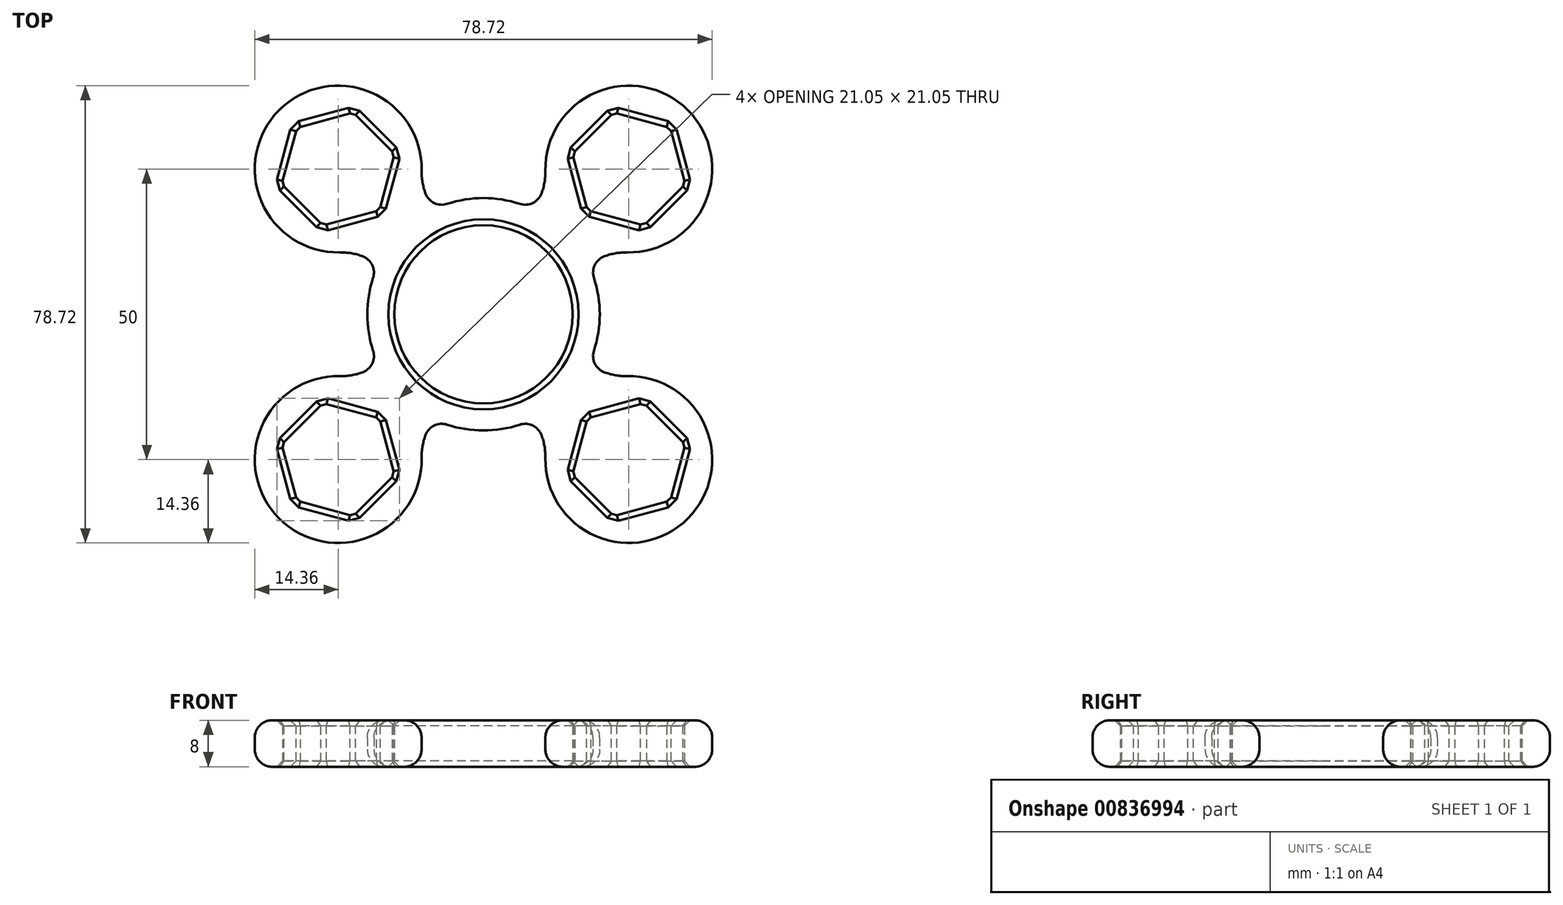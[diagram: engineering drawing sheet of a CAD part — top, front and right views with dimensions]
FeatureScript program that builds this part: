
annotation { "Feature Type Name" : "Feature", "Feature Type Description" : "" }
export const myFeature = defineFeature(function(context is Context, id is Id, definition is map)
    precondition{}
    {
        {
            var Q0;
            Q0=qCreatedBy(makeId("Top.planeOp"),FACE);
            var sketch = newSketch(context, id + "F0", { "sketchPlane" : qUnion([Q0])});
            skCircle(sketch, "E0", {"center": v(0, 0) * mm, "radius": 15.35 * mm});
            skLineSegment(sketch, "E1.1", {"start": v(35.15, -14.85) * mm, "end": v(14.85, -35.15) * mm, "construction": true});
            skLineSegment(sketch, "E1.2", {"start": v(-14.85, -35.15) * mm, "end": v(-35.15, -14.85) * mm, "construction": true});
            skLineSegment(sketch, "E1.3", {"start": v(-35.15, 14.85) * mm, "end": v(-17.9, 32.1) * mm, "construction": true});
            skArc(sketch, "E2", {"start": v(-18.1, 8.51) * mm, "mid": v(-20, 0) * mm, "end": v(-18.1, -8.51) * mm});
            skLineSegment(sketch, "E3", {"start": v(-25, 25) * mm, "end": v(-17.9, 17.9) * mm, "construction": true});
            skLineSegment(sketch, "E4", {"start": v(-25, -25) * mm, "end": v(-17.9, -17.9) * mm, "construction": true});
            skCircle(sketch, "E5.cCircle", {"center": v(-25, 25) * mm, "radius": 10.05 * mm, "construction": true});
            skLineSegment(sketch, "E5.0", {"start": v(-17.9, 17.9) * mm, "end": v(-27.6, 15.3) * mm});
            skLineSegment(sketch, "E5.1", {"start": v(-27.6, 15.3) * mm, "end": v(-34.7, 22.4) * mm});
            skLineSegment(sketch, "E5.2", {"start": v(-34.7, 22.4) * mm, "end": v(-32.1, 32.1) * mm});
            skLineSegment(sketch, "E5.3", {"start": v(-32.1, 32.1) * mm, "end": v(-22.4, 34.7) * mm});
            skLineSegment(sketch, "E5.4", {"start": v(-22.4, 34.7) * mm, "end": v(-15.3, 27.6) * mm});
            skLineSegment(sketch, "E5.5", {"start": v(-15.3, 27.6) * mm, "end": v(-17.9, 17.9) * mm});
            skCircle(sketch, "E6.cCircle", {"center": v(-25, -25) * mm, "radius": 10.05 * mm, "construction": true});
            skLineSegment(sketch, "E6.0", {"start": v(-17.9, -17.9) * mm, "end": v(-15.3, -27.6) * mm});
            skLineSegment(sketch, "E6.1", {"start": v(-15.3, -27.6) * mm, "end": v(-22.4, -34.7) * mm});
            skLineSegment(sketch, "E6.2", {"start": v(-22.4, -34.7) * mm, "end": v(-32.1, -32.1) * mm});
            skLineSegment(sketch, "E6.3", {"start": v(-32.1, -32.1) * mm, "end": v(-34.7, -22.4) * mm});
            skLineSegment(sketch, "E6.4", {"start": v(-34.7, -22.4) * mm, "end": v(-27.6, -15.3) * mm});
            skLineSegment(sketch, "E6.5", {"start": v(-27.6, -15.3) * mm, "end": v(-17.9, -17.9) * mm});
            skCircle(sketch, "E7.cCircle", {"center": v(25, -25) * mm, "radius": 10.05 * mm, "construction": true});
            skLineSegment(sketch, "E7.0", {"start": v(17.9, -17.9) * mm, "end": v(27.6, -15.3) * mm});
            skLineSegment(sketch, "E7.1", {"start": v(27.6, -15.3) * mm, "end": v(34.7, -22.4) * mm});
            skLineSegment(sketch, "E7.2", {"start": v(34.7, -22.4) * mm, "end": v(32.1, -32.1) * mm});
            skLineSegment(sketch, "E7.3", {"start": v(32.1, -32.1) * mm, "end": v(22.4, -34.7) * mm});
            skLineSegment(sketch, "E7.4", {"start": v(22.4, -34.7) * mm, "end": v(15.3, -27.6) * mm});
            skLineSegment(sketch, "E7.5", {"start": v(15.3, -27.6) * mm, "end": v(17.9, -17.9) * mm});
            skArc(sketch, "E8.cCircle", {"start": v(34.7, 22.4) * mm, "mid": v(17.9, 32.1) * mm, "end": v(27.6, 15.3) * mm, "construction": true});
            skLineSegment(sketch, "E8.0", {"start": v(17.9, 17.9) * mm, "end": v(15.3, 27.6) * mm});
            skLineSegment(sketch, "E8.1", {"start": v(15.3, 27.6) * mm, "end": v(22.4, 34.7) * mm});
            skLineSegment(sketch, "E8.2", {"start": v(22.4, 34.7) * mm, "end": v(32.1, 32.1) * mm});
            skLineSegment(sketch, "E8.3", {"start": v(32.1, 32.1) * mm, "end": v(34.7, 22.4) * mm});
            skLineSegment(sketch, "E8.4", {"start": v(34.7, 22.4) * mm, "end": v(27.6, 15.3) * mm});
            skLineSegment(sketch, "E8.5", {"start": v(27.6, 15.3) * mm, "end": v(17.9, 17.9) * mm});
            skArc(sketch, "E9", {"start": v(24.71, 10.65) * mm, "mid": v(35.15, 35.15) * mm, "end": v(10.65, 24.71) * mm});
            skArc(sketch, "E10", {"start": v(10.65, -24.71) * mm, "mid": v(35.15, -35.15) * mm, "end": v(24.71, -10.65) * mm});
            skArc(sketch, "E11", {"start": v(-24.71, -10.65) * mm, "mid": v(-35.15, -35.15) * mm, "end": v(-10.65, -24.71) * mm});
            skArc(sketch, "E12", {"start": v(-10.65, 24.71) * mm, "mid": v(-35.15, 35.15) * mm, "end": v(-24.71, 10.65) * mm});
            skArc(sketch, "E13", {"start": v(8.51, 18.1) * mm, "mid": v(10.13, 21.23) * mm, "end": v(10.65, 24.71) * mm});
            skArc(sketch, "E14", {"start": v(-24.71, -10.65) * mm, "mid": v(-21.23, -10.13) * mm, "end": v(-18.1, -8.51) * mm});
            skArc(sketch, "E15", {"start": v(-8.51, -18.1) * mm, "mid": v(-10.13, -21.23) * mm, "end": v(-10.65, -24.71) * mm});
            skArc(sketch, "E16", {"start": v(24.71, 10.65) * mm, "mid": v(21.23, 10.13) * mm, "end": v(18.1, 8.51) * mm});
            skPoint(sketch, "E17.center.orphan", {"position": v(-50, 0) * mm});
            skPoint(sketch, "E18.orphan", {"position": v(-29, 0) * mm});
            skArc(sketch, "E19.trimOffspring", {"start": v(-18.1, 8.51) * mm, "mid": v(-21.23, 10.13) * mm, "end": v(-24.71, 10.65) * mm});
            skArc(sketch, "E20.trimOffspring", {"start": v(-8.51, -18.1) * mm, "mid": v(0, -20) * mm, "end": v(8.51, -18.1) * mm});
            skPoint(sketch, "E21.start.orphan", {"position": v(0, -29) * mm});
            skPoint(sketch, "E22.center.orphan", {"position": v(0, -50) * mm});
            skArc(sketch, "E23.trimOffspring", {"start": v(10.65, -24.71) * mm, "mid": v(10.13, -21.23) * mm, "end": v(8.51, -18.1) * mm});
            skPoint(sketch, "E24.start.orphan", {"position": v(0, -20) * mm});
            skLineSegment(sketch, "E25.trimOffspring", {"start": v(17.9, -17.9) * mm, "end": v(25, -25) * mm, "construction": true});
            skArc(sketch, "E26.trimOffspring", {"start": v(18.1, -8.51) * mm, "mid": v(20, 0) * mm, "end": v(18.1, 8.51) * mm});
            skArc(sketch, "E27.trimOffspring", {"start": v(-10.65, 24.71) * mm, "mid": v(-10.13, 21.23) * mm, "end": v(-8.51, 18.1) * mm});
            skPoint(sketch, "E28.orphan", {"position": v(0, 29) * mm});
            skPoint(sketch, "E29.start.orphan", {"position": v(0, 20) * mm});
            skPoint(sketch, "E30.center.orphan", {"position": v(0, 50) * mm});
            skArc(sketch, "E31.trimOffspring", {"start": v(8.51, 18.1) * mm, "mid": v(0, 20) * mm, "end": v(-8.51, 18.1) * mm});
            skPoint(sketch, "E32.center.orphan", {"position": v(50, 0) * mm});
            skPoint(sketch, "E33.start.orphan", {"position": v(20, 0) * mm});
            skArc(sketch, "E34.trimOffspring", {"start": v(18.1, -8.51) * mm, "mid": v(21.23, -10.13) * mm, "end": v(24.71, -10.65) * mm});
            skPoint(sketch, "E35.start.orphan", {"position": v(29, 0) * mm});
            skPoint(sketch, "E36.start.orphan", {"position": v(-20, 0) * mm});
            skSolve(sketch);
        }
        {
            var Q0;
            Q0 = qSketchRegion(id + "F0", true);
            extrude(context, id + "F1", {"entities" : qUnion([Q0]), "depth" : 8 * mm, "offsetDistance" : 25 * mm});
        }
        {
            var Q0;
            Q0=makeQuery(id+"F1.opExtrude","CAP_EDGE",EDGE,{"disambiguationData":[OSD([sQuery(id+"F0.wireOp",EDGE,"E12")])],"isStart":false});
            var Q1;
            Q1=makeQuery(id+"F1.opExtrude","CAP_EDGE",EDGE,{"disambiguationData":[OSD([sQuery(id+"F0.wireOp",EDGE,"E11")])],"isStart":false});
            var Q2;
            Q2=makeQuery(id+"F1.opExtrude","CAP_EDGE",EDGE,{"disambiguationData":[OSD([sQuery(id+"F0.wireOp",EDGE,"E10")])],"isStart":false});
            var Q3;
            Q3=makeQuery(id+"F1.opExtrude","CAP_EDGE",EDGE,{"disambiguationData":[OSD([sQuery(id+"F0.wireOp",EDGE,"E9")])],"isStart":false});
            var Q4;
            Q4=makeQuery(id+"F1.opExtrude","CAP_EDGE",EDGE,{"disambiguationData":[OSD([sQuery(id+"F0.wireOp",EDGE,"E26.trimOffspring")])],"isStart":false});
            var Q5;
            Q5=makeQuery(id+"F1.opExtrude","CAP_EDGE",EDGE,{"disambiguationData":[OSD([sQuery(id+"F0.wireOp",EDGE,"E31.trimOffspring")])],"isStart":false});
            var Q6;
            Q6=makeQuery(id+"F1.opExtrude","CAP_EDGE",EDGE,{"disambiguationData":[OSD([sQuery(id+"F0.wireOp",EDGE,"E2")])],"isStart":false});
            var Q7;
            Q7=makeQuery(id+"F1.opExtrude","CAP_EDGE",EDGE,{"disambiguationData":[OSD([sQuery(id+"F0.wireOp",EDGE,"E20.trimOffspring")])],"isStart":true});
            var Q8;
            Q8=makeQuery(id+"F1.opExtrude","CAP_EDGE",EDGE,{"disambiguationData":[OSD([sQuery(id+"F0.wireOp",EDGE,"E20.trimOffspring")])],"isStart":false});
            var Q9;
            Q9=makeQuery(id+"F1.opExtrude","CAP_EDGE",EDGE,{"disambiguationData":[OSD([sQuery(id+"F0.wireOp",EDGE,"E11")])],"isStart":true});
            var Q10;
            Q10=makeQuery(id+"F1.opExtrude","CAP_EDGE",EDGE,{"disambiguationData":[OSD([sQuery(id+"F0.wireOp",EDGE,"E2")])],"isStart":true});
            var Q11;
            Q11=makeQuery(id+"F1.opExtrude","CAP_EDGE",EDGE,{"disambiguationData":[OSD([sQuery(id+"F0.wireOp",EDGE,"E12")])],"isStart":true});
            var Q12;
            Q12=makeQuery(id+"F1.opExtrude","SWEPT_EDGE",EDGE,{"disambiguationData":[OSD([sQuery(id+"F0.wireOp",EDGE,"E2"),sQuery(id+"F0.wireOp",EDGE,"E14")])]});
            var Q13;
            Q13=makeQuery(id+"F1.opExtrude","SWEPT_EDGE",EDGE,{"disambiguationData":[OSD([sQuery(id+"F0.wireOp",EDGE,"E2"),sQuery(id+"F0.wireOp",EDGE,"E19.trimOffspring")])]});
            var Q14;
            Q14=makeQuery(id+"F1.opExtrude","CAP_EDGE",EDGE,{"disambiguationData":[OSD([sQuery(id+"F0.wireOp",EDGE,"E9")])],"isStart":true});
            var Q15;
            Q15=makeQuery(id+"F1.opExtrude","CAP_EDGE",EDGE,{"disambiguationData":[OSD([sQuery(id+"F0.wireOp",EDGE,"E10")])],"isStart":true});
            var Q16;
            Q16=makeQuery(id+"F1.opExtrude","CAP_EDGE",EDGE,{"disambiguationData":[OSD([sQuery(id+"F0.wireOp",EDGE,"E26.trimOffspring")])],"isStart":true});
            var Q17;
            Q17=makeQuery(id+"F1.opExtrude","CAP_EDGE",EDGE,{"disambiguationData":[OSD([sQuery(id+"F0.wireOp",EDGE,"E31.trimOffspring")])],"isStart":true});
            var Q18;
            Q18=makeQuery(id+"F1.opExtrude","SWEPT_EDGE",EDGE,{"disambiguationData":[OSD([sQuery(id+"F0.wireOp",EDGE,"E13"),sQuery(id+"F0.wireOp",EDGE,"E31.trimOffspring")])]});
            var Q19;
            Q19=makeQuery(id+"F1.opExtrude","SWEPT_EDGE",EDGE,{"disambiguationData":[OSD([sQuery(id+"F0.wireOp",EDGE,"E16"),sQuery(id+"F0.wireOp",EDGE,"E26.trimOffspring")])]});
            var Q20;
            Q20=makeQuery(id+"F1.opExtrude","SWEPT_EDGE",EDGE,{"disambiguationData":[OSD([sQuery(id+"F0.wireOp",EDGE,"E26.trimOffspring"),sQuery(id+"F0.wireOp",EDGE,"E34.trimOffspring")])]});
            var Q21;
            Q21=makeQuery(id+"F1.opExtrude","SWEPT_EDGE",EDGE,{"disambiguationData":[OSD([sQuery(id+"F0.wireOp",EDGE,"E20.trimOffspring"),sQuery(id+"F0.wireOp",EDGE,"E23.trimOffspring")])]});
            var Q22;
            Q22=makeQuery(id+"F1.opExtrude","SWEPT_EDGE",EDGE,{"disambiguationData":[OSD([sQuery(id+"F0.wireOp",EDGE,"E15"),sQuery(id+"F0.wireOp",EDGE,"E20.trimOffspring")])]});
            var Q23;
            Q23=makeQuery(id+"F1.opExtrude","SWEPT_EDGE",EDGE,{"disambiguationData":[OSD([sQuery(id+"F0.wireOp",EDGE,"E27.trimOffspring"),sQuery(id+"F0.wireOp",EDGE,"E31.trimOffspring")])]});
            fillet(context, id + "F2", {"entities" : qUnion([Q0, Q1, Q2, Q3, Q4, Q5, Q6, Q7, Q8, Q9, Q10, Q11, Q12, Q13, Q14, Q15, Q16, Q17, Q18, Q19, Q20, Q21, Q22, Q23]), "radius" : 3 * mm, "tangentPropagation" : true, "allowEdgeOverflow" : false});
        }
        {
            var Q0;
            Q0=makeQuery(id+"F1.opExtrude","CAP_EDGE",EDGE,{"disambiguationData":[OSD([sQuery(id+"F0.wireOp",EDGE,"E5.2")])],"isStart":false});
            var Q1;
            Q1=makeQuery(id+"F1.opExtrude","CAP_EDGE",EDGE,{"disambiguationData":[OSD([sQuery(id+"F0.wireOp",EDGE,"E5.3")])],"isStart":false});
            var Q2;
            Q2=makeQuery(id+"F1.opExtrude","CAP_EDGE",EDGE,{"disambiguationData":[OSD([sQuery(id+"F0.wireOp",EDGE,"E5.4")])],"isStart":false});
            var Q3;
            Q3=makeQuery(id+"F1.opExtrude","CAP_EDGE",EDGE,{"disambiguationData":[OSD([sQuery(id+"F0.wireOp",EDGE,"E5.5")])],"isStart":false});
            var Q4;
            Q4=makeQuery(id+"F1.opExtrude","CAP_EDGE",EDGE,{"disambiguationData":[OSD([sQuery(id+"F0.wireOp",EDGE,"E5.0")])],"isStart":false});
            var Q5;
            Q5=makeQuery(id+"F1.opExtrude","CAP_EDGE",EDGE,{"disambiguationData":[OSD([sQuery(id+"F0.wireOp",EDGE,"E5.1")])],"isStart":false});
            var Q6;
            Q6=makeQuery(id+"F1.opExtrude","CAP_EDGE",EDGE,{"disambiguationData":[OSD([sQuery(id+"F0.wireOp",EDGE,"E8.0")])],"isStart":false});
            var Q7;
            Q7=makeQuery(id+"F1.opExtrude","CAP_EDGE",EDGE,{"disambiguationData":[OSD([sQuery(id+"F0.wireOp",EDGE,"E8.1")])],"isStart":false});
            var Q8;
            Q8=makeQuery(id+"F1.opExtrude","CAP_EDGE",EDGE,{"disambiguationData":[OSD([sQuery(id+"F0.wireOp",EDGE,"E8.2")])],"isStart":false});
            var Q9;
            Q9=makeQuery(id+"F1.opExtrude","CAP_EDGE",EDGE,{"disambiguationData":[OSD([sQuery(id+"F0.wireOp",EDGE,"E8.3")])],"isStart":false});
            var Q10;
            Q10=makeQuery(id+"F1.opExtrude","CAP_EDGE",EDGE,{"disambiguationData":[OSD([sQuery(id+"F0.wireOp",EDGE,"E8.4")])],"isStart":false});
            var Q11;
            Q11=makeQuery(id+"F1.opExtrude","CAP_EDGE",EDGE,{"disambiguationData":[OSD([sQuery(id+"F0.wireOp",EDGE,"E8.5")])],"isStart":false});
            var Q12;
            Q12=makeQuery(id+"F1.opExtrude","CAP_EDGE",EDGE,{"disambiguationData":[OSD([sQuery(id+"F0.wireOp",EDGE,"E0")])],"isStart":false});
            var Q13;
            Q13=makeQuery(id+"F1.opExtrude","CAP_EDGE",EDGE,{"disambiguationData":[OSD([sQuery(id+"F0.wireOp",EDGE,"E7.0")])],"isStart":false});
            var Q14;
            Q14=makeQuery(id+"F1.opExtrude","CAP_EDGE",EDGE,{"disambiguationData":[OSD([sQuery(id+"F0.wireOp",EDGE,"E7.5")])],"isStart":false});
            var Q15;
            Q15=makeQuery(id+"F1.opExtrude","CAP_EDGE",EDGE,{"disambiguationData":[OSD([sQuery(id+"F0.wireOp",EDGE,"E7.4")])],"isStart":false});
            var Q16;
            Q16=makeQuery(id+"F1.opExtrude","CAP_EDGE",EDGE,{"disambiguationData":[OSD([sQuery(id+"F0.wireOp",EDGE,"E7.3")])],"isStart":false});
            var Q17;
            Q17=makeQuery(id+"F1.opExtrude","CAP_EDGE",EDGE,{"disambiguationData":[OSD([sQuery(id+"F0.wireOp",EDGE,"E7.2")])],"isStart":false});
            var Q18;
            Q18=makeQuery(id+"F1.opExtrude","CAP_EDGE",EDGE,{"disambiguationData":[OSD([sQuery(id+"F0.wireOp",EDGE,"E7.1")])],"isStart":false});
            var Q19;
            Q19=makeQuery(id+"F1.opExtrude","CAP_EDGE",EDGE,{"disambiguationData":[OSD([sQuery(id+"F0.wireOp",EDGE,"E6.5")])],"isStart":false});
            var Q20;
            Q20=makeQuery(id+"F1.opExtrude","CAP_EDGE",EDGE,{"disambiguationData":[OSD([sQuery(id+"F0.wireOp",EDGE,"E6.0")])],"isStart":false});
            var Q21;
            Q21=makeQuery(id+"F1.opExtrude","CAP_EDGE",EDGE,{"disambiguationData":[OSD([sQuery(id+"F0.wireOp",EDGE,"E6.4")])],"isStart":false});
            var Q22;
            Q22=makeQuery(id+"F1.opExtrude","CAP_EDGE",EDGE,{"disambiguationData":[OSD([sQuery(id+"F0.wireOp",EDGE,"E6.3")])],"isStart":false});
            var Q23;
            Q23=makeQuery(id+"F1.opExtrude","CAP_EDGE",EDGE,{"disambiguationData":[OSD([sQuery(id+"F0.wireOp",EDGE,"E6.2")])],"isStart":false});
            var Q24;
            Q24=makeQuery(id+"F1.opExtrude","CAP_EDGE",EDGE,{"disambiguationData":[OSD([sQuery(id+"F0.wireOp",EDGE,"E6.1")])],"isStart":false});
            var Q25;
            Q25=makeQuery(id+"F1.opExtrude","CAP_EDGE",EDGE,{"disambiguationData":[OSD([sQuery(id+"F0.wireOp",EDGE,"E7.0")])],"isStart":true});
            var Q26;
            Q26=makeQuery(id+"F1.opExtrude","CAP_EDGE",EDGE,{"disambiguationData":[OSD([sQuery(id+"F0.wireOp",EDGE,"E7.5")])],"isStart":true});
            var Q27;
            Q27=makeQuery(id+"F1.opExtrude","CAP_EDGE",EDGE,{"disambiguationData":[OSD([sQuery(id+"F0.wireOp",EDGE,"E7.4")])],"isStart":true});
            var Q28;
            Q28=makeQuery(id+"F1.opExtrude","CAP_EDGE",EDGE,{"disambiguationData":[OSD([sQuery(id+"F0.wireOp",EDGE,"E7.3")])],"isStart":true});
            var Q29;
            Q29=makeQuery(id+"F1.opExtrude","CAP_EDGE",EDGE,{"disambiguationData":[OSD([sQuery(id+"F0.wireOp",EDGE,"E7.2")])],"isStart":true});
            var Q30;
            Q30=makeQuery(id+"F1.opExtrude","CAP_EDGE",EDGE,{"disambiguationData":[OSD([sQuery(id+"F0.wireOp",EDGE,"E7.1")])],"isStart":true});
            var Q31;
            Q31=makeQuery(id+"F1.opExtrude","CAP_EDGE",EDGE,{"disambiguationData":[OSD([sQuery(id+"F0.wireOp",EDGE,"E8.4")])],"isStart":true});
            var Q32;
            Q32=makeQuery(id+"F1.opExtrude","CAP_EDGE",EDGE,{"disambiguationData":[OSD([sQuery(id+"F0.wireOp",EDGE,"E8.5")])],"isStart":true});
            var Q33;
            Q33=makeQuery(id+"F1.opExtrude","CAP_EDGE",EDGE,{"disambiguationData":[OSD([sQuery(id+"F0.wireOp",EDGE,"E8.0")])],"isStart":true});
            var Q34;
            Q34=makeQuery(id+"F1.opExtrude","CAP_EDGE",EDGE,{"disambiguationData":[OSD([sQuery(id+"F0.wireOp",EDGE,"E8.1")])],"isStart":true});
            var Q35;
            Q35=makeQuery(id+"F1.opExtrude","CAP_EDGE",EDGE,{"disambiguationData":[OSD([sQuery(id+"F0.wireOp",EDGE,"E8.2")])],"isStart":true});
            var Q36;
            Q36=makeQuery(id+"F1.opExtrude","CAP_EDGE",EDGE,{"disambiguationData":[OSD([sQuery(id+"F0.wireOp",EDGE,"E8.3")])],"isStart":true});
            var Q37;
            Q37=makeQuery(id+"F1.opExtrude","CAP_EDGE",EDGE,{"disambiguationData":[OSD([sQuery(id+"F0.wireOp",EDGE,"E5.0")])],"isStart":true});
            var Q38;
            Q38=makeQuery(id+"F1.opExtrude","CAP_EDGE",EDGE,{"disambiguationData":[OSD([sQuery(id+"F0.wireOp",EDGE,"E5.5")])],"isStart":true});
            var Q39;
            Q39=makeQuery(id+"F1.opExtrude","CAP_EDGE",EDGE,{"disambiguationData":[OSD([sQuery(id+"F0.wireOp",EDGE,"E5.4")])],"isStart":true});
            var Q40;
            Q40=makeQuery(id+"F1.opExtrude","CAP_EDGE",EDGE,{"disambiguationData":[OSD([sQuery(id+"F0.wireOp",EDGE,"E5.3")])],"isStart":true});
            var Q41;
            Q41=makeQuery(id+"F1.opExtrude","CAP_EDGE",EDGE,{"disambiguationData":[OSD([sQuery(id+"F0.wireOp",EDGE,"E5.2")])],"isStart":true});
            var Q42;
            Q42=makeQuery(id+"F1.opExtrude","CAP_EDGE",EDGE,{"disambiguationData":[OSD([sQuery(id+"F0.wireOp",EDGE,"E5.1")])],"isStart":true});
            var Q43;
            Q43=makeQuery(id+"F1.opExtrude","CAP_EDGE",EDGE,{"disambiguationData":[OSD([sQuery(id+"F0.wireOp",EDGE,"E0")])],"isStart":true});
            var Q44;
            Q44=makeQuery(id+"F1.opExtrude","CAP_EDGE",EDGE,{"disambiguationData":[OSD([sQuery(id+"F0.wireOp",EDGE,"E6.5")])],"isStart":true});
            var Q45;
            Q45=makeQuery(id+"F1.opExtrude","CAP_EDGE",EDGE,{"disambiguationData":[OSD([sQuery(id+"F0.wireOp",EDGE,"E6.4")])],"isStart":true});
            var Q46;
            Q46=makeQuery(id+"F1.opExtrude","CAP_EDGE",EDGE,{"disambiguationData":[OSD([sQuery(id+"F0.wireOp",EDGE,"E6.3")])],"isStart":true});
            var Q47;
            Q47=makeQuery(id+"F1.opExtrude","CAP_EDGE",EDGE,{"disambiguationData":[OSD([sQuery(id+"F0.wireOp",EDGE,"E6.2")])],"isStart":true});
            var Q48;
            Q48=makeQuery(id+"F1.opExtrude","CAP_EDGE",EDGE,{"disambiguationData":[OSD([sQuery(id+"F0.wireOp",EDGE,"E6.1")])],"isStart":true});
            var Q49;
            Q49=makeQuery(id+"F1.opExtrude","CAP_EDGE",EDGE,{"disambiguationData":[OSD([sQuery(id+"F0.wireOp",EDGE,"E6.0")])],"isStart":true});
            var Q50;
            {var subQ0=sQuery(id+"F0.wireOp",EDGE,"E9");Q50=makeQuery(id+"F2.opFillet","BLEND_EDGE",EDGE,{"blendedFrom":[makeQuery(id+"F1.opExtrude","CAP_EDGE",EDGE,{"disambiguationData":[OSD([subQ0])],"isStart":true}),makeQuery(id+"F1.opExtrude","CAP_FACE",FACE,{"disambiguationData":[OSD([sQuery(id+"F0.wireOp",EDGE,"E0"),sQuery(id+"F0.wireOp",EDGE,"E2"),sQuery(id+"F0.wireOp",EDGE,"E5.0"),sQuery(id+"F0.wireOp",EDGE,"E5.1"),sQuery(id+"F0.wireOp",EDGE,"E5.2"),sQuery(id+"F0.wireOp",EDGE,"E5.3"),sQuery(id+"F0.wireOp",EDGE,"E5.4"),sQuery(id+"F0.wireOp",EDGE,"E5.5"),sQuery(id+"F0.wireOp",EDGE,"E6.0"),sQuery(id+"F0.wireOp",EDGE,"E6.1"),sQuery(id+"F0.wireOp",EDGE,"E6.2"),sQuery(id+"F0.wireOp",EDGE,"E6.3"),sQuery(id+"F0.wireOp",EDGE,"E6.4"),sQuery(id+"F0.wireOp",EDGE,"E6.5"),sQuery(id+"F0.wireOp",EDGE,"E7.0"),sQuery(id+"F0.wireOp",EDGE,"E7.1"),sQuery(id+"F0.wireOp",EDGE,"E7.2"),sQuery(id+"F0.wireOp",EDGE,"E7.3"),sQuery(id+"F0.wireOp",EDGE,"E7.4"),sQuery(id+"F0.wireOp",EDGE,"E7.5"),sQuery(id+"F0.wireOp",EDGE,"E8.0"),sQuery(id+"F0.wireOp",EDGE,"E8.1"),sQuery(id+"F0.wireOp",EDGE,"E8.2"),sQuery(id+"F0.wireOp",EDGE,"E8.3"),sQuery(id+"F0.wireOp",EDGE,"E8.4"),sQuery(id+"F0.wireOp",EDGE,"E8.5"),subQ0,sQuery(id+"F0.wireOp",EDGE,"E10"),sQuery(id+"F0.wireOp",EDGE,"E11"),sQuery(id+"F0.wireOp",EDGE,"E12"),sQuery(id+"F0.wireOp",EDGE,"E13"),sQuery(id+"F0.wireOp",EDGE,"E14"),sQuery(id+"F0.wireOp",EDGE,"E15"),sQuery(id+"F0.wireOp",EDGE,"E16"),sQuery(id+"F0.wireOp",EDGE,"E19.trimOffspring"),sQuery(id+"F0.wireOp",EDGE,"E20.trimOffspring"),sQuery(id+"F0.wireOp",EDGE,"E23.trimOffspring"),sQuery(id+"F0.wireOp",EDGE,"E26.trimOffspring"),sQuery(id+"F0.wireOp",EDGE,"E27.trimOffspring"),sQuery(id+"F0.wireOp",EDGE,"E31.trimOffspring"),sQuery(id+"F0.wireOp",EDGE,"E34.trimOffspring")])],"isStart":true})],"blendedInto":[makeQuery(id+"F1.opExtrude","CAP_FACE",FACE,{"disambiguationData":[OSD([sQuery(id+"F0.wireOp",EDGE,"E0"),sQuery(id+"F0.wireOp",EDGE,"E2"),sQuery(id+"F0.wireOp",EDGE,"E5.0"),sQuery(id+"F0.wireOp",EDGE,"E5.1"),sQuery(id+"F0.wireOp",EDGE,"E5.2"),sQuery(id+"F0.wireOp",EDGE,"E5.3"),sQuery(id+"F0.wireOp",EDGE,"E5.4"),sQuery(id+"F0.wireOp",EDGE,"E5.5"),sQuery(id+"F0.wireOp",EDGE,"E6.0"),sQuery(id+"F0.wireOp",EDGE,"E6.1"),sQuery(id+"F0.wireOp",EDGE,"E6.2"),sQuery(id+"F0.wireOp",EDGE,"E6.3"),sQuery(id+"F0.wireOp",EDGE,"E6.4"),sQuery(id+"F0.wireOp",EDGE,"E6.5"),sQuery(id+"F0.wireOp",EDGE,"E7.0"),sQuery(id+"F0.wireOp",EDGE,"E7.1"),sQuery(id+"F0.wireOp",EDGE,"E7.2"),sQuery(id+"F0.wireOp",EDGE,"E7.3"),sQuery(id+"F0.wireOp",EDGE,"E7.4"),sQuery(id+"F0.wireOp",EDGE,"E7.5"),sQuery(id+"F0.wireOp",EDGE,"E8.0"),sQuery(id+"F0.wireOp",EDGE,"E8.1"),sQuery(id+"F0.wireOp",EDGE,"E8.2"),sQuery(id+"F0.wireOp",EDGE,"E8.3"),sQuery(id+"F0.wireOp",EDGE,"E8.4"),sQuery(id+"F0.wireOp",EDGE,"E8.5"),subQ0,sQuery(id+"F0.wireOp",EDGE,"E10"),sQuery(id+"F0.wireOp",EDGE,"E11"),sQuery(id+"F0.wireOp",EDGE,"E12"),sQuery(id+"F0.wireOp",EDGE,"E13"),sQuery(id+"F0.wireOp",EDGE,"E14"),sQuery(id+"F0.wireOp",EDGE,"E15"),sQuery(id+"F0.wireOp",EDGE,"E16"),sQuery(id+"F0.wireOp",EDGE,"E19.trimOffspring"),sQuery(id+"F0.wireOp",EDGE,"E20.trimOffspring"),sQuery(id+"F0.wireOp",EDGE,"E23.trimOffspring"),sQuery(id+"F0.wireOp",EDGE,"E26.trimOffspring"),sQuery(id+"F0.wireOp",EDGE,"E27.trimOffspring"),sQuery(id+"F0.wireOp",EDGE,"E31.trimOffspring"),sQuery(id+"F0.wireOp",EDGE,"E34.trimOffspring")])],"isStart":true})]});}
            var Q51;
            {var subQ0=sQuery(id+"F0.wireOp",EDGE,"E9");Q51=makeQuery(id+"F2.opFillet","BLEND_EDGE",EDGE,{"blendedFrom":[makeQuery(id+"F1.opExtrude","CAP_EDGE",EDGE,{"disambiguationData":[OSD([subQ0])],"isStart":true}),makeQuery(id+"F1.opExtrude","SWEPT_FACE",FACE,{"disambiguationData":[OSD([subQ0])]})],"blendedInto":[makeQuery(id+"F1.opExtrude","SWEPT_FACE",FACE,{"disambiguationData":[OSD([subQ0])]})]});}
            var Q52;
            {var subQ0=sQuery(id+"F0.wireOp",EDGE,"E11");Q52=makeQuery(id+"F2.opFillet","BLEND_EDGE",EDGE,{"blendedFrom":[makeQuery(id+"F1.opExtrude","CAP_EDGE",EDGE,{"disambiguationData":[OSD([subQ0])],"isStart":true}),makeQuery(id+"F1.opExtrude","SWEPT_FACE",FACE,{"disambiguationData":[OSD([subQ0])]})],"blendedInto":[makeQuery(id+"F1.opExtrude","SWEPT_FACE",FACE,{"disambiguationData":[OSD([subQ0])]})]});}
            var Q53;
            {var subQ0=sQuery(id+"F0.wireOp",EDGE,"E11");Q53=makeQuery(id+"F2.opFillet","BLEND_EDGE",EDGE,{"blendedFrom":[makeQuery(id+"F1.opExtrude","CAP_EDGE",EDGE,{"disambiguationData":[OSD([subQ0])],"isStart":true}),makeQuery(id+"F1.opExtrude","CAP_FACE",FACE,{"disambiguationData":[OSD([sQuery(id+"F0.wireOp",EDGE,"E0"),sQuery(id+"F0.wireOp",EDGE,"E2"),sQuery(id+"F0.wireOp",EDGE,"E5.0"),sQuery(id+"F0.wireOp",EDGE,"E5.1"),sQuery(id+"F0.wireOp",EDGE,"E5.2"),sQuery(id+"F0.wireOp",EDGE,"E5.3"),sQuery(id+"F0.wireOp",EDGE,"E5.4"),sQuery(id+"F0.wireOp",EDGE,"E5.5"),sQuery(id+"F0.wireOp",EDGE,"E6.0"),sQuery(id+"F0.wireOp",EDGE,"E6.1"),sQuery(id+"F0.wireOp",EDGE,"E6.2"),sQuery(id+"F0.wireOp",EDGE,"E6.3"),sQuery(id+"F0.wireOp",EDGE,"E6.4"),sQuery(id+"F0.wireOp",EDGE,"E6.5"),sQuery(id+"F0.wireOp",EDGE,"E7.0"),sQuery(id+"F0.wireOp",EDGE,"E7.1"),sQuery(id+"F0.wireOp",EDGE,"E7.2"),sQuery(id+"F0.wireOp",EDGE,"E7.3"),sQuery(id+"F0.wireOp",EDGE,"E7.4"),sQuery(id+"F0.wireOp",EDGE,"E7.5"),sQuery(id+"F0.wireOp",EDGE,"E8.0"),sQuery(id+"F0.wireOp",EDGE,"E8.1"),sQuery(id+"F0.wireOp",EDGE,"E8.2"),sQuery(id+"F0.wireOp",EDGE,"E8.3"),sQuery(id+"F0.wireOp",EDGE,"E8.4"),sQuery(id+"F0.wireOp",EDGE,"E8.5"),sQuery(id+"F0.wireOp",EDGE,"E9"),sQuery(id+"F0.wireOp",EDGE,"E10"),subQ0,sQuery(id+"F0.wireOp",EDGE,"E12"),sQuery(id+"F0.wireOp",EDGE,"E13"),sQuery(id+"F0.wireOp",EDGE,"E14"),sQuery(id+"F0.wireOp",EDGE,"E15"),sQuery(id+"F0.wireOp",EDGE,"E16"),sQuery(id+"F0.wireOp",EDGE,"E19.trimOffspring"),sQuery(id+"F0.wireOp",EDGE,"E20.trimOffspring"),sQuery(id+"F0.wireOp",EDGE,"E23.trimOffspring"),sQuery(id+"F0.wireOp",EDGE,"E26.trimOffspring"),sQuery(id+"F0.wireOp",EDGE,"E27.trimOffspring"),sQuery(id+"F0.wireOp",EDGE,"E31.trimOffspring"),sQuery(id+"F0.wireOp",EDGE,"E34.trimOffspring")])],"isStart":true})],"blendedInto":[makeQuery(id+"F1.opExtrude","CAP_FACE",FACE,{"disambiguationData":[OSD([sQuery(id+"F0.wireOp",EDGE,"E0"),sQuery(id+"F0.wireOp",EDGE,"E2"),sQuery(id+"F0.wireOp",EDGE,"E5.0"),sQuery(id+"F0.wireOp",EDGE,"E5.1"),sQuery(id+"F0.wireOp",EDGE,"E5.2"),sQuery(id+"F0.wireOp",EDGE,"E5.3"),sQuery(id+"F0.wireOp",EDGE,"E5.4"),sQuery(id+"F0.wireOp",EDGE,"E5.5"),sQuery(id+"F0.wireOp",EDGE,"E6.0"),sQuery(id+"F0.wireOp",EDGE,"E6.1"),sQuery(id+"F0.wireOp",EDGE,"E6.2"),sQuery(id+"F0.wireOp",EDGE,"E6.3"),sQuery(id+"F0.wireOp",EDGE,"E6.4"),sQuery(id+"F0.wireOp",EDGE,"E6.5"),sQuery(id+"F0.wireOp",EDGE,"E7.0"),sQuery(id+"F0.wireOp",EDGE,"E7.1"),sQuery(id+"F0.wireOp",EDGE,"E7.2"),sQuery(id+"F0.wireOp",EDGE,"E7.3"),sQuery(id+"F0.wireOp",EDGE,"E7.4"),sQuery(id+"F0.wireOp",EDGE,"E7.5"),sQuery(id+"F0.wireOp",EDGE,"E8.0"),sQuery(id+"F0.wireOp",EDGE,"E8.1"),sQuery(id+"F0.wireOp",EDGE,"E8.2"),sQuery(id+"F0.wireOp",EDGE,"E8.3"),sQuery(id+"F0.wireOp",EDGE,"E8.4"),sQuery(id+"F0.wireOp",EDGE,"E8.5"),sQuery(id+"F0.wireOp",EDGE,"E9"),sQuery(id+"F0.wireOp",EDGE,"E10"),subQ0,sQuery(id+"F0.wireOp",EDGE,"E12"),sQuery(id+"F0.wireOp",EDGE,"E13"),sQuery(id+"F0.wireOp",EDGE,"E14"),sQuery(id+"F0.wireOp",EDGE,"E15"),sQuery(id+"F0.wireOp",EDGE,"E16"),sQuery(id+"F0.wireOp",EDGE,"E19.trimOffspring"),sQuery(id+"F0.wireOp",EDGE,"E20.trimOffspring"),sQuery(id+"F0.wireOp",EDGE,"E23.trimOffspring"),sQuery(id+"F0.wireOp",EDGE,"E26.trimOffspring"),sQuery(id+"F0.wireOp",EDGE,"E27.trimOffspring"),sQuery(id+"F0.wireOp",EDGE,"E31.trimOffspring"),sQuery(id+"F0.wireOp",EDGE,"E34.trimOffspring")])],"isStart":true})]});}
            var Q54;
            {var subQ0=sQuery(id+"F0.wireOp",EDGE,"E11");Q54=makeQuery(id+"F2.opFillet","BLEND_EDGE",EDGE,{"blendedFrom":[makeQuery(id+"F1.opExtrude","CAP_EDGE",EDGE,{"disambiguationData":[OSD([subQ0])],"isStart":false}),makeQuery(id+"F1.opExtrude","CAP_FACE",FACE,{"disambiguationData":[OSD([sQuery(id+"F0.wireOp",EDGE,"E0"),sQuery(id+"F0.wireOp",EDGE,"E2"),sQuery(id+"F0.wireOp",EDGE,"E5.0"),sQuery(id+"F0.wireOp",EDGE,"E5.1"),sQuery(id+"F0.wireOp",EDGE,"E5.2"),sQuery(id+"F0.wireOp",EDGE,"E5.3"),sQuery(id+"F0.wireOp",EDGE,"E5.4"),sQuery(id+"F0.wireOp",EDGE,"E5.5"),sQuery(id+"F0.wireOp",EDGE,"E6.0"),sQuery(id+"F0.wireOp",EDGE,"E6.1"),sQuery(id+"F0.wireOp",EDGE,"E6.2"),sQuery(id+"F0.wireOp",EDGE,"E6.3"),sQuery(id+"F0.wireOp",EDGE,"E6.4"),sQuery(id+"F0.wireOp",EDGE,"E6.5"),sQuery(id+"F0.wireOp",EDGE,"E7.0"),sQuery(id+"F0.wireOp",EDGE,"E7.1"),sQuery(id+"F0.wireOp",EDGE,"E7.2"),sQuery(id+"F0.wireOp",EDGE,"E7.3"),sQuery(id+"F0.wireOp",EDGE,"E7.4"),sQuery(id+"F0.wireOp",EDGE,"E7.5"),sQuery(id+"F0.wireOp",EDGE,"E8.0"),sQuery(id+"F0.wireOp",EDGE,"E8.1"),sQuery(id+"F0.wireOp",EDGE,"E8.2"),sQuery(id+"F0.wireOp",EDGE,"E8.3"),sQuery(id+"F0.wireOp",EDGE,"E8.4"),sQuery(id+"F0.wireOp",EDGE,"E8.5"),sQuery(id+"F0.wireOp",EDGE,"E9"),sQuery(id+"F0.wireOp",EDGE,"E10"),subQ0,sQuery(id+"F0.wireOp",EDGE,"E12"),sQuery(id+"F0.wireOp",EDGE,"E13"),sQuery(id+"F0.wireOp",EDGE,"E14"),sQuery(id+"F0.wireOp",EDGE,"E15"),sQuery(id+"F0.wireOp",EDGE,"E16"),sQuery(id+"F0.wireOp",EDGE,"E19.trimOffspring"),sQuery(id+"F0.wireOp",EDGE,"E20.trimOffspring"),sQuery(id+"F0.wireOp",EDGE,"E23.trimOffspring"),sQuery(id+"F0.wireOp",EDGE,"E26.trimOffspring"),sQuery(id+"F0.wireOp",EDGE,"E27.trimOffspring"),sQuery(id+"F0.wireOp",EDGE,"E31.trimOffspring"),sQuery(id+"F0.wireOp",EDGE,"E34.trimOffspring")])],"isStart":false})],"blendedInto":[makeQuery(id+"F1.opExtrude","CAP_FACE",FACE,{"disambiguationData":[OSD([sQuery(id+"F0.wireOp",EDGE,"E0"),sQuery(id+"F0.wireOp",EDGE,"E2"),sQuery(id+"F0.wireOp",EDGE,"E5.0"),sQuery(id+"F0.wireOp",EDGE,"E5.1"),sQuery(id+"F0.wireOp",EDGE,"E5.2"),sQuery(id+"F0.wireOp",EDGE,"E5.3"),sQuery(id+"F0.wireOp",EDGE,"E5.4"),sQuery(id+"F0.wireOp",EDGE,"E5.5"),sQuery(id+"F0.wireOp",EDGE,"E6.0"),sQuery(id+"F0.wireOp",EDGE,"E6.1"),sQuery(id+"F0.wireOp",EDGE,"E6.2"),sQuery(id+"F0.wireOp",EDGE,"E6.3"),sQuery(id+"F0.wireOp",EDGE,"E6.4"),sQuery(id+"F0.wireOp",EDGE,"E6.5"),sQuery(id+"F0.wireOp",EDGE,"E7.0"),sQuery(id+"F0.wireOp",EDGE,"E7.1"),sQuery(id+"F0.wireOp",EDGE,"E7.2"),sQuery(id+"F0.wireOp",EDGE,"E7.3"),sQuery(id+"F0.wireOp",EDGE,"E7.4"),sQuery(id+"F0.wireOp",EDGE,"E7.5"),sQuery(id+"F0.wireOp",EDGE,"E8.0"),sQuery(id+"F0.wireOp",EDGE,"E8.1"),sQuery(id+"F0.wireOp",EDGE,"E8.2"),sQuery(id+"F0.wireOp",EDGE,"E8.3"),sQuery(id+"F0.wireOp",EDGE,"E8.4"),sQuery(id+"F0.wireOp",EDGE,"E8.5"),sQuery(id+"F0.wireOp",EDGE,"E9"),sQuery(id+"F0.wireOp",EDGE,"E10"),subQ0,sQuery(id+"F0.wireOp",EDGE,"E12"),sQuery(id+"F0.wireOp",EDGE,"E13"),sQuery(id+"F0.wireOp",EDGE,"E14"),sQuery(id+"F0.wireOp",EDGE,"E15"),sQuery(id+"F0.wireOp",EDGE,"E16"),sQuery(id+"F0.wireOp",EDGE,"E19.trimOffspring"),sQuery(id+"F0.wireOp",EDGE,"E20.trimOffspring"),sQuery(id+"F0.wireOp",EDGE,"E23.trimOffspring"),sQuery(id+"F0.wireOp",EDGE,"E26.trimOffspring"),sQuery(id+"F0.wireOp",EDGE,"E27.trimOffspring"),sQuery(id+"F0.wireOp",EDGE,"E31.trimOffspring"),sQuery(id+"F0.wireOp",EDGE,"E34.trimOffspring")])],"isStart":false})]});}
            var Q55;
            {var subQ0=sQuery(id+"F0.wireOp",EDGE,"E9");Q55=makeQuery(id+"F2.opFillet","BLEND_EDGE",EDGE,{"blendedFrom":[makeQuery(id+"F1.opExtrude","CAP_EDGE",EDGE,{"disambiguationData":[OSD([subQ0])],"isStart":false}),makeQuery(id+"F1.opExtrude","SWEPT_FACE",FACE,{"disambiguationData":[OSD([subQ0])]})],"blendedInto":[makeQuery(id+"F1.opExtrude","SWEPT_FACE",FACE,{"disambiguationData":[OSD([subQ0])]})]});}
            var Q56;
            {var subQ0=sQuery(id+"F0.wireOp",EDGE,"E11");Q56=makeQuery(id+"F2.opFillet","BLEND_EDGE",EDGE,{"blendedFrom":[makeQuery(id+"F1.opExtrude","CAP_EDGE",EDGE,{"disambiguationData":[OSD([subQ0])],"isStart":false}),makeQuery(id+"F1.opExtrude","SWEPT_FACE",FACE,{"disambiguationData":[OSD([subQ0])]})],"blendedInto":[makeQuery(id+"F1.opExtrude","SWEPT_FACE",FACE,{"disambiguationData":[OSD([subQ0])]})]});}
            var Q57;
            {var subQ0=sQuery(id+"F0.wireOp",EDGE,"E10");Q57=makeQuery(id+"F2.opFillet","BLEND_EDGE",EDGE,{"blendedFrom":[makeQuery(id+"F1.opExtrude","CAP_EDGE",EDGE,{"disambiguationData":[OSD([subQ0])],"isStart":true}),makeQuery(id+"F1.opExtrude","CAP_FACE",FACE,{"disambiguationData":[OSD([sQuery(id+"F0.wireOp",EDGE,"E0"),sQuery(id+"F0.wireOp",EDGE,"E2"),sQuery(id+"F0.wireOp",EDGE,"E5.0"),sQuery(id+"F0.wireOp",EDGE,"E5.1"),sQuery(id+"F0.wireOp",EDGE,"E5.2"),sQuery(id+"F0.wireOp",EDGE,"E5.3"),sQuery(id+"F0.wireOp",EDGE,"E5.4"),sQuery(id+"F0.wireOp",EDGE,"E5.5"),sQuery(id+"F0.wireOp",EDGE,"E6.0"),sQuery(id+"F0.wireOp",EDGE,"E6.1"),sQuery(id+"F0.wireOp",EDGE,"E6.2"),sQuery(id+"F0.wireOp",EDGE,"E6.3"),sQuery(id+"F0.wireOp",EDGE,"E6.4"),sQuery(id+"F0.wireOp",EDGE,"E6.5"),sQuery(id+"F0.wireOp",EDGE,"E7.0"),sQuery(id+"F0.wireOp",EDGE,"E7.1"),sQuery(id+"F0.wireOp",EDGE,"E7.2"),sQuery(id+"F0.wireOp",EDGE,"E7.3"),sQuery(id+"F0.wireOp",EDGE,"E7.4"),sQuery(id+"F0.wireOp",EDGE,"E7.5"),sQuery(id+"F0.wireOp",EDGE,"E8.0"),sQuery(id+"F0.wireOp",EDGE,"E8.1"),sQuery(id+"F0.wireOp",EDGE,"E8.2"),sQuery(id+"F0.wireOp",EDGE,"E8.3"),sQuery(id+"F0.wireOp",EDGE,"E8.4"),sQuery(id+"F0.wireOp",EDGE,"E8.5"),sQuery(id+"F0.wireOp",EDGE,"E9"),subQ0,sQuery(id+"F0.wireOp",EDGE,"E11"),sQuery(id+"F0.wireOp",EDGE,"E12"),sQuery(id+"F0.wireOp",EDGE,"E13"),sQuery(id+"F0.wireOp",EDGE,"E14"),sQuery(id+"F0.wireOp",EDGE,"E15"),sQuery(id+"F0.wireOp",EDGE,"E16"),sQuery(id+"F0.wireOp",EDGE,"E19.trimOffspring"),sQuery(id+"F0.wireOp",EDGE,"E20.trimOffspring"),sQuery(id+"F0.wireOp",EDGE,"E23.trimOffspring"),sQuery(id+"F0.wireOp",EDGE,"E26.trimOffspring"),sQuery(id+"F0.wireOp",EDGE,"E27.trimOffspring"),sQuery(id+"F0.wireOp",EDGE,"E31.trimOffspring"),sQuery(id+"F0.wireOp",EDGE,"E34.trimOffspring")])],"isStart":true})],"blendedInto":[makeQuery(id+"F1.opExtrude","CAP_FACE",FACE,{"disambiguationData":[OSD([sQuery(id+"F0.wireOp",EDGE,"E0"),sQuery(id+"F0.wireOp",EDGE,"E2"),sQuery(id+"F0.wireOp",EDGE,"E5.0"),sQuery(id+"F0.wireOp",EDGE,"E5.1"),sQuery(id+"F0.wireOp",EDGE,"E5.2"),sQuery(id+"F0.wireOp",EDGE,"E5.3"),sQuery(id+"F0.wireOp",EDGE,"E5.4"),sQuery(id+"F0.wireOp",EDGE,"E5.5"),sQuery(id+"F0.wireOp",EDGE,"E6.0"),sQuery(id+"F0.wireOp",EDGE,"E6.1"),sQuery(id+"F0.wireOp",EDGE,"E6.2"),sQuery(id+"F0.wireOp",EDGE,"E6.3"),sQuery(id+"F0.wireOp",EDGE,"E6.4"),sQuery(id+"F0.wireOp",EDGE,"E6.5"),sQuery(id+"F0.wireOp",EDGE,"E7.0"),sQuery(id+"F0.wireOp",EDGE,"E7.1"),sQuery(id+"F0.wireOp",EDGE,"E7.2"),sQuery(id+"F0.wireOp",EDGE,"E7.3"),sQuery(id+"F0.wireOp",EDGE,"E7.4"),sQuery(id+"F0.wireOp",EDGE,"E7.5"),sQuery(id+"F0.wireOp",EDGE,"E8.0"),sQuery(id+"F0.wireOp",EDGE,"E8.1"),sQuery(id+"F0.wireOp",EDGE,"E8.2"),sQuery(id+"F0.wireOp",EDGE,"E8.3"),sQuery(id+"F0.wireOp",EDGE,"E8.4"),sQuery(id+"F0.wireOp",EDGE,"E8.5"),sQuery(id+"F0.wireOp",EDGE,"E9"),subQ0,sQuery(id+"F0.wireOp",EDGE,"E11"),sQuery(id+"F0.wireOp",EDGE,"E12"),sQuery(id+"F0.wireOp",EDGE,"E13"),sQuery(id+"F0.wireOp",EDGE,"E14"),sQuery(id+"F0.wireOp",EDGE,"E15"),sQuery(id+"F0.wireOp",EDGE,"E16"),sQuery(id+"F0.wireOp",EDGE,"E19.trimOffspring"),sQuery(id+"F0.wireOp",EDGE,"E20.trimOffspring"),sQuery(id+"F0.wireOp",EDGE,"E23.trimOffspring"),sQuery(id+"F0.wireOp",EDGE,"E26.trimOffspring"),sQuery(id+"F0.wireOp",EDGE,"E27.trimOffspring"),sQuery(id+"F0.wireOp",EDGE,"E31.trimOffspring"),sQuery(id+"F0.wireOp",EDGE,"E34.trimOffspring")])],"isStart":true})]});}
            var Q58;
            {var subQ0=sQuery(id+"F0.wireOp",EDGE,"E10");Q58=makeQuery(id+"F2.opFillet","BLEND_EDGE",EDGE,{"blendedFrom":[makeQuery(id+"F1.opExtrude","CAP_EDGE",EDGE,{"disambiguationData":[OSD([subQ0])],"isStart":true}),makeQuery(id+"F1.opExtrude","SWEPT_FACE",FACE,{"disambiguationData":[OSD([subQ0])]})],"blendedInto":[makeQuery(id+"F1.opExtrude","SWEPT_FACE",FACE,{"disambiguationData":[OSD([subQ0])]})]});}
            var Q59;
            {var subQ0=sQuery(id+"F0.wireOp",EDGE,"E10");Q59=makeQuery(id+"F2.opFillet","BLEND_EDGE",EDGE,{"blendedFrom":[makeQuery(id+"F1.opExtrude","CAP_EDGE",EDGE,{"disambiguationData":[OSD([subQ0])],"isStart":false}),makeQuery(id+"F1.opExtrude","CAP_FACE",FACE,{"disambiguationData":[OSD([sQuery(id+"F0.wireOp",EDGE,"E0"),sQuery(id+"F0.wireOp",EDGE,"E2"),sQuery(id+"F0.wireOp",EDGE,"E5.0"),sQuery(id+"F0.wireOp",EDGE,"E5.1"),sQuery(id+"F0.wireOp",EDGE,"E5.2"),sQuery(id+"F0.wireOp",EDGE,"E5.3"),sQuery(id+"F0.wireOp",EDGE,"E5.4"),sQuery(id+"F0.wireOp",EDGE,"E5.5"),sQuery(id+"F0.wireOp",EDGE,"E6.0"),sQuery(id+"F0.wireOp",EDGE,"E6.1"),sQuery(id+"F0.wireOp",EDGE,"E6.2"),sQuery(id+"F0.wireOp",EDGE,"E6.3"),sQuery(id+"F0.wireOp",EDGE,"E6.4"),sQuery(id+"F0.wireOp",EDGE,"E6.5"),sQuery(id+"F0.wireOp",EDGE,"E7.0"),sQuery(id+"F0.wireOp",EDGE,"E7.1"),sQuery(id+"F0.wireOp",EDGE,"E7.2"),sQuery(id+"F0.wireOp",EDGE,"E7.3"),sQuery(id+"F0.wireOp",EDGE,"E7.4"),sQuery(id+"F0.wireOp",EDGE,"E7.5"),sQuery(id+"F0.wireOp",EDGE,"E8.0"),sQuery(id+"F0.wireOp",EDGE,"E8.1"),sQuery(id+"F0.wireOp",EDGE,"E8.2"),sQuery(id+"F0.wireOp",EDGE,"E8.3"),sQuery(id+"F0.wireOp",EDGE,"E8.4"),sQuery(id+"F0.wireOp",EDGE,"E8.5"),sQuery(id+"F0.wireOp",EDGE,"E9"),subQ0,sQuery(id+"F0.wireOp",EDGE,"E11"),sQuery(id+"F0.wireOp",EDGE,"E12"),sQuery(id+"F0.wireOp",EDGE,"E13"),sQuery(id+"F0.wireOp",EDGE,"E14"),sQuery(id+"F0.wireOp",EDGE,"E15"),sQuery(id+"F0.wireOp",EDGE,"E16"),sQuery(id+"F0.wireOp",EDGE,"E19.trimOffspring"),sQuery(id+"F0.wireOp",EDGE,"E20.trimOffspring"),sQuery(id+"F0.wireOp",EDGE,"E23.trimOffspring"),sQuery(id+"F0.wireOp",EDGE,"E26.trimOffspring"),sQuery(id+"F0.wireOp",EDGE,"E27.trimOffspring"),sQuery(id+"F0.wireOp",EDGE,"E31.trimOffspring"),sQuery(id+"F0.wireOp",EDGE,"E34.trimOffspring")])],"isStart":false})],"blendedInto":[makeQuery(id+"F1.opExtrude","CAP_FACE",FACE,{"disambiguationData":[OSD([sQuery(id+"F0.wireOp",EDGE,"E0"),sQuery(id+"F0.wireOp",EDGE,"E2"),sQuery(id+"F0.wireOp",EDGE,"E5.0"),sQuery(id+"F0.wireOp",EDGE,"E5.1"),sQuery(id+"F0.wireOp",EDGE,"E5.2"),sQuery(id+"F0.wireOp",EDGE,"E5.3"),sQuery(id+"F0.wireOp",EDGE,"E5.4"),sQuery(id+"F0.wireOp",EDGE,"E5.5"),sQuery(id+"F0.wireOp",EDGE,"E6.0"),sQuery(id+"F0.wireOp",EDGE,"E6.1"),sQuery(id+"F0.wireOp",EDGE,"E6.2"),sQuery(id+"F0.wireOp",EDGE,"E6.3"),sQuery(id+"F0.wireOp",EDGE,"E6.4"),sQuery(id+"F0.wireOp",EDGE,"E6.5"),sQuery(id+"F0.wireOp",EDGE,"E7.0"),sQuery(id+"F0.wireOp",EDGE,"E7.1"),sQuery(id+"F0.wireOp",EDGE,"E7.2"),sQuery(id+"F0.wireOp",EDGE,"E7.3"),sQuery(id+"F0.wireOp",EDGE,"E7.4"),sQuery(id+"F0.wireOp",EDGE,"E7.5"),sQuery(id+"F0.wireOp",EDGE,"E8.0"),sQuery(id+"F0.wireOp",EDGE,"E8.1"),sQuery(id+"F0.wireOp",EDGE,"E8.2"),sQuery(id+"F0.wireOp",EDGE,"E8.3"),sQuery(id+"F0.wireOp",EDGE,"E8.4"),sQuery(id+"F0.wireOp",EDGE,"E8.5"),sQuery(id+"F0.wireOp",EDGE,"E9"),subQ0,sQuery(id+"F0.wireOp",EDGE,"E11"),sQuery(id+"F0.wireOp",EDGE,"E12"),sQuery(id+"F0.wireOp",EDGE,"E13"),sQuery(id+"F0.wireOp",EDGE,"E14"),sQuery(id+"F0.wireOp",EDGE,"E15"),sQuery(id+"F0.wireOp",EDGE,"E16"),sQuery(id+"F0.wireOp",EDGE,"E19.trimOffspring"),sQuery(id+"F0.wireOp",EDGE,"E20.trimOffspring"),sQuery(id+"F0.wireOp",EDGE,"E23.trimOffspring"),sQuery(id+"F0.wireOp",EDGE,"E26.trimOffspring"),sQuery(id+"F0.wireOp",EDGE,"E27.trimOffspring"),sQuery(id+"F0.wireOp",EDGE,"E31.trimOffspring"),sQuery(id+"F0.wireOp",EDGE,"E34.trimOffspring")])],"isStart":false})]});}
            var Q60;
            {var subQ0=sQuery(id+"F0.wireOp",EDGE,"E23.trimOffspring");var subQ1=sQuery(id+"F0.wireOp",EDGE,"E20.trimOffspring");Q60=makeQuery(id+"F2.opFillet","BLEND_EDGE",EDGE,{"blendedFrom":[makeQuery(id+"F1.opExtrude","CAP_VERTEX",VERTEX,{"disambiguationData":[OSD([subQ1,subQ0])],"isStart":true}),makeQuery(id+"F1.opExtrude","CAP_FACE",FACE,{"disambiguationData":[OSD([sQuery(id+"F0.wireOp",EDGE,"E0"),sQuery(id+"F0.wireOp",EDGE,"E2"),sQuery(id+"F0.wireOp",EDGE,"E5.0"),sQuery(id+"F0.wireOp",EDGE,"E5.1"),sQuery(id+"F0.wireOp",EDGE,"E5.2"),sQuery(id+"F0.wireOp",EDGE,"E5.3"),sQuery(id+"F0.wireOp",EDGE,"E5.4"),sQuery(id+"F0.wireOp",EDGE,"E5.5"),sQuery(id+"F0.wireOp",EDGE,"E6.0"),sQuery(id+"F0.wireOp",EDGE,"E6.1"),sQuery(id+"F0.wireOp",EDGE,"E6.2"),sQuery(id+"F0.wireOp",EDGE,"E6.3"),sQuery(id+"F0.wireOp",EDGE,"E6.4"),sQuery(id+"F0.wireOp",EDGE,"E6.5"),sQuery(id+"F0.wireOp",EDGE,"E7.0"),sQuery(id+"F0.wireOp",EDGE,"E7.1"),sQuery(id+"F0.wireOp",EDGE,"E7.2"),sQuery(id+"F0.wireOp",EDGE,"E7.3"),sQuery(id+"F0.wireOp",EDGE,"E7.4"),sQuery(id+"F0.wireOp",EDGE,"E7.5"),sQuery(id+"F0.wireOp",EDGE,"E8.0"),sQuery(id+"F0.wireOp",EDGE,"E8.1"),sQuery(id+"F0.wireOp",EDGE,"E8.2"),sQuery(id+"F0.wireOp",EDGE,"E8.3"),sQuery(id+"F0.wireOp",EDGE,"E8.4"),sQuery(id+"F0.wireOp",EDGE,"E8.5"),sQuery(id+"F0.wireOp",EDGE,"E9"),sQuery(id+"F0.wireOp",EDGE,"E10"),sQuery(id+"F0.wireOp",EDGE,"E11"),sQuery(id+"F0.wireOp",EDGE,"E12"),sQuery(id+"F0.wireOp",EDGE,"E13"),sQuery(id+"F0.wireOp",EDGE,"E14"),sQuery(id+"F0.wireOp",EDGE,"E15"),sQuery(id+"F0.wireOp",EDGE,"E16"),sQuery(id+"F0.wireOp",EDGE,"E19.trimOffspring"),subQ1,subQ0,sQuery(id+"F0.wireOp",EDGE,"E26.trimOffspring"),sQuery(id+"F0.wireOp",EDGE,"E27.trimOffspring"),sQuery(id+"F0.wireOp",EDGE,"E31.trimOffspring"),sQuery(id+"F0.wireOp",EDGE,"E34.trimOffspring")])],"isStart":true})],"blendedInto":[makeQuery(id+"F1.opExtrude","CAP_FACE",FACE,{"disambiguationData":[OSD([sQuery(id+"F0.wireOp",EDGE,"E0"),sQuery(id+"F0.wireOp",EDGE,"E2"),sQuery(id+"F0.wireOp",EDGE,"E5.0"),sQuery(id+"F0.wireOp",EDGE,"E5.1"),sQuery(id+"F0.wireOp",EDGE,"E5.2"),sQuery(id+"F0.wireOp",EDGE,"E5.3"),sQuery(id+"F0.wireOp",EDGE,"E5.4"),sQuery(id+"F0.wireOp",EDGE,"E5.5"),sQuery(id+"F0.wireOp",EDGE,"E6.0"),sQuery(id+"F0.wireOp",EDGE,"E6.1"),sQuery(id+"F0.wireOp",EDGE,"E6.2"),sQuery(id+"F0.wireOp",EDGE,"E6.3"),sQuery(id+"F0.wireOp",EDGE,"E6.4"),sQuery(id+"F0.wireOp",EDGE,"E6.5"),sQuery(id+"F0.wireOp",EDGE,"E7.0"),sQuery(id+"F0.wireOp",EDGE,"E7.1"),sQuery(id+"F0.wireOp",EDGE,"E7.2"),sQuery(id+"F0.wireOp",EDGE,"E7.3"),sQuery(id+"F0.wireOp",EDGE,"E7.4"),sQuery(id+"F0.wireOp",EDGE,"E7.5"),sQuery(id+"F0.wireOp",EDGE,"E8.0"),sQuery(id+"F0.wireOp",EDGE,"E8.1"),sQuery(id+"F0.wireOp",EDGE,"E8.2"),sQuery(id+"F0.wireOp",EDGE,"E8.3"),sQuery(id+"F0.wireOp",EDGE,"E8.4"),sQuery(id+"F0.wireOp",EDGE,"E8.5"),sQuery(id+"F0.wireOp",EDGE,"E9"),sQuery(id+"F0.wireOp",EDGE,"E10"),sQuery(id+"F0.wireOp",EDGE,"E11"),sQuery(id+"F0.wireOp",EDGE,"E12"),sQuery(id+"F0.wireOp",EDGE,"E13"),sQuery(id+"F0.wireOp",EDGE,"E14"),sQuery(id+"F0.wireOp",EDGE,"E15"),sQuery(id+"F0.wireOp",EDGE,"E16"),sQuery(id+"F0.wireOp",EDGE,"E19.trimOffspring"),subQ1,subQ0,sQuery(id+"F0.wireOp",EDGE,"E26.trimOffspring"),sQuery(id+"F0.wireOp",EDGE,"E27.trimOffspring"),sQuery(id+"F0.wireOp",EDGE,"E31.trimOffspring"),sQuery(id+"F0.wireOp",EDGE,"E34.trimOffspring")])],"isStart":true})]});}
            var Q61;
            {var subQ0=sQuery(id+"F0.wireOp",EDGE,"E10");Q61=makeQuery(id+"F2.opFillet","BLEND_EDGE",EDGE,{"blendedFrom":[makeQuery(id+"F1.opExtrude","CAP_EDGE",EDGE,{"disambiguationData":[OSD([subQ0])],"isStart":false}),makeQuery(id+"F1.opExtrude","SWEPT_FACE",FACE,{"disambiguationData":[OSD([subQ0])]})],"blendedInto":[makeQuery(id+"F1.opExtrude","SWEPT_FACE",FACE,{"disambiguationData":[OSD([subQ0])]})]});}
            var Q62;
            Q62=makeQuery(id+"F1.opExtrude","SWEPT_EDGE",EDGE,{"disambiguationData":[OSD([sQuery(id+"F0.wireOp",EDGE,"E5.4"),sQuery(id+"F0.wireOp",EDGE,"E5.5")])]});
            var Q63;
            Q63=makeQuery(id+"F1.opExtrude","SWEPT_EDGE",EDGE,{"disambiguationData":[OSD([sQuery(id+"F0.wireOp",EDGE,"E6.4"),sQuery(id+"F0.wireOp",EDGE,"E6.5")])]});
            var Q64;
            Q64=makeQuery(id+"F1.opExtrude","SWEPT_EDGE",EDGE,{"disambiguationData":[OSD([sQuery(id+"F0.wireOp",EDGE,"E7.0"),sQuery(id+"F0.wireOp",EDGE,"E7.1")])]});
            var Q65;
            Q65=makeQuery(id+"F1.opExtrude","SWEPT_EDGE",EDGE,{"disambiguationData":[OSD([sQuery(id+"F0.wireOp",EDGE,"E7.0"),sQuery(id+"F0.wireOp",EDGE,"E7.5")])]});
            var Q66;
            Q66=makeQuery(id+"F1.opExtrude","SWEPT_EDGE",EDGE,{"disambiguationData":[OSD([sQuery(id+"F0.wireOp",EDGE,"E5.2"),sQuery(id+"F0.wireOp",EDGE,"E5.3")])]});
            var Q67;
            Q67=makeQuery(id+"F1.opExtrude","SWEPT_EDGE",EDGE,{"disambiguationData":[OSD([sQuery(id+"F0.wireOp",EDGE,"E5.0"),sQuery(id+"F0.wireOp",EDGE,"E5.1")])]});
            var Q68;
            {var subQ0=sQuery(id+"F0.wireOp",EDGE,"E2");Q68=makeQuery(id+"F2.opFillet","BLEND_EDGE",EDGE,{"blendedFrom":[makeQuery(id+"F1.opExtrude","CAP_VERTEX",VERTEX,{"disambiguationData":[OSD([subQ0,sQuery(id+"F0.wireOp",EDGE,"E14")])],"isStart":true}),makeQuery(id+"F1.opExtrude","CAP_EDGE",EDGE,{"disambiguationData":[OSD([subQ0])],"isStart":true})],"blendedInto":[]});}
            var Q69;
            {var subQ0=sQuery(id+"F0.wireOp",EDGE,"E14");var subQ1=sQuery(id+"F0.wireOp",EDGE,"E2");Q69=makeQuery(id+"F2.opFillet","BLEND_EDGE",EDGE,{"blendedFrom":[makeQuery(id+"F1.opExtrude","CAP_VERTEX",VERTEX,{"disambiguationData":[OSD([subQ1,subQ0])],"isStart":true}),makeQuery(id+"F1.opExtrude","SWEPT_EDGE",EDGE,{"disambiguationData":[OSD([subQ1,subQ0])]})],"blendedInto":[]});}
            var Q70;
            {var subQ0=sQuery(id+"F0.wireOp",EDGE,"E19.trimOffspring");var subQ1=sQuery(id+"F0.wireOp",EDGE,"E2");Q70=makeQuery(id+"F2.opFillet","BLEND_EDGE",EDGE,{"blendedFrom":[makeQuery(id+"F1.opExtrude","CAP_VERTEX",VERTEX,{"disambiguationData":[OSD([subQ1,subQ0])],"isStart":false}),makeQuery(id+"F1.opExtrude","CAP_FACE",FACE,{"disambiguationData":[OSD([sQuery(id+"F0.wireOp",EDGE,"E0"),subQ1,sQuery(id+"F0.wireOp",EDGE,"E5.0"),sQuery(id+"F0.wireOp",EDGE,"E5.1"),sQuery(id+"F0.wireOp",EDGE,"E5.2"),sQuery(id+"F0.wireOp",EDGE,"E5.3"),sQuery(id+"F0.wireOp",EDGE,"E5.4"),sQuery(id+"F0.wireOp",EDGE,"E5.5"),sQuery(id+"F0.wireOp",EDGE,"E6.0"),sQuery(id+"F0.wireOp",EDGE,"E6.1"),sQuery(id+"F0.wireOp",EDGE,"E6.2"),sQuery(id+"F0.wireOp",EDGE,"E6.3"),sQuery(id+"F0.wireOp",EDGE,"E6.4"),sQuery(id+"F0.wireOp",EDGE,"E6.5"),sQuery(id+"F0.wireOp",EDGE,"E7.0"),sQuery(id+"F0.wireOp",EDGE,"E7.1"),sQuery(id+"F0.wireOp",EDGE,"E7.2"),sQuery(id+"F0.wireOp",EDGE,"E7.3"),sQuery(id+"F0.wireOp",EDGE,"E7.4"),sQuery(id+"F0.wireOp",EDGE,"E7.5"),sQuery(id+"F0.wireOp",EDGE,"E8.0"),sQuery(id+"F0.wireOp",EDGE,"E8.1"),sQuery(id+"F0.wireOp",EDGE,"E8.2"),sQuery(id+"F0.wireOp",EDGE,"E8.3"),sQuery(id+"F0.wireOp",EDGE,"E8.4"),sQuery(id+"F0.wireOp",EDGE,"E8.5"),sQuery(id+"F0.wireOp",EDGE,"E9"),sQuery(id+"F0.wireOp",EDGE,"E10"),sQuery(id+"F0.wireOp",EDGE,"E11"),sQuery(id+"F0.wireOp",EDGE,"E12"),sQuery(id+"F0.wireOp",EDGE,"E13"),sQuery(id+"F0.wireOp",EDGE,"E14"),sQuery(id+"F0.wireOp",EDGE,"E15"),sQuery(id+"F0.wireOp",EDGE,"E16"),subQ0,sQuery(id+"F0.wireOp",EDGE,"E20.trimOffspring"),sQuery(id+"F0.wireOp",EDGE,"E23.trimOffspring"),sQuery(id+"F0.wireOp",EDGE,"E26.trimOffspring"),sQuery(id+"F0.wireOp",EDGE,"E27.trimOffspring"),sQuery(id+"F0.wireOp",EDGE,"E31.trimOffspring"),sQuery(id+"F0.wireOp",EDGE,"E34.trimOffspring")])],"isStart":false})],"blendedInto":[makeQuery(id+"F1.opExtrude","CAP_FACE",FACE,{"disambiguationData":[OSD([sQuery(id+"F0.wireOp",EDGE,"E0"),subQ1,sQuery(id+"F0.wireOp",EDGE,"E5.0"),sQuery(id+"F0.wireOp",EDGE,"E5.1"),sQuery(id+"F0.wireOp",EDGE,"E5.2"),sQuery(id+"F0.wireOp",EDGE,"E5.3"),sQuery(id+"F0.wireOp",EDGE,"E5.4"),sQuery(id+"F0.wireOp",EDGE,"E5.5"),sQuery(id+"F0.wireOp",EDGE,"E6.0"),sQuery(id+"F0.wireOp",EDGE,"E6.1"),sQuery(id+"F0.wireOp",EDGE,"E6.2"),sQuery(id+"F0.wireOp",EDGE,"E6.3"),sQuery(id+"F0.wireOp",EDGE,"E6.4"),sQuery(id+"F0.wireOp",EDGE,"E6.5"),sQuery(id+"F0.wireOp",EDGE,"E7.0"),sQuery(id+"F0.wireOp",EDGE,"E7.1"),sQuery(id+"F0.wireOp",EDGE,"E7.2"),sQuery(id+"F0.wireOp",EDGE,"E7.3"),sQuery(id+"F0.wireOp",EDGE,"E7.4"),sQuery(id+"F0.wireOp",EDGE,"E7.5"),sQuery(id+"F0.wireOp",EDGE,"E8.0"),sQuery(id+"F0.wireOp",EDGE,"E8.1"),sQuery(id+"F0.wireOp",EDGE,"E8.2"),sQuery(id+"F0.wireOp",EDGE,"E8.3"),sQuery(id+"F0.wireOp",EDGE,"E8.4"),sQuery(id+"F0.wireOp",EDGE,"E8.5"),sQuery(id+"F0.wireOp",EDGE,"E9"),sQuery(id+"F0.wireOp",EDGE,"E10"),sQuery(id+"F0.wireOp",EDGE,"E11"),sQuery(id+"F0.wireOp",EDGE,"E12"),sQuery(id+"F0.wireOp",EDGE,"E13"),sQuery(id+"F0.wireOp",EDGE,"E14"),sQuery(id+"F0.wireOp",EDGE,"E15"),sQuery(id+"F0.wireOp",EDGE,"E16"),subQ0,sQuery(id+"F0.wireOp",EDGE,"E20.trimOffspring"),sQuery(id+"F0.wireOp",EDGE,"E23.trimOffspring"),sQuery(id+"F0.wireOp",EDGE,"E26.trimOffspring"),sQuery(id+"F0.wireOp",EDGE,"E27.trimOffspring"),sQuery(id+"F0.wireOp",EDGE,"E31.trimOffspring"),sQuery(id+"F0.wireOp",EDGE,"E34.trimOffspring")])],"isStart":false})]});}
            var Q71;
            Q71=makeQuery(id+"F1.opExtrude","SWEPT_EDGE",EDGE,{"disambiguationData":[OSD([sQuery(id+"F0.wireOp",EDGE,"E6.0"),sQuery(id+"F0.wireOp",EDGE,"E6.1")])]});
            var Q72;
            Q72=makeQuery(id+"F1.opExtrude","SWEPT_EDGE",EDGE,{"disambiguationData":[OSD([sQuery(id+"F0.wireOp",EDGE,"E6.3"),sQuery(id+"F0.wireOp",EDGE,"E6.4")])]});
            var Q73;
            Q73=makeQuery(id+"F1.opExtrude","SWEPT_EDGE",EDGE,{"disambiguationData":[OSD([sQuery(id+"F0.wireOp",EDGE,"E6.2"),sQuery(id+"F0.wireOp",EDGE,"E6.3")])]});
            var Q74;
            Q74=makeQuery(id+"F1.opExtrude","SWEPT_EDGE",EDGE,{"disambiguationData":[OSD([sQuery(id+"F0.wireOp",EDGE,"E5.3"),sQuery(id+"F0.wireOp",EDGE,"E5.4")])]});
            var Q75;
            Q75=makeQuery(id+"F1.opExtrude","SWEPT_EDGE",EDGE,{"disambiguationData":[OSD([sQuery(id+"F0.wireOp",EDGE,"E6.0"),sQuery(id+"F0.wireOp",EDGE,"E6.5")])]});
            var Q76;
            Q76=makeQuery(id+"F1.opExtrude","SWEPT_EDGE",EDGE,{"disambiguationData":[OSD([sQuery(id+"F0.wireOp",EDGE,"E6.1"),sQuery(id+"F0.wireOp",EDGE,"E6.2")])]});
            var Q77;
            {var subQ0=sQuery(id+"F0.wireOp",EDGE,"E20.trimOffspring");var subQ1=sQuery(id+"F0.wireOp",EDGE,"E15");Q77=makeQuery(id+"F2.opFillet","BLEND_EDGE",EDGE,{"blendedFrom":[makeQuery(id+"F1.opExtrude","CAP_VERTEX",VERTEX,{"disambiguationData":[OSD([subQ1,subQ0])],"isStart":false}),makeQuery(id+"F1.opExtrude","CAP_FACE",FACE,{"disambiguationData":[OSD([sQuery(id+"F0.wireOp",EDGE,"E0"),sQuery(id+"F0.wireOp",EDGE,"E2"),sQuery(id+"F0.wireOp",EDGE,"E5.0"),sQuery(id+"F0.wireOp",EDGE,"E5.1"),sQuery(id+"F0.wireOp",EDGE,"E5.2"),sQuery(id+"F0.wireOp",EDGE,"E5.3"),sQuery(id+"F0.wireOp",EDGE,"E5.4"),sQuery(id+"F0.wireOp",EDGE,"E5.5"),sQuery(id+"F0.wireOp",EDGE,"E6.0"),sQuery(id+"F0.wireOp",EDGE,"E6.1"),sQuery(id+"F0.wireOp",EDGE,"E6.2"),sQuery(id+"F0.wireOp",EDGE,"E6.3"),sQuery(id+"F0.wireOp",EDGE,"E6.4"),sQuery(id+"F0.wireOp",EDGE,"E6.5"),sQuery(id+"F0.wireOp",EDGE,"E7.0"),sQuery(id+"F0.wireOp",EDGE,"E7.1"),sQuery(id+"F0.wireOp",EDGE,"E7.2"),sQuery(id+"F0.wireOp",EDGE,"E7.3"),sQuery(id+"F0.wireOp",EDGE,"E7.4"),sQuery(id+"F0.wireOp",EDGE,"E7.5"),sQuery(id+"F0.wireOp",EDGE,"E8.0"),sQuery(id+"F0.wireOp",EDGE,"E8.1"),sQuery(id+"F0.wireOp",EDGE,"E8.2"),sQuery(id+"F0.wireOp",EDGE,"E8.3"),sQuery(id+"F0.wireOp",EDGE,"E8.4"),sQuery(id+"F0.wireOp",EDGE,"E8.5"),sQuery(id+"F0.wireOp",EDGE,"E9"),sQuery(id+"F0.wireOp",EDGE,"E10"),sQuery(id+"F0.wireOp",EDGE,"E11"),sQuery(id+"F0.wireOp",EDGE,"E12"),sQuery(id+"F0.wireOp",EDGE,"E13"),sQuery(id+"F0.wireOp",EDGE,"E14"),subQ1,sQuery(id+"F0.wireOp",EDGE,"E16"),sQuery(id+"F0.wireOp",EDGE,"E19.trimOffspring"),subQ0,sQuery(id+"F0.wireOp",EDGE,"E23.trimOffspring"),sQuery(id+"F0.wireOp",EDGE,"E26.trimOffspring"),sQuery(id+"F0.wireOp",EDGE,"E27.trimOffspring"),sQuery(id+"F0.wireOp",EDGE,"E31.trimOffspring"),sQuery(id+"F0.wireOp",EDGE,"E34.trimOffspring")])],"isStart":false})],"blendedInto":[makeQuery(id+"F1.opExtrude","CAP_FACE",FACE,{"disambiguationData":[OSD([sQuery(id+"F0.wireOp",EDGE,"E0"),sQuery(id+"F0.wireOp",EDGE,"E2"),sQuery(id+"F0.wireOp",EDGE,"E5.0"),sQuery(id+"F0.wireOp",EDGE,"E5.1"),sQuery(id+"F0.wireOp",EDGE,"E5.2"),sQuery(id+"F0.wireOp",EDGE,"E5.3"),sQuery(id+"F0.wireOp",EDGE,"E5.4"),sQuery(id+"F0.wireOp",EDGE,"E5.5"),sQuery(id+"F0.wireOp",EDGE,"E6.0"),sQuery(id+"F0.wireOp",EDGE,"E6.1"),sQuery(id+"F0.wireOp",EDGE,"E6.2"),sQuery(id+"F0.wireOp",EDGE,"E6.3"),sQuery(id+"F0.wireOp",EDGE,"E6.4"),sQuery(id+"F0.wireOp",EDGE,"E6.5"),sQuery(id+"F0.wireOp",EDGE,"E7.0"),sQuery(id+"F0.wireOp",EDGE,"E7.1"),sQuery(id+"F0.wireOp",EDGE,"E7.2"),sQuery(id+"F0.wireOp",EDGE,"E7.3"),sQuery(id+"F0.wireOp",EDGE,"E7.4"),sQuery(id+"F0.wireOp",EDGE,"E7.5"),sQuery(id+"F0.wireOp",EDGE,"E8.0"),sQuery(id+"F0.wireOp",EDGE,"E8.1"),sQuery(id+"F0.wireOp",EDGE,"E8.2"),sQuery(id+"F0.wireOp",EDGE,"E8.3"),sQuery(id+"F0.wireOp",EDGE,"E8.4"),sQuery(id+"F0.wireOp",EDGE,"E8.5"),sQuery(id+"F0.wireOp",EDGE,"E9"),sQuery(id+"F0.wireOp",EDGE,"E10"),sQuery(id+"F0.wireOp",EDGE,"E11"),sQuery(id+"F0.wireOp",EDGE,"E12"),sQuery(id+"F0.wireOp",EDGE,"E13"),sQuery(id+"F0.wireOp",EDGE,"E14"),subQ1,sQuery(id+"F0.wireOp",EDGE,"E16"),sQuery(id+"F0.wireOp",EDGE,"E19.trimOffspring"),subQ0,sQuery(id+"F0.wireOp",EDGE,"E23.trimOffspring"),sQuery(id+"F0.wireOp",EDGE,"E26.trimOffspring"),sQuery(id+"F0.wireOp",EDGE,"E27.trimOffspring"),sQuery(id+"F0.wireOp",EDGE,"E31.trimOffspring"),sQuery(id+"F0.wireOp",EDGE,"E34.trimOffspring")])],"isStart":false})]});}
            var Q78;
            Q78=makeQuery(id+"F2.opFillet","BLEND_EDGE",EDGE,{"blendedFrom":[makeQuery(id+"F1.opExtrude","CAP_EDGE",EDGE,{"disambiguationData":[OSD([sQuery(id+"F0.wireOp",EDGE,"E11")])],"isStart":true}),makeQuery(id+"F1.opExtrude","CAP_EDGE",EDGE,{"disambiguationData":[OSD([sQuery(id+"F0.wireOp",EDGE,"E15")])],"isStart":true})],"blendedInto":[]});
            var Q79;
            Q79=makeQuery(id+"F1.opExtrude","SWEPT_EDGE",EDGE,{"disambiguationData":[OSD([sQuery(id+"F0.wireOp",EDGE,"E7.1"),sQuery(id+"F0.wireOp",EDGE,"E7.2")])]});
            var Q80;
            {var subQ0=sQuery(id+"F0.wireOp",EDGE,"E14");var subQ1=sQuery(id+"F0.wireOp",EDGE,"E2");Q80=makeQuery(id+"F2.opFillet","BLEND_EDGE",EDGE,{"blendedFrom":[makeQuery(id+"F1.opExtrude","CAP_VERTEX",VERTEX,{"disambiguationData":[OSD([subQ1,subQ0])],"isStart":true}),makeQuery(id+"F1.opExtrude","CAP_FACE",FACE,{"disambiguationData":[OSD([sQuery(id+"F0.wireOp",EDGE,"E0"),subQ1,sQuery(id+"F0.wireOp",EDGE,"E5.0"),sQuery(id+"F0.wireOp",EDGE,"E5.1"),sQuery(id+"F0.wireOp",EDGE,"E5.2"),sQuery(id+"F0.wireOp",EDGE,"E5.3"),sQuery(id+"F0.wireOp",EDGE,"E5.4"),sQuery(id+"F0.wireOp",EDGE,"E5.5"),sQuery(id+"F0.wireOp",EDGE,"E6.0"),sQuery(id+"F0.wireOp",EDGE,"E6.1"),sQuery(id+"F0.wireOp",EDGE,"E6.2"),sQuery(id+"F0.wireOp",EDGE,"E6.3"),sQuery(id+"F0.wireOp",EDGE,"E6.4"),sQuery(id+"F0.wireOp",EDGE,"E6.5"),sQuery(id+"F0.wireOp",EDGE,"E7.0"),sQuery(id+"F0.wireOp",EDGE,"E7.1"),sQuery(id+"F0.wireOp",EDGE,"E7.2"),sQuery(id+"F0.wireOp",EDGE,"E7.3"),sQuery(id+"F0.wireOp",EDGE,"E7.4"),sQuery(id+"F0.wireOp",EDGE,"E7.5"),sQuery(id+"F0.wireOp",EDGE,"E8.0"),sQuery(id+"F0.wireOp",EDGE,"E8.1"),sQuery(id+"F0.wireOp",EDGE,"E8.2"),sQuery(id+"F0.wireOp",EDGE,"E8.3"),sQuery(id+"F0.wireOp",EDGE,"E8.4"),sQuery(id+"F0.wireOp",EDGE,"E8.5"),sQuery(id+"F0.wireOp",EDGE,"E9"),sQuery(id+"F0.wireOp",EDGE,"E10"),sQuery(id+"F0.wireOp",EDGE,"E11"),sQuery(id+"F0.wireOp",EDGE,"E12"),sQuery(id+"F0.wireOp",EDGE,"E13"),subQ0,sQuery(id+"F0.wireOp",EDGE,"E15"),sQuery(id+"F0.wireOp",EDGE,"E16"),sQuery(id+"F0.wireOp",EDGE,"E19.trimOffspring"),sQuery(id+"F0.wireOp",EDGE,"E20.trimOffspring"),sQuery(id+"F0.wireOp",EDGE,"E23.trimOffspring"),sQuery(id+"F0.wireOp",EDGE,"E26.trimOffspring"),sQuery(id+"F0.wireOp",EDGE,"E27.trimOffspring"),sQuery(id+"F0.wireOp",EDGE,"E31.trimOffspring"),sQuery(id+"F0.wireOp",EDGE,"E34.trimOffspring")])],"isStart":true})],"blendedInto":[makeQuery(id+"F1.opExtrude","CAP_FACE",FACE,{"disambiguationData":[OSD([sQuery(id+"F0.wireOp",EDGE,"E0"),subQ1,sQuery(id+"F0.wireOp",EDGE,"E5.0"),sQuery(id+"F0.wireOp",EDGE,"E5.1"),sQuery(id+"F0.wireOp",EDGE,"E5.2"),sQuery(id+"F0.wireOp",EDGE,"E5.3"),sQuery(id+"F0.wireOp",EDGE,"E5.4"),sQuery(id+"F0.wireOp",EDGE,"E5.5"),sQuery(id+"F0.wireOp",EDGE,"E6.0"),sQuery(id+"F0.wireOp",EDGE,"E6.1"),sQuery(id+"F0.wireOp",EDGE,"E6.2"),sQuery(id+"F0.wireOp",EDGE,"E6.3"),sQuery(id+"F0.wireOp",EDGE,"E6.4"),sQuery(id+"F0.wireOp",EDGE,"E6.5"),sQuery(id+"F0.wireOp",EDGE,"E7.0"),sQuery(id+"F0.wireOp",EDGE,"E7.1"),sQuery(id+"F0.wireOp",EDGE,"E7.2"),sQuery(id+"F0.wireOp",EDGE,"E7.3"),sQuery(id+"F0.wireOp",EDGE,"E7.4"),sQuery(id+"F0.wireOp",EDGE,"E7.5"),sQuery(id+"F0.wireOp",EDGE,"E8.0"),sQuery(id+"F0.wireOp",EDGE,"E8.1"),sQuery(id+"F0.wireOp",EDGE,"E8.2"),sQuery(id+"F0.wireOp",EDGE,"E8.3"),sQuery(id+"F0.wireOp",EDGE,"E8.4"),sQuery(id+"F0.wireOp",EDGE,"E8.5"),sQuery(id+"F0.wireOp",EDGE,"E9"),sQuery(id+"F0.wireOp",EDGE,"E10"),sQuery(id+"F0.wireOp",EDGE,"E11"),sQuery(id+"F0.wireOp",EDGE,"E12"),sQuery(id+"F0.wireOp",EDGE,"E13"),subQ0,sQuery(id+"F0.wireOp",EDGE,"E15"),sQuery(id+"F0.wireOp",EDGE,"E16"),sQuery(id+"F0.wireOp",EDGE,"E19.trimOffspring"),sQuery(id+"F0.wireOp",EDGE,"E20.trimOffspring"),sQuery(id+"F0.wireOp",EDGE,"E23.trimOffspring"),sQuery(id+"F0.wireOp",EDGE,"E26.trimOffspring"),sQuery(id+"F0.wireOp",EDGE,"E27.trimOffspring"),sQuery(id+"F0.wireOp",EDGE,"E31.trimOffspring"),sQuery(id+"F0.wireOp",EDGE,"E34.trimOffspring")])],"isStart":true})]});}
            var Q81;
            Q81=makeQuery(id+"F1.opExtrude","SWEPT_EDGE",EDGE,{"disambiguationData":[OSD([sQuery(id+"F0.wireOp",EDGE,"E7.2"),sQuery(id+"F0.wireOp",EDGE,"E7.3")])]});
            var Q82;
            {var subQ0=sQuery(id+"F0.wireOp",EDGE,"E2");Q82=makeQuery(id+"F2.opFillet","BLEND_EDGE",EDGE,{"blendedFrom":[makeQuery(id+"F1.opExtrude","CAP_VERTEX",VERTEX,{"disambiguationData":[OSD([subQ0,sQuery(id+"F0.wireOp",EDGE,"E19.trimOffspring")])],"isStart":false}),makeQuery(id+"F1.opExtrude","CAP_EDGE",EDGE,{"disambiguationData":[OSD([subQ0])],"isStart":false})],"blendedInto":[]});}
            var Q83;
            Q83=makeQuery(id+"F1.opExtrude","SWEPT_EDGE",EDGE,{"disambiguationData":[OSD([sQuery(id+"F0.wireOp",EDGE,"E7.3"),sQuery(id+"F0.wireOp",EDGE,"E7.4")])]});
            var Q84;
            {var subQ0=sQuery(id+"F0.wireOp",EDGE,"E2");Q84=makeQuery(id+"F2.opFillet","BLEND_EDGE",EDGE,{"blendedFrom":[makeQuery(id+"F1.opExtrude","CAP_VERTEX",VERTEX,{"disambiguationData":[OSD([subQ0,sQuery(id+"F0.wireOp",EDGE,"E19.trimOffspring")])],"isStart":true}),makeQuery(id+"F1.opExtrude","CAP_EDGE",EDGE,{"disambiguationData":[OSD([subQ0])],"isStart":true})],"blendedInto":[]});}
            var Q85;
            {var subQ0=sQuery(id+"F0.wireOp",EDGE,"E19.trimOffspring");var subQ1=sQuery(id+"F0.wireOp",EDGE,"E2");Q85=makeQuery(id+"F2.opFillet","BLEND_EDGE",EDGE,{"blendedFrom":[makeQuery(id+"F1.opExtrude","CAP_VERTEX",VERTEX,{"disambiguationData":[OSD([subQ1,subQ0])],"isStart":true}),makeQuery(id+"F1.opExtrude","CAP_FACE",FACE,{"disambiguationData":[OSD([sQuery(id+"F0.wireOp",EDGE,"E0"),subQ1,sQuery(id+"F0.wireOp",EDGE,"E5.0"),sQuery(id+"F0.wireOp",EDGE,"E5.1"),sQuery(id+"F0.wireOp",EDGE,"E5.2"),sQuery(id+"F0.wireOp",EDGE,"E5.3"),sQuery(id+"F0.wireOp",EDGE,"E5.4"),sQuery(id+"F0.wireOp",EDGE,"E5.5"),sQuery(id+"F0.wireOp",EDGE,"E6.0"),sQuery(id+"F0.wireOp",EDGE,"E6.1"),sQuery(id+"F0.wireOp",EDGE,"E6.2"),sQuery(id+"F0.wireOp",EDGE,"E6.3"),sQuery(id+"F0.wireOp",EDGE,"E6.4"),sQuery(id+"F0.wireOp",EDGE,"E6.5"),sQuery(id+"F0.wireOp",EDGE,"E7.0"),sQuery(id+"F0.wireOp",EDGE,"E7.1"),sQuery(id+"F0.wireOp",EDGE,"E7.2"),sQuery(id+"F0.wireOp",EDGE,"E7.3"),sQuery(id+"F0.wireOp",EDGE,"E7.4"),sQuery(id+"F0.wireOp",EDGE,"E7.5"),sQuery(id+"F0.wireOp",EDGE,"E8.0"),sQuery(id+"F0.wireOp",EDGE,"E8.1"),sQuery(id+"F0.wireOp",EDGE,"E8.2"),sQuery(id+"F0.wireOp",EDGE,"E8.3"),sQuery(id+"F0.wireOp",EDGE,"E8.4"),sQuery(id+"F0.wireOp",EDGE,"E8.5"),sQuery(id+"F0.wireOp",EDGE,"E9"),sQuery(id+"F0.wireOp",EDGE,"E10"),sQuery(id+"F0.wireOp",EDGE,"E11"),sQuery(id+"F0.wireOp",EDGE,"E12"),sQuery(id+"F0.wireOp",EDGE,"E13"),sQuery(id+"F0.wireOp",EDGE,"E14"),sQuery(id+"F0.wireOp",EDGE,"E15"),sQuery(id+"F0.wireOp",EDGE,"E16"),subQ0,sQuery(id+"F0.wireOp",EDGE,"E20.trimOffspring"),sQuery(id+"F0.wireOp",EDGE,"E23.trimOffspring"),sQuery(id+"F0.wireOp",EDGE,"E26.trimOffspring"),sQuery(id+"F0.wireOp",EDGE,"E27.trimOffspring"),sQuery(id+"F0.wireOp",EDGE,"E31.trimOffspring"),sQuery(id+"F0.wireOp",EDGE,"E34.trimOffspring")])],"isStart":true})],"blendedInto":[makeQuery(id+"F1.opExtrude","CAP_FACE",FACE,{"disambiguationData":[OSD([sQuery(id+"F0.wireOp",EDGE,"E0"),subQ1,sQuery(id+"F0.wireOp",EDGE,"E5.0"),sQuery(id+"F0.wireOp",EDGE,"E5.1"),sQuery(id+"F0.wireOp",EDGE,"E5.2"),sQuery(id+"F0.wireOp",EDGE,"E5.3"),sQuery(id+"F0.wireOp",EDGE,"E5.4"),sQuery(id+"F0.wireOp",EDGE,"E5.5"),sQuery(id+"F0.wireOp",EDGE,"E6.0"),sQuery(id+"F0.wireOp",EDGE,"E6.1"),sQuery(id+"F0.wireOp",EDGE,"E6.2"),sQuery(id+"F0.wireOp",EDGE,"E6.3"),sQuery(id+"F0.wireOp",EDGE,"E6.4"),sQuery(id+"F0.wireOp",EDGE,"E6.5"),sQuery(id+"F0.wireOp",EDGE,"E7.0"),sQuery(id+"F0.wireOp",EDGE,"E7.1"),sQuery(id+"F0.wireOp",EDGE,"E7.2"),sQuery(id+"F0.wireOp",EDGE,"E7.3"),sQuery(id+"F0.wireOp",EDGE,"E7.4"),sQuery(id+"F0.wireOp",EDGE,"E7.5"),sQuery(id+"F0.wireOp",EDGE,"E8.0"),sQuery(id+"F0.wireOp",EDGE,"E8.1"),sQuery(id+"F0.wireOp",EDGE,"E8.2"),sQuery(id+"F0.wireOp",EDGE,"E8.3"),sQuery(id+"F0.wireOp",EDGE,"E8.4"),sQuery(id+"F0.wireOp",EDGE,"E8.5"),sQuery(id+"F0.wireOp",EDGE,"E9"),sQuery(id+"F0.wireOp",EDGE,"E10"),sQuery(id+"F0.wireOp",EDGE,"E11"),sQuery(id+"F0.wireOp",EDGE,"E12"),sQuery(id+"F0.wireOp",EDGE,"E13"),sQuery(id+"F0.wireOp",EDGE,"E14"),sQuery(id+"F0.wireOp",EDGE,"E15"),sQuery(id+"F0.wireOp",EDGE,"E16"),subQ0,sQuery(id+"F0.wireOp",EDGE,"E20.trimOffspring"),sQuery(id+"F0.wireOp",EDGE,"E23.trimOffspring"),sQuery(id+"F0.wireOp",EDGE,"E26.trimOffspring"),sQuery(id+"F0.wireOp",EDGE,"E27.trimOffspring"),sQuery(id+"F0.wireOp",EDGE,"E31.trimOffspring"),sQuery(id+"F0.wireOp",EDGE,"E34.trimOffspring")])],"isStart":true})]});}
            var Q86;
            {var subQ0=sQuery(id+"F0.wireOp",EDGE,"E19.trimOffspring");Q86=makeQuery(id+"F2.opFillet","BLEND_EDGE",EDGE,{"blendedFrom":[makeQuery(id+"F1.opExtrude","CAP_EDGE",EDGE,{"disambiguationData":[OSD([subQ0])],"isStart":false}),makeQuery(id+"F1.opExtrude","CAP_FACE",FACE,{"disambiguationData":[OSD([sQuery(id+"F0.wireOp",EDGE,"E0"),sQuery(id+"F0.wireOp",EDGE,"E2"),sQuery(id+"F0.wireOp",EDGE,"E5.0"),sQuery(id+"F0.wireOp",EDGE,"E5.1"),sQuery(id+"F0.wireOp",EDGE,"E5.2"),sQuery(id+"F0.wireOp",EDGE,"E5.3"),sQuery(id+"F0.wireOp",EDGE,"E5.4"),sQuery(id+"F0.wireOp",EDGE,"E5.5"),sQuery(id+"F0.wireOp",EDGE,"E6.0"),sQuery(id+"F0.wireOp",EDGE,"E6.1"),sQuery(id+"F0.wireOp",EDGE,"E6.2"),sQuery(id+"F0.wireOp",EDGE,"E6.3"),sQuery(id+"F0.wireOp",EDGE,"E6.4"),sQuery(id+"F0.wireOp",EDGE,"E6.5"),sQuery(id+"F0.wireOp",EDGE,"E7.0"),sQuery(id+"F0.wireOp",EDGE,"E7.1"),sQuery(id+"F0.wireOp",EDGE,"E7.2"),sQuery(id+"F0.wireOp",EDGE,"E7.3"),sQuery(id+"F0.wireOp",EDGE,"E7.4"),sQuery(id+"F0.wireOp",EDGE,"E7.5"),sQuery(id+"F0.wireOp",EDGE,"E8.0"),sQuery(id+"F0.wireOp",EDGE,"E8.1"),sQuery(id+"F0.wireOp",EDGE,"E8.2"),sQuery(id+"F0.wireOp",EDGE,"E8.3"),sQuery(id+"F0.wireOp",EDGE,"E8.4"),sQuery(id+"F0.wireOp",EDGE,"E8.5"),sQuery(id+"F0.wireOp",EDGE,"E9"),sQuery(id+"F0.wireOp",EDGE,"E10"),sQuery(id+"F0.wireOp",EDGE,"E11"),sQuery(id+"F0.wireOp",EDGE,"E12"),sQuery(id+"F0.wireOp",EDGE,"E13"),sQuery(id+"F0.wireOp",EDGE,"E14"),sQuery(id+"F0.wireOp",EDGE,"E15"),sQuery(id+"F0.wireOp",EDGE,"E16"),subQ0,sQuery(id+"F0.wireOp",EDGE,"E20.trimOffspring"),sQuery(id+"F0.wireOp",EDGE,"E23.trimOffspring"),sQuery(id+"F0.wireOp",EDGE,"E26.trimOffspring"),sQuery(id+"F0.wireOp",EDGE,"E27.trimOffspring"),sQuery(id+"F0.wireOp",EDGE,"E31.trimOffspring"),sQuery(id+"F0.wireOp",EDGE,"E34.trimOffspring")])],"isStart":false})],"blendedInto":[makeQuery(id+"F1.opExtrude","CAP_FACE",FACE,{"disambiguationData":[OSD([sQuery(id+"F0.wireOp",EDGE,"E0"),sQuery(id+"F0.wireOp",EDGE,"E2"),sQuery(id+"F0.wireOp",EDGE,"E5.0"),sQuery(id+"F0.wireOp",EDGE,"E5.1"),sQuery(id+"F0.wireOp",EDGE,"E5.2"),sQuery(id+"F0.wireOp",EDGE,"E5.3"),sQuery(id+"F0.wireOp",EDGE,"E5.4"),sQuery(id+"F0.wireOp",EDGE,"E5.5"),sQuery(id+"F0.wireOp",EDGE,"E6.0"),sQuery(id+"F0.wireOp",EDGE,"E6.1"),sQuery(id+"F0.wireOp",EDGE,"E6.2"),sQuery(id+"F0.wireOp",EDGE,"E6.3"),sQuery(id+"F0.wireOp",EDGE,"E6.4"),sQuery(id+"F0.wireOp",EDGE,"E6.5"),sQuery(id+"F0.wireOp",EDGE,"E7.0"),sQuery(id+"F0.wireOp",EDGE,"E7.1"),sQuery(id+"F0.wireOp",EDGE,"E7.2"),sQuery(id+"F0.wireOp",EDGE,"E7.3"),sQuery(id+"F0.wireOp",EDGE,"E7.4"),sQuery(id+"F0.wireOp",EDGE,"E7.5"),sQuery(id+"F0.wireOp",EDGE,"E8.0"),sQuery(id+"F0.wireOp",EDGE,"E8.1"),sQuery(id+"F0.wireOp",EDGE,"E8.2"),sQuery(id+"F0.wireOp",EDGE,"E8.3"),sQuery(id+"F0.wireOp",EDGE,"E8.4"),sQuery(id+"F0.wireOp",EDGE,"E8.5"),sQuery(id+"F0.wireOp",EDGE,"E9"),sQuery(id+"F0.wireOp",EDGE,"E10"),sQuery(id+"F0.wireOp",EDGE,"E11"),sQuery(id+"F0.wireOp",EDGE,"E12"),sQuery(id+"F0.wireOp",EDGE,"E13"),sQuery(id+"F0.wireOp",EDGE,"E14"),sQuery(id+"F0.wireOp",EDGE,"E15"),sQuery(id+"F0.wireOp",EDGE,"E16"),subQ0,sQuery(id+"F0.wireOp",EDGE,"E20.trimOffspring"),sQuery(id+"F0.wireOp",EDGE,"E23.trimOffspring"),sQuery(id+"F0.wireOp",EDGE,"E26.trimOffspring"),sQuery(id+"F0.wireOp",EDGE,"E27.trimOffspring"),sQuery(id+"F0.wireOp",EDGE,"E31.trimOffspring"),sQuery(id+"F0.wireOp",EDGE,"E34.trimOffspring")])],"isStart":false})]});}
            var Q87;
            {var subQ0=sQuery(id+"F0.wireOp",EDGE,"E23.trimOffspring");var subQ1=sQuery(id+"F0.wireOp",EDGE,"E20.trimOffspring");Q87=makeQuery(id+"F2.opFillet","BLEND_EDGE",EDGE,{"blendedFrom":[makeQuery(id+"F1.opExtrude","CAP_VERTEX",VERTEX,{"disambiguationData":[OSD([subQ1,subQ0])],"isStart":false}),makeQuery(id+"F1.opExtrude","CAP_FACE",FACE,{"disambiguationData":[OSD([sQuery(id+"F0.wireOp",EDGE,"E0"),sQuery(id+"F0.wireOp",EDGE,"E2"),sQuery(id+"F0.wireOp",EDGE,"E5.0"),sQuery(id+"F0.wireOp",EDGE,"E5.1"),sQuery(id+"F0.wireOp",EDGE,"E5.2"),sQuery(id+"F0.wireOp",EDGE,"E5.3"),sQuery(id+"F0.wireOp",EDGE,"E5.4"),sQuery(id+"F0.wireOp",EDGE,"E5.5"),sQuery(id+"F0.wireOp",EDGE,"E6.0"),sQuery(id+"F0.wireOp",EDGE,"E6.1"),sQuery(id+"F0.wireOp",EDGE,"E6.2"),sQuery(id+"F0.wireOp",EDGE,"E6.3"),sQuery(id+"F0.wireOp",EDGE,"E6.4"),sQuery(id+"F0.wireOp",EDGE,"E6.5"),sQuery(id+"F0.wireOp",EDGE,"E7.0"),sQuery(id+"F0.wireOp",EDGE,"E7.1"),sQuery(id+"F0.wireOp",EDGE,"E7.2"),sQuery(id+"F0.wireOp",EDGE,"E7.3"),sQuery(id+"F0.wireOp",EDGE,"E7.4"),sQuery(id+"F0.wireOp",EDGE,"E7.5"),sQuery(id+"F0.wireOp",EDGE,"E8.0"),sQuery(id+"F0.wireOp",EDGE,"E8.1"),sQuery(id+"F0.wireOp",EDGE,"E8.2"),sQuery(id+"F0.wireOp",EDGE,"E8.3"),sQuery(id+"F0.wireOp",EDGE,"E8.4"),sQuery(id+"F0.wireOp",EDGE,"E8.5"),sQuery(id+"F0.wireOp",EDGE,"E9"),sQuery(id+"F0.wireOp",EDGE,"E10"),sQuery(id+"F0.wireOp",EDGE,"E11"),sQuery(id+"F0.wireOp",EDGE,"E12"),sQuery(id+"F0.wireOp",EDGE,"E13"),sQuery(id+"F0.wireOp",EDGE,"E14"),sQuery(id+"F0.wireOp",EDGE,"E15"),sQuery(id+"F0.wireOp",EDGE,"E16"),sQuery(id+"F0.wireOp",EDGE,"E19.trimOffspring"),subQ1,subQ0,sQuery(id+"F0.wireOp",EDGE,"E26.trimOffspring"),sQuery(id+"F0.wireOp",EDGE,"E27.trimOffspring"),sQuery(id+"F0.wireOp",EDGE,"E31.trimOffspring"),sQuery(id+"F0.wireOp",EDGE,"E34.trimOffspring")])],"isStart":false})],"blendedInto":[makeQuery(id+"F1.opExtrude","CAP_FACE",FACE,{"disambiguationData":[OSD([sQuery(id+"F0.wireOp",EDGE,"E0"),sQuery(id+"F0.wireOp",EDGE,"E2"),sQuery(id+"F0.wireOp",EDGE,"E5.0"),sQuery(id+"F0.wireOp",EDGE,"E5.1"),sQuery(id+"F0.wireOp",EDGE,"E5.2"),sQuery(id+"F0.wireOp",EDGE,"E5.3"),sQuery(id+"F0.wireOp",EDGE,"E5.4"),sQuery(id+"F0.wireOp",EDGE,"E5.5"),sQuery(id+"F0.wireOp",EDGE,"E6.0"),sQuery(id+"F0.wireOp",EDGE,"E6.1"),sQuery(id+"F0.wireOp",EDGE,"E6.2"),sQuery(id+"F0.wireOp",EDGE,"E6.3"),sQuery(id+"F0.wireOp",EDGE,"E6.4"),sQuery(id+"F0.wireOp",EDGE,"E6.5"),sQuery(id+"F0.wireOp",EDGE,"E7.0"),sQuery(id+"F0.wireOp",EDGE,"E7.1"),sQuery(id+"F0.wireOp",EDGE,"E7.2"),sQuery(id+"F0.wireOp",EDGE,"E7.3"),sQuery(id+"F0.wireOp",EDGE,"E7.4"),sQuery(id+"F0.wireOp",EDGE,"E7.5"),sQuery(id+"F0.wireOp",EDGE,"E8.0"),sQuery(id+"F0.wireOp",EDGE,"E8.1"),sQuery(id+"F0.wireOp",EDGE,"E8.2"),sQuery(id+"F0.wireOp",EDGE,"E8.3"),sQuery(id+"F0.wireOp",EDGE,"E8.4"),sQuery(id+"F0.wireOp",EDGE,"E8.5"),sQuery(id+"F0.wireOp",EDGE,"E9"),sQuery(id+"F0.wireOp",EDGE,"E10"),sQuery(id+"F0.wireOp",EDGE,"E11"),sQuery(id+"F0.wireOp",EDGE,"E12"),sQuery(id+"F0.wireOp",EDGE,"E13"),sQuery(id+"F0.wireOp",EDGE,"E14"),sQuery(id+"F0.wireOp",EDGE,"E15"),sQuery(id+"F0.wireOp",EDGE,"E16"),sQuery(id+"F0.wireOp",EDGE,"E19.trimOffspring"),subQ1,subQ0,sQuery(id+"F0.wireOp",EDGE,"E26.trimOffspring"),sQuery(id+"F0.wireOp",EDGE,"E27.trimOffspring"),sQuery(id+"F0.wireOp",EDGE,"E31.trimOffspring"),sQuery(id+"F0.wireOp",EDGE,"E34.trimOffspring")])],"isStart":false})]});}
            var Q88;
            Q88=makeQuery(id+"F2.opFillet","BLEND_EDGE",EDGE,{"blendedFrom":[makeQuery(id+"F1.opExtrude","CAP_EDGE",EDGE,{"disambiguationData":[OSD([sQuery(id+"F0.wireOp",EDGE,"E9")])],"isStart":true}),makeQuery(id+"F1.opExtrude","CAP_EDGE",EDGE,{"disambiguationData":[OSD([sQuery(id+"F0.wireOp",EDGE,"E16")])],"isStart":true})],"blendedInto":[]});
            var Q89;
            Q89=makeQuery(id+"F1.opExtrude","SWEPT_EDGE",EDGE,{"disambiguationData":[OSD([sQuery(id+"F0.wireOp",EDGE,"E8.1"),sQuery(id+"F0.wireOp",EDGE,"E8.2")])]});
            var Q90;
            {var subQ0=sQuery(id+"F0.wireOp",EDGE,"E14");Q90=makeQuery(id+"F2.opFillet","BLEND_EDGE",EDGE,{"blendedFrom":[makeQuery(id+"F1.opExtrude","CAP_VERTEX",VERTEX,{"disambiguationData":[OSD([sQuery(id+"F0.wireOp",EDGE,"E2"),subQ0])],"isStart":true}),makeQuery(id+"F1.opExtrude","CAP_EDGE",EDGE,{"disambiguationData":[OSD([subQ0])],"isStart":true})],"blendedInto":[]});}
            var Q91;
            Q91=makeQuery(id+"F1.opExtrude","SWEPT_EDGE",EDGE,{"disambiguationData":[OSD([sQuery(id+"F0.wireOp",EDGE,"E8.3"),sQuery(id+"F0.wireOp",EDGE,"E8.4")])]});
            var Q92;
            {var subQ0=sQuery(id+"F0.wireOp",EDGE,"E19.trimOffspring");Q92=makeQuery(id+"F2.opFillet","BLEND_EDGE",EDGE,{"blendedFrom":[makeQuery(id+"F1.opExtrude","CAP_VERTEX",VERTEX,{"disambiguationData":[OSD([sQuery(id+"F0.wireOp",EDGE,"E2"),subQ0])],"isStart":false}),makeQuery(id+"F1.opExtrude","CAP_EDGE",EDGE,{"disambiguationData":[OSD([subQ0])],"isStart":false})],"blendedInto":[]});}
            var Q93;
            {var subQ0=sQuery(id+"F0.wireOp",EDGE,"E19.trimOffspring");Q93=makeQuery(id+"F2.opFillet","BLEND_EDGE",EDGE,{"blendedFrom":[makeQuery(id+"F1.opExtrude","CAP_VERTEX",VERTEX,{"disambiguationData":[OSD([sQuery(id+"F0.wireOp",EDGE,"E2"),subQ0])],"isStart":true}),makeQuery(id+"F1.opExtrude","CAP_EDGE",EDGE,{"disambiguationData":[OSD([subQ0])],"isStart":true})],"blendedInto":[]});}
            var Q94;
            Q94=makeQuery(id+"F1.opExtrude","SWEPT_EDGE",EDGE,{"disambiguationData":[OSD([sQuery(id+"F0.wireOp",EDGE,"E8.4"),sQuery(id+"F0.wireOp",EDGE,"E8.5")])]});
            var Q95;
            {var subQ0=sQuery(id+"F0.wireOp",EDGE,"E23.trimOffspring");Q95=makeQuery(id+"F2.opFillet","BLEND_EDGE",EDGE,{"blendedFrom":[makeQuery(id+"F1.opExtrude","CAP_VERTEX",VERTEX,{"disambiguationData":[OSD([sQuery(id+"F0.wireOp",EDGE,"E20.trimOffspring"),subQ0])],"isStart":false}),makeQuery(id+"F1.opExtrude","CAP_EDGE",EDGE,{"disambiguationData":[OSD([subQ0])],"isStart":false})],"blendedInto":[]});}
            var Q96;
            {var subQ0=sQuery(id+"F0.wireOp",EDGE,"E20.trimOffspring");Q96=makeQuery(id+"F2.opFillet","BLEND_EDGE",EDGE,{"blendedFrom":[makeQuery(id+"F1.opExtrude","CAP_VERTEX",VERTEX,{"disambiguationData":[OSD([subQ0,sQuery(id+"F0.wireOp",EDGE,"E23.trimOffspring")])],"isStart":false}),makeQuery(id+"F1.opExtrude","CAP_EDGE",EDGE,{"disambiguationData":[OSD([subQ0])],"isStart":false})],"blendedInto":[]});}
            var Q97;
            {var subQ0=sQuery(id+"F0.wireOp",EDGE,"E31.trimOffspring");var subQ1=sQuery(id+"F0.wireOp",EDGE,"E13");Q97=makeQuery(id+"F2.opFillet","BLEND_EDGE",EDGE,{"blendedFrom":[makeQuery(id+"F1.opExtrude","CAP_VERTEX",VERTEX,{"disambiguationData":[OSD([subQ1,subQ0])],"isStart":true}),makeQuery(id+"F1.opExtrude","SWEPT_EDGE",EDGE,{"disambiguationData":[OSD([subQ1,subQ0])]})],"blendedInto":[]});}
            var Q98;
            {var subQ0=sQuery(id+"F0.wireOp",EDGE,"E14");Q98=makeQuery(id+"F2.opFillet","BLEND_EDGE",EDGE,{"blendedFrom":[makeQuery(id+"F1.opExtrude","CAP_EDGE",EDGE,{"disambiguationData":[OSD([subQ0])],"isStart":true}),makeQuery(id+"F1.opExtrude","CAP_FACE",FACE,{"disambiguationData":[OSD([sQuery(id+"F0.wireOp",EDGE,"E0"),sQuery(id+"F0.wireOp",EDGE,"E2"),sQuery(id+"F0.wireOp",EDGE,"E5.0"),sQuery(id+"F0.wireOp",EDGE,"E5.1"),sQuery(id+"F0.wireOp",EDGE,"E5.2"),sQuery(id+"F0.wireOp",EDGE,"E5.3"),sQuery(id+"F0.wireOp",EDGE,"E5.4"),sQuery(id+"F0.wireOp",EDGE,"E5.5"),sQuery(id+"F0.wireOp",EDGE,"E6.0"),sQuery(id+"F0.wireOp",EDGE,"E6.1"),sQuery(id+"F0.wireOp",EDGE,"E6.2"),sQuery(id+"F0.wireOp",EDGE,"E6.3"),sQuery(id+"F0.wireOp",EDGE,"E6.4"),sQuery(id+"F0.wireOp",EDGE,"E6.5"),sQuery(id+"F0.wireOp",EDGE,"E7.0"),sQuery(id+"F0.wireOp",EDGE,"E7.1"),sQuery(id+"F0.wireOp",EDGE,"E7.2"),sQuery(id+"F0.wireOp",EDGE,"E7.3"),sQuery(id+"F0.wireOp",EDGE,"E7.4"),sQuery(id+"F0.wireOp",EDGE,"E7.5"),sQuery(id+"F0.wireOp",EDGE,"E8.0"),sQuery(id+"F0.wireOp",EDGE,"E8.1"),sQuery(id+"F0.wireOp",EDGE,"E8.2"),sQuery(id+"F0.wireOp",EDGE,"E8.3"),sQuery(id+"F0.wireOp",EDGE,"E8.4"),sQuery(id+"F0.wireOp",EDGE,"E8.5"),sQuery(id+"F0.wireOp",EDGE,"E9"),sQuery(id+"F0.wireOp",EDGE,"E10"),sQuery(id+"F0.wireOp",EDGE,"E11"),sQuery(id+"F0.wireOp",EDGE,"E12"),sQuery(id+"F0.wireOp",EDGE,"E13"),subQ0,sQuery(id+"F0.wireOp",EDGE,"E15"),sQuery(id+"F0.wireOp",EDGE,"E16"),sQuery(id+"F0.wireOp",EDGE,"E19.trimOffspring"),sQuery(id+"F0.wireOp",EDGE,"E20.trimOffspring"),sQuery(id+"F0.wireOp",EDGE,"E23.trimOffspring"),sQuery(id+"F0.wireOp",EDGE,"E26.trimOffspring"),sQuery(id+"F0.wireOp",EDGE,"E27.trimOffspring"),sQuery(id+"F0.wireOp",EDGE,"E31.trimOffspring"),sQuery(id+"F0.wireOp",EDGE,"E34.trimOffspring")])],"isStart":true})],"blendedInto":[makeQuery(id+"F1.opExtrude","CAP_FACE",FACE,{"disambiguationData":[OSD([sQuery(id+"F0.wireOp",EDGE,"E0"),sQuery(id+"F0.wireOp",EDGE,"E2"),sQuery(id+"F0.wireOp",EDGE,"E5.0"),sQuery(id+"F0.wireOp",EDGE,"E5.1"),sQuery(id+"F0.wireOp",EDGE,"E5.2"),sQuery(id+"F0.wireOp",EDGE,"E5.3"),sQuery(id+"F0.wireOp",EDGE,"E5.4"),sQuery(id+"F0.wireOp",EDGE,"E5.5"),sQuery(id+"F0.wireOp",EDGE,"E6.0"),sQuery(id+"F0.wireOp",EDGE,"E6.1"),sQuery(id+"F0.wireOp",EDGE,"E6.2"),sQuery(id+"F0.wireOp",EDGE,"E6.3"),sQuery(id+"F0.wireOp",EDGE,"E6.4"),sQuery(id+"F0.wireOp",EDGE,"E6.5"),sQuery(id+"F0.wireOp",EDGE,"E7.0"),sQuery(id+"F0.wireOp",EDGE,"E7.1"),sQuery(id+"F0.wireOp",EDGE,"E7.2"),sQuery(id+"F0.wireOp",EDGE,"E7.3"),sQuery(id+"F0.wireOp",EDGE,"E7.4"),sQuery(id+"F0.wireOp",EDGE,"E7.5"),sQuery(id+"F0.wireOp",EDGE,"E8.0"),sQuery(id+"F0.wireOp",EDGE,"E8.1"),sQuery(id+"F0.wireOp",EDGE,"E8.2"),sQuery(id+"F0.wireOp",EDGE,"E8.3"),sQuery(id+"F0.wireOp",EDGE,"E8.4"),sQuery(id+"F0.wireOp",EDGE,"E8.5"),sQuery(id+"F0.wireOp",EDGE,"E9"),sQuery(id+"F0.wireOp",EDGE,"E10"),sQuery(id+"F0.wireOp",EDGE,"E11"),sQuery(id+"F0.wireOp",EDGE,"E12"),sQuery(id+"F0.wireOp",EDGE,"E13"),subQ0,sQuery(id+"F0.wireOp",EDGE,"E15"),sQuery(id+"F0.wireOp",EDGE,"E16"),sQuery(id+"F0.wireOp",EDGE,"E19.trimOffspring"),sQuery(id+"F0.wireOp",EDGE,"E20.trimOffspring"),sQuery(id+"F0.wireOp",EDGE,"E23.trimOffspring"),sQuery(id+"F0.wireOp",EDGE,"E26.trimOffspring"),sQuery(id+"F0.wireOp",EDGE,"E27.trimOffspring"),sQuery(id+"F0.wireOp",EDGE,"E31.trimOffspring"),sQuery(id+"F0.wireOp",EDGE,"E34.trimOffspring")])],"isStart":true})]});}
            var Q99;
            {var subQ0=sQuery(id+"F0.wireOp",EDGE,"E20.trimOffspring");Q99=makeQuery(id+"F2.opFillet","BLEND_EDGE",EDGE,{"blendedFrom":[makeQuery(id+"F1.opExtrude","CAP_EDGE",EDGE,{"disambiguationData":[OSD([subQ0])],"isStart":true}),makeQuery(id+"F1.opExtrude","CAP_FACE",FACE,{"disambiguationData":[OSD([sQuery(id+"F0.wireOp",EDGE,"E0"),sQuery(id+"F0.wireOp",EDGE,"E2"),sQuery(id+"F0.wireOp",EDGE,"E5.0"),sQuery(id+"F0.wireOp",EDGE,"E5.1"),sQuery(id+"F0.wireOp",EDGE,"E5.2"),sQuery(id+"F0.wireOp",EDGE,"E5.3"),sQuery(id+"F0.wireOp",EDGE,"E5.4"),sQuery(id+"F0.wireOp",EDGE,"E5.5"),sQuery(id+"F0.wireOp",EDGE,"E6.0"),sQuery(id+"F0.wireOp",EDGE,"E6.1"),sQuery(id+"F0.wireOp",EDGE,"E6.2"),sQuery(id+"F0.wireOp",EDGE,"E6.3"),sQuery(id+"F0.wireOp",EDGE,"E6.4"),sQuery(id+"F0.wireOp",EDGE,"E6.5"),sQuery(id+"F0.wireOp",EDGE,"E7.0"),sQuery(id+"F0.wireOp",EDGE,"E7.1"),sQuery(id+"F0.wireOp",EDGE,"E7.2"),sQuery(id+"F0.wireOp",EDGE,"E7.3"),sQuery(id+"F0.wireOp",EDGE,"E7.4"),sQuery(id+"F0.wireOp",EDGE,"E7.5"),sQuery(id+"F0.wireOp",EDGE,"E8.0"),sQuery(id+"F0.wireOp",EDGE,"E8.1"),sQuery(id+"F0.wireOp",EDGE,"E8.2"),sQuery(id+"F0.wireOp",EDGE,"E8.3"),sQuery(id+"F0.wireOp",EDGE,"E8.4"),sQuery(id+"F0.wireOp",EDGE,"E8.5"),sQuery(id+"F0.wireOp",EDGE,"E9"),sQuery(id+"F0.wireOp",EDGE,"E10"),sQuery(id+"F0.wireOp",EDGE,"E11"),sQuery(id+"F0.wireOp",EDGE,"E12"),sQuery(id+"F0.wireOp",EDGE,"E13"),sQuery(id+"F0.wireOp",EDGE,"E14"),sQuery(id+"F0.wireOp",EDGE,"E15"),sQuery(id+"F0.wireOp",EDGE,"E16"),sQuery(id+"F0.wireOp",EDGE,"E19.trimOffspring"),subQ0,sQuery(id+"F0.wireOp",EDGE,"E23.trimOffspring"),sQuery(id+"F0.wireOp",EDGE,"E26.trimOffspring"),sQuery(id+"F0.wireOp",EDGE,"E27.trimOffspring"),sQuery(id+"F0.wireOp",EDGE,"E31.trimOffspring"),sQuery(id+"F0.wireOp",EDGE,"E34.trimOffspring")])],"isStart":true})],"blendedInto":[makeQuery(id+"F1.opExtrude","CAP_FACE",FACE,{"disambiguationData":[OSD([sQuery(id+"F0.wireOp",EDGE,"E0"),sQuery(id+"F0.wireOp",EDGE,"E2"),sQuery(id+"F0.wireOp",EDGE,"E5.0"),sQuery(id+"F0.wireOp",EDGE,"E5.1"),sQuery(id+"F0.wireOp",EDGE,"E5.2"),sQuery(id+"F0.wireOp",EDGE,"E5.3"),sQuery(id+"F0.wireOp",EDGE,"E5.4"),sQuery(id+"F0.wireOp",EDGE,"E5.5"),sQuery(id+"F0.wireOp",EDGE,"E6.0"),sQuery(id+"F0.wireOp",EDGE,"E6.1"),sQuery(id+"F0.wireOp",EDGE,"E6.2"),sQuery(id+"F0.wireOp",EDGE,"E6.3"),sQuery(id+"F0.wireOp",EDGE,"E6.4"),sQuery(id+"F0.wireOp",EDGE,"E6.5"),sQuery(id+"F0.wireOp",EDGE,"E7.0"),sQuery(id+"F0.wireOp",EDGE,"E7.1"),sQuery(id+"F0.wireOp",EDGE,"E7.2"),sQuery(id+"F0.wireOp",EDGE,"E7.3"),sQuery(id+"F0.wireOp",EDGE,"E7.4"),sQuery(id+"F0.wireOp",EDGE,"E7.5"),sQuery(id+"F0.wireOp",EDGE,"E8.0"),sQuery(id+"F0.wireOp",EDGE,"E8.1"),sQuery(id+"F0.wireOp",EDGE,"E8.2"),sQuery(id+"F0.wireOp",EDGE,"E8.3"),sQuery(id+"F0.wireOp",EDGE,"E8.4"),sQuery(id+"F0.wireOp",EDGE,"E8.5"),sQuery(id+"F0.wireOp",EDGE,"E9"),sQuery(id+"F0.wireOp",EDGE,"E10"),sQuery(id+"F0.wireOp",EDGE,"E11"),sQuery(id+"F0.wireOp",EDGE,"E12"),sQuery(id+"F0.wireOp",EDGE,"E13"),sQuery(id+"F0.wireOp",EDGE,"E14"),sQuery(id+"F0.wireOp",EDGE,"E15"),sQuery(id+"F0.wireOp",EDGE,"E16"),sQuery(id+"F0.wireOp",EDGE,"E19.trimOffspring"),subQ0,sQuery(id+"F0.wireOp",EDGE,"E23.trimOffspring"),sQuery(id+"F0.wireOp",EDGE,"E26.trimOffspring"),sQuery(id+"F0.wireOp",EDGE,"E27.trimOffspring"),sQuery(id+"F0.wireOp",EDGE,"E31.trimOffspring"),sQuery(id+"F0.wireOp",EDGE,"E34.trimOffspring")])],"isStart":true})]});}
            var Q100;
            {var subQ0=sQuery(id+"F0.wireOp",EDGE,"E31.trimOffspring");Q100=makeQuery(id+"F2.opFillet","BLEND_EDGE",EDGE,{"blendedFrom":[makeQuery(id+"F1.opExtrude","CAP_EDGE",EDGE,{"disambiguationData":[OSD([subQ0])],"isStart":true}),makeQuery(id+"F1.opExtrude","CAP_FACE",FACE,{"disambiguationData":[OSD([sQuery(id+"F0.wireOp",EDGE,"E0"),sQuery(id+"F0.wireOp",EDGE,"E2"),sQuery(id+"F0.wireOp",EDGE,"E5.0"),sQuery(id+"F0.wireOp",EDGE,"E5.1"),sQuery(id+"F0.wireOp",EDGE,"E5.2"),sQuery(id+"F0.wireOp",EDGE,"E5.3"),sQuery(id+"F0.wireOp",EDGE,"E5.4"),sQuery(id+"F0.wireOp",EDGE,"E5.5"),sQuery(id+"F0.wireOp",EDGE,"E6.0"),sQuery(id+"F0.wireOp",EDGE,"E6.1"),sQuery(id+"F0.wireOp",EDGE,"E6.2"),sQuery(id+"F0.wireOp",EDGE,"E6.3"),sQuery(id+"F0.wireOp",EDGE,"E6.4"),sQuery(id+"F0.wireOp",EDGE,"E6.5"),sQuery(id+"F0.wireOp",EDGE,"E7.0"),sQuery(id+"F0.wireOp",EDGE,"E7.1"),sQuery(id+"F0.wireOp",EDGE,"E7.2"),sQuery(id+"F0.wireOp",EDGE,"E7.3"),sQuery(id+"F0.wireOp",EDGE,"E7.4"),sQuery(id+"F0.wireOp",EDGE,"E7.5"),sQuery(id+"F0.wireOp",EDGE,"E8.0"),sQuery(id+"F0.wireOp",EDGE,"E8.1"),sQuery(id+"F0.wireOp",EDGE,"E8.2"),sQuery(id+"F0.wireOp",EDGE,"E8.3"),sQuery(id+"F0.wireOp",EDGE,"E8.4"),sQuery(id+"F0.wireOp",EDGE,"E8.5"),sQuery(id+"F0.wireOp",EDGE,"E9"),sQuery(id+"F0.wireOp",EDGE,"E10"),sQuery(id+"F0.wireOp",EDGE,"E11"),sQuery(id+"F0.wireOp",EDGE,"E12"),sQuery(id+"F0.wireOp",EDGE,"E13"),sQuery(id+"F0.wireOp",EDGE,"E14"),sQuery(id+"F0.wireOp",EDGE,"E15"),sQuery(id+"F0.wireOp",EDGE,"E16"),sQuery(id+"F0.wireOp",EDGE,"E19.trimOffspring"),sQuery(id+"F0.wireOp",EDGE,"E20.trimOffspring"),sQuery(id+"F0.wireOp",EDGE,"E23.trimOffspring"),sQuery(id+"F0.wireOp",EDGE,"E26.trimOffspring"),sQuery(id+"F0.wireOp",EDGE,"E27.trimOffspring"),subQ0,sQuery(id+"F0.wireOp",EDGE,"E34.trimOffspring")])],"isStart":true})],"blendedInto":[makeQuery(id+"F1.opExtrude","CAP_FACE",FACE,{"disambiguationData":[OSD([sQuery(id+"F0.wireOp",EDGE,"E0"),sQuery(id+"F0.wireOp",EDGE,"E2"),sQuery(id+"F0.wireOp",EDGE,"E5.0"),sQuery(id+"F0.wireOp",EDGE,"E5.1"),sQuery(id+"F0.wireOp",EDGE,"E5.2"),sQuery(id+"F0.wireOp",EDGE,"E5.3"),sQuery(id+"F0.wireOp",EDGE,"E5.4"),sQuery(id+"F0.wireOp",EDGE,"E5.5"),sQuery(id+"F0.wireOp",EDGE,"E6.0"),sQuery(id+"F0.wireOp",EDGE,"E6.1"),sQuery(id+"F0.wireOp",EDGE,"E6.2"),sQuery(id+"F0.wireOp",EDGE,"E6.3"),sQuery(id+"F0.wireOp",EDGE,"E6.4"),sQuery(id+"F0.wireOp",EDGE,"E6.5"),sQuery(id+"F0.wireOp",EDGE,"E7.0"),sQuery(id+"F0.wireOp",EDGE,"E7.1"),sQuery(id+"F0.wireOp",EDGE,"E7.2"),sQuery(id+"F0.wireOp",EDGE,"E7.3"),sQuery(id+"F0.wireOp",EDGE,"E7.4"),sQuery(id+"F0.wireOp",EDGE,"E7.5"),sQuery(id+"F0.wireOp",EDGE,"E8.0"),sQuery(id+"F0.wireOp",EDGE,"E8.1"),sQuery(id+"F0.wireOp",EDGE,"E8.2"),sQuery(id+"F0.wireOp",EDGE,"E8.3"),sQuery(id+"F0.wireOp",EDGE,"E8.4"),sQuery(id+"F0.wireOp",EDGE,"E8.5"),sQuery(id+"F0.wireOp",EDGE,"E9"),sQuery(id+"F0.wireOp",EDGE,"E10"),sQuery(id+"F0.wireOp",EDGE,"E11"),sQuery(id+"F0.wireOp",EDGE,"E12"),sQuery(id+"F0.wireOp",EDGE,"E13"),sQuery(id+"F0.wireOp",EDGE,"E14"),sQuery(id+"F0.wireOp",EDGE,"E15"),sQuery(id+"F0.wireOp",EDGE,"E16"),sQuery(id+"F0.wireOp",EDGE,"E19.trimOffspring"),sQuery(id+"F0.wireOp",EDGE,"E20.trimOffspring"),sQuery(id+"F0.wireOp",EDGE,"E23.trimOffspring"),sQuery(id+"F0.wireOp",EDGE,"E26.trimOffspring"),sQuery(id+"F0.wireOp",EDGE,"E27.trimOffspring"),subQ0,sQuery(id+"F0.wireOp",EDGE,"E34.trimOffspring")])],"isStart":true})]});}
            var Q101;
            {var subQ0=sQuery(id+"F0.wireOp",EDGE,"E13");Q101=makeQuery(id+"F2.opFillet","BLEND_EDGE",EDGE,{"blendedFrom":[makeQuery(id+"F1.opExtrude","CAP_VERTEX",VERTEX,{"disambiguationData":[OSD([subQ0,sQuery(id+"F0.wireOp",EDGE,"E31.trimOffspring")])],"isStart":true}),makeQuery(id+"F1.opExtrude","CAP_EDGE",EDGE,{"disambiguationData":[OSD([subQ0])],"isStart":true})],"blendedInto":[]});}
            var Q102;
            {var subQ0=sQuery(id+"F0.wireOp",EDGE,"E16");Q102=makeQuery(id+"F2.opFillet","BLEND_EDGE",EDGE,{"blendedFrom":[makeQuery(id+"F1.opExtrude","CAP_VERTEX",VERTEX,{"disambiguationData":[OSD([subQ0,sQuery(id+"F0.wireOp",EDGE,"E26.trimOffspring")])],"isStart":true}),makeQuery(id+"F1.opExtrude","CAP_EDGE",EDGE,{"disambiguationData":[OSD([subQ0])],"isStart":true})],"blendedInto":[]});}
            var Q103;
            {var subQ0=sQuery(id+"F0.wireOp",EDGE,"E26.trimOffspring");Q103=makeQuery(id+"F2.opFillet","BLEND_EDGE",EDGE,{"blendedFrom":[makeQuery(id+"F1.opExtrude","CAP_VERTEX",VERTEX,{"disambiguationData":[OSD([subQ0,sQuery(id+"F0.wireOp",EDGE,"E34.trimOffspring")])],"isStart":true}),makeQuery(id+"F1.opExtrude","CAP_EDGE",EDGE,{"disambiguationData":[OSD([subQ0])],"isStart":true})],"blendedInto":[]});}
            var Q104;
            Q104=makeQuery(id+"F2.opFillet","BLEND_EDGE",EDGE,{"blendedFrom":[makeQuery(id+"F1.opExtrude","CAP_EDGE",EDGE,{"disambiguationData":[OSD([sQuery(id+"F0.wireOp",EDGE,"E9")])],"isStart":false}),makeQuery(id+"F1.opExtrude","CAP_EDGE",EDGE,{"disambiguationData":[OSD([sQuery(id+"F0.wireOp",EDGE,"E16")])],"isStart":false})],"blendedInto":[]});
            var Q105;
            {var subQ0=sQuery(id+"F0.wireOp",EDGE,"E20.trimOffspring");Q105=makeQuery(id+"F2.opFillet","BLEND_EDGE",EDGE,{"blendedFrom":[makeQuery(id+"F1.opExtrude","CAP_EDGE",EDGE,{"disambiguationData":[OSD([subQ0])],"isStart":true}),makeQuery(id+"F1.opExtrude","SWEPT_FACE",FACE,{"disambiguationData":[OSD([subQ0])]})],"blendedInto":[makeQuery(id+"F1.opExtrude","SWEPT_FACE",FACE,{"disambiguationData":[OSD([subQ0])]})]});}
            var Q106;
            {var subQ0=sQuery(id+"F0.wireOp",EDGE,"E31.trimOffspring");Q106=makeQuery(id+"F2.opFillet","BLEND_EDGE",EDGE,{"blendedFrom":[makeQuery(id+"F1.opExtrude","CAP_EDGE",EDGE,{"disambiguationData":[OSD([subQ0])],"isStart":true}),makeQuery(id+"F1.opExtrude","SWEPT_FACE",FACE,{"disambiguationData":[OSD([subQ0])]})],"blendedInto":[makeQuery(id+"F1.opExtrude","SWEPT_FACE",FACE,{"disambiguationData":[OSD([subQ0])]})]});}
            var Q107;
            {var subQ0=sQuery(id+"F0.wireOp",EDGE,"E31.trimOffspring");Q107=makeQuery(id+"F2.opFillet","BLEND_EDGE",EDGE,{"blendedFrom":[makeQuery(id+"F1.opExtrude","CAP_VERTEX",VERTEX,{"disambiguationData":[OSD([sQuery(id+"F0.wireOp",EDGE,"E13"),subQ0])],"isStart":true}),makeQuery(id+"F1.opExtrude","CAP_EDGE",EDGE,{"disambiguationData":[OSD([subQ0])],"isStart":true})],"blendedInto":[]});}
            var Q108;
            {var subQ0=sQuery(id+"F0.wireOp",EDGE,"E26.trimOffspring");Q108=makeQuery(id+"F2.opFillet","BLEND_EDGE",EDGE,{"blendedFrom":[makeQuery(id+"F1.opExtrude","CAP_VERTEX",VERTEX,{"disambiguationData":[OSD([sQuery(id+"F0.wireOp",EDGE,"E16"),subQ0])],"isStart":true}),makeQuery(id+"F1.opExtrude","CAP_EDGE",EDGE,{"disambiguationData":[OSD([subQ0])],"isStart":true})],"blendedInto":[]});}
            var Q109;
            {var subQ0=sQuery(id+"F0.wireOp",EDGE,"E34.trimOffspring");Q109=makeQuery(id+"F2.opFillet","BLEND_EDGE",EDGE,{"blendedFrom":[makeQuery(id+"F1.opExtrude","CAP_VERTEX",VERTEX,{"disambiguationData":[OSD([sQuery(id+"F0.wireOp",EDGE,"E26.trimOffspring"),subQ0])],"isStart":true}),makeQuery(id+"F1.opExtrude","CAP_EDGE",EDGE,{"disambiguationData":[OSD([subQ0])],"isStart":true})],"blendedInto":[]});}
            var Q110;
            {var subQ0=sQuery(id+"F0.wireOp",EDGE,"E9");Q110=makeQuery(id+"F2.opFillet","BLEND_EDGE",EDGE,{"blendedFrom":[makeQuery(id+"F1.opExtrude","CAP_EDGE",EDGE,{"disambiguationData":[OSD([subQ0])],"isStart":false}),makeQuery(id+"F1.opExtrude","CAP_FACE",FACE,{"disambiguationData":[OSD([sQuery(id+"F0.wireOp",EDGE,"E0"),sQuery(id+"F0.wireOp",EDGE,"E2"),sQuery(id+"F0.wireOp",EDGE,"E5.0"),sQuery(id+"F0.wireOp",EDGE,"E5.1"),sQuery(id+"F0.wireOp",EDGE,"E5.2"),sQuery(id+"F0.wireOp",EDGE,"E5.3"),sQuery(id+"F0.wireOp",EDGE,"E5.4"),sQuery(id+"F0.wireOp",EDGE,"E5.5"),sQuery(id+"F0.wireOp",EDGE,"E6.0"),sQuery(id+"F0.wireOp",EDGE,"E6.1"),sQuery(id+"F0.wireOp",EDGE,"E6.2"),sQuery(id+"F0.wireOp",EDGE,"E6.3"),sQuery(id+"F0.wireOp",EDGE,"E6.4"),sQuery(id+"F0.wireOp",EDGE,"E6.5"),sQuery(id+"F0.wireOp",EDGE,"E7.0"),sQuery(id+"F0.wireOp",EDGE,"E7.1"),sQuery(id+"F0.wireOp",EDGE,"E7.2"),sQuery(id+"F0.wireOp",EDGE,"E7.3"),sQuery(id+"F0.wireOp",EDGE,"E7.4"),sQuery(id+"F0.wireOp",EDGE,"E7.5"),sQuery(id+"F0.wireOp",EDGE,"E8.0"),sQuery(id+"F0.wireOp",EDGE,"E8.1"),sQuery(id+"F0.wireOp",EDGE,"E8.2"),sQuery(id+"F0.wireOp",EDGE,"E8.3"),sQuery(id+"F0.wireOp",EDGE,"E8.4"),sQuery(id+"F0.wireOp",EDGE,"E8.5"),subQ0,sQuery(id+"F0.wireOp",EDGE,"E10"),sQuery(id+"F0.wireOp",EDGE,"E11"),sQuery(id+"F0.wireOp",EDGE,"E12"),sQuery(id+"F0.wireOp",EDGE,"E13"),sQuery(id+"F0.wireOp",EDGE,"E14"),sQuery(id+"F0.wireOp",EDGE,"E15"),sQuery(id+"F0.wireOp",EDGE,"E16"),sQuery(id+"F0.wireOp",EDGE,"E19.trimOffspring"),sQuery(id+"F0.wireOp",EDGE,"E20.trimOffspring"),sQuery(id+"F0.wireOp",EDGE,"E23.trimOffspring"),sQuery(id+"F0.wireOp",EDGE,"E26.trimOffspring"),sQuery(id+"F0.wireOp",EDGE,"E27.trimOffspring"),sQuery(id+"F0.wireOp",EDGE,"E31.trimOffspring"),sQuery(id+"F0.wireOp",EDGE,"E34.trimOffspring")])],"isStart":false})],"blendedInto":[makeQuery(id+"F1.opExtrude","CAP_FACE",FACE,{"disambiguationData":[OSD([sQuery(id+"F0.wireOp",EDGE,"E0"),sQuery(id+"F0.wireOp",EDGE,"E2"),sQuery(id+"F0.wireOp",EDGE,"E5.0"),sQuery(id+"F0.wireOp",EDGE,"E5.1"),sQuery(id+"F0.wireOp",EDGE,"E5.2"),sQuery(id+"F0.wireOp",EDGE,"E5.3"),sQuery(id+"F0.wireOp",EDGE,"E5.4"),sQuery(id+"F0.wireOp",EDGE,"E5.5"),sQuery(id+"F0.wireOp",EDGE,"E6.0"),sQuery(id+"F0.wireOp",EDGE,"E6.1"),sQuery(id+"F0.wireOp",EDGE,"E6.2"),sQuery(id+"F0.wireOp",EDGE,"E6.3"),sQuery(id+"F0.wireOp",EDGE,"E6.4"),sQuery(id+"F0.wireOp",EDGE,"E6.5"),sQuery(id+"F0.wireOp",EDGE,"E7.0"),sQuery(id+"F0.wireOp",EDGE,"E7.1"),sQuery(id+"F0.wireOp",EDGE,"E7.2"),sQuery(id+"F0.wireOp",EDGE,"E7.3"),sQuery(id+"F0.wireOp",EDGE,"E7.4"),sQuery(id+"F0.wireOp",EDGE,"E7.5"),sQuery(id+"F0.wireOp",EDGE,"E8.0"),sQuery(id+"F0.wireOp",EDGE,"E8.1"),sQuery(id+"F0.wireOp",EDGE,"E8.2"),sQuery(id+"F0.wireOp",EDGE,"E8.3"),sQuery(id+"F0.wireOp",EDGE,"E8.4"),sQuery(id+"F0.wireOp",EDGE,"E8.5"),subQ0,sQuery(id+"F0.wireOp",EDGE,"E10"),sQuery(id+"F0.wireOp",EDGE,"E11"),sQuery(id+"F0.wireOp",EDGE,"E12"),sQuery(id+"F0.wireOp",EDGE,"E13"),sQuery(id+"F0.wireOp",EDGE,"E14"),sQuery(id+"F0.wireOp",EDGE,"E15"),sQuery(id+"F0.wireOp",EDGE,"E16"),sQuery(id+"F0.wireOp",EDGE,"E19.trimOffspring"),sQuery(id+"F0.wireOp",EDGE,"E20.trimOffspring"),sQuery(id+"F0.wireOp",EDGE,"E23.trimOffspring"),sQuery(id+"F0.wireOp",EDGE,"E26.trimOffspring"),sQuery(id+"F0.wireOp",EDGE,"E27.trimOffspring"),sQuery(id+"F0.wireOp",EDGE,"E31.trimOffspring"),sQuery(id+"F0.wireOp",EDGE,"E34.trimOffspring")])],"isStart":false})]});}
            var Q111;
            {var subQ0=sQuery(id+"F0.wireOp",EDGE,"E20.trimOffspring");Q111=makeQuery(id+"F2.opFillet","BLEND_EDGE",EDGE,{"blendedFrom":[makeQuery(id+"F1.opExtrude","CAP_EDGE",EDGE,{"disambiguationData":[OSD([subQ0])],"isStart":false}),makeQuery(id+"F1.opExtrude","CAP_FACE",FACE,{"disambiguationData":[OSD([sQuery(id+"F0.wireOp",EDGE,"E0"),sQuery(id+"F0.wireOp",EDGE,"E2"),sQuery(id+"F0.wireOp",EDGE,"E5.0"),sQuery(id+"F0.wireOp",EDGE,"E5.1"),sQuery(id+"F0.wireOp",EDGE,"E5.2"),sQuery(id+"F0.wireOp",EDGE,"E5.3"),sQuery(id+"F0.wireOp",EDGE,"E5.4"),sQuery(id+"F0.wireOp",EDGE,"E5.5"),sQuery(id+"F0.wireOp",EDGE,"E6.0"),sQuery(id+"F0.wireOp",EDGE,"E6.1"),sQuery(id+"F0.wireOp",EDGE,"E6.2"),sQuery(id+"F0.wireOp",EDGE,"E6.3"),sQuery(id+"F0.wireOp",EDGE,"E6.4"),sQuery(id+"F0.wireOp",EDGE,"E6.5"),sQuery(id+"F0.wireOp",EDGE,"E7.0"),sQuery(id+"F0.wireOp",EDGE,"E7.1"),sQuery(id+"F0.wireOp",EDGE,"E7.2"),sQuery(id+"F0.wireOp",EDGE,"E7.3"),sQuery(id+"F0.wireOp",EDGE,"E7.4"),sQuery(id+"F0.wireOp",EDGE,"E7.5"),sQuery(id+"F0.wireOp",EDGE,"E8.0"),sQuery(id+"F0.wireOp",EDGE,"E8.1"),sQuery(id+"F0.wireOp",EDGE,"E8.2"),sQuery(id+"F0.wireOp",EDGE,"E8.3"),sQuery(id+"F0.wireOp",EDGE,"E8.4"),sQuery(id+"F0.wireOp",EDGE,"E8.5"),sQuery(id+"F0.wireOp",EDGE,"E9"),sQuery(id+"F0.wireOp",EDGE,"E10"),sQuery(id+"F0.wireOp",EDGE,"E11"),sQuery(id+"F0.wireOp",EDGE,"E12"),sQuery(id+"F0.wireOp",EDGE,"E13"),sQuery(id+"F0.wireOp",EDGE,"E14"),sQuery(id+"F0.wireOp",EDGE,"E15"),sQuery(id+"F0.wireOp",EDGE,"E16"),sQuery(id+"F0.wireOp",EDGE,"E19.trimOffspring"),subQ0,sQuery(id+"F0.wireOp",EDGE,"E23.trimOffspring"),sQuery(id+"F0.wireOp",EDGE,"E26.trimOffspring"),sQuery(id+"F0.wireOp",EDGE,"E27.trimOffspring"),sQuery(id+"F0.wireOp",EDGE,"E31.trimOffspring"),sQuery(id+"F0.wireOp",EDGE,"E34.trimOffspring")])],"isStart":false})],"blendedInto":[makeQuery(id+"F1.opExtrude","CAP_FACE",FACE,{"disambiguationData":[OSD([sQuery(id+"F0.wireOp",EDGE,"E0"),sQuery(id+"F0.wireOp",EDGE,"E2"),sQuery(id+"F0.wireOp",EDGE,"E5.0"),sQuery(id+"F0.wireOp",EDGE,"E5.1"),sQuery(id+"F0.wireOp",EDGE,"E5.2"),sQuery(id+"F0.wireOp",EDGE,"E5.3"),sQuery(id+"F0.wireOp",EDGE,"E5.4"),sQuery(id+"F0.wireOp",EDGE,"E5.5"),sQuery(id+"F0.wireOp",EDGE,"E6.0"),sQuery(id+"F0.wireOp",EDGE,"E6.1"),sQuery(id+"F0.wireOp",EDGE,"E6.2"),sQuery(id+"F0.wireOp",EDGE,"E6.3"),sQuery(id+"F0.wireOp",EDGE,"E6.4"),sQuery(id+"F0.wireOp",EDGE,"E6.5"),sQuery(id+"F0.wireOp",EDGE,"E7.0"),sQuery(id+"F0.wireOp",EDGE,"E7.1"),sQuery(id+"F0.wireOp",EDGE,"E7.2"),sQuery(id+"F0.wireOp",EDGE,"E7.3"),sQuery(id+"F0.wireOp",EDGE,"E7.4"),sQuery(id+"F0.wireOp",EDGE,"E7.5"),sQuery(id+"F0.wireOp",EDGE,"E8.0"),sQuery(id+"F0.wireOp",EDGE,"E8.1"),sQuery(id+"F0.wireOp",EDGE,"E8.2"),sQuery(id+"F0.wireOp",EDGE,"E8.3"),sQuery(id+"F0.wireOp",EDGE,"E8.4"),sQuery(id+"F0.wireOp",EDGE,"E8.5"),sQuery(id+"F0.wireOp",EDGE,"E9"),sQuery(id+"F0.wireOp",EDGE,"E10"),sQuery(id+"F0.wireOp",EDGE,"E11"),sQuery(id+"F0.wireOp",EDGE,"E12"),sQuery(id+"F0.wireOp",EDGE,"E13"),sQuery(id+"F0.wireOp",EDGE,"E14"),sQuery(id+"F0.wireOp",EDGE,"E15"),sQuery(id+"F0.wireOp",EDGE,"E16"),sQuery(id+"F0.wireOp",EDGE,"E19.trimOffspring"),subQ0,sQuery(id+"F0.wireOp",EDGE,"E23.trimOffspring"),sQuery(id+"F0.wireOp",EDGE,"E26.trimOffspring"),sQuery(id+"F0.wireOp",EDGE,"E27.trimOffspring"),sQuery(id+"F0.wireOp",EDGE,"E31.trimOffspring"),sQuery(id+"F0.wireOp",EDGE,"E34.trimOffspring")])],"isStart":false})]});}
            var Q112;
            {var subQ0=sQuery(id+"F0.wireOp",EDGE,"E31.trimOffspring");Q112=makeQuery(id+"F2.opFillet","BLEND_EDGE",EDGE,{"blendedFrom":[makeQuery(id+"F1.opExtrude","CAP_EDGE",EDGE,{"disambiguationData":[OSD([subQ0])],"isStart":false}),makeQuery(id+"F1.opExtrude","CAP_FACE",FACE,{"disambiguationData":[OSD([sQuery(id+"F0.wireOp",EDGE,"E0"),sQuery(id+"F0.wireOp",EDGE,"E2"),sQuery(id+"F0.wireOp",EDGE,"E5.0"),sQuery(id+"F0.wireOp",EDGE,"E5.1"),sQuery(id+"F0.wireOp",EDGE,"E5.2"),sQuery(id+"F0.wireOp",EDGE,"E5.3"),sQuery(id+"F0.wireOp",EDGE,"E5.4"),sQuery(id+"F0.wireOp",EDGE,"E5.5"),sQuery(id+"F0.wireOp",EDGE,"E6.0"),sQuery(id+"F0.wireOp",EDGE,"E6.1"),sQuery(id+"F0.wireOp",EDGE,"E6.2"),sQuery(id+"F0.wireOp",EDGE,"E6.3"),sQuery(id+"F0.wireOp",EDGE,"E6.4"),sQuery(id+"F0.wireOp",EDGE,"E6.5"),sQuery(id+"F0.wireOp",EDGE,"E7.0"),sQuery(id+"F0.wireOp",EDGE,"E7.1"),sQuery(id+"F0.wireOp",EDGE,"E7.2"),sQuery(id+"F0.wireOp",EDGE,"E7.3"),sQuery(id+"F0.wireOp",EDGE,"E7.4"),sQuery(id+"F0.wireOp",EDGE,"E7.5"),sQuery(id+"F0.wireOp",EDGE,"E8.0"),sQuery(id+"F0.wireOp",EDGE,"E8.1"),sQuery(id+"F0.wireOp",EDGE,"E8.2"),sQuery(id+"F0.wireOp",EDGE,"E8.3"),sQuery(id+"F0.wireOp",EDGE,"E8.4"),sQuery(id+"F0.wireOp",EDGE,"E8.5"),sQuery(id+"F0.wireOp",EDGE,"E9"),sQuery(id+"F0.wireOp",EDGE,"E10"),sQuery(id+"F0.wireOp",EDGE,"E11"),sQuery(id+"F0.wireOp",EDGE,"E12"),sQuery(id+"F0.wireOp",EDGE,"E13"),sQuery(id+"F0.wireOp",EDGE,"E14"),sQuery(id+"F0.wireOp",EDGE,"E15"),sQuery(id+"F0.wireOp",EDGE,"E16"),sQuery(id+"F0.wireOp",EDGE,"E19.trimOffspring"),sQuery(id+"F0.wireOp",EDGE,"E20.trimOffspring"),sQuery(id+"F0.wireOp",EDGE,"E23.trimOffspring"),sQuery(id+"F0.wireOp",EDGE,"E26.trimOffspring"),sQuery(id+"F0.wireOp",EDGE,"E27.trimOffspring"),subQ0,sQuery(id+"F0.wireOp",EDGE,"E34.trimOffspring")])],"isStart":false})],"blendedInto":[makeQuery(id+"F1.opExtrude","CAP_FACE",FACE,{"disambiguationData":[OSD([sQuery(id+"F0.wireOp",EDGE,"E0"),sQuery(id+"F0.wireOp",EDGE,"E2"),sQuery(id+"F0.wireOp",EDGE,"E5.0"),sQuery(id+"F0.wireOp",EDGE,"E5.1"),sQuery(id+"F0.wireOp",EDGE,"E5.2"),sQuery(id+"F0.wireOp",EDGE,"E5.3"),sQuery(id+"F0.wireOp",EDGE,"E5.4"),sQuery(id+"F0.wireOp",EDGE,"E5.5"),sQuery(id+"F0.wireOp",EDGE,"E6.0"),sQuery(id+"F0.wireOp",EDGE,"E6.1"),sQuery(id+"F0.wireOp",EDGE,"E6.2"),sQuery(id+"F0.wireOp",EDGE,"E6.3"),sQuery(id+"F0.wireOp",EDGE,"E6.4"),sQuery(id+"F0.wireOp",EDGE,"E6.5"),sQuery(id+"F0.wireOp",EDGE,"E7.0"),sQuery(id+"F0.wireOp",EDGE,"E7.1"),sQuery(id+"F0.wireOp",EDGE,"E7.2"),sQuery(id+"F0.wireOp",EDGE,"E7.3"),sQuery(id+"F0.wireOp",EDGE,"E7.4"),sQuery(id+"F0.wireOp",EDGE,"E7.5"),sQuery(id+"F0.wireOp",EDGE,"E8.0"),sQuery(id+"F0.wireOp",EDGE,"E8.1"),sQuery(id+"F0.wireOp",EDGE,"E8.2"),sQuery(id+"F0.wireOp",EDGE,"E8.3"),sQuery(id+"F0.wireOp",EDGE,"E8.4"),sQuery(id+"F0.wireOp",EDGE,"E8.5"),sQuery(id+"F0.wireOp",EDGE,"E9"),sQuery(id+"F0.wireOp",EDGE,"E10"),sQuery(id+"F0.wireOp",EDGE,"E11"),sQuery(id+"F0.wireOp",EDGE,"E12"),sQuery(id+"F0.wireOp",EDGE,"E13"),sQuery(id+"F0.wireOp",EDGE,"E14"),sQuery(id+"F0.wireOp",EDGE,"E15"),sQuery(id+"F0.wireOp",EDGE,"E16"),sQuery(id+"F0.wireOp",EDGE,"E19.trimOffspring"),sQuery(id+"F0.wireOp",EDGE,"E20.trimOffspring"),sQuery(id+"F0.wireOp",EDGE,"E23.trimOffspring"),sQuery(id+"F0.wireOp",EDGE,"E26.trimOffspring"),sQuery(id+"F0.wireOp",EDGE,"E27.trimOffspring"),subQ0,sQuery(id+"F0.wireOp",EDGE,"E34.trimOffspring")])],"isStart":false})]});}
            var Q113;
            {var subQ0=sQuery(id+"F0.wireOp",EDGE,"E31.trimOffspring");var subQ1=sQuery(id+"F0.wireOp",EDGE,"E13");Q113=makeQuery(id+"F2.opFillet","BLEND_EDGE",EDGE,{"blendedFrom":[makeQuery(id+"F1.opExtrude","CAP_VERTEX",VERTEX,{"disambiguationData":[OSD([subQ1,subQ0])],"isStart":true}),makeQuery(id+"F1.opExtrude","CAP_FACE",FACE,{"disambiguationData":[OSD([sQuery(id+"F0.wireOp",EDGE,"E0"),sQuery(id+"F0.wireOp",EDGE,"E2"),sQuery(id+"F0.wireOp",EDGE,"E5.0"),sQuery(id+"F0.wireOp",EDGE,"E5.1"),sQuery(id+"F0.wireOp",EDGE,"E5.2"),sQuery(id+"F0.wireOp",EDGE,"E5.3"),sQuery(id+"F0.wireOp",EDGE,"E5.4"),sQuery(id+"F0.wireOp",EDGE,"E5.5"),sQuery(id+"F0.wireOp",EDGE,"E6.0"),sQuery(id+"F0.wireOp",EDGE,"E6.1"),sQuery(id+"F0.wireOp",EDGE,"E6.2"),sQuery(id+"F0.wireOp",EDGE,"E6.3"),sQuery(id+"F0.wireOp",EDGE,"E6.4"),sQuery(id+"F0.wireOp",EDGE,"E6.5"),sQuery(id+"F0.wireOp",EDGE,"E7.0"),sQuery(id+"F0.wireOp",EDGE,"E7.1"),sQuery(id+"F0.wireOp",EDGE,"E7.2"),sQuery(id+"F0.wireOp",EDGE,"E7.3"),sQuery(id+"F0.wireOp",EDGE,"E7.4"),sQuery(id+"F0.wireOp",EDGE,"E7.5"),sQuery(id+"F0.wireOp",EDGE,"E8.0"),sQuery(id+"F0.wireOp",EDGE,"E8.1"),sQuery(id+"F0.wireOp",EDGE,"E8.2"),sQuery(id+"F0.wireOp",EDGE,"E8.3"),sQuery(id+"F0.wireOp",EDGE,"E8.4"),sQuery(id+"F0.wireOp",EDGE,"E8.5"),sQuery(id+"F0.wireOp",EDGE,"E9"),sQuery(id+"F0.wireOp",EDGE,"E10"),sQuery(id+"F0.wireOp",EDGE,"E11"),sQuery(id+"F0.wireOp",EDGE,"E12"),subQ1,sQuery(id+"F0.wireOp",EDGE,"E14"),sQuery(id+"F0.wireOp",EDGE,"E15"),sQuery(id+"F0.wireOp",EDGE,"E16"),sQuery(id+"F0.wireOp",EDGE,"E19.trimOffspring"),sQuery(id+"F0.wireOp",EDGE,"E20.trimOffspring"),sQuery(id+"F0.wireOp",EDGE,"E23.trimOffspring"),sQuery(id+"F0.wireOp",EDGE,"E26.trimOffspring"),sQuery(id+"F0.wireOp",EDGE,"E27.trimOffspring"),subQ0,sQuery(id+"F0.wireOp",EDGE,"E34.trimOffspring")])],"isStart":true})],"blendedInto":[makeQuery(id+"F1.opExtrude","CAP_FACE",FACE,{"disambiguationData":[OSD([sQuery(id+"F0.wireOp",EDGE,"E0"),sQuery(id+"F0.wireOp",EDGE,"E2"),sQuery(id+"F0.wireOp",EDGE,"E5.0"),sQuery(id+"F0.wireOp",EDGE,"E5.1"),sQuery(id+"F0.wireOp",EDGE,"E5.2"),sQuery(id+"F0.wireOp",EDGE,"E5.3"),sQuery(id+"F0.wireOp",EDGE,"E5.4"),sQuery(id+"F0.wireOp",EDGE,"E5.5"),sQuery(id+"F0.wireOp",EDGE,"E6.0"),sQuery(id+"F0.wireOp",EDGE,"E6.1"),sQuery(id+"F0.wireOp",EDGE,"E6.2"),sQuery(id+"F0.wireOp",EDGE,"E6.3"),sQuery(id+"F0.wireOp",EDGE,"E6.4"),sQuery(id+"F0.wireOp",EDGE,"E6.5"),sQuery(id+"F0.wireOp",EDGE,"E7.0"),sQuery(id+"F0.wireOp",EDGE,"E7.1"),sQuery(id+"F0.wireOp",EDGE,"E7.2"),sQuery(id+"F0.wireOp",EDGE,"E7.3"),sQuery(id+"F0.wireOp",EDGE,"E7.4"),sQuery(id+"F0.wireOp",EDGE,"E7.5"),sQuery(id+"F0.wireOp",EDGE,"E8.0"),sQuery(id+"F0.wireOp",EDGE,"E8.1"),sQuery(id+"F0.wireOp",EDGE,"E8.2"),sQuery(id+"F0.wireOp",EDGE,"E8.3"),sQuery(id+"F0.wireOp",EDGE,"E8.4"),sQuery(id+"F0.wireOp",EDGE,"E8.5"),sQuery(id+"F0.wireOp",EDGE,"E9"),sQuery(id+"F0.wireOp",EDGE,"E10"),sQuery(id+"F0.wireOp",EDGE,"E11"),sQuery(id+"F0.wireOp",EDGE,"E12"),subQ1,sQuery(id+"F0.wireOp",EDGE,"E14"),sQuery(id+"F0.wireOp",EDGE,"E15"),sQuery(id+"F0.wireOp",EDGE,"E16"),sQuery(id+"F0.wireOp",EDGE,"E19.trimOffspring"),sQuery(id+"F0.wireOp",EDGE,"E20.trimOffspring"),sQuery(id+"F0.wireOp",EDGE,"E23.trimOffspring"),sQuery(id+"F0.wireOp",EDGE,"E26.trimOffspring"),sQuery(id+"F0.wireOp",EDGE,"E27.trimOffspring"),subQ0,sQuery(id+"F0.wireOp",EDGE,"E34.trimOffspring")])],"isStart":true})]});}
            var Q114;
            {var subQ0=sQuery(id+"F0.wireOp",EDGE,"E26.trimOffspring");var subQ1=sQuery(id+"F0.wireOp",EDGE,"E16");Q114=makeQuery(id+"F2.opFillet","BLEND_EDGE",EDGE,{"blendedFrom":[makeQuery(id+"F1.opExtrude","CAP_VERTEX",VERTEX,{"disambiguationData":[OSD([subQ1,subQ0])],"isStart":true}),makeQuery(id+"F1.opExtrude","CAP_FACE",FACE,{"disambiguationData":[OSD([sQuery(id+"F0.wireOp",EDGE,"E0"),sQuery(id+"F0.wireOp",EDGE,"E2"),sQuery(id+"F0.wireOp",EDGE,"E5.0"),sQuery(id+"F0.wireOp",EDGE,"E5.1"),sQuery(id+"F0.wireOp",EDGE,"E5.2"),sQuery(id+"F0.wireOp",EDGE,"E5.3"),sQuery(id+"F0.wireOp",EDGE,"E5.4"),sQuery(id+"F0.wireOp",EDGE,"E5.5"),sQuery(id+"F0.wireOp",EDGE,"E6.0"),sQuery(id+"F0.wireOp",EDGE,"E6.1"),sQuery(id+"F0.wireOp",EDGE,"E6.2"),sQuery(id+"F0.wireOp",EDGE,"E6.3"),sQuery(id+"F0.wireOp",EDGE,"E6.4"),sQuery(id+"F0.wireOp",EDGE,"E6.5"),sQuery(id+"F0.wireOp",EDGE,"E7.0"),sQuery(id+"F0.wireOp",EDGE,"E7.1"),sQuery(id+"F0.wireOp",EDGE,"E7.2"),sQuery(id+"F0.wireOp",EDGE,"E7.3"),sQuery(id+"F0.wireOp",EDGE,"E7.4"),sQuery(id+"F0.wireOp",EDGE,"E7.5"),sQuery(id+"F0.wireOp",EDGE,"E8.0"),sQuery(id+"F0.wireOp",EDGE,"E8.1"),sQuery(id+"F0.wireOp",EDGE,"E8.2"),sQuery(id+"F0.wireOp",EDGE,"E8.3"),sQuery(id+"F0.wireOp",EDGE,"E8.4"),sQuery(id+"F0.wireOp",EDGE,"E8.5"),sQuery(id+"F0.wireOp",EDGE,"E9"),sQuery(id+"F0.wireOp",EDGE,"E10"),sQuery(id+"F0.wireOp",EDGE,"E11"),sQuery(id+"F0.wireOp",EDGE,"E12"),sQuery(id+"F0.wireOp",EDGE,"E13"),sQuery(id+"F0.wireOp",EDGE,"E14"),sQuery(id+"F0.wireOp",EDGE,"E15"),subQ1,sQuery(id+"F0.wireOp",EDGE,"E19.trimOffspring"),sQuery(id+"F0.wireOp",EDGE,"E20.trimOffspring"),sQuery(id+"F0.wireOp",EDGE,"E23.trimOffspring"),subQ0,sQuery(id+"F0.wireOp",EDGE,"E27.trimOffspring"),sQuery(id+"F0.wireOp",EDGE,"E31.trimOffspring"),sQuery(id+"F0.wireOp",EDGE,"E34.trimOffspring")])],"isStart":true})],"blendedInto":[makeQuery(id+"F1.opExtrude","CAP_FACE",FACE,{"disambiguationData":[OSD([sQuery(id+"F0.wireOp",EDGE,"E0"),sQuery(id+"F0.wireOp",EDGE,"E2"),sQuery(id+"F0.wireOp",EDGE,"E5.0"),sQuery(id+"F0.wireOp",EDGE,"E5.1"),sQuery(id+"F0.wireOp",EDGE,"E5.2"),sQuery(id+"F0.wireOp",EDGE,"E5.3"),sQuery(id+"F0.wireOp",EDGE,"E5.4"),sQuery(id+"F0.wireOp",EDGE,"E5.5"),sQuery(id+"F0.wireOp",EDGE,"E6.0"),sQuery(id+"F0.wireOp",EDGE,"E6.1"),sQuery(id+"F0.wireOp",EDGE,"E6.2"),sQuery(id+"F0.wireOp",EDGE,"E6.3"),sQuery(id+"F0.wireOp",EDGE,"E6.4"),sQuery(id+"F0.wireOp",EDGE,"E6.5"),sQuery(id+"F0.wireOp",EDGE,"E7.0"),sQuery(id+"F0.wireOp",EDGE,"E7.1"),sQuery(id+"F0.wireOp",EDGE,"E7.2"),sQuery(id+"F0.wireOp",EDGE,"E7.3"),sQuery(id+"F0.wireOp",EDGE,"E7.4"),sQuery(id+"F0.wireOp",EDGE,"E7.5"),sQuery(id+"F0.wireOp",EDGE,"E8.0"),sQuery(id+"F0.wireOp",EDGE,"E8.1"),sQuery(id+"F0.wireOp",EDGE,"E8.2"),sQuery(id+"F0.wireOp",EDGE,"E8.3"),sQuery(id+"F0.wireOp",EDGE,"E8.4"),sQuery(id+"F0.wireOp",EDGE,"E8.5"),sQuery(id+"F0.wireOp",EDGE,"E9"),sQuery(id+"F0.wireOp",EDGE,"E10"),sQuery(id+"F0.wireOp",EDGE,"E11"),sQuery(id+"F0.wireOp",EDGE,"E12"),sQuery(id+"F0.wireOp",EDGE,"E13"),sQuery(id+"F0.wireOp",EDGE,"E14"),sQuery(id+"F0.wireOp",EDGE,"E15"),subQ1,sQuery(id+"F0.wireOp",EDGE,"E19.trimOffspring"),sQuery(id+"F0.wireOp",EDGE,"E20.trimOffspring"),sQuery(id+"F0.wireOp",EDGE,"E23.trimOffspring"),subQ0,sQuery(id+"F0.wireOp",EDGE,"E27.trimOffspring"),sQuery(id+"F0.wireOp",EDGE,"E31.trimOffspring"),sQuery(id+"F0.wireOp",EDGE,"E34.trimOffspring")])],"isStart":true})]});}
            var Q115;
            {var subQ0=sQuery(id+"F0.wireOp",EDGE,"E34.trimOffspring");var subQ1=sQuery(id+"F0.wireOp",EDGE,"E26.trimOffspring");Q115=makeQuery(id+"F2.opFillet","BLEND_EDGE",EDGE,{"blendedFrom":[makeQuery(id+"F1.opExtrude","CAP_VERTEX",VERTEX,{"disambiguationData":[OSD([subQ1,subQ0])],"isStart":true}),makeQuery(id+"F1.opExtrude","CAP_FACE",FACE,{"disambiguationData":[OSD([sQuery(id+"F0.wireOp",EDGE,"E0"),sQuery(id+"F0.wireOp",EDGE,"E2"),sQuery(id+"F0.wireOp",EDGE,"E5.0"),sQuery(id+"F0.wireOp",EDGE,"E5.1"),sQuery(id+"F0.wireOp",EDGE,"E5.2"),sQuery(id+"F0.wireOp",EDGE,"E5.3"),sQuery(id+"F0.wireOp",EDGE,"E5.4"),sQuery(id+"F0.wireOp",EDGE,"E5.5"),sQuery(id+"F0.wireOp",EDGE,"E6.0"),sQuery(id+"F0.wireOp",EDGE,"E6.1"),sQuery(id+"F0.wireOp",EDGE,"E6.2"),sQuery(id+"F0.wireOp",EDGE,"E6.3"),sQuery(id+"F0.wireOp",EDGE,"E6.4"),sQuery(id+"F0.wireOp",EDGE,"E6.5"),sQuery(id+"F0.wireOp",EDGE,"E7.0"),sQuery(id+"F0.wireOp",EDGE,"E7.1"),sQuery(id+"F0.wireOp",EDGE,"E7.2"),sQuery(id+"F0.wireOp",EDGE,"E7.3"),sQuery(id+"F0.wireOp",EDGE,"E7.4"),sQuery(id+"F0.wireOp",EDGE,"E7.5"),sQuery(id+"F0.wireOp",EDGE,"E8.0"),sQuery(id+"F0.wireOp",EDGE,"E8.1"),sQuery(id+"F0.wireOp",EDGE,"E8.2"),sQuery(id+"F0.wireOp",EDGE,"E8.3"),sQuery(id+"F0.wireOp",EDGE,"E8.4"),sQuery(id+"F0.wireOp",EDGE,"E8.5"),sQuery(id+"F0.wireOp",EDGE,"E9"),sQuery(id+"F0.wireOp",EDGE,"E10"),sQuery(id+"F0.wireOp",EDGE,"E11"),sQuery(id+"F0.wireOp",EDGE,"E12"),sQuery(id+"F0.wireOp",EDGE,"E13"),sQuery(id+"F0.wireOp",EDGE,"E14"),sQuery(id+"F0.wireOp",EDGE,"E15"),sQuery(id+"F0.wireOp",EDGE,"E16"),sQuery(id+"F0.wireOp",EDGE,"E19.trimOffspring"),sQuery(id+"F0.wireOp",EDGE,"E20.trimOffspring"),sQuery(id+"F0.wireOp",EDGE,"E23.trimOffspring"),subQ1,sQuery(id+"F0.wireOp",EDGE,"E27.trimOffspring"),sQuery(id+"F0.wireOp",EDGE,"E31.trimOffspring"),subQ0])],"isStart":true})],"blendedInto":[makeQuery(id+"F1.opExtrude","CAP_FACE",FACE,{"disambiguationData":[OSD([sQuery(id+"F0.wireOp",EDGE,"E0"),sQuery(id+"F0.wireOp",EDGE,"E2"),sQuery(id+"F0.wireOp",EDGE,"E5.0"),sQuery(id+"F0.wireOp",EDGE,"E5.1"),sQuery(id+"F0.wireOp",EDGE,"E5.2"),sQuery(id+"F0.wireOp",EDGE,"E5.3"),sQuery(id+"F0.wireOp",EDGE,"E5.4"),sQuery(id+"F0.wireOp",EDGE,"E5.5"),sQuery(id+"F0.wireOp",EDGE,"E6.0"),sQuery(id+"F0.wireOp",EDGE,"E6.1"),sQuery(id+"F0.wireOp",EDGE,"E6.2"),sQuery(id+"F0.wireOp",EDGE,"E6.3"),sQuery(id+"F0.wireOp",EDGE,"E6.4"),sQuery(id+"F0.wireOp",EDGE,"E6.5"),sQuery(id+"F0.wireOp",EDGE,"E7.0"),sQuery(id+"F0.wireOp",EDGE,"E7.1"),sQuery(id+"F0.wireOp",EDGE,"E7.2"),sQuery(id+"F0.wireOp",EDGE,"E7.3"),sQuery(id+"F0.wireOp",EDGE,"E7.4"),sQuery(id+"F0.wireOp",EDGE,"E7.5"),sQuery(id+"F0.wireOp",EDGE,"E8.0"),sQuery(id+"F0.wireOp",EDGE,"E8.1"),sQuery(id+"F0.wireOp",EDGE,"E8.2"),sQuery(id+"F0.wireOp",EDGE,"E8.3"),sQuery(id+"F0.wireOp",EDGE,"E8.4"),sQuery(id+"F0.wireOp",EDGE,"E8.5"),sQuery(id+"F0.wireOp",EDGE,"E9"),sQuery(id+"F0.wireOp",EDGE,"E10"),sQuery(id+"F0.wireOp",EDGE,"E11"),sQuery(id+"F0.wireOp",EDGE,"E12"),sQuery(id+"F0.wireOp",EDGE,"E13"),sQuery(id+"F0.wireOp",EDGE,"E14"),sQuery(id+"F0.wireOp",EDGE,"E15"),sQuery(id+"F0.wireOp",EDGE,"E16"),sQuery(id+"F0.wireOp",EDGE,"E19.trimOffspring"),sQuery(id+"F0.wireOp",EDGE,"E20.trimOffspring"),sQuery(id+"F0.wireOp",EDGE,"E23.trimOffspring"),subQ1,sQuery(id+"F0.wireOp",EDGE,"E27.trimOffspring"),sQuery(id+"F0.wireOp",EDGE,"E31.trimOffspring"),subQ0])],"isStart":true})]});}
            var Q116;
            {var subQ0=sQuery(id+"F0.wireOp",EDGE,"E31.trimOffspring");Q116=makeQuery(id+"F2.opFillet","BLEND_EDGE",EDGE,{"blendedFrom":[makeQuery(id+"F1.opExtrude","CAP_EDGE",EDGE,{"disambiguationData":[OSD([subQ0])],"isStart":false}),makeQuery(id+"F1.opExtrude","SWEPT_FACE",FACE,{"disambiguationData":[OSD([subQ0])]})],"blendedInto":[makeQuery(id+"F1.opExtrude","SWEPT_FACE",FACE,{"disambiguationData":[OSD([subQ0])]})]});}
            var Q117;
            Q117=makeQuery(id+"F2.opFillet","BLEND_EDGE",EDGE,{"blendedFrom":[makeQuery(id+"F1.opExtrude","CAP_EDGE",EDGE,{"disambiguationData":[OSD([sQuery(id+"F0.wireOp",EDGE,"E10")])],"isStart":true}),makeQuery(id+"F1.opExtrude","CAP_EDGE",EDGE,{"disambiguationData":[OSD([sQuery(id+"F0.wireOp",EDGE,"E23.trimOffspring")])],"isStart":true})],"blendedInto":[]});
            var Q118;
            Q118=makeQuery(id+"F2.opFillet","BLEND_EDGE",EDGE,{"blendedFrom":[makeQuery(id+"F1.opExtrude","CAP_EDGE",EDGE,{"disambiguationData":[OSD([sQuery(id+"F0.wireOp",EDGE,"E12")])],"isStart":true}),makeQuery(id+"F1.opExtrude","CAP_EDGE",EDGE,{"disambiguationData":[OSD([sQuery(id+"F0.wireOp",EDGE,"E19.trimOffspring")])],"isStart":true})],"blendedInto":[]});
            var Q119;
            {var subQ0=sQuery(id+"F0.wireOp",EDGE,"E15");Q119=makeQuery(id+"F2.opFillet","BLEND_EDGE",EDGE,{"blendedFrom":[makeQuery(id+"F1.opExtrude","CAP_EDGE",EDGE,{"disambiguationData":[OSD([subQ0])],"isStart":true}),makeQuery(id+"F1.opExtrude","CAP_FACE",FACE,{"disambiguationData":[OSD([sQuery(id+"F0.wireOp",EDGE,"E0"),sQuery(id+"F0.wireOp",EDGE,"E2"),sQuery(id+"F0.wireOp",EDGE,"E5.0"),sQuery(id+"F0.wireOp",EDGE,"E5.1"),sQuery(id+"F0.wireOp",EDGE,"E5.2"),sQuery(id+"F0.wireOp",EDGE,"E5.3"),sQuery(id+"F0.wireOp",EDGE,"E5.4"),sQuery(id+"F0.wireOp",EDGE,"E5.5"),sQuery(id+"F0.wireOp",EDGE,"E6.0"),sQuery(id+"F0.wireOp",EDGE,"E6.1"),sQuery(id+"F0.wireOp",EDGE,"E6.2"),sQuery(id+"F0.wireOp",EDGE,"E6.3"),sQuery(id+"F0.wireOp",EDGE,"E6.4"),sQuery(id+"F0.wireOp",EDGE,"E6.5"),sQuery(id+"F0.wireOp",EDGE,"E7.0"),sQuery(id+"F0.wireOp",EDGE,"E7.1"),sQuery(id+"F0.wireOp",EDGE,"E7.2"),sQuery(id+"F0.wireOp",EDGE,"E7.3"),sQuery(id+"F0.wireOp",EDGE,"E7.4"),sQuery(id+"F0.wireOp",EDGE,"E7.5"),sQuery(id+"F0.wireOp",EDGE,"E8.0"),sQuery(id+"F0.wireOp",EDGE,"E8.1"),sQuery(id+"F0.wireOp",EDGE,"E8.2"),sQuery(id+"F0.wireOp",EDGE,"E8.3"),sQuery(id+"F0.wireOp",EDGE,"E8.4"),sQuery(id+"F0.wireOp",EDGE,"E8.5"),sQuery(id+"F0.wireOp",EDGE,"E9"),sQuery(id+"F0.wireOp",EDGE,"E10"),sQuery(id+"F0.wireOp",EDGE,"E11"),sQuery(id+"F0.wireOp",EDGE,"E12"),sQuery(id+"F0.wireOp",EDGE,"E13"),sQuery(id+"F0.wireOp",EDGE,"E14"),subQ0,sQuery(id+"F0.wireOp",EDGE,"E16"),sQuery(id+"F0.wireOp",EDGE,"E19.trimOffspring"),sQuery(id+"F0.wireOp",EDGE,"E20.trimOffspring"),sQuery(id+"F0.wireOp",EDGE,"E23.trimOffspring"),sQuery(id+"F0.wireOp",EDGE,"E26.trimOffspring"),sQuery(id+"F0.wireOp",EDGE,"E27.trimOffspring"),sQuery(id+"F0.wireOp",EDGE,"E31.trimOffspring"),sQuery(id+"F0.wireOp",EDGE,"E34.trimOffspring")])],"isStart":true})],"blendedInto":[makeQuery(id+"F1.opExtrude","CAP_FACE",FACE,{"disambiguationData":[OSD([sQuery(id+"F0.wireOp",EDGE,"E0"),sQuery(id+"F0.wireOp",EDGE,"E2"),sQuery(id+"F0.wireOp",EDGE,"E5.0"),sQuery(id+"F0.wireOp",EDGE,"E5.1"),sQuery(id+"F0.wireOp",EDGE,"E5.2"),sQuery(id+"F0.wireOp",EDGE,"E5.3"),sQuery(id+"F0.wireOp",EDGE,"E5.4"),sQuery(id+"F0.wireOp",EDGE,"E5.5"),sQuery(id+"F0.wireOp",EDGE,"E6.0"),sQuery(id+"F0.wireOp",EDGE,"E6.1"),sQuery(id+"F0.wireOp",EDGE,"E6.2"),sQuery(id+"F0.wireOp",EDGE,"E6.3"),sQuery(id+"F0.wireOp",EDGE,"E6.4"),sQuery(id+"F0.wireOp",EDGE,"E6.5"),sQuery(id+"F0.wireOp",EDGE,"E7.0"),sQuery(id+"F0.wireOp",EDGE,"E7.1"),sQuery(id+"F0.wireOp",EDGE,"E7.2"),sQuery(id+"F0.wireOp",EDGE,"E7.3"),sQuery(id+"F0.wireOp",EDGE,"E7.4"),sQuery(id+"F0.wireOp",EDGE,"E7.5"),sQuery(id+"F0.wireOp",EDGE,"E8.0"),sQuery(id+"F0.wireOp",EDGE,"E8.1"),sQuery(id+"F0.wireOp",EDGE,"E8.2"),sQuery(id+"F0.wireOp",EDGE,"E8.3"),sQuery(id+"F0.wireOp",EDGE,"E8.4"),sQuery(id+"F0.wireOp",EDGE,"E8.5"),sQuery(id+"F0.wireOp",EDGE,"E9"),sQuery(id+"F0.wireOp",EDGE,"E10"),sQuery(id+"F0.wireOp",EDGE,"E11"),sQuery(id+"F0.wireOp",EDGE,"E12"),sQuery(id+"F0.wireOp",EDGE,"E13"),sQuery(id+"F0.wireOp",EDGE,"E14"),subQ0,sQuery(id+"F0.wireOp",EDGE,"E16"),sQuery(id+"F0.wireOp",EDGE,"E19.trimOffspring"),sQuery(id+"F0.wireOp",EDGE,"E20.trimOffspring"),sQuery(id+"F0.wireOp",EDGE,"E23.trimOffspring"),sQuery(id+"F0.wireOp",EDGE,"E26.trimOffspring"),sQuery(id+"F0.wireOp",EDGE,"E27.trimOffspring"),sQuery(id+"F0.wireOp",EDGE,"E31.trimOffspring"),sQuery(id+"F0.wireOp",EDGE,"E34.trimOffspring")])],"isStart":true})]});}
            var Q120;
            {var subQ0=sQuery(id+"F0.wireOp",EDGE,"E23.trimOffspring");Q120=makeQuery(id+"F2.opFillet","BLEND_EDGE",EDGE,{"blendedFrom":[makeQuery(id+"F1.opExtrude","CAP_EDGE",EDGE,{"disambiguationData":[OSD([subQ0])],"isStart":true}),makeQuery(id+"F1.opExtrude","CAP_FACE",FACE,{"disambiguationData":[OSD([sQuery(id+"F0.wireOp",EDGE,"E0"),sQuery(id+"F0.wireOp",EDGE,"E2"),sQuery(id+"F0.wireOp",EDGE,"E5.0"),sQuery(id+"F0.wireOp",EDGE,"E5.1"),sQuery(id+"F0.wireOp",EDGE,"E5.2"),sQuery(id+"F0.wireOp",EDGE,"E5.3"),sQuery(id+"F0.wireOp",EDGE,"E5.4"),sQuery(id+"F0.wireOp",EDGE,"E5.5"),sQuery(id+"F0.wireOp",EDGE,"E6.0"),sQuery(id+"F0.wireOp",EDGE,"E6.1"),sQuery(id+"F0.wireOp",EDGE,"E6.2"),sQuery(id+"F0.wireOp",EDGE,"E6.3"),sQuery(id+"F0.wireOp",EDGE,"E6.4"),sQuery(id+"F0.wireOp",EDGE,"E6.5"),sQuery(id+"F0.wireOp",EDGE,"E7.0"),sQuery(id+"F0.wireOp",EDGE,"E7.1"),sQuery(id+"F0.wireOp",EDGE,"E7.2"),sQuery(id+"F0.wireOp",EDGE,"E7.3"),sQuery(id+"F0.wireOp",EDGE,"E7.4"),sQuery(id+"F0.wireOp",EDGE,"E7.5"),sQuery(id+"F0.wireOp",EDGE,"E8.0"),sQuery(id+"F0.wireOp",EDGE,"E8.1"),sQuery(id+"F0.wireOp",EDGE,"E8.2"),sQuery(id+"F0.wireOp",EDGE,"E8.3"),sQuery(id+"F0.wireOp",EDGE,"E8.4"),sQuery(id+"F0.wireOp",EDGE,"E8.5"),sQuery(id+"F0.wireOp",EDGE,"E9"),sQuery(id+"F0.wireOp",EDGE,"E10"),sQuery(id+"F0.wireOp",EDGE,"E11"),sQuery(id+"F0.wireOp",EDGE,"E12"),sQuery(id+"F0.wireOp",EDGE,"E13"),sQuery(id+"F0.wireOp",EDGE,"E14"),sQuery(id+"F0.wireOp",EDGE,"E15"),sQuery(id+"F0.wireOp",EDGE,"E16"),sQuery(id+"F0.wireOp",EDGE,"E19.trimOffspring"),sQuery(id+"F0.wireOp",EDGE,"E20.trimOffspring"),subQ0,sQuery(id+"F0.wireOp",EDGE,"E26.trimOffspring"),sQuery(id+"F0.wireOp",EDGE,"E27.trimOffspring"),sQuery(id+"F0.wireOp",EDGE,"E31.trimOffspring"),sQuery(id+"F0.wireOp",EDGE,"E34.trimOffspring")])],"isStart":true})],"blendedInto":[makeQuery(id+"F1.opExtrude","CAP_FACE",FACE,{"disambiguationData":[OSD([sQuery(id+"F0.wireOp",EDGE,"E0"),sQuery(id+"F0.wireOp",EDGE,"E2"),sQuery(id+"F0.wireOp",EDGE,"E5.0"),sQuery(id+"F0.wireOp",EDGE,"E5.1"),sQuery(id+"F0.wireOp",EDGE,"E5.2"),sQuery(id+"F0.wireOp",EDGE,"E5.3"),sQuery(id+"F0.wireOp",EDGE,"E5.4"),sQuery(id+"F0.wireOp",EDGE,"E5.5"),sQuery(id+"F0.wireOp",EDGE,"E6.0"),sQuery(id+"F0.wireOp",EDGE,"E6.1"),sQuery(id+"F0.wireOp",EDGE,"E6.2"),sQuery(id+"F0.wireOp",EDGE,"E6.3"),sQuery(id+"F0.wireOp",EDGE,"E6.4"),sQuery(id+"F0.wireOp",EDGE,"E6.5"),sQuery(id+"F0.wireOp",EDGE,"E7.0"),sQuery(id+"F0.wireOp",EDGE,"E7.1"),sQuery(id+"F0.wireOp",EDGE,"E7.2"),sQuery(id+"F0.wireOp",EDGE,"E7.3"),sQuery(id+"F0.wireOp",EDGE,"E7.4"),sQuery(id+"F0.wireOp",EDGE,"E7.5"),sQuery(id+"F0.wireOp",EDGE,"E8.0"),sQuery(id+"F0.wireOp",EDGE,"E8.1"),sQuery(id+"F0.wireOp",EDGE,"E8.2"),sQuery(id+"F0.wireOp",EDGE,"E8.3"),sQuery(id+"F0.wireOp",EDGE,"E8.4"),sQuery(id+"F0.wireOp",EDGE,"E8.5"),sQuery(id+"F0.wireOp",EDGE,"E9"),sQuery(id+"F0.wireOp",EDGE,"E10"),sQuery(id+"F0.wireOp",EDGE,"E11"),sQuery(id+"F0.wireOp",EDGE,"E12"),sQuery(id+"F0.wireOp",EDGE,"E13"),sQuery(id+"F0.wireOp",EDGE,"E14"),sQuery(id+"F0.wireOp",EDGE,"E15"),sQuery(id+"F0.wireOp",EDGE,"E16"),sQuery(id+"F0.wireOp",EDGE,"E19.trimOffspring"),sQuery(id+"F0.wireOp",EDGE,"E20.trimOffspring"),subQ0,sQuery(id+"F0.wireOp",EDGE,"E26.trimOffspring"),sQuery(id+"F0.wireOp",EDGE,"E27.trimOffspring"),sQuery(id+"F0.wireOp",EDGE,"E31.trimOffspring"),sQuery(id+"F0.wireOp",EDGE,"E34.trimOffspring")])],"isStart":true})]});}
            var Q121;
            {var subQ0=sQuery(id+"F0.wireOp",EDGE,"E34.trimOffspring");Q121=makeQuery(id+"F2.opFillet","BLEND_EDGE",EDGE,{"blendedFrom":[makeQuery(id+"F1.opExtrude","CAP_EDGE",EDGE,{"disambiguationData":[OSD([subQ0])],"isStart":true}),makeQuery(id+"F1.opExtrude","CAP_FACE",FACE,{"disambiguationData":[OSD([sQuery(id+"F0.wireOp",EDGE,"E0"),sQuery(id+"F0.wireOp",EDGE,"E2"),sQuery(id+"F0.wireOp",EDGE,"E5.0"),sQuery(id+"F0.wireOp",EDGE,"E5.1"),sQuery(id+"F0.wireOp",EDGE,"E5.2"),sQuery(id+"F0.wireOp",EDGE,"E5.3"),sQuery(id+"F0.wireOp",EDGE,"E5.4"),sQuery(id+"F0.wireOp",EDGE,"E5.5"),sQuery(id+"F0.wireOp",EDGE,"E6.0"),sQuery(id+"F0.wireOp",EDGE,"E6.1"),sQuery(id+"F0.wireOp",EDGE,"E6.2"),sQuery(id+"F0.wireOp",EDGE,"E6.3"),sQuery(id+"F0.wireOp",EDGE,"E6.4"),sQuery(id+"F0.wireOp",EDGE,"E6.5"),sQuery(id+"F0.wireOp",EDGE,"E7.0"),sQuery(id+"F0.wireOp",EDGE,"E7.1"),sQuery(id+"F0.wireOp",EDGE,"E7.2"),sQuery(id+"F0.wireOp",EDGE,"E7.3"),sQuery(id+"F0.wireOp",EDGE,"E7.4"),sQuery(id+"F0.wireOp",EDGE,"E7.5"),sQuery(id+"F0.wireOp",EDGE,"E8.0"),sQuery(id+"F0.wireOp",EDGE,"E8.1"),sQuery(id+"F0.wireOp",EDGE,"E8.2"),sQuery(id+"F0.wireOp",EDGE,"E8.3"),sQuery(id+"F0.wireOp",EDGE,"E8.4"),sQuery(id+"F0.wireOp",EDGE,"E8.5"),sQuery(id+"F0.wireOp",EDGE,"E9"),sQuery(id+"F0.wireOp",EDGE,"E10"),sQuery(id+"F0.wireOp",EDGE,"E11"),sQuery(id+"F0.wireOp",EDGE,"E12"),sQuery(id+"F0.wireOp",EDGE,"E13"),sQuery(id+"F0.wireOp",EDGE,"E14"),sQuery(id+"F0.wireOp",EDGE,"E15"),sQuery(id+"F0.wireOp",EDGE,"E16"),sQuery(id+"F0.wireOp",EDGE,"E19.trimOffspring"),sQuery(id+"F0.wireOp",EDGE,"E20.trimOffspring"),sQuery(id+"F0.wireOp",EDGE,"E23.trimOffspring"),sQuery(id+"F0.wireOp",EDGE,"E26.trimOffspring"),sQuery(id+"F0.wireOp",EDGE,"E27.trimOffspring"),sQuery(id+"F0.wireOp",EDGE,"E31.trimOffspring"),subQ0])],"isStart":true})],"blendedInto":[makeQuery(id+"F1.opExtrude","CAP_FACE",FACE,{"disambiguationData":[OSD([sQuery(id+"F0.wireOp",EDGE,"E0"),sQuery(id+"F0.wireOp",EDGE,"E2"),sQuery(id+"F0.wireOp",EDGE,"E5.0"),sQuery(id+"F0.wireOp",EDGE,"E5.1"),sQuery(id+"F0.wireOp",EDGE,"E5.2"),sQuery(id+"F0.wireOp",EDGE,"E5.3"),sQuery(id+"F0.wireOp",EDGE,"E5.4"),sQuery(id+"F0.wireOp",EDGE,"E5.5"),sQuery(id+"F0.wireOp",EDGE,"E6.0"),sQuery(id+"F0.wireOp",EDGE,"E6.1"),sQuery(id+"F0.wireOp",EDGE,"E6.2"),sQuery(id+"F0.wireOp",EDGE,"E6.3"),sQuery(id+"F0.wireOp",EDGE,"E6.4"),sQuery(id+"F0.wireOp",EDGE,"E6.5"),sQuery(id+"F0.wireOp",EDGE,"E7.0"),sQuery(id+"F0.wireOp",EDGE,"E7.1"),sQuery(id+"F0.wireOp",EDGE,"E7.2"),sQuery(id+"F0.wireOp",EDGE,"E7.3"),sQuery(id+"F0.wireOp",EDGE,"E7.4"),sQuery(id+"F0.wireOp",EDGE,"E7.5"),sQuery(id+"F0.wireOp",EDGE,"E8.0"),sQuery(id+"F0.wireOp",EDGE,"E8.1"),sQuery(id+"F0.wireOp",EDGE,"E8.2"),sQuery(id+"F0.wireOp",EDGE,"E8.3"),sQuery(id+"F0.wireOp",EDGE,"E8.4"),sQuery(id+"F0.wireOp",EDGE,"E8.5"),sQuery(id+"F0.wireOp",EDGE,"E9"),sQuery(id+"F0.wireOp",EDGE,"E10"),sQuery(id+"F0.wireOp",EDGE,"E11"),sQuery(id+"F0.wireOp",EDGE,"E12"),sQuery(id+"F0.wireOp",EDGE,"E13"),sQuery(id+"F0.wireOp",EDGE,"E14"),sQuery(id+"F0.wireOp",EDGE,"E15"),sQuery(id+"F0.wireOp",EDGE,"E16"),sQuery(id+"F0.wireOp",EDGE,"E19.trimOffspring"),sQuery(id+"F0.wireOp",EDGE,"E20.trimOffspring"),sQuery(id+"F0.wireOp",EDGE,"E23.trimOffspring"),sQuery(id+"F0.wireOp",EDGE,"E26.trimOffspring"),sQuery(id+"F0.wireOp",EDGE,"E27.trimOffspring"),sQuery(id+"F0.wireOp",EDGE,"E31.trimOffspring"),subQ0])],"isStart":true})]});}
            var Q122;
            {var subQ0=sQuery(id+"F0.wireOp",EDGE,"E16");Q122=makeQuery(id+"F2.opFillet","BLEND_EDGE",EDGE,{"blendedFrom":[makeQuery(id+"F1.opExtrude","CAP_VERTEX",VERTEX,{"disambiguationData":[OSD([subQ0,sQuery(id+"F0.wireOp",EDGE,"E26.trimOffspring")])],"isStart":false}),makeQuery(id+"F1.opExtrude","CAP_EDGE",EDGE,{"disambiguationData":[OSD([subQ0])],"isStart":false})],"blendedInto":[]});}
            var Q123;
            Q123=makeQuery(id+"F2.opFillet","BLEND_EDGE",EDGE,{"blendedFrom":[makeQuery(id+"F1.opExtrude","CAP_EDGE",EDGE,{"disambiguationData":[OSD([sQuery(id+"F0.wireOp",EDGE,"E10")])],"isStart":true}),makeQuery(id+"F1.opExtrude","CAP_EDGE",EDGE,{"disambiguationData":[OSD([sQuery(id+"F0.wireOp",EDGE,"E34.trimOffspring")])],"isStart":true})],"blendedInto":[]});
            var Q124;
            Q124=makeQuery(id+"F2.opFillet","BLEND_EDGE",EDGE,{"blendedFrom":[makeQuery(id+"F1.opExtrude","CAP_EDGE",EDGE,{"disambiguationData":[OSD([sQuery(id+"F0.wireOp",EDGE,"E12")])],"isStart":true}),makeQuery(id+"F1.opExtrude","CAP_EDGE",EDGE,{"disambiguationData":[OSD([sQuery(id+"F0.wireOp",EDGE,"E27.trimOffspring")])],"isStart":true})],"blendedInto":[]});
            var Q125;
            {var subQ0=sQuery(id+"F0.wireOp",EDGE,"E34.trimOffspring");Q125=makeQuery(id+"F2.opFillet","BLEND_EDGE",EDGE,{"blendedFrom":[makeQuery(id+"F1.opExtrude","CAP_EDGE",EDGE,{"disambiguationData":[OSD([subQ0])],"isStart":true}),makeQuery(id+"F1.opExtrude","SWEPT_FACE",FACE,{"disambiguationData":[OSD([subQ0])]})],"blendedInto":[makeQuery(id+"F1.opExtrude","SWEPT_FACE",FACE,{"disambiguationData":[OSD([subQ0])]})]});}
            var Q126;
            {var subQ0=sQuery(id+"F0.wireOp",EDGE,"E23.trimOffspring");Q126=makeQuery(id+"F2.opFillet","BLEND_EDGE",EDGE,{"blendedFrom":[makeQuery(id+"F1.opExtrude","CAP_EDGE",EDGE,{"disambiguationData":[OSD([subQ0])],"isStart":false}),makeQuery(id+"F1.opExtrude","CAP_FACE",FACE,{"disambiguationData":[OSD([sQuery(id+"F0.wireOp",EDGE,"E0"),sQuery(id+"F0.wireOp",EDGE,"E2"),sQuery(id+"F0.wireOp",EDGE,"E5.0"),sQuery(id+"F0.wireOp",EDGE,"E5.1"),sQuery(id+"F0.wireOp",EDGE,"E5.2"),sQuery(id+"F0.wireOp",EDGE,"E5.3"),sQuery(id+"F0.wireOp",EDGE,"E5.4"),sQuery(id+"F0.wireOp",EDGE,"E5.5"),sQuery(id+"F0.wireOp",EDGE,"E6.0"),sQuery(id+"F0.wireOp",EDGE,"E6.1"),sQuery(id+"F0.wireOp",EDGE,"E6.2"),sQuery(id+"F0.wireOp",EDGE,"E6.3"),sQuery(id+"F0.wireOp",EDGE,"E6.4"),sQuery(id+"F0.wireOp",EDGE,"E6.5"),sQuery(id+"F0.wireOp",EDGE,"E7.0"),sQuery(id+"F0.wireOp",EDGE,"E7.1"),sQuery(id+"F0.wireOp",EDGE,"E7.2"),sQuery(id+"F0.wireOp",EDGE,"E7.3"),sQuery(id+"F0.wireOp",EDGE,"E7.4"),sQuery(id+"F0.wireOp",EDGE,"E7.5"),sQuery(id+"F0.wireOp",EDGE,"E8.0"),sQuery(id+"F0.wireOp",EDGE,"E8.1"),sQuery(id+"F0.wireOp",EDGE,"E8.2"),sQuery(id+"F0.wireOp",EDGE,"E8.3"),sQuery(id+"F0.wireOp",EDGE,"E8.4"),sQuery(id+"F0.wireOp",EDGE,"E8.5"),sQuery(id+"F0.wireOp",EDGE,"E9"),sQuery(id+"F0.wireOp",EDGE,"E10"),sQuery(id+"F0.wireOp",EDGE,"E11"),sQuery(id+"F0.wireOp",EDGE,"E12"),sQuery(id+"F0.wireOp",EDGE,"E13"),sQuery(id+"F0.wireOp",EDGE,"E14"),sQuery(id+"F0.wireOp",EDGE,"E15"),sQuery(id+"F0.wireOp",EDGE,"E16"),sQuery(id+"F0.wireOp",EDGE,"E19.trimOffspring"),sQuery(id+"F0.wireOp",EDGE,"E20.trimOffspring"),subQ0,sQuery(id+"F0.wireOp",EDGE,"E26.trimOffspring"),sQuery(id+"F0.wireOp",EDGE,"E27.trimOffspring"),sQuery(id+"F0.wireOp",EDGE,"E31.trimOffspring"),sQuery(id+"F0.wireOp",EDGE,"E34.trimOffspring")])],"isStart":false})],"blendedInto":[makeQuery(id+"F1.opExtrude","CAP_FACE",FACE,{"disambiguationData":[OSD([sQuery(id+"F0.wireOp",EDGE,"E0"),sQuery(id+"F0.wireOp",EDGE,"E2"),sQuery(id+"F0.wireOp",EDGE,"E5.0"),sQuery(id+"F0.wireOp",EDGE,"E5.1"),sQuery(id+"F0.wireOp",EDGE,"E5.2"),sQuery(id+"F0.wireOp",EDGE,"E5.3"),sQuery(id+"F0.wireOp",EDGE,"E5.4"),sQuery(id+"F0.wireOp",EDGE,"E5.5"),sQuery(id+"F0.wireOp",EDGE,"E6.0"),sQuery(id+"F0.wireOp",EDGE,"E6.1"),sQuery(id+"F0.wireOp",EDGE,"E6.2"),sQuery(id+"F0.wireOp",EDGE,"E6.3"),sQuery(id+"F0.wireOp",EDGE,"E6.4"),sQuery(id+"F0.wireOp",EDGE,"E6.5"),sQuery(id+"F0.wireOp",EDGE,"E7.0"),sQuery(id+"F0.wireOp",EDGE,"E7.1"),sQuery(id+"F0.wireOp",EDGE,"E7.2"),sQuery(id+"F0.wireOp",EDGE,"E7.3"),sQuery(id+"F0.wireOp",EDGE,"E7.4"),sQuery(id+"F0.wireOp",EDGE,"E7.5"),sQuery(id+"F0.wireOp",EDGE,"E8.0"),sQuery(id+"F0.wireOp",EDGE,"E8.1"),sQuery(id+"F0.wireOp",EDGE,"E8.2"),sQuery(id+"F0.wireOp",EDGE,"E8.3"),sQuery(id+"F0.wireOp",EDGE,"E8.4"),sQuery(id+"F0.wireOp",EDGE,"E8.5"),sQuery(id+"F0.wireOp",EDGE,"E9"),sQuery(id+"F0.wireOp",EDGE,"E10"),sQuery(id+"F0.wireOp",EDGE,"E11"),sQuery(id+"F0.wireOp",EDGE,"E12"),sQuery(id+"F0.wireOp",EDGE,"E13"),sQuery(id+"F0.wireOp",EDGE,"E14"),sQuery(id+"F0.wireOp",EDGE,"E15"),sQuery(id+"F0.wireOp",EDGE,"E16"),sQuery(id+"F0.wireOp",EDGE,"E19.trimOffspring"),sQuery(id+"F0.wireOp",EDGE,"E20.trimOffspring"),subQ0,sQuery(id+"F0.wireOp",EDGE,"E26.trimOffspring"),sQuery(id+"F0.wireOp",EDGE,"E27.trimOffspring"),sQuery(id+"F0.wireOp",EDGE,"E31.trimOffspring"),sQuery(id+"F0.wireOp",EDGE,"E34.trimOffspring")])],"isStart":false})]});}
            var Q127;
            {var subQ0=sQuery(id+"F0.wireOp",EDGE,"E26.trimOffspring");var subQ1=sQuery(id+"F0.wireOp",EDGE,"E16");Q127=makeQuery(id+"F2.opFillet","BLEND_EDGE",EDGE,{"blendedFrom":[makeQuery(id+"F1.opExtrude","CAP_VERTEX",VERTEX,{"disambiguationData":[OSD([subQ1,subQ0])],"isStart":false}),makeQuery(id+"F1.opExtrude","CAP_FACE",FACE,{"disambiguationData":[OSD([sQuery(id+"F0.wireOp",EDGE,"E0"),sQuery(id+"F0.wireOp",EDGE,"E2"),sQuery(id+"F0.wireOp",EDGE,"E5.0"),sQuery(id+"F0.wireOp",EDGE,"E5.1"),sQuery(id+"F0.wireOp",EDGE,"E5.2"),sQuery(id+"F0.wireOp",EDGE,"E5.3"),sQuery(id+"F0.wireOp",EDGE,"E5.4"),sQuery(id+"F0.wireOp",EDGE,"E5.5"),sQuery(id+"F0.wireOp",EDGE,"E6.0"),sQuery(id+"F0.wireOp",EDGE,"E6.1"),sQuery(id+"F0.wireOp",EDGE,"E6.2"),sQuery(id+"F0.wireOp",EDGE,"E6.3"),sQuery(id+"F0.wireOp",EDGE,"E6.4"),sQuery(id+"F0.wireOp",EDGE,"E6.5"),sQuery(id+"F0.wireOp",EDGE,"E7.0"),sQuery(id+"F0.wireOp",EDGE,"E7.1"),sQuery(id+"F0.wireOp",EDGE,"E7.2"),sQuery(id+"F0.wireOp",EDGE,"E7.3"),sQuery(id+"F0.wireOp",EDGE,"E7.4"),sQuery(id+"F0.wireOp",EDGE,"E7.5"),sQuery(id+"F0.wireOp",EDGE,"E8.0"),sQuery(id+"F0.wireOp",EDGE,"E8.1"),sQuery(id+"F0.wireOp",EDGE,"E8.2"),sQuery(id+"F0.wireOp",EDGE,"E8.3"),sQuery(id+"F0.wireOp",EDGE,"E8.4"),sQuery(id+"F0.wireOp",EDGE,"E8.5"),sQuery(id+"F0.wireOp",EDGE,"E9"),sQuery(id+"F0.wireOp",EDGE,"E10"),sQuery(id+"F0.wireOp",EDGE,"E11"),sQuery(id+"F0.wireOp",EDGE,"E12"),sQuery(id+"F0.wireOp",EDGE,"E13"),sQuery(id+"F0.wireOp",EDGE,"E14"),sQuery(id+"F0.wireOp",EDGE,"E15"),subQ1,sQuery(id+"F0.wireOp",EDGE,"E19.trimOffspring"),sQuery(id+"F0.wireOp",EDGE,"E20.trimOffspring"),sQuery(id+"F0.wireOp",EDGE,"E23.trimOffspring"),subQ0,sQuery(id+"F0.wireOp",EDGE,"E27.trimOffspring"),sQuery(id+"F0.wireOp",EDGE,"E31.trimOffspring"),sQuery(id+"F0.wireOp",EDGE,"E34.trimOffspring")])],"isStart":false})],"blendedInto":[makeQuery(id+"F1.opExtrude","CAP_FACE",FACE,{"disambiguationData":[OSD([sQuery(id+"F0.wireOp",EDGE,"E0"),sQuery(id+"F0.wireOp",EDGE,"E2"),sQuery(id+"F0.wireOp",EDGE,"E5.0"),sQuery(id+"F0.wireOp",EDGE,"E5.1"),sQuery(id+"F0.wireOp",EDGE,"E5.2"),sQuery(id+"F0.wireOp",EDGE,"E5.3"),sQuery(id+"F0.wireOp",EDGE,"E5.4"),sQuery(id+"F0.wireOp",EDGE,"E5.5"),sQuery(id+"F0.wireOp",EDGE,"E6.0"),sQuery(id+"F0.wireOp",EDGE,"E6.1"),sQuery(id+"F0.wireOp",EDGE,"E6.2"),sQuery(id+"F0.wireOp",EDGE,"E6.3"),sQuery(id+"F0.wireOp",EDGE,"E6.4"),sQuery(id+"F0.wireOp",EDGE,"E6.5"),sQuery(id+"F0.wireOp",EDGE,"E7.0"),sQuery(id+"F0.wireOp",EDGE,"E7.1"),sQuery(id+"F0.wireOp",EDGE,"E7.2"),sQuery(id+"F0.wireOp",EDGE,"E7.3"),sQuery(id+"F0.wireOp",EDGE,"E7.4"),sQuery(id+"F0.wireOp",EDGE,"E7.5"),sQuery(id+"F0.wireOp",EDGE,"E8.0"),sQuery(id+"F0.wireOp",EDGE,"E8.1"),sQuery(id+"F0.wireOp",EDGE,"E8.2"),sQuery(id+"F0.wireOp",EDGE,"E8.3"),sQuery(id+"F0.wireOp",EDGE,"E8.4"),sQuery(id+"F0.wireOp",EDGE,"E8.5"),sQuery(id+"F0.wireOp",EDGE,"E9"),sQuery(id+"F0.wireOp",EDGE,"E10"),sQuery(id+"F0.wireOp",EDGE,"E11"),sQuery(id+"F0.wireOp",EDGE,"E12"),sQuery(id+"F0.wireOp",EDGE,"E13"),sQuery(id+"F0.wireOp",EDGE,"E14"),sQuery(id+"F0.wireOp",EDGE,"E15"),subQ1,sQuery(id+"F0.wireOp",EDGE,"E19.trimOffspring"),sQuery(id+"F0.wireOp",EDGE,"E20.trimOffspring"),sQuery(id+"F0.wireOp",EDGE,"E23.trimOffspring"),subQ0,sQuery(id+"F0.wireOp",EDGE,"E27.trimOffspring"),sQuery(id+"F0.wireOp",EDGE,"E31.trimOffspring"),sQuery(id+"F0.wireOp",EDGE,"E34.trimOffspring")])],"isStart":false})]});}
            var Q128;
            {var subQ0=sQuery(id+"F0.wireOp",EDGE,"E23.trimOffspring");var subQ1=sQuery(id+"F0.wireOp",EDGE,"E20.trimOffspring");Q128=makeQuery(id+"F2.opFillet","BLEND_EDGE",EDGE,{"blendedFrom":[makeQuery(id+"F1.opExtrude","CAP_VERTEX",VERTEX,{"disambiguationData":[OSD([subQ1,subQ0])],"isStart":true}),makeQuery(id+"F1.opExtrude","SWEPT_EDGE",EDGE,{"disambiguationData":[OSD([subQ1,subQ0])]})],"blendedInto":[]});}
            var Q129;
            {var subQ0=sQuery(id+"F0.wireOp",EDGE,"E2");Q129=makeQuery(id+"F2.opFillet","BLEND_EDGE",EDGE,{"blendedFrom":[makeQuery(id+"F1.opExtrude","CAP_EDGE",EDGE,{"disambiguationData":[OSD([subQ0])],"isStart":true}),makeQuery(id+"F1.opExtrude","CAP_FACE",FACE,{"disambiguationData":[OSD([sQuery(id+"F0.wireOp",EDGE,"E0"),subQ0,sQuery(id+"F0.wireOp",EDGE,"E5.0"),sQuery(id+"F0.wireOp",EDGE,"E5.1"),sQuery(id+"F0.wireOp",EDGE,"E5.2"),sQuery(id+"F0.wireOp",EDGE,"E5.3"),sQuery(id+"F0.wireOp",EDGE,"E5.4"),sQuery(id+"F0.wireOp",EDGE,"E5.5"),sQuery(id+"F0.wireOp",EDGE,"E6.0"),sQuery(id+"F0.wireOp",EDGE,"E6.1"),sQuery(id+"F0.wireOp",EDGE,"E6.2"),sQuery(id+"F0.wireOp",EDGE,"E6.3"),sQuery(id+"F0.wireOp",EDGE,"E6.4"),sQuery(id+"F0.wireOp",EDGE,"E6.5"),sQuery(id+"F0.wireOp",EDGE,"E7.0"),sQuery(id+"F0.wireOp",EDGE,"E7.1"),sQuery(id+"F0.wireOp",EDGE,"E7.2"),sQuery(id+"F0.wireOp",EDGE,"E7.3"),sQuery(id+"F0.wireOp",EDGE,"E7.4"),sQuery(id+"F0.wireOp",EDGE,"E7.5"),sQuery(id+"F0.wireOp",EDGE,"E8.0"),sQuery(id+"F0.wireOp",EDGE,"E8.1"),sQuery(id+"F0.wireOp",EDGE,"E8.2"),sQuery(id+"F0.wireOp",EDGE,"E8.3"),sQuery(id+"F0.wireOp",EDGE,"E8.4"),sQuery(id+"F0.wireOp",EDGE,"E8.5"),sQuery(id+"F0.wireOp",EDGE,"E9"),sQuery(id+"F0.wireOp",EDGE,"E10"),sQuery(id+"F0.wireOp",EDGE,"E11"),sQuery(id+"F0.wireOp",EDGE,"E12"),sQuery(id+"F0.wireOp",EDGE,"E13"),sQuery(id+"F0.wireOp",EDGE,"E14"),sQuery(id+"F0.wireOp",EDGE,"E15"),sQuery(id+"F0.wireOp",EDGE,"E16"),sQuery(id+"F0.wireOp",EDGE,"E19.trimOffspring"),sQuery(id+"F0.wireOp",EDGE,"E20.trimOffspring"),sQuery(id+"F0.wireOp",EDGE,"E23.trimOffspring"),sQuery(id+"F0.wireOp",EDGE,"E26.trimOffspring"),sQuery(id+"F0.wireOp",EDGE,"E27.trimOffspring"),sQuery(id+"F0.wireOp",EDGE,"E31.trimOffspring"),sQuery(id+"F0.wireOp",EDGE,"E34.trimOffspring")])],"isStart":true})],"blendedInto":[makeQuery(id+"F1.opExtrude","CAP_FACE",FACE,{"disambiguationData":[OSD([sQuery(id+"F0.wireOp",EDGE,"E0"),subQ0,sQuery(id+"F0.wireOp",EDGE,"E5.0"),sQuery(id+"F0.wireOp",EDGE,"E5.1"),sQuery(id+"F0.wireOp",EDGE,"E5.2"),sQuery(id+"F0.wireOp",EDGE,"E5.3"),sQuery(id+"F0.wireOp",EDGE,"E5.4"),sQuery(id+"F0.wireOp",EDGE,"E5.5"),sQuery(id+"F0.wireOp",EDGE,"E6.0"),sQuery(id+"F0.wireOp",EDGE,"E6.1"),sQuery(id+"F0.wireOp",EDGE,"E6.2"),sQuery(id+"F0.wireOp",EDGE,"E6.3"),sQuery(id+"F0.wireOp",EDGE,"E6.4"),sQuery(id+"F0.wireOp",EDGE,"E6.5"),sQuery(id+"F0.wireOp",EDGE,"E7.0"),sQuery(id+"F0.wireOp",EDGE,"E7.1"),sQuery(id+"F0.wireOp",EDGE,"E7.2"),sQuery(id+"F0.wireOp",EDGE,"E7.3"),sQuery(id+"F0.wireOp",EDGE,"E7.4"),sQuery(id+"F0.wireOp",EDGE,"E7.5"),sQuery(id+"F0.wireOp",EDGE,"E8.0"),sQuery(id+"F0.wireOp",EDGE,"E8.1"),sQuery(id+"F0.wireOp",EDGE,"E8.2"),sQuery(id+"F0.wireOp",EDGE,"E8.3"),sQuery(id+"F0.wireOp",EDGE,"E8.4"),sQuery(id+"F0.wireOp",EDGE,"E8.5"),sQuery(id+"F0.wireOp",EDGE,"E9"),sQuery(id+"F0.wireOp",EDGE,"E10"),sQuery(id+"F0.wireOp",EDGE,"E11"),sQuery(id+"F0.wireOp",EDGE,"E12"),sQuery(id+"F0.wireOp",EDGE,"E13"),sQuery(id+"F0.wireOp",EDGE,"E14"),sQuery(id+"F0.wireOp",EDGE,"E15"),sQuery(id+"F0.wireOp",EDGE,"E16"),sQuery(id+"F0.wireOp",EDGE,"E19.trimOffspring"),sQuery(id+"F0.wireOp",EDGE,"E20.trimOffspring"),sQuery(id+"F0.wireOp",EDGE,"E23.trimOffspring"),sQuery(id+"F0.wireOp",EDGE,"E26.trimOffspring"),sQuery(id+"F0.wireOp",EDGE,"E27.trimOffspring"),sQuery(id+"F0.wireOp",EDGE,"E31.trimOffspring"),sQuery(id+"F0.wireOp",EDGE,"E34.trimOffspring")])],"isStart":true})]});}
            var Q130;
            {var subQ0=sQuery(id+"F0.wireOp",EDGE,"E16");Q130=makeQuery(id+"F2.opFillet","BLEND_EDGE",EDGE,{"blendedFrom":[makeQuery(id+"F1.opExtrude","CAP_EDGE",EDGE,{"disambiguationData":[OSD([subQ0])],"isStart":true}),makeQuery(id+"F1.opExtrude","CAP_FACE",FACE,{"disambiguationData":[OSD([sQuery(id+"F0.wireOp",EDGE,"E0"),sQuery(id+"F0.wireOp",EDGE,"E2"),sQuery(id+"F0.wireOp",EDGE,"E5.0"),sQuery(id+"F0.wireOp",EDGE,"E5.1"),sQuery(id+"F0.wireOp",EDGE,"E5.2"),sQuery(id+"F0.wireOp",EDGE,"E5.3"),sQuery(id+"F0.wireOp",EDGE,"E5.4"),sQuery(id+"F0.wireOp",EDGE,"E5.5"),sQuery(id+"F0.wireOp",EDGE,"E6.0"),sQuery(id+"F0.wireOp",EDGE,"E6.1"),sQuery(id+"F0.wireOp",EDGE,"E6.2"),sQuery(id+"F0.wireOp",EDGE,"E6.3"),sQuery(id+"F0.wireOp",EDGE,"E6.4"),sQuery(id+"F0.wireOp",EDGE,"E6.5"),sQuery(id+"F0.wireOp",EDGE,"E7.0"),sQuery(id+"F0.wireOp",EDGE,"E7.1"),sQuery(id+"F0.wireOp",EDGE,"E7.2"),sQuery(id+"F0.wireOp",EDGE,"E7.3"),sQuery(id+"F0.wireOp",EDGE,"E7.4"),sQuery(id+"F0.wireOp",EDGE,"E7.5"),sQuery(id+"F0.wireOp",EDGE,"E8.0"),sQuery(id+"F0.wireOp",EDGE,"E8.1"),sQuery(id+"F0.wireOp",EDGE,"E8.2"),sQuery(id+"F0.wireOp",EDGE,"E8.3"),sQuery(id+"F0.wireOp",EDGE,"E8.4"),sQuery(id+"F0.wireOp",EDGE,"E8.5"),sQuery(id+"F0.wireOp",EDGE,"E9"),sQuery(id+"F0.wireOp",EDGE,"E10"),sQuery(id+"F0.wireOp",EDGE,"E11"),sQuery(id+"F0.wireOp",EDGE,"E12"),sQuery(id+"F0.wireOp",EDGE,"E13"),sQuery(id+"F0.wireOp",EDGE,"E14"),sQuery(id+"F0.wireOp",EDGE,"E15"),subQ0,sQuery(id+"F0.wireOp",EDGE,"E19.trimOffspring"),sQuery(id+"F0.wireOp",EDGE,"E20.trimOffspring"),sQuery(id+"F0.wireOp",EDGE,"E23.trimOffspring"),sQuery(id+"F0.wireOp",EDGE,"E26.trimOffspring"),sQuery(id+"F0.wireOp",EDGE,"E27.trimOffspring"),sQuery(id+"F0.wireOp",EDGE,"E31.trimOffspring"),sQuery(id+"F0.wireOp",EDGE,"E34.trimOffspring")])],"isStart":true})],"blendedInto":[makeQuery(id+"F1.opExtrude","CAP_FACE",FACE,{"disambiguationData":[OSD([sQuery(id+"F0.wireOp",EDGE,"E0"),sQuery(id+"F0.wireOp",EDGE,"E2"),sQuery(id+"F0.wireOp",EDGE,"E5.0"),sQuery(id+"F0.wireOp",EDGE,"E5.1"),sQuery(id+"F0.wireOp",EDGE,"E5.2"),sQuery(id+"F0.wireOp",EDGE,"E5.3"),sQuery(id+"F0.wireOp",EDGE,"E5.4"),sQuery(id+"F0.wireOp",EDGE,"E5.5"),sQuery(id+"F0.wireOp",EDGE,"E6.0"),sQuery(id+"F0.wireOp",EDGE,"E6.1"),sQuery(id+"F0.wireOp",EDGE,"E6.2"),sQuery(id+"F0.wireOp",EDGE,"E6.3"),sQuery(id+"F0.wireOp",EDGE,"E6.4"),sQuery(id+"F0.wireOp",EDGE,"E6.5"),sQuery(id+"F0.wireOp",EDGE,"E7.0"),sQuery(id+"F0.wireOp",EDGE,"E7.1"),sQuery(id+"F0.wireOp",EDGE,"E7.2"),sQuery(id+"F0.wireOp",EDGE,"E7.3"),sQuery(id+"F0.wireOp",EDGE,"E7.4"),sQuery(id+"F0.wireOp",EDGE,"E7.5"),sQuery(id+"F0.wireOp",EDGE,"E8.0"),sQuery(id+"F0.wireOp",EDGE,"E8.1"),sQuery(id+"F0.wireOp",EDGE,"E8.2"),sQuery(id+"F0.wireOp",EDGE,"E8.3"),sQuery(id+"F0.wireOp",EDGE,"E8.4"),sQuery(id+"F0.wireOp",EDGE,"E8.5"),sQuery(id+"F0.wireOp",EDGE,"E9"),sQuery(id+"F0.wireOp",EDGE,"E10"),sQuery(id+"F0.wireOp",EDGE,"E11"),sQuery(id+"F0.wireOp",EDGE,"E12"),sQuery(id+"F0.wireOp",EDGE,"E13"),sQuery(id+"F0.wireOp",EDGE,"E14"),sQuery(id+"F0.wireOp",EDGE,"E15"),subQ0,sQuery(id+"F0.wireOp",EDGE,"E19.trimOffspring"),sQuery(id+"F0.wireOp",EDGE,"E20.trimOffspring"),sQuery(id+"F0.wireOp",EDGE,"E23.trimOffspring"),sQuery(id+"F0.wireOp",EDGE,"E26.trimOffspring"),sQuery(id+"F0.wireOp",EDGE,"E27.trimOffspring"),sQuery(id+"F0.wireOp",EDGE,"E31.trimOffspring"),sQuery(id+"F0.wireOp",EDGE,"E34.trimOffspring")])],"isStart":true})]});}
            var Q131;
            {var subQ0=sQuery(id+"F0.wireOp",EDGE,"E26.trimOffspring");Q131=makeQuery(id+"F2.opFillet","BLEND_EDGE",EDGE,{"blendedFrom":[makeQuery(id+"F1.opExtrude","CAP_EDGE",EDGE,{"disambiguationData":[OSD([subQ0])],"isStart":true}),makeQuery(id+"F1.opExtrude","CAP_FACE",FACE,{"disambiguationData":[OSD([sQuery(id+"F0.wireOp",EDGE,"E0"),sQuery(id+"F0.wireOp",EDGE,"E2"),sQuery(id+"F0.wireOp",EDGE,"E5.0"),sQuery(id+"F0.wireOp",EDGE,"E5.1"),sQuery(id+"F0.wireOp",EDGE,"E5.2"),sQuery(id+"F0.wireOp",EDGE,"E5.3"),sQuery(id+"F0.wireOp",EDGE,"E5.4"),sQuery(id+"F0.wireOp",EDGE,"E5.5"),sQuery(id+"F0.wireOp",EDGE,"E6.0"),sQuery(id+"F0.wireOp",EDGE,"E6.1"),sQuery(id+"F0.wireOp",EDGE,"E6.2"),sQuery(id+"F0.wireOp",EDGE,"E6.3"),sQuery(id+"F0.wireOp",EDGE,"E6.4"),sQuery(id+"F0.wireOp",EDGE,"E6.5"),sQuery(id+"F0.wireOp",EDGE,"E7.0"),sQuery(id+"F0.wireOp",EDGE,"E7.1"),sQuery(id+"F0.wireOp",EDGE,"E7.2"),sQuery(id+"F0.wireOp",EDGE,"E7.3"),sQuery(id+"F0.wireOp",EDGE,"E7.4"),sQuery(id+"F0.wireOp",EDGE,"E7.5"),sQuery(id+"F0.wireOp",EDGE,"E8.0"),sQuery(id+"F0.wireOp",EDGE,"E8.1"),sQuery(id+"F0.wireOp",EDGE,"E8.2"),sQuery(id+"F0.wireOp",EDGE,"E8.3"),sQuery(id+"F0.wireOp",EDGE,"E8.4"),sQuery(id+"F0.wireOp",EDGE,"E8.5"),sQuery(id+"F0.wireOp",EDGE,"E9"),sQuery(id+"F0.wireOp",EDGE,"E10"),sQuery(id+"F0.wireOp",EDGE,"E11"),sQuery(id+"F0.wireOp",EDGE,"E12"),sQuery(id+"F0.wireOp",EDGE,"E13"),sQuery(id+"F0.wireOp",EDGE,"E14"),sQuery(id+"F0.wireOp",EDGE,"E15"),sQuery(id+"F0.wireOp",EDGE,"E16"),sQuery(id+"F0.wireOp",EDGE,"E19.trimOffspring"),sQuery(id+"F0.wireOp",EDGE,"E20.trimOffspring"),sQuery(id+"F0.wireOp",EDGE,"E23.trimOffspring"),subQ0,sQuery(id+"F0.wireOp",EDGE,"E27.trimOffspring"),sQuery(id+"F0.wireOp",EDGE,"E31.trimOffspring"),sQuery(id+"F0.wireOp",EDGE,"E34.trimOffspring")])],"isStart":true})],"blendedInto":[makeQuery(id+"F1.opExtrude","CAP_FACE",FACE,{"disambiguationData":[OSD([sQuery(id+"F0.wireOp",EDGE,"E0"),sQuery(id+"F0.wireOp",EDGE,"E2"),sQuery(id+"F0.wireOp",EDGE,"E5.0"),sQuery(id+"F0.wireOp",EDGE,"E5.1"),sQuery(id+"F0.wireOp",EDGE,"E5.2"),sQuery(id+"F0.wireOp",EDGE,"E5.3"),sQuery(id+"F0.wireOp",EDGE,"E5.4"),sQuery(id+"F0.wireOp",EDGE,"E5.5"),sQuery(id+"F0.wireOp",EDGE,"E6.0"),sQuery(id+"F0.wireOp",EDGE,"E6.1"),sQuery(id+"F0.wireOp",EDGE,"E6.2"),sQuery(id+"F0.wireOp",EDGE,"E6.3"),sQuery(id+"F0.wireOp",EDGE,"E6.4"),sQuery(id+"F0.wireOp",EDGE,"E6.5"),sQuery(id+"F0.wireOp",EDGE,"E7.0"),sQuery(id+"F0.wireOp",EDGE,"E7.1"),sQuery(id+"F0.wireOp",EDGE,"E7.2"),sQuery(id+"F0.wireOp",EDGE,"E7.3"),sQuery(id+"F0.wireOp",EDGE,"E7.4"),sQuery(id+"F0.wireOp",EDGE,"E7.5"),sQuery(id+"F0.wireOp",EDGE,"E8.0"),sQuery(id+"F0.wireOp",EDGE,"E8.1"),sQuery(id+"F0.wireOp",EDGE,"E8.2"),sQuery(id+"F0.wireOp",EDGE,"E8.3"),sQuery(id+"F0.wireOp",EDGE,"E8.4"),sQuery(id+"F0.wireOp",EDGE,"E8.5"),sQuery(id+"F0.wireOp",EDGE,"E9"),sQuery(id+"F0.wireOp",EDGE,"E10"),sQuery(id+"F0.wireOp",EDGE,"E11"),sQuery(id+"F0.wireOp",EDGE,"E12"),sQuery(id+"F0.wireOp",EDGE,"E13"),sQuery(id+"F0.wireOp",EDGE,"E14"),sQuery(id+"F0.wireOp",EDGE,"E15"),sQuery(id+"F0.wireOp",EDGE,"E16"),sQuery(id+"F0.wireOp",EDGE,"E19.trimOffspring"),sQuery(id+"F0.wireOp",EDGE,"E20.trimOffspring"),sQuery(id+"F0.wireOp",EDGE,"E23.trimOffspring"),subQ0,sQuery(id+"F0.wireOp",EDGE,"E27.trimOffspring"),sQuery(id+"F0.wireOp",EDGE,"E31.trimOffspring"),sQuery(id+"F0.wireOp",EDGE,"E34.trimOffspring")])],"isStart":true})]});}
            var Q132;
            {var subQ0=sQuery(id+"F0.wireOp",EDGE,"E15");Q132=makeQuery(id+"F2.opFillet","BLEND_EDGE",EDGE,{"blendedFrom":[makeQuery(id+"F1.opExtrude","CAP_VERTEX",VERTEX,{"disambiguationData":[OSD([subQ0,sQuery(id+"F0.wireOp",EDGE,"E20.trimOffspring")])],"isStart":true}),makeQuery(id+"F1.opExtrude","CAP_EDGE",EDGE,{"disambiguationData":[OSD([subQ0])],"isStart":true})],"blendedInto":[]});}
            var Q133;
            {var subQ0=sQuery(id+"F0.wireOp",EDGE,"E20.trimOffspring");Q133=makeQuery(id+"F2.opFillet","BLEND_EDGE",EDGE,{"blendedFrom":[makeQuery(id+"F1.opExtrude","CAP_VERTEX",VERTEX,{"disambiguationData":[OSD([subQ0,sQuery(id+"F0.wireOp",EDGE,"E23.trimOffspring")])],"isStart":true}),makeQuery(id+"F1.opExtrude","CAP_EDGE",EDGE,{"disambiguationData":[OSD([subQ0])],"isStart":true})],"blendedInto":[]});}
            var Q134;
            {var subQ0=sQuery(id+"F0.wireOp",EDGE,"E27.trimOffspring");Q134=makeQuery(id+"F2.opFillet","BLEND_EDGE",EDGE,{"blendedFrom":[makeQuery(id+"F1.opExtrude","CAP_VERTEX",VERTEX,{"disambiguationData":[OSD([subQ0,sQuery(id+"F0.wireOp",EDGE,"E31.trimOffspring")])],"isStart":true}),makeQuery(id+"F1.opExtrude","CAP_EDGE",EDGE,{"disambiguationData":[OSD([subQ0])],"isStart":true})],"blendedInto":[]});}
            var Q135;
            {var subQ0=sQuery(id+"F0.wireOp",EDGE,"E2");Q135=makeQuery(id+"F2.opFillet","BLEND_EDGE",EDGE,{"blendedFrom":[makeQuery(id+"F1.opExtrude","CAP_EDGE",EDGE,{"disambiguationData":[OSD([subQ0])],"isStart":true}),makeQuery(id+"F1.opExtrude","SWEPT_FACE",FACE,{"disambiguationData":[OSD([subQ0])]})],"blendedInto":[makeQuery(id+"F1.opExtrude","SWEPT_FACE",FACE,{"disambiguationData":[OSD([subQ0])]})]});}
            var Q136;
            {var subQ0=sQuery(id+"F0.wireOp",EDGE,"E26.trimOffspring");Q136=makeQuery(id+"F2.opFillet","BLEND_EDGE",EDGE,{"blendedFrom":[makeQuery(id+"F1.opExtrude","CAP_EDGE",EDGE,{"disambiguationData":[OSD([subQ0])],"isStart":true}),makeQuery(id+"F1.opExtrude","SWEPT_FACE",FACE,{"disambiguationData":[OSD([subQ0])]})],"blendedInto":[makeQuery(id+"F1.opExtrude","SWEPT_FACE",FACE,{"disambiguationData":[OSD([subQ0])]})]});}
            var Q137;
            {var subQ0=sQuery(id+"F0.wireOp",EDGE,"E20.trimOffspring");Q137=makeQuery(id+"F2.opFillet","BLEND_EDGE",EDGE,{"blendedFrom":[makeQuery(id+"F1.opExtrude","CAP_VERTEX",VERTEX,{"disambiguationData":[OSD([sQuery(id+"F0.wireOp",EDGE,"E15"),subQ0])],"isStart":true}),makeQuery(id+"F1.opExtrude","CAP_EDGE",EDGE,{"disambiguationData":[OSD([subQ0])],"isStart":true})],"blendedInto":[]});}
            var Q138;
            {var subQ0=sQuery(id+"F0.wireOp",EDGE,"E23.trimOffspring");Q138=makeQuery(id+"F2.opFillet","BLEND_EDGE",EDGE,{"blendedFrom":[makeQuery(id+"F1.opExtrude","CAP_VERTEX",VERTEX,{"disambiguationData":[OSD([sQuery(id+"F0.wireOp",EDGE,"E20.trimOffspring"),subQ0])],"isStart":true}),makeQuery(id+"F1.opExtrude","CAP_EDGE",EDGE,{"disambiguationData":[OSD([subQ0])],"isStart":true})],"blendedInto":[]});}
            var Q139;
            {var subQ0=sQuery(id+"F0.wireOp",EDGE,"E31.trimOffspring");Q139=makeQuery(id+"F2.opFillet","BLEND_EDGE",EDGE,{"blendedFrom":[makeQuery(id+"F1.opExtrude","CAP_VERTEX",VERTEX,{"disambiguationData":[OSD([sQuery(id+"F0.wireOp",EDGE,"E27.trimOffspring"),subQ0])],"isStart":true}),makeQuery(id+"F1.opExtrude","CAP_EDGE",EDGE,{"disambiguationData":[OSD([subQ0])],"isStart":true})],"blendedInto":[]});}
            var Q140;
            {var subQ0=sQuery(id+"F0.wireOp",EDGE,"E2");Q140=makeQuery(id+"F2.opFillet","BLEND_EDGE",EDGE,{"blendedFrom":[makeQuery(id+"F1.opExtrude","CAP_EDGE",EDGE,{"disambiguationData":[OSD([subQ0])],"isStart":false}),makeQuery(id+"F1.opExtrude","CAP_FACE",FACE,{"disambiguationData":[OSD([sQuery(id+"F0.wireOp",EDGE,"E0"),subQ0,sQuery(id+"F0.wireOp",EDGE,"E5.0"),sQuery(id+"F0.wireOp",EDGE,"E5.1"),sQuery(id+"F0.wireOp",EDGE,"E5.2"),sQuery(id+"F0.wireOp",EDGE,"E5.3"),sQuery(id+"F0.wireOp",EDGE,"E5.4"),sQuery(id+"F0.wireOp",EDGE,"E5.5"),sQuery(id+"F0.wireOp",EDGE,"E6.0"),sQuery(id+"F0.wireOp",EDGE,"E6.1"),sQuery(id+"F0.wireOp",EDGE,"E6.2"),sQuery(id+"F0.wireOp",EDGE,"E6.3"),sQuery(id+"F0.wireOp",EDGE,"E6.4"),sQuery(id+"F0.wireOp",EDGE,"E6.5"),sQuery(id+"F0.wireOp",EDGE,"E7.0"),sQuery(id+"F0.wireOp",EDGE,"E7.1"),sQuery(id+"F0.wireOp",EDGE,"E7.2"),sQuery(id+"F0.wireOp",EDGE,"E7.3"),sQuery(id+"F0.wireOp",EDGE,"E7.4"),sQuery(id+"F0.wireOp",EDGE,"E7.5"),sQuery(id+"F0.wireOp",EDGE,"E8.0"),sQuery(id+"F0.wireOp",EDGE,"E8.1"),sQuery(id+"F0.wireOp",EDGE,"E8.2"),sQuery(id+"F0.wireOp",EDGE,"E8.3"),sQuery(id+"F0.wireOp",EDGE,"E8.4"),sQuery(id+"F0.wireOp",EDGE,"E8.5"),sQuery(id+"F0.wireOp",EDGE,"E9"),sQuery(id+"F0.wireOp",EDGE,"E10"),sQuery(id+"F0.wireOp",EDGE,"E11"),sQuery(id+"F0.wireOp",EDGE,"E12"),sQuery(id+"F0.wireOp",EDGE,"E13"),sQuery(id+"F0.wireOp",EDGE,"E14"),sQuery(id+"F0.wireOp",EDGE,"E15"),sQuery(id+"F0.wireOp",EDGE,"E16"),sQuery(id+"F0.wireOp",EDGE,"E19.trimOffspring"),sQuery(id+"F0.wireOp",EDGE,"E20.trimOffspring"),sQuery(id+"F0.wireOp",EDGE,"E23.trimOffspring"),sQuery(id+"F0.wireOp",EDGE,"E26.trimOffspring"),sQuery(id+"F0.wireOp",EDGE,"E27.trimOffspring"),sQuery(id+"F0.wireOp",EDGE,"E31.trimOffspring"),sQuery(id+"F0.wireOp",EDGE,"E34.trimOffspring")])],"isStart":false})],"blendedInto":[makeQuery(id+"F1.opExtrude","CAP_FACE",FACE,{"disambiguationData":[OSD([sQuery(id+"F0.wireOp",EDGE,"E0"),subQ0,sQuery(id+"F0.wireOp",EDGE,"E5.0"),sQuery(id+"F0.wireOp",EDGE,"E5.1"),sQuery(id+"F0.wireOp",EDGE,"E5.2"),sQuery(id+"F0.wireOp",EDGE,"E5.3"),sQuery(id+"F0.wireOp",EDGE,"E5.4"),sQuery(id+"F0.wireOp",EDGE,"E5.5"),sQuery(id+"F0.wireOp",EDGE,"E6.0"),sQuery(id+"F0.wireOp",EDGE,"E6.1"),sQuery(id+"F0.wireOp",EDGE,"E6.2"),sQuery(id+"F0.wireOp",EDGE,"E6.3"),sQuery(id+"F0.wireOp",EDGE,"E6.4"),sQuery(id+"F0.wireOp",EDGE,"E6.5"),sQuery(id+"F0.wireOp",EDGE,"E7.0"),sQuery(id+"F0.wireOp",EDGE,"E7.1"),sQuery(id+"F0.wireOp",EDGE,"E7.2"),sQuery(id+"F0.wireOp",EDGE,"E7.3"),sQuery(id+"F0.wireOp",EDGE,"E7.4"),sQuery(id+"F0.wireOp",EDGE,"E7.5"),sQuery(id+"F0.wireOp",EDGE,"E8.0"),sQuery(id+"F0.wireOp",EDGE,"E8.1"),sQuery(id+"F0.wireOp",EDGE,"E8.2"),sQuery(id+"F0.wireOp",EDGE,"E8.3"),sQuery(id+"F0.wireOp",EDGE,"E8.4"),sQuery(id+"F0.wireOp",EDGE,"E8.5"),sQuery(id+"F0.wireOp",EDGE,"E9"),sQuery(id+"F0.wireOp",EDGE,"E10"),sQuery(id+"F0.wireOp",EDGE,"E11"),sQuery(id+"F0.wireOp",EDGE,"E12"),sQuery(id+"F0.wireOp",EDGE,"E13"),sQuery(id+"F0.wireOp",EDGE,"E14"),sQuery(id+"F0.wireOp",EDGE,"E15"),sQuery(id+"F0.wireOp",EDGE,"E16"),sQuery(id+"F0.wireOp",EDGE,"E19.trimOffspring"),sQuery(id+"F0.wireOp",EDGE,"E20.trimOffspring"),sQuery(id+"F0.wireOp",EDGE,"E23.trimOffspring"),sQuery(id+"F0.wireOp",EDGE,"E26.trimOffspring"),sQuery(id+"F0.wireOp",EDGE,"E27.trimOffspring"),sQuery(id+"F0.wireOp",EDGE,"E31.trimOffspring"),sQuery(id+"F0.wireOp",EDGE,"E34.trimOffspring")])],"isStart":false})]});}
            var Q141;
            {var subQ0=sQuery(id+"F0.wireOp",EDGE,"E16");Q141=makeQuery(id+"F2.opFillet","BLEND_EDGE",EDGE,{"blendedFrom":[makeQuery(id+"F1.opExtrude","CAP_EDGE",EDGE,{"disambiguationData":[OSD([subQ0])],"isStart":false}),makeQuery(id+"F1.opExtrude","CAP_FACE",FACE,{"disambiguationData":[OSD([sQuery(id+"F0.wireOp",EDGE,"E0"),sQuery(id+"F0.wireOp",EDGE,"E2"),sQuery(id+"F0.wireOp",EDGE,"E5.0"),sQuery(id+"F0.wireOp",EDGE,"E5.1"),sQuery(id+"F0.wireOp",EDGE,"E5.2"),sQuery(id+"F0.wireOp",EDGE,"E5.3"),sQuery(id+"F0.wireOp",EDGE,"E5.4"),sQuery(id+"F0.wireOp",EDGE,"E5.5"),sQuery(id+"F0.wireOp",EDGE,"E6.0"),sQuery(id+"F0.wireOp",EDGE,"E6.1"),sQuery(id+"F0.wireOp",EDGE,"E6.2"),sQuery(id+"F0.wireOp",EDGE,"E6.3"),sQuery(id+"F0.wireOp",EDGE,"E6.4"),sQuery(id+"F0.wireOp",EDGE,"E6.5"),sQuery(id+"F0.wireOp",EDGE,"E7.0"),sQuery(id+"F0.wireOp",EDGE,"E7.1"),sQuery(id+"F0.wireOp",EDGE,"E7.2"),sQuery(id+"F0.wireOp",EDGE,"E7.3"),sQuery(id+"F0.wireOp",EDGE,"E7.4"),sQuery(id+"F0.wireOp",EDGE,"E7.5"),sQuery(id+"F0.wireOp",EDGE,"E8.0"),sQuery(id+"F0.wireOp",EDGE,"E8.1"),sQuery(id+"F0.wireOp",EDGE,"E8.2"),sQuery(id+"F0.wireOp",EDGE,"E8.3"),sQuery(id+"F0.wireOp",EDGE,"E8.4"),sQuery(id+"F0.wireOp",EDGE,"E8.5"),sQuery(id+"F0.wireOp",EDGE,"E9"),sQuery(id+"F0.wireOp",EDGE,"E10"),sQuery(id+"F0.wireOp",EDGE,"E11"),sQuery(id+"F0.wireOp",EDGE,"E12"),sQuery(id+"F0.wireOp",EDGE,"E13"),sQuery(id+"F0.wireOp",EDGE,"E14"),sQuery(id+"F0.wireOp",EDGE,"E15"),subQ0,sQuery(id+"F0.wireOp",EDGE,"E19.trimOffspring"),sQuery(id+"F0.wireOp",EDGE,"E20.trimOffspring"),sQuery(id+"F0.wireOp",EDGE,"E23.trimOffspring"),sQuery(id+"F0.wireOp",EDGE,"E26.trimOffspring"),sQuery(id+"F0.wireOp",EDGE,"E27.trimOffspring"),sQuery(id+"F0.wireOp",EDGE,"E31.trimOffspring"),sQuery(id+"F0.wireOp",EDGE,"E34.trimOffspring")])],"isStart":false})],"blendedInto":[makeQuery(id+"F1.opExtrude","CAP_FACE",FACE,{"disambiguationData":[OSD([sQuery(id+"F0.wireOp",EDGE,"E0"),sQuery(id+"F0.wireOp",EDGE,"E2"),sQuery(id+"F0.wireOp",EDGE,"E5.0"),sQuery(id+"F0.wireOp",EDGE,"E5.1"),sQuery(id+"F0.wireOp",EDGE,"E5.2"),sQuery(id+"F0.wireOp",EDGE,"E5.3"),sQuery(id+"F0.wireOp",EDGE,"E5.4"),sQuery(id+"F0.wireOp",EDGE,"E5.5"),sQuery(id+"F0.wireOp",EDGE,"E6.0"),sQuery(id+"F0.wireOp",EDGE,"E6.1"),sQuery(id+"F0.wireOp",EDGE,"E6.2"),sQuery(id+"F0.wireOp",EDGE,"E6.3"),sQuery(id+"F0.wireOp",EDGE,"E6.4"),sQuery(id+"F0.wireOp",EDGE,"E6.5"),sQuery(id+"F0.wireOp",EDGE,"E7.0"),sQuery(id+"F0.wireOp",EDGE,"E7.1"),sQuery(id+"F0.wireOp",EDGE,"E7.2"),sQuery(id+"F0.wireOp",EDGE,"E7.3"),sQuery(id+"F0.wireOp",EDGE,"E7.4"),sQuery(id+"F0.wireOp",EDGE,"E7.5"),sQuery(id+"F0.wireOp",EDGE,"E8.0"),sQuery(id+"F0.wireOp",EDGE,"E8.1"),sQuery(id+"F0.wireOp",EDGE,"E8.2"),sQuery(id+"F0.wireOp",EDGE,"E8.3"),sQuery(id+"F0.wireOp",EDGE,"E8.4"),sQuery(id+"F0.wireOp",EDGE,"E8.5"),sQuery(id+"F0.wireOp",EDGE,"E9"),sQuery(id+"F0.wireOp",EDGE,"E10"),sQuery(id+"F0.wireOp",EDGE,"E11"),sQuery(id+"F0.wireOp",EDGE,"E12"),sQuery(id+"F0.wireOp",EDGE,"E13"),sQuery(id+"F0.wireOp",EDGE,"E14"),sQuery(id+"F0.wireOp",EDGE,"E15"),subQ0,sQuery(id+"F0.wireOp",EDGE,"E19.trimOffspring"),sQuery(id+"F0.wireOp",EDGE,"E20.trimOffspring"),sQuery(id+"F0.wireOp",EDGE,"E23.trimOffspring"),sQuery(id+"F0.wireOp",EDGE,"E26.trimOffspring"),sQuery(id+"F0.wireOp",EDGE,"E27.trimOffspring"),sQuery(id+"F0.wireOp",EDGE,"E31.trimOffspring"),sQuery(id+"F0.wireOp",EDGE,"E34.trimOffspring")])],"isStart":false})]});}
            var Q142;
            {var subQ0=sQuery(id+"F0.wireOp",EDGE,"E20.trimOffspring");var subQ1=sQuery(id+"F0.wireOp",EDGE,"E15");Q142=makeQuery(id+"F2.opFillet","BLEND_EDGE",EDGE,{"blendedFrom":[makeQuery(id+"F1.opExtrude","CAP_VERTEX",VERTEX,{"disambiguationData":[OSD([subQ1,subQ0])],"isStart":true}),makeQuery(id+"F1.opExtrude","CAP_FACE",FACE,{"disambiguationData":[OSD([sQuery(id+"F0.wireOp",EDGE,"E0"),sQuery(id+"F0.wireOp",EDGE,"E2"),sQuery(id+"F0.wireOp",EDGE,"E5.0"),sQuery(id+"F0.wireOp",EDGE,"E5.1"),sQuery(id+"F0.wireOp",EDGE,"E5.2"),sQuery(id+"F0.wireOp",EDGE,"E5.3"),sQuery(id+"F0.wireOp",EDGE,"E5.4"),sQuery(id+"F0.wireOp",EDGE,"E5.5"),sQuery(id+"F0.wireOp",EDGE,"E6.0"),sQuery(id+"F0.wireOp",EDGE,"E6.1"),sQuery(id+"F0.wireOp",EDGE,"E6.2"),sQuery(id+"F0.wireOp",EDGE,"E6.3"),sQuery(id+"F0.wireOp",EDGE,"E6.4"),sQuery(id+"F0.wireOp",EDGE,"E6.5"),sQuery(id+"F0.wireOp",EDGE,"E7.0"),sQuery(id+"F0.wireOp",EDGE,"E7.1"),sQuery(id+"F0.wireOp",EDGE,"E7.2"),sQuery(id+"F0.wireOp",EDGE,"E7.3"),sQuery(id+"F0.wireOp",EDGE,"E7.4"),sQuery(id+"F0.wireOp",EDGE,"E7.5"),sQuery(id+"F0.wireOp",EDGE,"E8.0"),sQuery(id+"F0.wireOp",EDGE,"E8.1"),sQuery(id+"F0.wireOp",EDGE,"E8.2"),sQuery(id+"F0.wireOp",EDGE,"E8.3"),sQuery(id+"F0.wireOp",EDGE,"E8.4"),sQuery(id+"F0.wireOp",EDGE,"E8.5"),sQuery(id+"F0.wireOp",EDGE,"E9"),sQuery(id+"F0.wireOp",EDGE,"E10"),sQuery(id+"F0.wireOp",EDGE,"E11"),sQuery(id+"F0.wireOp",EDGE,"E12"),sQuery(id+"F0.wireOp",EDGE,"E13"),sQuery(id+"F0.wireOp",EDGE,"E14"),subQ1,sQuery(id+"F0.wireOp",EDGE,"E16"),sQuery(id+"F0.wireOp",EDGE,"E19.trimOffspring"),subQ0,sQuery(id+"F0.wireOp",EDGE,"E23.trimOffspring"),sQuery(id+"F0.wireOp",EDGE,"E26.trimOffspring"),sQuery(id+"F0.wireOp",EDGE,"E27.trimOffspring"),sQuery(id+"F0.wireOp",EDGE,"E31.trimOffspring"),sQuery(id+"F0.wireOp",EDGE,"E34.trimOffspring")])],"isStart":true})],"blendedInto":[makeQuery(id+"F1.opExtrude","CAP_FACE",FACE,{"disambiguationData":[OSD([sQuery(id+"F0.wireOp",EDGE,"E0"),sQuery(id+"F0.wireOp",EDGE,"E2"),sQuery(id+"F0.wireOp",EDGE,"E5.0"),sQuery(id+"F0.wireOp",EDGE,"E5.1"),sQuery(id+"F0.wireOp",EDGE,"E5.2"),sQuery(id+"F0.wireOp",EDGE,"E5.3"),sQuery(id+"F0.wireOp",EDGE,"E5.4"),sQuery(id+"F0.wireOp",EDGE,"E5.5"),sQuery(id+"F0.wireOp",EDGE,"E6.0"),sQuery(id+"F0.wireOp",EDGE,"E6.1"),sQuery(id+"F0.wireOp",EDGE,"E6.2"),sQuery(id+"F0.wireOp",EDGE,"E6.3"),sQuery(id+"F0.wireOp",EDGE,"E6.4"),sQuery(id+"F0.wireOp",EDGE,"E6.5"),sQuery(id+"F0.wireOp",EDGE,"E7.0"),sQuery(id+"F0.wireOp",EDGE,"E7.1"),sQuery(id+"F0.wireOp",EDGE,"E7.2"),sQuery(id+"F0.wireOp",EDGE,"E7.3"),sQuery(id+"F0.wireOp",EDGE,"E7.4"),sQuery(id+"F0.wireOp",EDGE,"E7.5"),sQuery(id+"F0.wireOp",EDGE,"E8.0"),sQuery(id+"F0.wireOp",EDGE,"E8.1"),sQuery(id+"F0.wireOp",EDGE,"E8.2"),sQuery(id+"F0.wireOp",EDGE,"E8.3"),sQuery(id+"F0.wireOp",EDGE,"E8.4"),sQuery(id+"F0.wireOp",EDGE,"E8.5"),sQuery(id+"F0.wireOp",EDGE,"E9"),sQuery(id+"F0.wireOp",EDGE,"E10"),sQuery(id+"F0.wireOp",EDGE,"E11"),sQuery(id+"F0.wireOp",EDGE,"E12"),sQuery(id+"F0.wireOp",EDGE,"E13"),sQuery(id+"F0.wireOp",EDGE,"E14"),subQ1,sQuery(id+"F0.wireOp",EDGE,"E16"),sQuery(id+"F0.wireOp",EDGE,"E19.trimOffspring"),subQ0,sQuery(id+"F0.wireOp",EDGE,"E23.trimOffspring"),sQuery(id+"F0.wireOp",EDGE,"E26.trimOffspring"),sQuery(id+"F0.wireOp",EDGE,"E27.trimOffspring"),sQuery(id+"F0.wireOp",EDGE,"E31.trimOffspring"),sQuery(id+"F0.wireOp",EDGE,"E34.trimOffspring")])],"isStart":true})]});}
            var Q143;
            {var subQ0=sQuery(id+"F0.wireOp",EDGE,"E31.trimOffspring");var subQ1=sQuery(id+"F0.wireOp",EDGE,"E27.trimOffspring");Q143=makeQuery(id+"F2.opFillet","BLEND_EDGE",EDGE,{"blendedFrom":[makeQuery(id+"F1.opExtrude","CAP_VERTEX",VERTEX,{"disambiguationData":[OSD([subQ1,subQ0])],"isStart":true}),makeQuery(id+"F1.opExtrude","CAP_FACE",FACE,{"disambiguationData":[OSD([sQuery(id+"F0.wireOp",EDGE,"E0"),sQuery(id+"F0.wireOp",EDGE,"E2"),sQuery(id+"F0.wireOp",EDGE,"E5.0"),sQuery(id+"F0.wireOp",EDGE,"E5.1"),sQuery(id+"F0.wireOp",EDGE,"E5.2"),sQuery(id+"F0.wireOp",EDGE,"E5.3"),sQuery(id+"F0.wireOp",EDGE,"E5.4"),sQuery(id+"F0.wireOp",EDGE,"E5.5"),sQuery(id+"F0.wireOp",EDGE,"E6.0"),sQuery(id+"F0.wireOp",EDGE,"E6.1"),sQuery(id+"F0.wireOp",EDGE,"E6.2"),sQuery(id+"F0.wireOp",EDGE,"E6.3"),sQuery(id+"F0.wireOp",EDGE,"E6.4"),sQuery(id+"F0.wireOp",EDGE,"E6.5"),sQuery(id+"F0.wireOp",EDGE,"E7.0"),sQuery(id+"F0.wireOp",EDGE,"E7.1"),sQuery(id+"F0.wireOp",EDGE,"E7.2"),sQuery(id+"F0.wireOp",EDGE,"E7.3"),sQuery(id+"F0.wireOp",EDGE,"E7.4"),sQuery(id+"F0.wireOp",EDGE,"E7.5"),sQuery(id+"F0.wireOp",EDGE,"E8.0"),sQuery(id+"F0.wireOp",EDGE,"E8.1"),sQuery(id+"F0.wireOp",EDGE,"E8.2"),sQuery(id+"F0.wireOp",EDGE,"E8.3"),sQuery(id+"F0.wireOp",EDGE,"E8.4"),sQuery(id+"F0.wireOp",EDGE,"E8.5"),sQuery(id+"F0.wireOp",EDGE,"E9"),sQuery(id+"F0.wireOp",EDGE,"E10"),sQuery(id+"F0.wireOp",EDGE,"E11"),sQuery(id+"F0.wireOp",EDGE,"E12"),sQuery(id+"F0.wireOp",EDGE,"E13"),sQuery(id+"F0.wireOp",EDGE,"E14"),sQuery(id+"F0.wireOp",EDGE,"E15"),sQuery(id+"F0.wireOp",EDGE,"E16"),sQuery(id+"F0.wireOp",EDGE,"E19.trimOffspring"),sQuery(id+"F0.wireOp",EDGE,"E20.trimOffspring"),sQuery(id+"F0.wireOp",EDGE,"E23.trimOffspring"),sQuery(id+"F0.wireOp",EDGE,"E26.trimOffspring"),subQ1,subQ0,sQuery(id+"F0.wireOp",EDGE,"E34.trimOffspring")])],"isStart":true})],"blendedInto":[makeQuery(id+"F1.opExtrude","CAP_FACE",FACE,{"disambiguationData":[OSD([sQuery(id+"F0.wireOp",EDGE,"E0"),sQuery(id+"F0.wireOp",EDGE,"E2"),sQuery(id+"F0.wireOp",EDGE,"E5.0"),sQuery(id+"F0.wireOp",EDGE,"E5.1"),sQuery(id+"F0.wireOp",EDGE,"E5.2"),sQuery(id+"F0.wireOp",EDGE,"E5.3"),sQuery(id+"F0.wireOp",EDGE,"E5.4"),sQuery(id+"F0.wireOp",EDGE,"E5.5"),sQuery(id+"F0.wireOp",EDGE,"E6.0"),sQuery(id+"F0.wireOp",EDGE,"E6.1"),sQuery(id+"F0.wireOp",EDGE,"E6.2"),sQuery(id+"F0.wireOp",EDGE,"E6.3"),sQuery(id+"F0.wireOp",EDGE,"E6.4"),sQuery(id+"F0.wireOp",EDGE,"E6.5"),sQuery(id+"F0.wireOp",EDGE,"E7.0"),sQuery(id+"F0.wireOp",EDGE,"E7.1"),sQuery(id+"F0.wireOp",EDGE,"E7.2"),sQuery(id+"F0.wireOp",EDGE,"E7.3"),sQuery(id+"F0.wireOp",EDGE,"E7.4"),sQuery(id+"F0.wireOp",EDGE,"E7.5"),sQuery(id+"F0.wireOp",EDGE,"E8.0"),sQuery(id+"F0.wireOp",EDGE,"E8.1"),sQuery(id+"F0.wireOp",EDGE,"E8.2"),sQuery(id+"F0.wireOp",EDGE,"E8.3"),sQuery(id+"F0.wireOp",EDGE,"E8.4"),sQuery(id+"F0.wireOp",EDGE,"E8.5"),sQuery(id+"F0.wireOp",EDGE,"E9"),sQuery(id+"F0.wireOp",EDGE,"E10"),sQuery(id+"F0.wireOp",EDGE,"E11"),sQuery(id+"F0.wireOp",EDGE,"E12"),sQuery(id+"F0.wireOp",EDGE,"E13"),sQuery(id+"F0.wireOp",EDGE,"E14"),sQuery(id+"F0.wireOp",EDGE,"E15"),sQuery(id+"F0.wireOp",EDGE,"E16"),sQuery(id+"F0.wireOp",EDGE,"E19.trimOffspring"),sQuery(id+"F0.wireOp",EDGE,"E20.trimOffspring"),sQuery(id+"F0.wireOp",EDGE,"E23.trimOffspring"),sQuery(id+"F0.wireOp",EDGE,"E26.trimOffspring"),subQ1,subQ0,sQuery(id+"F0.wireOp",EDGE,"E34.trimOffspring")])],"isStart":true})]});}
            var Q144;
            {var subQ0=sQuery(id+"F0.wireOp",EDGE,"E2");Q144=makeQuery(id+"F2.opFillet","BLEND_EDGE",EDGE,{"blendedFrom":[makeQuery(id+"F1.opExtrude","CAP_EDGE",EDGE,{"disambiguationData":[OSD([subQ0])],"isStart":false}),makeQuery(id+"F1.opExtrude","SWEPT_FACE",FACE,{"disambiguationData":[OSD([subQ0])]})],"blendedInto":[makeQuery(id+"F1.opExtrude","SWEPT_FACE",FACE,{"disambiguationData":[OSD([subQ0])]})]});}
            var Q145;
            {var subQ0=sQuery(id+"F0.wireOp",EDGE,"E23.trimOffspring");var subQ1=sQuery(id+"F0.wireOp",EDGE,"E20.trimOffspring");Q145=makeQuery(id+"F2.opFillet","BLEND_EDGE",EDGE,{"blendedFrom":[makeQuery(id+"F1.opExtrude","CAP_VERTEX",VERTEX,{"disambiguationData":[OSD([subQ1,subQ0])],"isStart":false}),makeQuery(id+"F1.opExtrude","SWEPT_EDGE",EDGE,{"disambiguationData":[OSD([subQ1,subQ0])]})],"blendedInto":[]});}
            var Q146;
            Q146=makeQuery(id+"F2.opFillet","BLEND_EDGE",EDGE,{"blendedFrom":[makeQuery(id+"F1.opExtrude","CAP_EDGE",EDGE,{"disambiguationData":[OSD([sQuery(id+"F0.wireOp",EDGE,"E9")])],"isStart":true}),makeQuery(id+"F1.opExtrude","CAP_EDGE",EDGE,{"disambiguationData":[OSD([sQuery(id+"F0.wireOp",EDGE,"E13")])],"isStart":true})],"blendedInto":[]});
            var Q147;
            Q147=makeQuery(id+"F2.opFillet","BLEND_EDGE",EDGE,{"blendedFrom":[makeQuery(id+"F1.opExtrude","CAP_EDGE",EDGE,{"disambiguationData":[OSD([sQuery(id+"F0.wireOp",EDGE,"E11")])],"isStart":true}),makeQuery(id+"F1.opExtrude","CAP_EDGE",EDGE,{"disambiguationData":[OSD([sQuery(id+"F0.wireOp",EDGE,"E14")])],"isStart":true})],"blendedInto":[]});
            var Q148;
            {var subQ0=sQuery(id+"F0.wireOp",EDGE,"E13");Q148=makeQuery(id+"F2.opFillet","BLEND_EDGE",EDGE,{"blendedFrom":[makeQuery(id+"F1.opExtrude","CAP_EDGE",EDGE,{"disambiguationData":[OSD([subQ0])],"isStart":true}),makeQuery(id+"F1.opExtrude","CAP_FACE",FACE,{"disambiguationData":[OSD([sQuery(id+"F0.wireOp",EDGE,"E0"),sQuery(id+"F0.wireOp",EDGE,"E2"),sQuery(id+"F0.wireOp",EDGE,"E5.0"),sQuery(id+"F0.wireOp",EDGE,"E5.1"),sQuery(id+"F0.wireOp",EDGE,"E5.2"),sQuery(id+"F0.wireOp",EDGE,"E5.3"),sQuery(id+"F0.wireOp",EDGE,"E5.4"),sQuery(id+"F0.wireOp",EDGE,"E5.5"),sQuery(id+"F0.wireOp",EDGE,"E6.0"),sQuery(id+"F0.wireOp",EDGE,"E6.1"),sQuery(id+"F0.wireOp",EDGE,"E6.2"),sQuery(id+"F0.wireOp",EDGE,"E6.3"),sQuery(id+"F0.wireOp",EDGE,"E6.4"),sQuery(id+"F0.wireOp",EDGE,"E6.5"),sQuery(id+"F0.wireOp",EDGE,"E7.0"),sQuery(id+"F0.wireOp",EDGE,"E7.1"),sQuery(id+"F0.wireOp",EDGE,"E7.2"),sQuery(id+"F0.wireOp",EDGE,"E7.3"),sQuery(id+"F0.wireOp",EDGE,"E7.4"),sQuery(id+"F0.wireOp",EDGE,"E7.5"),sQuery(id+"F0.wireOp",EDGE,"E8.0"),sQuery(id+"F0.wireOp",EDGE,"E8.1"),sQuery(id+"F0.wireOp",EDGE,"E8.2"),sQuery(id+"F0.wireOp",EDGE,"E8.3"),sQuery(id+"F0.wireOp",EDGE,"E8.4"),sQuery(id+"F0.wireOp",EDGE,"E8.5"),sQuery(id+"F0.wireOp",EDGE,"E9"),sQuery(id+"F0.wireOp",EDGE,"E10"),sQuery(id+"F0.wireOp",EDGE,"E11"),sQuery(id+"F0.wireOp",EDGE,"E12"),subQ0,sQuery(id+"F0.wireOp",EDGE,"E14"),sQuery(id+"F0.wireOp",EDGE,"E15"),sQuery(id+"F0.wireOp",EDGE,"E16"),sQuery(id+"F0.wireOp",EDGE,"E19.trimOffspring"),sQuery(id+"F0.wireOp",EDGE,"E20.trimOffspring"),sQuery(id+"F0.wireOp",EDGE,"E23.trimOffspring"),sQuery(id+"F0.wireOp",EDGE,"E26.trimOffspring"),sQuery(id+"F0.wireOp",EDGE,"E27.trimOffspring"),sQuery(id+"F0.wireOp",EDGE,"E31.trimOffspring"),sQuery(id+"F0.wireOp",EDGE,"E34.trimOffspring")])],"isStart":true})],"blendedInto":[makeQuery(id+"F1.opExtrude","CAP_FACE",FACE,{"disambiguationData":[OSD([sQuery(id+"F0.wireOp",EDGE,"E0"),sQuery(id+"F0.wireOp",EDGE,"E2"),sQuery(id+"F0.wireOp",EDGE,"E5.0"),sQuery(id+"F0.wireOp",EDGE,"E5.1"),sQuery(id+"F0.wireOp",EDGE,"E5.2"),sQuery(id+"F0.wireOp",EDGE,"E5.3"),sQuery(id+"F0.wireOp",EDGE,"E5.4"),sQuery(id+"F0.wireOp",EDGE,"E5.5"),sQuery(id+"F0.wireOp",EDGE,"E6.0"),sQuery(id+"F0.wireOp",EDGE,"E6.1"),sQuery(id+"F0.wireOp",EDGE,"E6.2"),sQuery(id+"F0.wireOp",EDGE,"E6.3"),sQuery(id+"F0.wireOp",EDGE,"E6.4"),sQuery(id+"F0.wireOp",EDGE,"E6.5"),sQuery(id+"F0.wireOp",EDGE,"E7.0"),sQuery(id+"F0.wireOp",EDGE,"E7.1"),sQuery(id+"F0.wireOp",EDGE,"E7.2"),sQuery(id+"F0.wireOp",EDGE,"E7.3"),sQuery(id+"F0.wireOp",EDGE,"E7.4"),sQuery(id+"F0.wireOp",EDGE,"E7.5"),sQuery(id+"F0.wireOp",EDGE,"E8.0"),sQuery(id+"F0.wireOp",EDGE,"E8.1"),sQuery(id+"F0.wireOp",EDGE,"E8.2"),sQuery(id+"F0.wireOp",EDGE,"E8.3"),sQuery(id+"F0.wireOp",EDGE,"E8.4"),sQuery(id+"F0.wireOp",EDGE,"E8.5"),sQuery(id+"F0.wireOp",EDGE,"E9"),sQuery(id+"F0.wireOp",EDGE,"E10"),sQuery(id+"F0.wireOp",EDGE,"E11"),sQuery(id+"F0.wireOp",EDGE,"E12"),subQ0,sQuery(id+"F0.wireOp",EDGE,"E14"),sQuery(id+"F0.wireOp",EDGE,"E15"),sQuery(id+"F0.wireOp",EDGE,"E16"),sQuery(id+"F0.wireOp",EDGE,"E19.trimOffspring"),sQuery(id+"F0.wireOp",EDGE,"E20.trimOffspring"),sQuery(id+"F0.wireOp",EDGE,"E23.trimOffspring"),sQuery(id+"F0.wireOp",EDGE,"E26.trimOffspring"),sQuery(id+"F0.wireOp",EDGE,"E27.trimOffspring"),sQuery(id+"F0.wireOp",EDGE,"E31.trimOffspring"),sQuery(id+"F0.wireOp",EDGE,"E34.trimOffspring")])],"isStart":true})]});}
            var Q149;
            {var subQ0=sQuery(id+"F0.wireOp",EDGE,"E19.trimOffspring");Q149=makeQuery(id+"F2.opFillet","BLEND_EDGE",EDGE,{"blendedFrom":[makeQuery(id+"F1.opExtrude","CAP_EDGE",EDGE,{"disambiguationData":[OSD([subQ0])],"isStart":true}),makeQuery(id+"F1.opExtrude","CAP_FACE",FACE,{"disambiguationData":[OSD([sQuery(id+"F0.wireOp",EDGE,"E0"),sQuery(id+"F0.wireOp",EDGE,"E2"),sQuery(id+"F0.wireOp",EDGE,"E5.0"),sQuery(id+"F0.wireOp",EDGE,"E5.1"),sQuery(id+"F0.wireOp",EDGE,"E5.2"),sQuery(id+"F0.wireOp",EDGE,"E5.3"),sQuery(id+"F0.wireOp",EDGE,"E5.4"),sQuery(id+"F0.wireOp",EDGE,"E5.5"),sQuery(id+"F0.wireOp",EDGE,"E6.0"),sQuery(id+"F0.wireOp",EDGE,"E6.1"),sQuery(id+"F0.wireOp",EDGE,"E6.2"),sQuery(id+"F0.wireOp",EDGE,"E6.3"),sQuery(id+"F0.wireOp",EDGE,"E6.4"),sQuery(id+"F0.wireOp",EDGE,"E6.5"),sQuery(id+"F0.wireOp",EDGE,"E7.0"),sQuery(id+"F0.wireOp",EDGE,"E7.1"),sQuery(id+"F0.wireOp",EDGE,"E7.2"),sQuery(id+"F0.wireOp",EDGE,"E7.3"),sQuery(id+"F0.wireOp",EDGE,"E7.4"),sQuery(id+"F0.wireOp",EDGE,"E7.5"),sQuery(id+"F0.wireOp",EDGE,"E8.0"),sQuery(id+"F0.wireOp",EDGE,"E8.1"),sQuery(id+"F0.wireOp",EDGE,"E8.2"),sQuery(id+"F0.wireOp",EDGE,"E8.3"),sQuery(id+"F0.wireOp",EDGE,"E8.4"),sQuery(id+"F0.wireOp",EDGE,"E8.5"),sQuery(id+"F0.wireOp",EDGE,"E9"),sQuery(id+"F0.wireOp",EDGE,"E10"),sQuery(id+"F0.wireOp",EDGE,"E11"),sQuery(id+"F0.wireOp",EDGE,"E12"),sQuery(id+"F0.wireOp",EDGE,"E13"),sQuery(id+"F0.wireOp",EDGE,"E14"),sQuery(id+"F0.wireOp",EDGE,"E15"),sQuery(id+"F0.wireOp",EDGE,"E16"),subQ0,sQuery(id+"F0.wireOp",EDGE,"E20.trimOffspring"),sQuery(id+"F0.wireOp",EDGE,"E23.trimOffspring"),sQuery(id+"F0.wireOp",EDGE,"E26.trimOffspring"),sQuery(id+"F0.wireOp",EDGE,"E27.trimOffspring"),sQuery(id+"F0.wireOp",EDGE,"E31.trimOffspring"),sQuery(id+"F0.wireOp",EDGE,"E34.trimOffspring")])],"isStart":true})],"blendedInto":[makeQuery(id+"F1.opExtrude","CAP_FACE",FACE,{"disambiguationData":[OSD([sQuery(id+"F0.wireOp",EDGE,"E0"),sQuery(id+"F0.wireOp",EDGE,"E2"),sQuery(id+"F0.wireOp",EDGE,"E5.0"),sQuery(id+"F0.wireOp",EDGE,"E5.1"),sQuery(id+"F0.wireOp",EDGE,"E5.2"),sQuery(id+"F0.wireOp",EDGE,"E5.3"),sQuery(id+"F0.wireOp",EDGE,"E5.4"),sQuery(id+"F0.wireOp",EDGE,"E5.5"),sQuery(id+"F0.wireOp",EDGE,"E6.0"),sQuery(id+"F0.wireOp",EDGE,"E6.1"),sQuery(id+"F0.wireOp",EDGE,"E6.2"),sQuery(id+"F0.wireOp",EDGE,"E6.3"),sQuery(id+"F0.wireOp",EDGE,"E6.4"),sQuery(id+"F0.wireOp",EDGE,"E6.5"),sQuery(id+"F0.wireOp",EDGE,"E7.0"),sQuery(id+"F0.wireOp",EDGE,"E7.1"),sQuery(id+"F0.wireOp",EDGE,"E7.2"),sQuery(id+"F0.wireOp",EDGE,"E7.3"),sQuery(id+"F0.wireOp",EDGE,"E7.4"),sQuery(id+"F0.wireOp",EDGE,"E7.5"),sQuery(id+"F0.wireOp",EDGE,"E8.0"),sQuery(id+"F0.wireOp",EDGE,"E8.1"),sQuery(id+"F0.wireOp",EDGE,"E8.2"),sQuery(id+"F0.wireOp",EDGE,"E8.3"),sQuery(id+"F0.wireOp",EDGE,"E8.4"),sQuery(id+"F0.wireOp",EDGE,"E8.5"),sQuery(id+"F0.wireOp",EDGE,"E9"),sQuery(id+"F0.wireOp",EDGE,"E10"),sQuery(id+"F0.wireOp",EDGE,"E11"),sQuery(id+"F0.wireOp",EDGE,"E12"),sQuery(id+"F0.wireOp",EDGE,"E13"),sQuery(id+"F0.wireOp",EDGE,"E14"),sQuery(id+"F0.wireOp",EDGE,"E15"),sQuery(id+"F0.wireOp",EDGE,"E16"),subQ0,sQuery(id+"F0.wireOp",EDGE,"E20.trimOffspring"),sQuery(id+"F0.wireOp",EDGE,"E23.trimOffspring"),sQuery(id+"F0.wireOp",EDGE,"E26.trimOffspring"),sQuery(id+"F0.wireOp",EDGE,"E27.trimOffspring"),sQuery(id+"F0.wireOp",EDGE,"E31.trimOffspring"),sQuery(id+"F0.wireOp",EDGE,"E34.trimOffspring")])],"isStart":true})]});}
            var Q150;
            {var subQ0=sQuery(id+"F0.wireOp",EDGE,"E27.trimOffspring");Q150=makeQuery(id+"F2.opFillet","BLEND_EDGE",EDGE,{"blendedFrom":[makeQuery(id+"F1.opExtrude","CAP_EDGE",EDGE,{"disambiguationData":[OSD([subQ0])],"isStart":true}),makeQuery(id+"F1.opExtrude","CAP_FACE",FACE,{"disambiguationData":[OSD([sQuery(id+"F0.wireOp",EDGE,"E0"),sQuery(id+"F0.wireOp",EDGE,"E2"),sQuery(id+"F0.wireOp",EDGE,"E5.0"),sQuery(id+"F0.wireOp",EDGE,"E5.1"),sQuery(id+"F0.wireOp",EDGE,"E5.2"),sQuery(id+"F0.wireOp",EDGE,"E5.3"),sQuery(id+"F0.wireOp",EDGE,"E5.4"),sQuery(id+"F0.wireOp",EDGE,"E5.5"),sQuery(id+"F0.wireOp",EDGE,"E6.0"),sQuery(id+"F0.wireOp",EDGE,"E6.1"),sQuery(id+"F0.wireOp",EDGE,"E6.2"),sQuery(id+"F0.wireOp",EDGE,"E6.3"),sQuery(id+"F0.wireOp",EDGE,"E6.4"),sQuery(id+"F0.wireOp",EDGE,"E6.5"),sQuery(id+"F0.wireOp",EDGE,"E7.0"),sQuery(id+"F0.wireOp",EDGE,"E7.1"),sQuery(id+"F0.wireOp",EDGE,"E7.2"),sQuery(id+"F0.wireOp",EDGE,"E7.3"),sQuery(id+"F0.wireOp",EDGE,"E7.4"),sQuery(id+"F0.wireOp",EDGE,"E7.5"),sQuery(id+"F0.wireOp",EDGE,"E8.0"),sQuery(id+"F0.wireOp",EDGE,"E8.1"),sQuery(id+"F0.wireOp",EDGE,"E8.2"),sQuery(id+"F0.wireOp",EDGE,"E8.3"),sQuery(id+"F0.wireOp",EDGE,"E8.4"),sQuery(id+"F0.wireOp",EDGE,"E8.5"),sQuery(id+"F0.wireOp",EDGE,"E9"),sQuery(id+"F0.wireOp",EDGE,"E10"),sQuery(id+"F0.wireOp",EDGE,"E11"),sQuery(id+"F0.wireOp",EDGE,"E12"),sQuery(id+"F0.wireOp",EDGE,"E13"),sQuery(id+"F0.wireOp",EDGE,"E14"),sQuery(id+"F0.wireOp",EDGE,"E15"),sQuery(id+"F0.wireOp",EDGE,"E16"),sQuery(id+"F0.wireOp",EDGE,"E19.trimOffspring"),sQuery(id+"F0.wireOp",EDGE,"E20.trimOffspring"),sQuery(id+"F0.wireOp",EDGE,"E23.trimOffspring"),sQuery(id+"F0.wireOp",EDGE,"E26.trimOffspring"),subQ0,sQuery(id+"F0.wireOp",EDGE,"E31.trimOffspring"),sQuery(id+"F0.wireOp",EDGE,"E34.trimOffspring")])],"isStart":true})],"blendedInto":[makeQuery(id+"F1.opExtrude","CAP_FACE",FACE,{"disambiguationData":[OSD([sQuery(id+"F0.wireOp",EDGE,"E0"),sQuery(id+"F0.wireOp",EDGE,"E2"),sQuery(id+"F0.wireOp",EDGE,"E5.0"),sQuery(id+"F0.wireOp",EDGE,"E5.1"),sQuery(id+"F0.wireOp",EDGE,"E5.2"),sQuery(id+"F0.wireOp",EDGE,"E5.3"),sQuery(id+"F0.wireOp",EDGE,"E5.4"),sQuery(id+"F0.wireOp",EDGE,"E5.5"),sQuery(id+"F0.wireOp",EDGE,"E6.0"),sQuery(id+"F0.wireOp",EDGE,"E6.1"),sQuery(id+"F0.wireOp",EDGE,"E6.2"),sQuery(id+"F0.wireOp",EDGE,"E6.3"),sQuery(id+"F0.wireOp",EDGE,"E6.4"),sQuery(id+"F0.wireOp",EDGE,"E6.5"),sQuery(id+"F0.wireOp",EDGE,"E7.0"),sQuery(id+"F0.wireOp",EDGE,"E7.1"),sQuery(id+"F0.wireOp",EDGE,"E7.2"),sQuery(id+"F0.wireOp",EDGE,"E7.3"),sQuery(id+"F0.wireOp",EDGE,"E7.4"),sQuery(id+"F0.wireOp",EDGE,"E7.5"),sQuery(id+"F0.wireOp",EDGE,"E8.0"),sQuery(id+"F0.wireOp",EDGE,"E8.1"),sQuery(id+"F0.wireOp",EDGE,"E8.2"),sQuery(id+"F0.wireOp",EDGE,"E8.3"),sQuery(id+"F0.wireOp",EDGE,"E8.4"),sQuery(id+"F0.wireOp",EDGE,"E8.5"),sQuery(id+"F0.wireOp",EDGE,"E9"),sQuery(id+"F0.wireOp",EDGE,"E10"),sQuery(id+"F0.wireOp",EDGE,"E11"),sQuery(id+"F0.wireOp",EDGE,"E12"),sQuery(id+"F0.wireOp",EDGE,"E13"),sQuery(id+"F0.wireOp",EDGE,"E14"),sQuery(id+"F0.wireOp",EDGE,"E15"),sQuery(id+"F0.wireOp",EDGE,"E16"),sQuery(id+"F0.wireOp",EDGE,"E19.trimOffspring"),sQuery(id+"F0.wireOp",EDGE,"E20.trimOffspring"),sQuery(id+"F0.wireOp",EDGE,"E23.trimOffspring"),sQuery(id+"F0.wireOp",EDGE,"E26.trimOffspring"),subQ0,sQuery(id+"F0.wireOp",EDGE,"E31.trimOffspring"),sQuery(id+"F0.wireOp",EDGE,"E34.trimOffspring")])],"isStart":true})]});}
            var Q151;
            {var subQ0=sQuery(id+"F0.wireOp",EDGE,"E14");var subQ1=sQuery(id+"F0.wireOp",EDGE,"E2");Q151=makeQuery(id+"F2.opFillet","BLEND_EDGE",EDGE,{"blendedFrom":[makeQuery(id+"F1.opExtrude","CAP_VERTEX",VERTEX,{"disambiguationData":[OSD([subQ1,subQ0])],"isStart":false}),makeQuery(id+"F1.opExtrude","CAP_FACE",FACE,{"disambiguationData":[OSD([sQuery(id+"F0.wireOp",EDGE,"E0"),subQ1,sQuery(id+"F0.wireOp",EDGE,"E5.0"),sQuery(id+"F0.wireOp",EDGE,"E5.1"),sQuery(id+"F0.wireOp",EDGE,"E5.2"),sQuery(id+"F0.wireOp",EDGE,"E5.3"),sQuery(id+"F0.wireOp",EDGE,"E5.4"),sQuery(id+"F0.wireOp",EDGE,"E5.5"),sQuery(id+"F0.wireOp",EDGE,"E6.0"),sQuery(id+"F0.wireOp",EDGE,"E6.1"),sQuery(id+"F0.wireOp",EDGE,"E6.2"),sQuery(id+"F0.wireOp",EDGE,"E6.3"),sQuery(id+"F0.wireOp",EDGE,"E6.4"),sQuery(id+"F0.wireOp",EDGE,"E6.5"),sQuery(id+"F0.wireOp",EDGE,"E7.0"),sQuery(id+"F0.wireOp",EDGE,"E7.1"),sQuery(id+"F0.wireOp",EDGE,"E7.2"),sQuery(id+"F0.wireOp",EDGE,"E7.3"),sQuery(id+"F0.wireOp",EDGE,"E7.4"),sQuery(id+"F0.wireOp",EDGE,"E7.5"),sQuery(id+"F0.wireOp",EDGE,"E8.0"),sQuery(id+"F0.wireOp",EDGE,"E8.1"),sQuery(id+"F0.wireOp",EDGE,"E8.2"),sQuery(id+"F0.wireOp",EDGE,"E8.3"),sQuery(id+"F0.wireOp",EDGE,"E8.4"),sQuery(id+"F0.wireOp",EDGE,"E8.5"),sQuery(id+"F0.wireOp",EDGE,"E9"),sQuery(id+"F0.wireOp",EDGE,"E10"),sQuery(id+"F0.wireOp",EDGE,"E11"),sQuery(id+"F0.wireOp",EDGE,"E12"),sQuery(id+"F0.wireOp",EDGE,"E13"),subQ0,sQuery(id+"F0.wireOp",EDGE,"E15"),sQuery(id+"F0.wireOp",EDGE,"E16"),sQuery(id+"F0.wireOp",EDGE,"E19.trimOffspring"),sQuery(id+"F0.wireOp",EDGE,"E20.trimOffspring"),sQuery(id+"F0.wireOp",EDGE,"E23.trimOffspring"),sQuery(id+"F0.wireOp",EDGE,"E26.trimOffspring"),sQuery(id+"F0.wireOp",EDGE,"E27.trimOffspring"),sQuery(id+"F0.wireOp",EDGE,"E31.trimOffspring"),sQuery(id+"F0.wireOp",EDGE,"E34.trimOffspring")])],"isStart":false})],"blendedInto":[makeQuery(id+"F1.opExtrude","CAP_FACE",FACE,{"disambiguationData":[OSD([sQuery(id+"F0.wireOp",EDGE,"E0"),subQ1,sQuery(id+"F0.wireOp",EDGE,"E5.0"),sQuery(id+"F0.wireOp",EDGE,"E5.1"),sQuery(id+"F0.wireOp",EDGE,"E5.2"),sQuery(id+"F0.wireOp",EDGE,"E5.3"),sQuery(id+"F0.wireOp",EDGE,"E5.4"),sQuery(id+"F0.wireOp",EDGE,"E5.5"),sQuery(id+"F0.wireOp",EDGE,"E6.0"),sQuery(id+"F0.wireOp",EDGE,"E6.1"),sQuery(id+"F0.wireOp",EDGE,"E6.2"),sQuery(id+"F0.wireOp",EDGE,"E6.3"),sQuery(id+"F0.wireOp",EDGE,"E6.4"),sQuery(id+"F0.wireOp",EDGE,"E6.5"),sQuery(id+"F0.wireOp",EDGE,"E7.0"),sQuery(id+"F0.wireOp",EDGE,"E7.1"),sQuery(id+"F0.wireOp",EDGE,"E7.2"),sQuery(id+"F0.wireOp",EDGE,"E7.3"),sQuery(id+"F0.wireOp",EDGE,"E7.4"),sQuery(id+"F0.wireOp",EDGE,"E7.5"),sQuery(id+"F0.wireOp",EDGE,"E8.0"),sQuery(id+"F0.wireOp",EDGE,"E8.1"),sQuery(id+"F0.wireOp",EDGE,"E8.2"),sQuery(id+"F0.wireOp",EDGE,"E8.3"),sQuery(id+"F0.wireOp",EDGE,"E8.4"),sQuery(id+"F0.wireOp",EDGE,"E8.5"),sQuery(id+"F0.wireOp",EDGE,"E9"),sQuery(id+"F0.wireOp",EDGE,"E10"),sQuery(id+"F0.wireOp",EDGE,"E11"),sQuery(id+"F0.wireOp",EDGE,"E12"),sQuery(id+"F0.wireOp",EDGE,"E13"),subQ0,sQuery(id+"F0.wireOp",EDGE,"E15"),sQuery(id+"F0.wireOp",EDGE,"E16"),sQuery(id+"F0.wireOp",EDGE,"E19.trimOffspring"),sQuery(id+"F0.wireOp",EDGE,"E20.trimOffspring"),sQuery(id+"F0.wireOp",EDGE,"E23.trimOffspring"),sQuery(id+"F0.wireOp",EDGE,"E26.trimOffspring"),sQuery(id+"F0.wireOp",EDGE,"E27.trimOffspring"),sQuery(id+"F0.wireOp",EDGE,"E31.trimOffspring"),sQuery(id+"F0.wireOp",EDGE,"E34.trimOffspring")])],"isStart":false})]});}
            var Q152;
            Q152=makeQuery(id+"F1.opExtrude","SWEPT_EDGE",EDGE,{"disambiguationData":[OSD([sQuery(id+"F0.wireOp",EDGE,"E5.0"),sQuery(id+"F0.wireOp",EDGE,"E5.5")])]});
            var Q153;
            Q153=makeQuery(id+"F1.opExtrude","SWEPT_EDGE",EDGE,{"disambiguationData":[OSD([sQuery(id+"F0.wireOp",EDGE,"E5.1"),sQuery(id+"F0.wireOp",EDGE,"E5.2")])]});
            var Q154;
            {var subQ0=sQuery(id+"F0.wireOp",EDGE,"E27.trimOffspring");Q154=makeQuery(id+"F2.opFillet","BLEND_EDGE",EDGE,{"blendedFrom":[makeQuery(id+"F1.opExtrude","CAP_VERTEX",VERTEX,{"disambiguationData":[OSD([subQ0,sQuery(id+"F0.wireOp",EDGE,"E31.trimOffspring")])],"isStart":false}),makeQuery(id+"F1.opExtrude","CAP_EDGE",EDGE,{"disambiguationData":[OSD([subQ0])],"isStart":false})],"blendedInto":[]});}
            var Q155;
            {var subQ0=sQuery(id+"F0.wireOp",EDGE,"E19.trimOffspring");Q155=makeQuery(id+"F2.opFillet","BLEND_EDGE",EDGE,{"blendedFrom":[makeQuery(id+"F1.opExtrude","CAP_EDGE",EDGE,{"disambiguationData":[OSD([subQ0])],"isStart":false}),makeQuery(id+"F1.opExtrude","SWEPT_FACE",FACE,{"disambiguationData":[OSD([subQ0])]})],"blendedInto":[makeQuery(id+"F1.opExtrude","SWEPT_FACE",FACE,{"disambiguationData":[OSD([subQ0])]})]});}
            var Q156;
            {var subQ0=sQuery(id+"F0.wireOp",EDGE,"E27.trimOffspring");Q156=makeQuery(id+"F2.opFillet","BLEND_EDGE",EDGE,{"blendedFrom":[makeQuery(id+"F1.opExtrude","CAP_EDGE",EDGE,{"disambiguationData":[OSD([subQ0])],"isStart":false}),makeQuery(id+"F1.opExtrude","CAP_FACE",FACE,{"disambiguationData":[OSD([sQuery(id+"F0.wireOp",EDGE,"E0"),sQuery(id+"F0.wireOp",EDGE,"E2"),sQuery(id+"F0.wireOp",EDGE,"E5.0"),sQuery(id+"F0.wireOp",EDGE,"E5.1"),sQuery(id+"F0.wireOp",EDGE,"E5.2"),sQuery(id+"F0.wireOp",EDGE,"E5.3"),sQuery(id+"F0.wireOp",EDGE,"E5.4"),sQuery(id+"F0.wireOp",EDGE,"E5.5"),sQuery(id+"F0.wireOp",EDGE,"E6.0"),sQuery(id+"F0.wireOp",EDGE,"E6.1"),sQuery(id+"F0.wireOp",EDGE,"E6.2"),sQuery(id+"F0.wireOp",EDGE,"E6.3"),sQuery(id+"F0.wireOp",EDGE,"E6.4"),sQuery(id+"F0.wireOp",EDGE,"E6.5"),sQuery(id+"F0.wireOp",EDGE,"E7.0"),sQuery(id+"F0.wireOp",EDGE,"E7.1"),sQuery(id+"F0.wireOp",EDGE,"E7.2"),sQuery(id+"F0.wireOp",EDGE,"E7.3"),sQuery(id+"F0.wireOp",EDGE,"E7.4"),sQuery(id+"F0.wireOp",EDGE,"E7.5"),sQuery(id+"F0.wireOp",EDGE,"E8.0"),sQuery(id+"F0.wireOp",EDGE,"E8.1"),sQuery(id+"F0.wireOp",EDGE,"E8.2"),sQuery(id+"F0.wireOp",EDGE,"E8.3"),sQuery(id+"F0.wireOp",EDGE,"E8.4"),sQuery(id+"F0.wireOp",EDGE,"E8.5"),sQuery(id+"F0.wireOp",EDGE,"E9"),sQuery(id+"F0.wireOp",EDGE,"E10"),sQuery(id+"F0.wireOp",EDGE,"E11"),sQuery(id+"F0.wireOp",EDGE,"E12"),sQuery(id+"F0.wireOp",EDGE,"E13"),sQuery(id+"F0.wireOp",EDGE,"E14"),sQuery(id+"F0.wireOp",EDGE,"E15"),sQuery(id+"F0.wireOp",EDGE,"E16"),sQuery(id+"F0.wireOp",EDGE,"E19.trimOffspring"),sQuery(id+"F0.wireOp",EDGE,"E20.trimOffspring"),sQuery(id+"F0.wireOp",EDGE,"E23.trimOffspring"),sQuery(id+"F0.wireOp",EDGE,"E26.trimOffspring"),subQ0,sQuery(id+"F0.wireOp",EDGE,"E31.trimOffspring"),sQuery(id+"F0.wireOp",EDGE,"E34.trimOffspring")])],"isStart":false})],"blendedInto":[makeQuery(id+"F1.opExtrude","CAP_FACE",FACE,{"disambiguationData":[OSD([sQuery(id+"F0.wireOp",EDGE,"E0"),sQuery(id+"F0.wireOp",EDGE,"E2"),sQuery(id+"F0.wireOp",EDGE,"E5.0"),sQuery(id+"F0.wireOp",EDGE,"E5.1"),sQuery(id+"F0.wireOp",EDGE,"E5.2"),sQuery(id+"F0.wireOp",EDGE,"E5.3"),sQuery(id+"F0.wireOp",EDGE,"E5.4"),sQuery(id+"F0.wireOp",EDGE,"E5.5"),sQuery(id+"F0.wireOp",EDGE,"E6.0"),sQuery(id+"F0.wireOp",EDGE,"E6.1"),sQuery(id+"F0.wireOp",EDGE,"E6.2"),sQuery(id+"F0.wireOp",EDGE,"E6.3"),sQuery(id+"F0.wireOp",EDGE,"E6.4"),sQuery(id+"F0.wireOp",EDGE,"E6.5"),sQuery(id+"F0.wireOp",EDGE,"E7.0"),sQuery(id+"F0.wireOp",EDGE,"E7.1"),sQuery(id+"F0.wireOp",EDGE,"E7.2"),sQuery(id+"F0.wireOp",EDGE,"E7.3"),sQuery(id+"F0.wireOp",EDGE,"E7.4"),sQuery(id+"F0.wireOp",EDGE,"E7.5"),sQuery(id+"F0.wireOp",EDGE,"E8.0"),sQuery(id+"F0.wireOp",EDGE,"E8.1"),sQuery(id+"F0.wireOp",EDGE,"E8.2"),sQuery(id+"F0.wireOp",EDGE,"E8.3"),sQuery(id+"F0.wireOp",EDGE,"E8.4"),sQuery(id+"F0.wireOp",EDGE,"E8.5"),sQuery(id+"F0.wireOp",EDGE,"E9"),sQuery(id+"F0.wireOp",EDGE,"E10"),sQuery(id+"F0.wireOp",EDGE,"E11"),sQuery(id+"F0.wireOp",EDGE,"E12"),sQuery(id+"F0.wireOp",EDGE,"E13"),sQuery(id+"F0.wireOp",EDGE,"E14"),sQuery(id+"F0.wireOp",EDGE,"E15"),sQuery(id+"F0.wireOp",EDGE,"E16"),sQuery(id+"F0.wireOp",EDGE,"E19.trimOffspring"),sQuery(id+"F0.wireOp",EDGE,"E20.trimOffspring"),sQuery(id+"F0.wireOp",EDGE,"E23.trimOffspring"),sQuery(id+"F0.wireOp",EDGE,"E26.trimOffspring"),subQ0,sQuery(id+"F0.wireOp",EDGE,"E31.trimOffspring"),sQuery(id+"F0.wireOp",EDGE,"E34.trimOffspring")])],"isStart":false})]});}
            var Q157;
            {var subQ0=sQuery(id+"F0.wireOp",EDGE,"E13");Q157=makeQuery(id+"F2.opFillet","BLEND_EDGE",EDGE,{"blendedFrom":[makeQuery(id+"F1.opExtrude","CAP_EDGE",EDGE,{"disambiguationData":[OSD([subQ0])],"isStart":false}),makeQuery(id+"F1.opExtrude","CAP_FACE",FACE,{"disambiguationData":[OSD([sQuery(id+"F0.wireOp",EDGE,"E0"),sQuery(id+"F0.wireOp",EDGE,"E2"),sQuery(id+"F0.wireOp",EDGE,"E5.0"),sQuery(id+"F0.wireOp",EDGE,"E5.1"),sQuery(id+"F0.wireOp",EDGE,"E5.2"),sQuery(id+"F0.wireOp",EDGE,"E5.3"),sQuery(id+"F0.wireOp",EDGE,"E5.4"),sQuery(id+"F0.wireOp",EDGE,"E5.5"),sQuery(id+"F0.wireOp",EDGE,"E6.0"),sQuery(id+"F0.wireOp",EDGE,"E6.1"),sQuery(id+"F0.wireOp",EDGE,"E6.2"),sQuery(id+"F0.wireOp",EDGE,"E6.3"),sQuery(id+"F0.wireOp",EDGE,"E6.4"),sQuery(id+"F0.wireOp",EDGE,"E6.5"),sQuery(id+"F0.wireOp",EDGE,"E7.0"),sQuery(id+"F0.wireOp",EDGE,"E7.1"),sQuery(id+"F0.wireOp",EDGE,"E7.2"),sQuery(id+"F0.wireOp",EDGE,"E7.3"),sQuery(id+"F0.wireOp",EDGE,"E7.4"),sQuery(id+"F0.wireOp",EDGE,"E7.5"),sQuery(id+"F0.wireOp",EDGE,"E8.0"),sQuery(id+"F0.wireOp",EDGE,"E8.1"),sQuery(id+"F0.wireOp",EDGE,"E8.2"),sQuery(id+"F0.wireOp",EDGE,"E8.3"),sQuery(id+"F0.wireOp",EDGE,"E8.4"),sQuery(id+"F0.wireOp",EDGE,"E8.5"),sQuery(id+"F0.wireOp",EDGE,"E9"),sQuery(id+"F0.wireOp",EDGE,"E10"),sQuery(id+"F0.wireOp",EDGE,"E11"),sQuery(id+"F0.wireOp",EDGE,"E12"),subQ0,sQuery(id+"F0.wireOp",EDGE,"E14"),sQuery(id+"F0.wireOp",EDGE,"E15"),sQuery(id+"F0.wireOp",EDGE,"E16"),sQuery(id+"F0.wireOp",EDGE,"E19.trimOffspring"),sQuery(id+"F0.wireOp",EDGE,"E20.trimOffspring"),sQuery(id+"F0.wireOp",EDGE,"E23.trimOffspring"),sQuery(id+"F0.wireOp",EDGE,"E26.trimOffspring"),sQuery(id+"F0.wireOp",EDGE,"E27.trimOffspring"),sQuery(id+"F0.wireOp",EDGE,"E31.trimOffspring"),sQuery(id+"F0.wireOp",EDGE,"E34.trimOffspring")])],"isStart":false})],"blendedInto":[makeQuery(id+"F1.opExtrude","CAP_FACE",FACE,{"disambiguationData":[OSD([sQuery(id+"F0.wireOp",EDGE,"E0"),sQuery(id+"F0.wireOp",EDGE,"E2"),sQuery(id+"F0.wireOp",EDGE,"E5.0"),sQuery(id+"F0.wireOp",EDGE,"E5.1"),sQuery(id+"F0.wireOp",EDGE,"E5.2"),sQuery(id+"F0.wireOp",EDGE,"E5.3"),sQuery(id+"F0.wireOp",EDGE,"E5.4"),sQuery(id+"F0.wireOp",EDGE,"E5.5"),sQuery(id+"F0.wireOp",EDGE,"E6.0"),sQuery(id+"F0.wireOp",EDGE,"E6.1"),sQuery(id+"F0.wireOp",EDGE,"E6.2"),sQuery(id+"F0.wireOp",EDGE,"E6.3"),sQuery(id+"F0.wireOp",EDGE,"E6.4"),sQuery(id+"F0.wireOp",EDGE,"E6.5"),sQuery(id+"F0.wireOp",EDGE,"E7.0"),sQuery(id+"F0.wireOp",EDGE,"E7.1"),sQuery(id+"F0.wireOp",EDGE,"E7.2"),sQuery(id+"F0.wireOp",EDGE,"E7.3"),sQuery(id+"F0.wireOp",EDGE,"E7.4"),sQuery(id+"F0.wireOp",EDGE,"E7.5"),sQuery(id+"F0.wireOp",EDGE,"E8.0"),sQuery(id+"F0.wireOp",EDGE,"E8.1"),sQuery(id+"F0.wireOp",EDGE,"E8.2"),sQuery(id+"F0.wireOp",EDGE,"E8.3"),sQuery(id+"F0.wireOp",EDGE,"E8.4"),sQuery(id+"F0.wireOp",EDGE,"E8.5"),sQuery(id+"F0.wireOp",EDGE,"E9"),sQuery(id+"F0.wireOp",EDGE,"E10"),sQuery(id+"F0.wireOp",EDGE,"E11"),sQuery(id+"F0.wireOp",EDGE,"E12"),subQ0,sQuery(id+"F0.wireOp",EDGE,"E14"),sQuery(id+"F0.wireOp",EDGE,"E15"),sQuery(id+"F0.wireOp",EDGE,"E16"),sQuery(id+"F0.wireOp",EDGE,"E19.trimOffspring"),sQuery(id+"F0.wireOp",EDGE,"E20.trimOffspring"),sQuery(id+"F0.wireOp",EDGE,"E23.trimOffspring"),sQuery(id+"F0.wireOp",EDGE,"E26.trimOffspring"),sQuery(id+"F0.wireOp",EDGE,"E27.trimOffspring"),sQuery(id+"F0.wireOp",EDGE,"E31.trimOffspring"),sQuery(id+"F0.wireOp",EDGE,"E34.trimOffspring")])],"isStart":false})]});}
            var Q158;
            {var subQ0=sQuery(id+"F0.wireOp",EDGE,"E19.trimOffspring");Q158=makeQuery(id+"F2.opFillet","BLEND_EDGE",EDGE,{"blendedFrom":[makeQuery(id+"F1.opExtrude","CAP_EDGE",EDGE,{"disambiguationData":[OSD([subQ0])],"isStart":true}),makeQuery(id+"F1.opExtrude","SWEPT_FACE",FACE,{"disambiguationData":[OSD([subQ0])]})],"blendedInto":[makeQuery(id+"F1.opExtrude","SWEPT_FACE",FACE,{"disambiguationData":[OSD([subQ0])]})]});}
            var Q159;
            {var subQ0=sQuery(id+"F0.wireOp",EDGE,"E20.trimOffspring");Q159=makeQuery(id+"F2.opFillet","BLEND_EDGE",EDGE,{"blendedFrom":[makeQuery(id+"F1.opExtrude","CAP_VERTEX",VERTEX,{"disambiguationData":[OSD([sQuery(id+"F0.wireOp",EDGE,"E15"),subQ0])],"isStart":false}),makeQuery(id+"F1.opExtrude","CAP_EDGE",EDGE,{"disambiguationData":[OSD([subQ0])],"isStart":false})],"blendedInto":[]});}
            var Q160;
            {var subQ0=sQuery(id+"F0.wireOp",EDGE,"E13");Q160=makeQuery(id+"F2.opFillet","BLEND_EDGE",EDGE,{"blendedFrom":[makeQuery(id+"F1.opExtrude","CAP_EDGE",EDGE,{"disambiguationData":[OSD([subQ0])],"isStart":true}),makeQuery(id+"F1.opExtrude","SWEPT_FACE",FACE,{"disambiguationData":[OSD([subQ0])]})],"blendedInto":[makeQuery(id+"F1.opExtrude","SWEPT_FACE",FACE,{"disambiguationData":[OSD([subQ0])]})]});}
            var Q161;
            {var subQ0=sQuery(id+"F0.wireOp",EDGE,"E15");Q161=makeQuery(id+"F2.opFillet","BLEND_EDGE",EDGE,{"blendedFrom":[makeQuery(id+"F1.opExtrude","CAP_VERTEX",VERTEX,{"disambiguationData":[OSD([subQ0,sQuery(id+"F0.wireOp",EDGE,"E20.trimOffspring")])],"isStart":false}),makeQuery(id+"F1.opExtrude","CAP_EDGE",EDGE,{"disambiguationData":[OSD([subQ0])],"isStart":false})],"blendedInto":[]});}
            var Q162;
            {var subQ0=sQuery(id+"F0.wireOp",EDGE,"E19.trimOffspring");var subQ1=sQuery(id+"F0.wireOp",EDGE,"E2");Q162=makeQuery(id+"F2.opFillet","BLEND_EDGE",EDGE,{"blendedFrom":[makeQuery(id+"F1.opExtrude","CAP_VERTEX",VERTEX,{"disambiguationData":[OSD([subQ1,subQ0])],"isStart":false}),makeQuery(id+"F1.opExtrude","SWEPT_EDGE",EDGE,{"disambiguationData":[OSD([subQ1,subQ0])]})],"blendedInto":[]});}
            var Q163;
            Q163=makeQuery(id+"F1.opExtrude","SWEPT_EDGE",EDGE,{"disambiguationData":[OSD([sQuery(id+"F0.wireOp",EDGE,"E7.4"),sQuery(id+"F0.wireOp",EDGE,"E7.5")])]});
            var Q164;
            {var subQ0=sQuery(id+"F0.wireOp",EDGE,"E2");Q164=makeQuery(id+"F2.opFillet","BLEND_EDGE",EDGE,{"blendedFrom":[makeQuery(id+"F1.opExtrude","CAP_VERTEX",VERTEX,{"disambiguationData":[OSD([subQ0,sQuery(id+"F0.wireOp",EDGE,"E14")])],"isStart":false}),makeQuery(id+"F1.opExtrude","CAP_EDGE",EDGE,{"disambiguationData":[OSD([subQ0])],"isStart":false})],"blendedInto":[]});}
            var Q165;
            Q165=makeQuery(id+"F1.opExtrude","SWEPT_EDGE",EDGE,{"disambiguationData":[OSD([sQuery(id+"F0.wireOp",EDGE,"E8.0"),sQuery(id+"F0.wireOp",EDGE,"E8.5")])]});
            var Q166;
            Q166=makeQuery(id+"F1.opExtrude","SWEPT_EDGE",EDGE,{"disambiguationData":[OSD([sQuery(id+"F0.wireOp",EDGE,"E8.0"),sQuery(id+"F0.wireOp",EDGE,"E8.1")])]});
            var Q167;
            {var subQ0=sQuery(id+"F0.wireOp",EDGE,"E27.trimOffspring");Q167=makeQuery(id+"F2.opFillet","BLEND_EDGE",EDGE,{"blendedFrom":[makeQuery(id+"F1.opExtrude","CAP_EDGE",EDGE,{"disambiguationData":[OSD([subQ0])],"isStart":true}),makeQuery(id+"F1.opExtrude","SWEPT_FACE",FACE,{"disambiguationData":[OSD([subQ0])]})],"blendedInto":[makeQuery(id+"F1.opExtrude","SWEPT_FACE",FACE,{"disambiguationData":[OSD([subQ0])]})]});}
            var Q168;
            {var subQ0=sQuery(id+"F0.wireOp",EDGE,"E31.trimOffspring");Q168=makeQuery(id+"F2.opFillet","BLEND_EDGE",EDGE,{"blendedFrom":[makeQuery(id+"F1.opExtrude","SWEPT_EDGE",EDGE,{"disambiguationData":[OSD([sQuery(id+"F0.wireOp",EDGE,"E13"),subQ0])]}),makeQuery(id+"F1.opExtrude","SWEPT_FACE",FACE,{"disambiguationData":[OSD([subQ0])]})],"blendedInto":[makeQuery(id+"F1.opExtrude","SWEPT_FACE",FACE,{"disambiguationData":[OSD([subQ0])]})]});}
            var Q169;
            Q169=makeQuery(id+"F1.opExtrude","SWEPT_EDGE",EDGE,{"disambiguationData":[OSD([sQuery(id+"F0.wireOp",EDGE,"E8.2"),sQuery(id+"F0.wireOp",EDGE,"E8.3")])]});
            var Q170;
            {var subQ0=sQuery(id+"F0.wireOp",EDGE,"E14");var subQ1=sQuery(id+"F0.wireOp",EDGE,"E2");Q170=makeQuery(id+"F2.opFillet","BLEND_EDGE",EDGE,{"blendedFrom":[makeQuery(id+"F1.opExtrude","CAP_VERTEX",VERTEX,{"disambiguationData":[OSD([subQ1,subQ0])],"isStart":false}),makeQuery(id+"F1.opExtrude","SWEPT_EDGE",EDGE,{"disambiguationData":[OSD([subQ1,subQ0])]})],"blendedInto":[]});}
            var Q171;
            {var subQ0=sQuery(id+"F0.wireOp",EDGE,"E19.trimOffspring");var subQ1=sQuery(id+"F0.wireOp",EDGE,"E2");Q171=makeQuery(id+"F2.opFillet","BLEND_EDGE",EDGE,{"blendedFrom":[makeQuery(id+"F1.opExtrude","CAP_VERTEX",VERTEX,{"disambiguationData":[OSD([subQ1,subQ0])],"isStart":true}),makeQuery(id+"F1.opExtrude","SWEPT_EDGE",EDGE,{"disambiguationData":[OSD([subQ1,subQ0])]})],"blendedInto":[]});}
            var Q172;
            {var subQ0=sQuery(id+"F0.wireOp",EDGE,"E14");Q172=makeQuery(id+"F2.opFillet","BLEND_EDGE",EDGE,{"blendedFrom":[makeQuery(id+"F1.opExtrude","CAP_VERTEX",VERTEX,{"disambiguationData":[OSD([sQuery(id+"F0.wireOp",EDGE,"E2"),subQ0])],"isStart":false}),makeQuery(id+"F1.opExtrude","CAP_EDGE",EDGE,{"disambiguationData":[OSD([subQ0])],"isStart":false})],"blendedInto":[]});}
            var Q173;
            {var subQ0=sQuery(id+"F0.wireOp",EDGE,"E31.trimOffspring");var subQ1=sQuery(id+"F0.wireOp",EDGE,"E27.trimOffspring");Q173=makeQuery(id+"F2.opFillet","BLEND_EDGE",EDGE,{"blendedFrom":[makeQuery(id+"F1.opExtrude","CAP_VERTEX",VERTEX,{"disambiguationData":[OSD([subQ1,subQ0])],"isStart":false}),makeQuery(id+"F1.opExtrude","CAP_FACE",FACE,{"disambiguationData":[OSD([sQuery(id+"F0.wireOp",EDGE,"E0"),sQuery(id+"F0.wireOp",EDGE,"E2"),sQuery(id+"F0.wireOp",EDGE,"E5.0"),sQuery(id+"F0.wireOp",EDGE,"E5.1"),sQuery(id+"F0.wireOp",EDGE,"E5.2"),sQuery(id+"F0.wireOp",EDGE,"E5.3"),sQuery(id+"F0.wireOp",EDGE,"E5.4"),sQuery(id+"F0.wireOp",EDGE,"E5.5"),sQuery(id+"F0.wireOp",EDGE,"E6.0"),sQuery(id+"F0.wireOp",EDGE,"E6.1"),sQuery(id+"F0.wireOp",EDGE,"E6.2"),sQuery(id+"F0.wireOp",EDGE,"E6.3"),sQuery(id+"F0.wireOp",EDGE,"E6.4"),sQuery(id+"F0.wireOp",EDGE,"E6.5"),sQuery(id+"F0.wireOp",EDGE,"E7.0"),sQuery(id+"F0.wireOp",EDGE,"E7.1"),sQuery(id+"F0.wireOp",EDGE,"E7.2"),sQuery(id+"F0.wireOp",EDGE,"E7.3"),sQuery(id+"F0.wireOp",EDGE,"E7.4"),sQuery(id+"F0.wireOp",EDGE,"E7.5"),sQuery(id+"F0.wireOp",EDGE,"E8.0"),sQuery(id+"F0.wireOp",EDGE,"E8.1"),sQuery(id+"F0.wireOp",EDGE,"E8.2"),sQuery(id+"F0.wireOp",EDGE,"E8.3"),sQuery(id+"F0.wireOp",EDGE,"E8.4"),sQuery(id+"F0.wireOp",EDGE,"E8.5"),sQuery(id+"F0.wireOp",EDGE,"E9"),sQuery(id+"F0.wireOp",EDGE,"E10"),sQuery(id+"F0.wireOp",EDGE,"E11"),sQuery(id+"F0.wireOp",EDGE,"E12"),sQuery(id+"F0.wireOp",EDGE,"E13"),sQuery(id+"F0.wireOp",EDGE,"E14"),sQuery(id+"F0.wireOp",EDGE,"E15"),sQuery(id+"F0.wireOp",EDGE,"E16"),sQuery(id+"F0.wireOp",EDGE,"E19.trimOffspring"),sQuery(id+"F0.wireOp",EDGE,"E20.trimOffspring"),sQuery(id+"F0.wireOp",EDGE,"E23.trimOffspring"),sQuery(id+"F0.wireOp",EDGE,"E26.trimOffspring"),subQ1,subQ0,sQuery(id+"F0.wireOp",EDGE,"E34.trimOffspring")])],"isStart":false})],"blendedInto":[makeQuery(id+"F1.opExtrude","CAP_FACE",FACE,{"disambiguationData":[OSD([sQuery(id+"F0.wireOp",EDGE,"E0"),sQuery(id+"F0.wireOp",EDGE,"E2"),sQuery(id+"F0.wireOp",EDGE,"E5.0"),sQuery(id+"F0.wireOp",EDGE,"E5.1"),sQuery(id+"F0.wireOp",EDGE,"E5.2"),sQuery(id+"F0.wireOp",EDGE,"E5.3"),sQuery(id+"F0.wireOp",EDGE,"E5.4"),sQuery(id+"F0.wireOp",EDGE,"E5.5"),sQuery(id+"F0.wireOp",EDGE,"E6.0"),sQuery(id+"F0.wireOp",EDGE,"E6.1"),sQuery(id+"F0.wireOp",EDGE,"E6.2"),sQuery(id+"F0.wireOp",EDGE,"E6.3"),sQuery(id+"F0.wireOp",EDGE,"E6.4"),sQuery(id+"F0.wireOp",EDGE,"E6.5"),sQuery(id+"F0.wireOp",EDGE,"E7.0"),sQuery(id+"F0.wireOp",EDGE,"E7.1"),sQuery(id+"F0.wireOp",EDGE,"E7.2"),sQuery(id+"F0.wireOp",EDGE,"E7.3"),sQuery(id+"F0.wireOp",EDGE,"E7.4"),sQuery(id+"F0.wireOp",EDGE,"E7.5"),sQuery(id+"F0.wireOp",EDGE,"E8.0"),sQuery(id+"F0.wireOp",EDGE,"E8.1"),sQuery(id+"F0.wireOp",EDGE,"E8.2"),sQuery(id+"F0.wireOp",EDGE,"E8.3"),sQuery(id+"F0.wireOp",EDGE,"E8.4"),sQuery(id+"F0.wireOp",EDGE,"E8.5"),sQuery(id+"F0.wireOp",EDGE,"E9"),sQuery(id+"F0.wireOp",EDGE,"E10"),sQuery(id+"F0.wireOp",EDGE,"E11"),sQuery(id+"F0.wireOp",EDGE,"E12"),sQuery(id+"F0.wireOp",EDGE,"E13"),sQuery(id+"F0.wireOp",EDGE,"E14"),sQuery(id+"F0.wireOp",EDGE,"E15"),sQuery(id+"F0.wireOp",EDGE,"E16"),sQuery(id+"F0.wireOp",EDGE,"E19.trimOffspring"),sQuery(id+"F0.wireOp",EDGE,"E20.trimOffspring"),sQuery(id+"F0.wireOp",EDGE,"E23.trimOffspring"),sQuery(id+"F0.wireOp",EDGE,"E26.trimOffspring"),subQ1,subQ0,sQuery(id+"F0.wireOp",EDGE,"E34.trimOffspring")])],"isStart":false})]});}
            var Q174;
            {var subQ0=sQuery(id+"F0.wireOp",EDGE,"E31.trimOffspring");Q174=makeQuery(id+"F2.opFillet","BLEND_EDGE",EDGE,{"blendedFrom":[makeQuery(id+"F1.opExtrude","CAP_VERTEX",VERTEX,{"disambiguationData":[OSD([sQuery(id+"F0.wireOp",EDGE,"E27.trimOffspring"),subQ0])],"isStart":false}),makeQuery(id+"F1.opExtrude","CAP_EDGE",EDGE,{"disambiguationData":[OSD([subQ0])],"isStart":false})],"blendedInto":[]});}
            var Q175;
            {var subQ0=sQuery(id+"F0.wireOp",EDGE,"E27.trimOffspring");Q175=makeQuery(id+"F2.opFillet","BLEND_EDGE",EDGE,{"blendedFrom":[makeQuery(id+"F1.opExtrude","CAP_EDGE",EDGE,{"disambiguationData":[OSD([subQ0])],"isStart":false}),makeQuery(id+"F1.opExtrude","SWEPT_FACE",FACE,{"disambiguationData":[OSD([subQ0])]})],"blendedInto":[makeQuery(id+"F1.opExtrude","SWEPT_FACE",FACE,{"disambiguationData":[OSD([subQ0])]})]});}
            var Q176;
            {var subQ0=sQuery(id+"F0.wireOp",EDGE,"E26.trimOffspring");var subQ1=sQuery(id+"F0.wireOp",EDGE,"E16");Q176=makeQuery(id+"F2.opFillet","BLEND_EDGE",EDGE,{"blendedFrom":[makeQuery(id+"F1.opExtrude","CAP_VERTEX",VERTEX,{"disambiguationData":[OSD([subQ1,subQ0])],"isStart":true}),makeQuery(id+"F1.opExtrude","SWEPT_EDGE",EDGE,{"disambiguationData":[OSD([subQ1,subQ0])]})],"blendedInto":[]});}
            var Q177;
            {var subQ0=sQuery(id+"F0.wireOp",EDGE,"E34.trimOffspring");var subQ1=sQuery(id+"F0.wireOp",EDGE,"E26.trimOffspring");Q177=makeQuery(id+"F2.opFillet","BLEND_EDGE",EDGE,{"blendedFrom":[makeQuery(id+"F1.opExtrude","CAP_VERTEX",VERTEX,{"disambiguationData":[OSD([subQ1,subQ0])],"isStart":true}),makeQuery(id+"F1.opExtrude","SWEPT_EDGE",EDGE,{"disambiguationData":[OSD([subQ1,subQ0])]})],"blendedInto":[]});}
            var Q178;
            Q178=makeQuery(id+"F2.opFillet","BLEND_EDGE",EDGE,{"blendedFrom":[makeQuery(id+"F1.opExtrude","CAP_EDGE",EDGE,{"disambiguationData":[OSD([sQuery(id+"F0.wireOp",EDGE,"E9")])],"isStart":false}),makeQuery(id+"F1.opExtrude","CAP_EDGE",EDGE,{"disambiguationData":[OSD([sQuery(id+"F0.wireOp",EDGE,"E13")])],"isStart":false})],"blendedInto":[]});
            var Q179;
            Q179=makeQuery(id+"F2.opFillet","BLEND_EDGE",EDGE,{"blendedFrom":[makeQuery(id+"F1.opExtrude","CAP_EDGE",EDGE,{"disambiguationData":[OSD([sQuery(id+"F0.wireOp",EDGE,"E11")])],"isStart":false}),makeQuery(id+"F1.opExtrude","CAP_EDGE",EDGE,{"disambiguationData":[OSD([sQuery(id+"F0.wireOp",EDGE,"E14")])],"isStart":false})],"blendedInto":[]});
            var Q180;
            Q180=makeQuery(id+"F2.opFillet","BLEND_EDGE",EDGE,{"blendedFrom":[makeQuery(id+"F1.opExtrude","CAP_EDGE",EDGE,{"disambiguationData":[OSD([sQuery(id+"F0.wireOp",EDGE,"E11")])],"isStart":false}),makeQuery(id+"F1.opExtrude","CAP_EDGE",EDGE,{"disambiguationData":[OSD([sQuery(id+"F0.wireOp",EDGE,"E15")])],"isStart":false})],"blendedInto":[]});
            var Q181;
            {var subQ0=sQuery(id+"F0.wireOp",EDGE,"E14");Q181=makeQuery(id+"F2.opFillet","BLEND_EDGE",EDGE,{"blendedFrom":[makeQuery(id+"F1.opExtrude","CAP_EDGE",EDGE,{"disambiguationData":[OSD([subQ0])],"isStart":true}),makeQuery(id+"F1.opExtrude","SWEPT_FACE",FACE,{"disambiguationData":[OSD([subQ0])]})],"blendedInto":[makeQuery(id+"F1.opExtrude","SWEPT_FACE",FACE,{"disambiguationData":[OSD([subQ0])]})]});}
            var Q182;
            {var subQ0=sQuery(id+"F0.wireOp",EDGE,"E2");Q182=makeQuery(id+"F2.opFillet","BLEND_EDGE",EDGE,{"blendedFrom":[makeQuery(id+"F1.opExtrude","SWEPT_EDGE",EDGE,{"disambiguationData":[OSD([subQ0,sQuery(id+"F0.wireOp",EDGE,"E14")])]}),makeQuery(id+"F1.opExtrude","SWEPT_FACE",FACE,{"disambiguationData":[OSD([subQ0])]})],"blendedInto":[makeQuery(id+"F1.opExtrude","SWEPT_FACE",FACE,{"disambiguationData":[OSD([subQ0])]})]});}
            var Q183;
            {var subQ0=sQuery(id+"F0.wireOp",EDGE,"E20.trimOffspring");Q183=makeQuery(id+"F2.opFillet","BLEND_EDGE",EDGE,{"blendedFrom":[makeQuery(id+"F1.opExtrude","SWEPT_EDGE",EDGE,{"disambiguationData":[OSD([subQ0,sQuery(id+"F0.wireOp",EDGE,"E23.trimOffspring")])]}),makeQuery(id+"F1.opExtrude","SWEPT_FACE",FACE,{"disambiguationData":[OSD([subQ0])]})],"blendedInto":[makeQuery(id+"F1.opExtrude","SWEPT_FACE",FACE,{"disambiguationData":[OSD([subQ0])]})]});}
            var Q184;
            {var subQ0=sQuery(id+"F0.wireOp",EDGE,"E14");Q184=makeQuery(id+"F2.opFillet","BLEND_EDGE",EDGE,{"blendedFrom":[makeQuery(id+"F1.opExtrude","CAP_EDGE",EDGE,{"disambiguationData":[OSD([subQ0])],"isStart":false}),makeQuery(id+"F1.opExtrude","CAP_FACE",FACE,{"disambiguationData":[OSD([sQuery(id+"F0.wireOp",EDGE,"E0"),sQuery(id+"F0.wireOp",EDGE,"E2"),sQuery(id+"F0.wireOp",EDGE,"E5.0"),sQuery(id+"F0.wireOp",EDGE,"E5.1"),sQuery(id+"F0.wireOp",EDGE,"E5.2"),sQuery(id+"F0.wireOp",EDGE,"E5.3"),sQuery(id+"F0.wireOp",EDGE,"E5.4"),sQuery(id+"F0.wireOp",EDGE,"E5.5"),sQuery(id+"F0.wireOp",EDGE,"E6.0"),sQuery(id+"F0.wireOp",EDGE,"E6.1"),sQuery(id+"F0.wireOp",EDGE,"E6.2"),sQuery(id+"F0.wireOp",EDGE,"E6.3"),sQuery(id+"F0.wireOp",EDGE,"E6.4"),sQuery(id+"F0.wireOp",EDGE,"E6.5"),sQuery(id+"F0.wireOp",EDGE,"E7.0"),sQuery(id+"F0.wireOp",EDGE,"E7.1"),sQuery(id+"F0.wireOp",EDGE,"E7.2"),sQuery(id+"F0.wireOp",EDGE,"E7.3"),sQuery(id+"F0.wireOp",EDGE,"E7.4"),sQuery(id+"F0.wireOp",EDGE,"E7.5"),sQuery(id+"F0.wireOp",EDGE,"E8.0"),sQuery(id+"F0.wireOp",EDGE,"E8.1"),sQuery(id+"F0.wireOp",EDGE,"E8.2"),sQuery(id+"F0.wireOp",EDGE,"E8.3"),sQuery(id+"F0.wireOp",EDGE,"E8.4"),sQuery(id+"F0.wireOp",EDGE,"E8.5"),sQuery(id+"F0.wireOp",EDGE,"E9"),sQuery(id+"F0.wireOp",EDGE,"E10"),sQuery(id+"F0.wireOp",EDGE,"E11"),sQuery(id+"F0.wireOp",EDGE,"E12"),sQuery(id+"F0.wireOp",EDGE,"E13"),subQ0,sQuery(id+"F0.wireOp",EDGE,"E15"),sQuery(id+"F0.wireOp",EDGE,"E16"),sQuery(id+"F0.wireOp",EDGE,"E19.trimOffspring"),sQuery(id+"F0.wireOp",EDGE,"E20.trimOffspring"),sQuery(id+"F0.wireOp",EDGE,"E23.trimOffspring"),sQuery(id+"F0.wireOp",EDGE,"E26.trimOffspring"),sQuery(id+"F0.wireOp",EDGE,"E27.trimOffspring"),sQuery(id+"F0.wireOp",EDGE,"E31.trimOffspring"),sQuery(id+"F0.wireOp",EDGE,"E34.trimOffspring")])],"isStart":false})],"blendedInto":[makeQuery(id+"F1.opExtrude","CAP_FACE",FACE,{"disambiguationData":[OSD([sQuery(id+"F0.wireOp",EDGE,"E0"),sQuery(id+"F0.wireOp",EDGE,"E2"),sQuery(id+"F0.wireOp",EDGE,"E5.0"),sQuery(id+"F0.wireOp",EDGE,"E5.1"),sQuery(id+"F0.wireOp",EDGE,"E5.2"),sQuery(id+"F0.wireOp",EDGE,"E5.3"),sQuery(id+"F0.wireOp",EDGE,"E5.4"),sQuery(id+"F0.wireOp",EDGE,"E5.5"),sQuery(id+"F0.wireOp",EDGE,"E6.0"),sQuery(id+"F0.wireOp",EDGE,"E6.1"),sQuery(id+"F0.wireOp",EDGE,"E6.2"),sQuery(id+"F0.wireOp",EDGE,"E6.3"),sQuery(id+"F0.wireOp",EDGE,"E6.4"),sQuery(id+"F0.wireOp",EDGE,"E6.5"),sQuery(id+"F0.wireOp",EDGE,"E7.0"),sQuery(id+"F0.wireOp",EDGE,"E7.1"),sQuery(id+"F0.wireOp",EDGE,"E7.2"),sQuery(id+"F0.wireOp",EDGE,"E7.3"),sQuery(id+"F0.wireOp",EDGE,"E7.4"),sQuery(id+"F0.wireOp",EDGE,"E7.5"),sQuery(id+"F0.wireOp",EDGE,"E8.0"),sQuery(id+"F0.wireOp",EDGE,"E8.1"),sQuery(id+"F0.wireOp",EDGE,"E8.2"),sQuery(id+"F0.wireOp",EDGE,"E8.3"),sQuery(id+"F0.wireOp",EDGE,"E8.4"),sQuery(id+"F0.wireOp",EDGE,"E8.5"),sQuery(id+"F0.wireOp",EDGE,"E9"),sQuery(id+"F0.wireOp",EDGE,"E10"),sQuery(id+"F0.wireOp",EDGE,"E11"),sQuery(id+"F0.wireOp",EDGE,"E12"),sQuery(id+"F0.wireOp",EDGE,"E13"),subQ0,sQuery(id+"F0.wireOp",EDGE,"E15"),sQuery(id+"F0.wireOp",EDGE,"E16"),sQuery(id+"F0.wireOp",EDGE,"E19.trimOffspring"),sQuery(id+"F0.wireOp",EDGE,"E20.trimOffspring"),sQuery(id+"F0.wireOp",EDGE,"E23.trimOffspring"),sQuery(id+"F0.wireOp",EDGE,"E26.trimOffspring"),sQuery(id+"F0.wireOp",EDGE,"E27.trimOffspring"),sQuery(id+"F0.wireOp",EDGE,"E31.trimOffspring"),sQuery(id+"F0.wireOp",EDGE,"E34.trimOffspring")])],"isStart":false})]});}
            var Q185;
            {var subQ0=sQuery(id+"F0.wireOp",EDGE,"E23.trimOffspring");Q185=makeQuery(id+"F2.opFillet","BLEND_EDGE",EDGE,{"blendedFrom":[makeQuery(id+"F1.opExtrude","SWEPT_EDGE",EDGE,{"disambiguationData":[OSD([sQuery(id+"F0.wireOp",EDGE,"E20.trimOffspring"),subQ0])]}),makeQuery(id+"F1.opExtrude","SWEPT_FACE",FACE,{"disambiguationData":[OSD([subQ0])]})],"blendedInto":[makeQuery(id+"F1.opExtrude","SWEPT_FACE",FACE,{"disambiguationData":[OSD([subQ0])]})]});}
            var Q186;
            {var subQ0=sQuery(id+"F0.wireOp",EDGE,"E14");Q186=makeQuery(id+"F2.opFillet","BLEND_EDGE",EDGE,{"blendedFrom":[makeQuery(id+"F1.opExtrude","CAP_EDGE",EDGE,{"disambiguationData":[OSD([subQ0])],"isStart":false}),makeQuery(id+"F1.opExtrude","SWEPT_FACE",FACE,{"disambiguationData":[OSD([subQ0])]})],"blendedInto":[makeQuery(id+"F1.opExtrude","SWEPT_FACE",FACE,{"disambiguationData":[OSD([subQ0])]})]});}
            var Q187;
            {var subQ0=sQuery(id+"F0.wireOp",EDGE,"E20.trimOffspring");Q187=makeQuery(id+"F2.opFillet","BLEND_EDGE",EDGE,{"blendedFrom":[makeQuery(id+"F1.opExtrude","CAP_EDGE",EDGE,{"disambiguationData":[OSD([subQ0])],"isStart":false}),makeQuery(id+"F1.opExtrude","SWEPT_FACE",FACE,{"disambiguationData":[OSD([subQ0])]})],"blendedInto":[makeQuery(id+"F1.opExtrude","SWEPT_FACE",FACE,{"disambiguationData":[OSD([subQ0])]})]});}
            var Q188;
            {var subQ0=sQuery(id+"F0.wireOp",EDGE,"E31.trimOffspring");var subQ1=sQuery(id+"F0.wireOp",EDGE,"E13");Q188=makeQuery(id+"F2.opFillet","BLEND_EDGE",EDGE,{"blendedFrom":[makeQuery(id+"F1.opExtrude","CAP_VERTEX",VERTEX,{"disambiguationData":[OSD([subQ1,subQ0])],"isStart":false}),makeQuery(id+"F1.opExtrude","SWEPT_EDGE",EDGE,{"disambiguationData":[OSD([subQ1,subQ0])]})],"blendedInto":[]});}
            var Q189;
            {var subQ0=sQuery(id+"F0.wireOp",EDGE,"E26.trimOffspring");var subQ1=sQuery(id+"F0.wireOp",EDGE,"E16");Q189=makeQuery(id+"F2.opFillet","BLEND_EDGE",EDGE,{"blendedFrom":[makeQuery(id+"F1.opExtrude","CAP_VERTEX",VERTEX,{"disambiguationData":[OSD([subQ1,subQ0])],"isStart":false}),makeQuery(id+"F1.opExtrude","SWEPT_EDGE",EDGE,{"disambiguationData":[OSD([subQ1,subQ0])]})],"blendedInto":[]});}
            var Q190;
            {var subQ0=sQuery(id+"F0.wireOp",EDGE,"E34.trimOffspring");var subQ1=sQuery(id+"F0.wireOp",EDGE,"E26.trimOffspring");Q190=makeQuery(id+"F2.opFillet","BLEND_EDGE",EDGE,{"blendedFrom":[makeQuery(id+"F1.opExtrude","CAP_VERTEX",VERTEX,{"disambiguationData":[OSD([subQ1,subQ0])],"isStart":false}),makeQuery(id+"F1.opExtrude","SWEPT_EDGE",EDGE,{"disambiguationData":[OSD([subQ1,subQ0])]})],"blendedInto":[]});}
            var Q191;
            Q191=makeQuery(id+"F1.opExtrude","SWEPT_EDGE",EDGE,{"disambiguationData":[OSD([sQuery(id+"F0.wireOp",EDGE,"E9"),sQuery(id+"F0.wireOp",EDGE,"E16")])]});
            var Q192;
            {var subQ0=sQuery(id+"F0.wireOp",EDGE,"E13");Q192=makeQuery(id+"F2.opFillet","BLEND_EDGE",EDGE,{"blendedFrom":[makeQuery(id+"F1.opExtrude","CAP_VERTEX",VERTEX,{"disambiguationData":[OSD([subQ0,sQuery(id+"F0.wireOp",EDGE,"E31.trimOffspring")])],"isStart":false}),makeQuery(id+"F1.opExtrude","CAP_EDGE",EDGE,{"disambiguationData":[OSD([subQ0])],"isStart":false})],"blendedInto":[]});}
            var Q193;
            {var subQ0=sQuery(id+"F0.wireOp",EDGE,"E26.trimOffspring");Q193=makeQuery(id+"F2.opFillet","BLEND_EDGE",EDGE,{"blendedFrom":[makeQuery(id+"F1.opExtrude","CAP_VERTEX",VERTEX,{"disambiguationData":[OSD([subQ0,sQuery(id+"F0.wireOp",EDGE,"E34.trimOffspring")])],"isStart":false}),makeQuery(id+"F1.opExtrude","CAP_EDGE",EDGE,{"disambiguationData":[OSD([subQ0])],"isStart":false})],"blendedInto":[]});}
            var Q194;
            {var subQ0=sQuery(id+"F0.wireOp",EDGE,"E15");Q194=makeQuery(id+"F2.opFillet","BLEND_EDGE",EDGE,{"blendedFrom":[makeQuery(id+"F1.opExtrude","CAP_EDGE",EDGE,{"disambiguationData":[OSD([subQ0])],"isStart":true}),makeQuery(id+"F1.opExtrude","SWEPT_FACE",FACE,{"disambiguationData":[OSD([subQ0])]})],"blendedInto":[makeQuery(id+"F1.opExtrude","SWEPT_FACE",FACE,{"disambiguationData":[OSD([subQ0])]})]});}
            var Q195;
            {var subQ0=sQuery(id+"F0.wireOp",EDGE,"E23.trimOffspring");Q195=makeQuery(id+"F2.opFillet","BLEND_EDGE",EDGE,{"blendedFrom":[makeQuery(id+"F1.opExtrude","CAP_EDGE",EDGE,{"disambiguationData":[OSD([subQ0])],"isStart":true}),makeQuery(id+"F1.opExtrude","SWEPT_FACE",FACE,{"disambiguationData":[OSD([subQ0])]})],"blendedInto":[makeQuery(id+"F1.opExtrude","SWEPT_FACE",FACE,{"disambiguationData":[OSD([subQ0])]})]});}
            var Q196;
            {var subQ0=sQuery(id+"F0.wireOp",EDGE,"E31.trimOffspring");Q196=makeQuery(id+"F2.opFillet","BLEND_EDGE",EDGE,{"blendedFrom":[makeQuery(id+"F1.opExtrude","CAP_VERTEX",VERTEX,{"disambiguationData":[OSD([sQuery(id+"F0.wireOp",EDGE,"E13"),subQ0])],"isStart":false}),makeQuery(id+"F1.opExtrude","CAP_EDGE",EDGE,{"disambiguationData":[OSD([subQ0])],"isStart":false})],"blendedInto":[]});}
            var Q197;
            {var subQ0=sQuery(id+"F0.wireOp",EDGE,"E26.trimOffspring");Q197=makeQuery(id+"F2.opFillet","BLEND_EDGE",EDGE,{"blendedFrom":[makeQuery(id+"F1.opExtrude","CAP_VERTEX",VERTEX,{"disambiguationData":[OSD([sQuery(id+"F0.wireOp",EDGE,"E16"),subQ0])],"isStart":false}),makeQuery(id+"F1.opExtrude","CAP_EDGE",EDGE,{"disambiguationData":[OSD([subQ0])],"isStart":false})],"blendedInto":[]});}
            var Q198;
            {var subQ0=sQuery(id+"F0.wireOp",EDGE,"E34.trimOffspring");Q198=makeQuery(id+"F2.opFillet","BLEND_EDGE",EDGE,{"blendedFrom":[makeQuery(id+"F1.opExtrude","CAP_VERTEX",VERTEX,{"disambiguationData":[OSD([sQuery(id+"F0.wireOp",EDGE,"E26.trimOffspring"),subQ0])],"isStart":false}),makeQuery(id+"F1.opExtrude","CAP_EDGE",EDGE,{"disambiguationData":[OSD([subQ0])],"isStart":false})],"blendedInto":[]});}
            var Q199;
            {var subQ0=sQuery(id+"F0.wireOp",EDGE,"E15");Q199=makeQuery(id+"F2.opFillet","BLEND_EDGE",EDGE,{"blendedFrom":[makeQuery(id+"F1.opExtrude","CAP_EDGE",EDGE,{"disambiguationData":[OSD([subQ0])],"isStart":false}),makeQuery(id+"F1.opExtrude","CAP_FACE",FACE,{"disambiguationData":[OSD([sQuery(id+"F0.wireOp",EDGE,"E0"),sQuery(id+"F0.wireOp",EDGE,"E2"),sQuery(id+"F0.wireOp",EDGE,"E5.0"),sQuery(id+"F0.wireOp",EDGE,"E5.1"),sQuery(id+"F0.wireOp",EDGE,"E5.2"),sQuery(id+"F0.wireOp",EDGE,"E5.3"),sQuery(id+"F0.wireOp",EDGE,"E5.4"),sQuery(id+"F0.wireOp",EDGE,"E5.5"),sQuery(id+"F0.wireOp",EDGE,"E6.0"),sQuery(id+"F0.wireOp",EDGE,"E6.1"),sQuery(id+"F0.wireOp",EDGE,"E6.2"),sQuery(id+"F0.wireOp",EDGE,"E6.3"),sQuery(id+"F0.wireOp",EDGE,"E6.4"),sQuery(id+"F0.wireOp",EDGE,"E6.5"),sQuery(id+"F0.wireOp",EDGE,"E7.0"),sQuery(id+"F0.wireOp",EDGE,"E7.1"),sQuery(id+"F0.wireOp",EDGE,"E7.2"),sQuery(id+"F0.wireOp",EDGE,"E7.3"),sQuery(id+"F0.wireOp",EDGE,"E7.4"),sQuery(id+"F0.wireOp",EDGE,"E7.5"),sQuery(id+"F0.wireOp",EDGE,"E8.0"),sQuery(id+"F0.wireOp",EDGE,"E8.1"),sQuery(id+"F0.wireOp",EDGE,"E8.2"),sQuery(id+"F0.wireOp",EDGE,"E8.3"),sQuery(id+"F0.wireOp",EDGE,"E8.4"),sQuery(id+"F0.wireOp",EDGE,"E8.5"),sQuery(id+"F0.wireOp",EDGE,"E9"),sQuery(id+"F0.wireOp",EDGE,"E10"),sQuery(id+"F0.wireOp",EDGE,"E11"),sQuery(id+"F0.wireOp",EDGE,"E12"),sQuery(id+"F0.wireOp",EDGE,"E13"),sQuery(id+"F0.wireOp",EDGE,"E14"),subQ0,sQuery(id+"F0.wireOp",EDGE,"E16"),sQuery(id+"F0.wireOp",EDGE,"E19.trimOffspring"),sQuery(id+"F0.wireOp",EDGE,"E20.trimOffspring"),sQuery(id+"F0.wireOp",EDGE,"E23.trimOffspring"),sQuery(id+"F0.wireOp",EDGE,"E26.trimOffspring"),sQuery(id+"F0.wireOp",EDGE,"E27.trimOffspring"),sQuery(id+"F0.wireOp",EDGE,"E31.trimOffspring"),sQuery(id+"F0.wireOp",EDGE,"E34.trimOffspring")])],"isStart":false})],"blendedInto":[makeQuery(id+"F1.opExtrude","CAP_FACE",FACE,{"disambiguationData":[OSD([sQuery(id+"F0.wireOp",EDGE,"E0"),sQuery(id+"F0.wireOp",EDGE,"E2"),sQuery(id+"F0.wireOp",EDGE,"E5.0"),sQuery(id+"F0.wireOp",EDGE,"E5.1"),sQuery(id+"F0.wireOp",EDGE,"E5.2"),sQuery(id+"F0.wireOp",EDGE,"E5.3"),sQuery(id+"F0.wireOp",EDGE,"E5.4"),sQuery(id+"F0.wireOp",EDGE,"E5.5"),sQuery(id+"F0.wireOp",EDGE,"E6.0"),sQuery(id+"F0.wireOp",EDGE,"E6.1"),sQuery(id+"F0.wireOp",EDGE,"E6.2"),sQuery(id+"F0.wireOp",EDGE,"E6.3"),sQuery(id+"F0.wireOp",EDGE,"E6.4"),sQuery(id+"F0.wireOp",EDGE,"E6.5"),sQuery(id+"F0.wireOp",EDGE,"E7.0"),sQuery(id+"F0.wireOp",EDGE,"E7.1"),sQuery(id+"F0.wireOp",EDGE,"E7.2"),sQuery(id+"F0.wireOp",EDGE,"E7.3"),sQuery(id+"F0.wireOp",EDGE,"E7.4"),sQuery(id+"F0.wireOp",EDGE,"E7.5"),sQuery(id+"F0.wireOp",EDGE,"E8.0"),sQuery(id+"F0.wireOp",EDGE,"E8.1"),sQuery(id+"F0.wireOp",EDGE,"E8.2"),sQuery(id+"F0.wireOp",EDGE,"E8.3"),sQuery(id+"F0.wireOp",EDGE,"E8.4"),sQuery(id+"F0.wireOp",EDGE,"E8.5"),sQuery(id+"F0.wireOp",EDGE,"E9"),sQuery(id+"F0.wireOp",EDGE,"E10"),sQuery(id+"F0.wireOp",EDGE,"E11"),sQuery(id+"F0.wireOp",EDGE,"E12"),sQuery(id+"F0.wireOp",EDGE,"E13"),sQuery(id+"F0.wireOp",EDGE,"E14"),subQ0,sQuery(id+"F0.wireOp",EDGE,"E16"),sQuery(id+"F0.wireOp",EDGE,"E19.trimOffspring"),sQuery(id+"F0.wireOp",EDGE,"E20.trimOffspring"),sQuery(id+"F0.wireOp",EDGE,"E23.trimOffspring"),sQuery(id+"F0.wireOp",EDGE,"E26.trimOffspring"),sQuery(id+"F0.wireOp",EDGE,"E27.trimOffspring"),sQuery(id+"F0.wireOp",EDGE,"E31.trimOffspring"),sQuery(id+"F0.wireOp",EDGE,"E34.trimOffspring")])],"isStart":false})]});}
            var Q200;
            {var subQ0=sQuery(id+"F0.wireOp",EDGE,"E34.trimOffspring");Q200=makeQuery(id+"F2.opFillet","BLEND_EDGE",EDGE,{"blendedFrom":[makeQuery(id+"F1.opExtrude","CAP_EDGE",EDGE,{"disambiguationData":[OSD([subQ0])],"isStart":false}),makeQuery(id+"F1.opExtrude","CAP_FACE",FACE,{"disambiguationData":[OSD([sQuery(id+"F0.wireOp",EDGE,"E0"),sQuery(id+"F0.wireOp",EDGE,"E2"),sQuery(id+"F0.wireOp",EDGE,"E5.0"),sQuery(id+"F0.wireOp",EDGE,"E5.1"),sQuery(id+"F0.wireOp",EDGE,"E5.2"),sQuery(id+"F0.wireOp",EDGE,"E5.3"),sQuery(id+"F0.wireOp",EDGE,"E5.4"),sQuery(id+"F0.wireOp",EDGE,"E5.5"),sQuery(id+"F0.wireOp",EDGE,"E6.0"),sQuery(id+"F0.wireOp",EDGE,"E6.1"),sQuery(id+"F0.wireOp",EDGE,"E6.2"),sQuery(id+"F0.wireOp",EDGE,"E6.3"),sQuery(id+"F0.wireOp",EDGE,"E6.4"),sQuery(id+"F0.wireOp",EDGE,"E6.5"),sQuery(id+"F0.wireOp",EDGE,"E7.0"),sQuery(id+"F0.wireOp",EDGE,"E7.1"),sQuery(id+"F0.wireOp",EDGE,"E7.2"),sQuery(id+"F0.wireOp",EDGE,"E7.3"),sQuery(id+"F0.wireOp",EDGE,"E7.4"),sQuery(id+"F0.wireOp",EDGE,"E7.5"),sQuery(id+"F0.wireOp",EDGE,"E8.0"),sQuery(id+"F0.wireOp",EDGE,"E8.1"),sQuery(id+"F0.wireOp",EDGE,"E8.2"),sQuery(id+"F0.wireOp",EDGE,"E8.3"),sQuery(id+"F0.wireOp",EDGE,"E8.4"),sQuery(id+"F0.wireOp",EDGE,"E8.5"),sQuery(id+"F0.wireOp",EDGE,"E9"),sQuery(id+"F0.wireOp",EDGE,"E10"),sQuery(id+"F0.wireOp",EDGE,"E11"),sQuery(id+"F0.wireOp",EDGE,"E12"),sQuery(id+"F0.wireOp",EDGE,"E13"),sQuery(id+"F0.wireOp",EDGE,"E14"),sQuery(id+"F0.wireOp",EDGE,"E15"),sQuery(id+"F0.wireOp",EDGE,"E16"),sQuery(id+"F0.wireOp",EDGE,"E19.trimOffspring"),sQuery(id+"F0.wireOp",EDGE,"E20.trimOffspring"),sQuery(id+"F0.wireOp",EDGE,"E23.trimOffspring"),sQuery(id+"F0.wireOp",EDGE,"E26.trimOffspring"),sQuery(id+"F0.wireOp",EDGE,"E27.trimOffspring"),sQuery(id+"F0.wireOp",EDGE,"E31.trimOffspring"),subQ0])],"isStart":false})],"blendedInto":[makeQuery(id+"F1.opExtrude","CAP_FACE",FACE,{"disambiguationData":[OSD([sQuery(id+"F0.wireOp",EDGE,"E0"),sQuery(id+"F0.wireOp",EDGE,"E2"),sQuery(id+"F0.wireOp",EDGE,"E5.0"),sQuery(id+"F0.wireOp",EDGE,"E5.1"),sQuery(id+"F0.wireOp",EDGE,"E5.2"),sQuery(id+"F0.wireOp",EDGE,"E5.3"),sQuery(id+"F0.wireOp",EDGE,"E5.4"),sQuery(id+"F0.wireOp",EDGE,"E5.5"),sQuery(id+"F0.wireOp",EDGE,"E6.0"),sQuery(id+"F0.wireOp",EDGE,"E6.1"),sQuery(id+"F0.wireOp",EDGE,"E6.2"),sQuery(id+"F0.wireOp",EDGE,"E6.3"),sQuery(id+"F0.wireOp",EDGE,"E6.4"),sQuery(id+"F0.wireOp",EDGE,"E6.5"),sQuery(id+"F0.wireOp",EDGE,"E7.0"),sQuery(id+"F0.wireOp",EDGE,"E7.1"),sQuery(id+"F0.wireOp",EDGE,"E7.2"),sQuery(id+"F0.wireOp",EDGE,"E7.3"),sQuery(id+"F0.wireOp",EDGE,"E7.4"),sQuery(id+"F0.wireOp",EDGE,"E7.5"),sQuery(id+"F0.wireOp",EDGE,"E8.0"),sQuery(id+"F0.wireOp",EDGE,"E8.1"),sQuery(id+"F0.wireOp",EDGE,"E8.2"),sQuery(id+"F0.wireOp",EDGE,"E8.3"),sQuery(id+"F0.wireOp",EDGE,"E8.4"),sQuery(id+"F0.wireOp",EDGE,"E8.5"),sQuery(id+"F0.wireOp",EDGE,"E9"),sQuery(id+"F0.wireOp",EDGE,"E10"),sQuery(id+"F0.wireOp",EDGE,"E11"),sQuery(id+"F0.wireOp",EDGE,"E12"),sQuery(id+"F0.wireOp",EDGE,"E13"),sQuery(id+"F0.wireOp",EDGE,"E14"),sQuery(id+"F0.wireOp",EDGE,"E15"),sQuery(id+"F0.wireOp",EDGE,"E16"),sQuery(id+"F0.wireOp",EDGE,"E19.trimOffspring"),sQuery(id+"F0.wireOp",EDGE,"E20.trimOffspring"),sQuery(id+"F0.wireOp",EDGE,"E23.trimOffspring"),sQuery(id+"F0.wireOp",EDGE,"E26.trimOffspring"),sQuery(id+"F0.wireOp",EDGE,"E27.trimOffspring"),sQuery(id+"F0.wireOp",EDGE,"E31.trimOffspring"),subQ0])],"isStart":false})]});}
            var Q201;
            {var subQ0=sQuery(id+"F0.wireOp",EDGE,"E31.trimOffspring");var subQ1=sQuery(id+"F0.wireOp",EDGE,"E13");Q201=makeQuery(id+"F2.opFillet","BLEND_EDGE",EDGE,{"blendedFrom":[makeQuery(id+"F1.opExtrude","CAP_VERTEX",VERTEX,{"disambiguationData":[OSD([subQ1,subQ0])],"isStart":false}),makeQuery(id+"F1.opExtrude","CAP_FACE",FACE,{"disambiguationData":[OSD([sQuery(id+"F0.wireOp",EDGE,"E0"),sQuery(id+"F0.wireOp",EDGE,"E2"),sQuery(id+"F0.wireOp",EDGE,"E5.0"),sQuery(id+"F0.wireOp",EDGE,"E5.1"),sQuery(id+"F0.wireOp",EDGE,"E5.2"),sQuery(id+"F0.wireOp",EDGE,"E5.3"),sQuery(id+"F0.wireOp",EDGE,"E5.4"),sQuery(id+"F0.wireOp",EDGE,"E5.5"),sQuery(id+"F0.wireOp",EDGE,"E6.0"),sQuery(id+"F0.wireOp",EDGE,"E6.1"),sQuery(id+"F0.wireOp",EDGE,"E6.2"),sQuery(id+"F0.wireOp",EDGE,"E6.3"),sQuery(id+"F0.wireOp",EDGE,"E6.4"),sQuery(id+"F0.wireOp",EDGE,"E6.5"),sQuery(id+"F0.wireOp",EDGE,"E7.0"),sQuery(id+"F0.wireOp",EDGE,"E7.1"),sQuery(id+"F0.wireOp",EDGE,"E7.2"),sQuery(id+"F0.wireOp",EDGE,"E7.3"),sQuery(id+"F0.wireOp",EDGE,"E7.4"),sQuery(id+"F0.wireOp",EDGE,"E7.5"),sQuery(id+"F0.wireOp",EDGE,"E8.0"),sQuery(id+"F0.wireOp",EDGE,"E8.1"),sQuery(id+"F0.wireOp",EDGE,"E8.2"),sQuery(id+"F0.wireOp",EDGE,"E8.3"),sQuery(id+"F0.wireOp",EDGE,"E8.4"),sQuery(id+"F0.wireOp",EDGE,"E8.5"),sQuery(id+"F0.wireOp",EDGE,"E9"),sQuery(id+"F0.wireOp",EDGE,"E10"),sQuery(id+"F0.wireOp",EDGE,"E11"),sQuery(id+"F0.wireOp",EDGE,"E12"),subQ1,sQuery(id+"F0.wireOp",EDGE,"E14"),sQuery(id+"F0.wireOp",EDGE,"E15"),sQuery(id+"F0.wireOp",EDGE,"E16"),sQuery(id+"F0.wireOp",EDGE,"E19.trimOffspring"),sQuery(id+"F0.wireOp",EDGE,"E20.trimOffspring"),sQuery(id+"F0.wireOp",EDGE,"E23.trimOffspring"),sQuery(id+"F0.wireOp",EDGE,"E26.trimOffspring"),sQuery(id+"F0.wireOp",EDGE,"E27.trimOffspring"),subQ0,sQuery(id+"F0.wireOp",EDGE,"E34.trimOffspring")])],"isStart":false})],"blendedInto":[makeQuery(id+"F1.opExtrude","CAP_FACE",FACE,{"disambiguationData":[OSD([sQuery(id+"F0.wireOp",EDGE,"E0"),sQuery(id+"F0.wireOp",EDGE,"E2"),sQuery(id+"F0.wireOp",EDGE,"E5.0"),sQuery(id+"F0.wireOp",EDGE,"E5.1"),sQuery(id+"F0.wireOp",EDGE,"E5.2"),sQuery(id+"F0.wireOp",EDGE,"E5.3"),sQuery(id+"F0.wireOp",EDGE,"E5.4"),sQuery(id+"F0.wireOp",EDGE,"E5.5"),sQuery(id+"F0.wireOp",EDGE,"E6.0"),sQuery(id+"F0.wireOp",EDGE,"E6.1"),sQuery(id+"F0.wireOp",EDGE,"E6.2"),sQuery(id+"F0.wireOp",EDGE,"E6.3"),sQuery(id+"F0.wireOp",EDGE,"E6.4"),sQuery(id+"F0.wireOp",EDGE,"E6.5"),sQuery(id+"F0.wireOp",EDGE,"E7.0"),sQuery(id+"F0.wireOp",EDGE,"E7.1"),sQuery(id+"F0.wireOp",EDGE,"E7.2"),sQuery(id+"F0.wireOp",EDGE,"E7.3"),sQuery(id+"F0.wireOp",EDGE,"E7.4"),sQuery(id+"F0.wireOp",EDGE,"E7.5"),sQuery(id+"F0.wireOp",EDGE,"E8.0"),sQuery(id+"F0.wireOp",EDGE,"E8.1"),sQuery(id+"F0.wireOp",EDGE,"E8.2"),sQuery(id+"F0.wireOp",EDGE,"E8.3"),sQuery(id+"F0.wireOp",EDGE,"E8.4"),sQuery(id+"F0.wireOp",EDGE,"E8.5"),sQuery(id+"F0.wireOp",EDGE,"E9"),sQuery(id+"F0.wireOp",EDGE,"E10"),sQuery(id+"F0.wireOp",EDGE,"E11"),sQuery(id+"F0.wireOp",EDGE,"E12"),subQ1,sQuery(id+"F0.wireOp",EDGE,"E14"),sQuery(id+"F0.wireOp",EDGE,"E15"),sQuery(id+"F0.wireOp",EDGE,"E16"),sQuery(id+"F0.wireOp",EDGE,"E19.trimOffspring"),sQuery(id+"F0.wireOp",EDGE,"E20.trimOffspring"),sQuery(id+"F0.wireOp",EDGE,"E23.trimOffspring"),sQuery(id+"F0.wireOp",EDGE,"E26.trimOffspring"),sQuery(id+"F0.wireOp",EDGE,"E27.trimOffspring"),subQ0,sQuery(id+"F0.wireOp",EDGE,"E34.trimOffspring")])],"isStart":false})]});}
            var Q202;
            {var subQ0=sQuery(id+"F0.wireOp",EDGE,"E34.trimOffspring");var subQ1=sQuery(id+"F0.wireOp",EDGE,"E26.trimOffspring");Q202=makeQuery(id+"F2.opFillet","BLEND_EDGE",EDGE,{"blendedFrom":[makeQuery(id+"F1.opExtrude","CAP_VERTEX",VERTEX,{"disambiguationData":[OSD([subQ1,subQ0])],"isStart":false}),makeQuery(id+"F1.opExtrude","CAP_FACE",FACE,{"disambiguationData":[OSD([sQuery(id+"F0.wireOp",EDGE,"E0"),sQuery(id+"F0.wireOp",EDGE,"E2"),sQuery(id+"F0.wireOp",EDGE,"E5.0"),sQuery(id+"F0.wireOp",EDGE,"E5.1"),sQuery(id+"F0.wireOp",EDGE,"E5.2"),sQuery(id+"F0.wireOp",EDGE,"E5.3"),sQuery(id+"F0.wireOp",EDGE,"E5.4"),sQuery(id+"F0.wireOp",EDGE,"E5.5"),sQuery(id+"F0.wireOp",EDGE,"E6.0"),sQuery(id+"F0.wireOp",EDGE,"E6.1"),sQuery(id+"F0.wireOp",EDGE,"E6.2"),sQuery(id+"F0.wireOp",EDGE,"E6.3"),sQuery(id+"F0.wireOp",EDGE,"E6.4"),sQuery(id+"F0.wireOp",EDGE,"E6.5"),sQuery(id+"F0.wireOp",EDGE,"E7.0"),sQuery(id+"F0.wireOp",EDGE,"E7.1"),sQuery(id+"F0.wireOp",EDGE,"E7.2"),sQuery(id+"F0.wireOp",EDGE,"E7.3"),sQuery(id+"F0.wireOp",EDGE,"E7.4"),sQuery(id+"F0.wireOp",EDGE,"E7.5"),sQuery(id+"F0.wireOp",EDGE,"E8.0"),sQuery(id+"F0.wireOp",EDGE,"E8.1"),sQuery(id+"F0.wireOp",EDGE,"E8.2"),sQuery(id+"F0.wireOp",EDGE,"E8.3"),sQuery(id+"F0.wireOp",EDGE,"E8.4"),sQuery(id+"F0.wireOp",EDGE,"E8.5"),sQuery(id+"F0.wireOp",EDGE,"E9"),sQuery(id+"F0.wireOp",EDGE,"E10"),sQuery(id+"F0.wireOp",EDGE,"E11"),sQuery(id+"F0.wireOp",EDGE,"E12"),sQuery(id+"F0.wireOp",EDGE,"E13"),sQuery(id+"F0.wireOp",EDGE,"E14"),sQuery(id+"F0.wireOp",EDGE,"E15"),sQuery(id+"F0.wireOp",EDGE,"E16"),sQuery(id+"F0.wireOp",EDGE,"E19.trimOffspring"),sQuery(id+"F0.wireOp",EDGE,"E20.trimOffspring"),sQuery(id+"F0.wireOp",EDGE,"E23.trimOffspring"),subQ1,sQuery(id+"F0.wireOp",EDGE,"E27.trimOffspring"),sQuery(id+"F0.wireOp",EDGE,"E31.trimOffspring"),subQ0])],"isStart":false})],"blendedInto":[makeQuery(id+"F1.opExtrude","CAP_FACE",FACE,{"disambiguationData":[OSD([sQuery(id+"F0.wireOp",EDGE,"E0"),sQuery(id+"F0.wireOp",EDGE,"E2"),sQuery(id+"F0.wireOp",EDGE,"E5.0"),sQuery(id+"F0.wireOp",EDGE,"E5.1"),sQuery(id+"F0.wireOp",EDGE,"E5.2"),sQuery(id+"F0.wireOp",EDGE,"E5.3"),sQuery(id+"F0.wireOp",EDGE,"E5.4"),sQuery(id+"F0.wireOp",EDGE,"E5.5"),sQuery(id+"F0.wireOp",EDGE,"E6.0"),sQuery(id+"F0.wireOp",EDGE,"E6.1"),sQuery(id+"F0.wireOp",EDGE,"E6.2"),sQuery(id+"F0.wireOp",EDGE,"E6.3"),sQuery(id+"F0.wireOp",EDGE,"E6.4"),sQuery(id+"F0.wireOp",EDGE,"E6.5"),sQuery(id+"F0.wireOp",EDGE,"E7.0"),sQuery(id+"F0.wireOp",EDGE,"E7.1"),sQuery(id+"F0.wireOp",EDGE,"E7.2"),sQuery(id+"F0.wireOp",EDGE,"E7.3"),sQuery(id+"F0.wireOp",EDGE,"E7.4"),sQuery(id+"F0.wireOp",EDGE,"E7.5"),sQuery(id+"F0.wireOp",EDGE,"E8.0"),sQuery(id+"F0.wireOp",EDGE,"E8.1"),sQuery(id+"F0.wireOp",EDGE,"E8.2"),sQuery(id+"F0.wireOp",EDGE,"E8.3"),sQuery(id+"F0.wireOp",EDGE,"E8.4"),sQuery(id+"F0.wireOp",EDGE,"E8.5"),sQuery(id+"F0.wireOp",EDGE,"E9"),sQuery(id+"F0.wireOp",EDGE,"E10"),sQuery(id+"F0.wireOp",EDGE,"E11"),sQuery(id+"F0.wireOp",EDGE,"E12"),sQuery(id+"F0.wireOp",EDGE,"E13"),sQuery(id+"F0.wireOp",EDGE,"E14"),sQuery(id+"F0.wireOp",EDGE,"E15"),sQuery(id+"F0.wireOp",EDGE,"E16"),sQuery(id+"F0.wireOp",EDGE,"E19.trimOffspring"),sQuery(id+"F0.wireOp",EDGE,"E20.trimOffspring"),sQuery(id+"F0.wireOp",EDGE,"E23.trimOffspring"),subQ1,sQuery(id+"F0.wireOp",EDGE,"E27.trimOffspring"),sQuery(id+"F0.wireOp",EDGE,"E31.trimOffspring"),subQ0])],"isStart":false})]});}
            var Q203;
            Q203=makeQuery(id+"F1.opExtrude","SWEPT_EDGE",EDGE,{"disambiguationData":[OSD([sQuery(id+"F0.wireOp",EDGE,"E10"),sQuery(id+"F0.wireOp",EDGE,"E34.trimOffspring")])]});
            var Q204;
            {var subQ0=sQuery(id+"F0.wireOp",EDGE,"E31.trimOffspring");Q204=makeQuery(id+"F2.opFillet","BLEND_EDGE",EDGE,{"blendedFrom":[makeQuery(id+"F1.opExtrude","SWEPT_EDGE",EDGE,{"disambiguationData":[OSD([sQuery(id+"F0.wireOp",EDGE,"E27.trimOffspring"),subQ0])]}),makeQuery(id+"F1.opExtrude","SWEPT_FACE",FACE,{"disambiguationData":[OSD([subQ0])]})],"blendedInto":[makeQuery(id+"F1.opExtrude","SWEPT_FACE",FACE,{"disambiguationData":[OSD([subQ0])]})]});}
            var Q205;
            {var subQ0=sQuery(id+"F0.wireOp",EDGE,"E34.trimOffspring");Q205=makeQuery(id+"F2.opFillet","BLEND_EDGE",EDGE,{"blendedFrom":[makeQuery(id+"F1.opExtrude","CAP_EDGE",EDGE,{"disambiguationData":[OSD([subQ0])],"isStart":false}),makeQuery(id+"F1.opExtrude","SWEPT_FACE",FACE,{"disambiguationData":[OSD([subQ0])]})],"blendedInto":[makeQuery(id+"F1.opExtrude","SWEPT_FACE",FACE,{"disambiguationData":[OSD([subQ0])]})]});}
            var Q206;
            {var subQ0=sQuery(id+"F0.wireOp",EDGE,"E20.trimOffspring");var subQ1=sQuery(id+"F0.wireOp",EDGE,"E15");Q206=makeQuery(id+"F2.opFillet","BLEND_EDGE",EDGE,{"blendedFrom":[makeQuery(id+"F1.opExtrude","CAP_VERTEX",VERTEX,{"disambiguationData":[OSD([subQ1,subQ0])],"isStart":true}),makeQuery(id+"F1.opExtrude","SWEPT_EDGE",EDGE,{"disambiguationData":[OSD([subQ1,subQ0])]})],"blendedInto":[]});}
            var Q207;
            {var subQ0=sQuery(id+"F0.wireOp",EDGE,"E31.trimOffspring");var subQ1=sQuery(id+"F0.wireOp",EDGE,"E27.trimOffspring");Q207=makeQuery(id+"F2.opFillet","BLEND_EDGE",EDGE,{"blendedFrom":[makeQuery(id+"F1.opExtrude","CAP_VERTEX",VERTEX,{"disambiguationData":[OSD([subQ1,subQ0])],"isStart":true}),makeQuery(id+"F1.opExtrude","SWEPT_EDGE",EDGE,{"disambiguationData":[OSD([subQ1,subQ0])]})],"blendedInto":[]});}
            var Q208;
            Q208=makeQuery(id+"F2.opFillet","BLEND_EDGE",EDGE,{"blendedFrom":[makeQuery(id+"F1.opExtrude","CAP_EDGE",EDGE,{"disambiguationData":[OSD([sQuery(id+"F0.wireOp",EDGE,"E10")])],"isStart":false}),makeQuery(id+"F1.opExtrude","CAP_EDGE",EDGE,{"disambiguationData":[OSD([sQuery(id+"F0.wireOp",EDGE,"E23.trimOffspring")])],"isStart":false})],"blendedInto":[]});
            var Q209;
            Q209=makeQuery(id+"F2.opFillet","BLEND_EDGE",EDGE,{"blendedFrom":[makeQuery(id+"F1.opExtrude","CAP_EDGE",EDGE,{"disambiguationData":[OSD([sQuery(id+"F0.wireOp",EDGE,"E12")])],"isStart":false}),makeQuery(id+"F1.opExtrude","CAP_EDGE",EDGE,{"disambiguationData":[OSD([sQuery(id+"F0.wireOp",EDGE,"E19.trimOffspring")])],"isStart":false})],"blendedInto":[]});
            var Q210;
            Q210=makeQuery(id+"F2.opFillet","BLEND_EDGE",EDGE,{"blendedFrom":[makeQuery(id+"F1.opExtrude","CAP_EDGE",EDGE,{"disambiguationData":[OSD([sQuery(id+"F0.wireOp",EDGE,"E10")])],"isStart":false}),makeQuery(id+"F1.opExtrude","CAP_EDGE",EDGE,{"disambiguationData":[OSD([sQuery(id+"F0.wireOp",EDGE,"E34.trimOffspring")])],"isStart":false})],"blendedInto":[]});
            var Q211;
            Q211=makeQuery(id+"F2.opFillet","BLEND_EDGE",EDGE,{"blendedFrom":[makeQuery(id+"F1.opExtrude","CAP_EDGE",EDGE,{"disambiguationData":[OSD([sQuery(id+"F0.wireOp",EDGE,"E12")])],"isStart":false}),makeQuery(id+"F1.opExtrude","CAP_EDGE",EDGE,{"disambiguationData":[OSD([sQuery(id+"F0.wireOp",EDGE,"E27.trimOffspring")])],"isStart":false})],"blendedInto":[]});
            var Q212;
            {var subQ0=sQuery(id+"F0.wireOp",EDGE,"E16");Q212=makeQuery(id+"F2.opFillet","BLEND_EDGE",EDGE,{"blendedFrom":[makeQuery(id+"F1.opExtrude","CAP_EDGE",EDGE,{"disambiguationData":[OSD([subQ0])],"isStart":true}),makeQuery(id+"F1.opExtrude","SWEPT_FACE",FACE,{"disambiguationData":[OSD([subQ0])]})],"blendedInto":[makeQuery(id+"F1.opExtrude","SWEPT_FACE",FACE,{"disambiguationData":[OSD([subQ0])]})]});}
            var Q213;
            {var subQ0=sQuery(id+"F0.wireOp",EDGE,"E26.trimOffspring");Q213=makeQuery(id+"F2.opFillet","BLEND_EDGE",EDGE,{"blendedFrom":[makeQuery(id+"F1.opExtrude","CAP_EDGE",EDGE,{"disambiguationData":[OSD([subQ0])],"isStart":false}),makeQuery(id+"F1.opExtrude","CAP_FACE",FACE,{"disambiguationData":[OSD([sQuery(id+"F0.wireOp",EDGE,"E0"),sQuery(id+"F0.wireOp",EDGE,"E2"),sQuery(id+"F0.wireOp",EDGE,"E5.0"),sQuery(id+"F0.wireOp",EDGE,"E5.1"),sQuery(id+"F0.wireOp",EDGE,"E5.2"),sQuery(id+"F0.wireOp",EDGE,"E5.3"),sQuery(id+"F0.wireOp",EDGE,"E5.4"),sQuery(id+"F0.wireOp",EDGE,"E5.5"),sQuery(id+"F0.wireOp",EDGE,"E6.0"),sQuery(id+"F0.wireOp",EDGE,"E6.1"),sQuery(id+"F0.wireOp",EDGE,"E6.2"),sQuery(id+"F0.wireOp",EDGE,"E6.3"),sQuery(id+"F0.wireOp",EDGE,"E6.4"),sQuery(id+"F0.wireOp",EDGE,"E6.5"),sQuery(id+"F0.wireOp",EDGE,"E7.0"),sQuery(id+"F0.wireOp",EDGE,"E7.1"),sQuery(id+"F0.wireOp",EDGE,"E7.2"),sQuery(id+"F0.wireOp",EDGE,"E7.3"),sQuery(id+"F0.wireOp",EDGE,"E7.4"),sQuery(id+"F0.wireOp",EDGE,"E7.5"),sQuery(id+"F0.wireOp",EDGE,"E8.0"),sQuery(id+"F0.wireOp",EDGE,"E8.1"),sQuery(id+"F0.wireOp",EDGE,"E8.2"),sQuery(id+"F0.wireOp",EDGE,"E8.3"),sQuery(id+"F0.wireOp",EDGE,"E8.4"),sQuery(id+"F0.wireOp",EDGE,"E8.5"),sQuery(id+"F0.wireOp",EDGE,"E9"),sQuery(id+"F0.wireOp",EDGE,"E10"),sQuery(id+"F0.wireOp",EDGE,"E11"),sQuery(id+"F0.wireOp",EDGE,"E12"),sQuery(id+"F0.wireOp",EDGE,"E13"),sQuery(id+"F0.wireOp",EDGE,"E14"),sQuery(id+"F0.wireOp",EDGE,"E15"),sQuery(id+"F0.wireOp",EDGE,"E16"),sQuery(id+"F0.wireOp",EDGE,"E19.trimOffspring"),sQuery(id+"F0.wireOp",EDGE,"E20.trimOffspring"),sQuery(id+"F0.wireOp",EDGE,"E23.trimOffspring"),subQ0,sQuery(id+"F0.wireOp",EDGE,"E27.trimOffspring"),sQuery(id+"F0.wireOp",EDGE,"E31.trimOffspring"),sQuery(id+"F0.wireOp",EDGE,"E34.trimOffspring")])],"isStart":false})],"blendedInto":[makeQuery(id+"F1.opExtrude","CAP_FACE",FACE,{"disambiguationData":[OSD([sQuery(id+"F0.wireOp",EDGE,"E0"),sQuery(id+"F0.wireOp",EDGE,"E2"),sQuery(id+"F0.wireOp",EDGE,"E5.0"),sQuery(id+"F0.wireOp",EDGE,"E5.1"),sQuery(id+"F0.wireOp",EDGE,"E5.2"),sQuery(id+"F0.wireOp",EDGE,"E5.3"),sQuery(id+"F0.wireOp",EDGE,"E5.4"),sQuery(id+"F0.wireOp",EDGE,"E5.5"),sQuery(id+"F0.wireOp",EDGE,"E6.0"),sQuery(id+"F0.wireOp",EDGE,"E6.1"),sQuery(id+"F0.wireOp",EDGE,"E6.2"),sQuery(id+"F0.wireOp",EDGE,"E6.3"),sQuery(id+"F0.wireOp",EDGE,"E6.4"),sQuery(id+"F0.wireOp",EDGE,"E6.5"),sQuery(id+"F0.wireOp",EDGE,"E7.0"),sQuery(id+"F0.wireOp",EDGE,"E7.1"),sQuery(id+"F0.wireOp",EDGE,"E7.2"),sQuery(id+"F0.wireOp",EDGE,"E7.3"),sQuery(id+"F0.wireOp",EDGE,"E7.4"),sQuery(id+"F0.wireOp",EDGE,"E7.5"),sQuery(id+"F0.wireOp",EDGE,"E8.0"),sQuery(id+"F0.wireOp",EDGE,"E8.1"),sQuery(id+"F0.wireOp",EDGE,"E8.2"),sQuery(id+"F0.wireOp",EDGE,"E8.3"),sQuery(id+"F0.wireOp",EDGE,"E8.4"),sQuery(id+"F0.wireOp",EDGE,"E8.5"),sQuery(id+"F0.wireOp",EDGE,"E9"),sQuery(id+"F0.wireOp",EDGE,"E10"),sQuery(id+"F0.wireOp",EDGE,"E11"),sQuery(id+"F0.wireOp",EDGE,"E12"),sQuery(id+"F0.wireOp",EDGE,"E13"),sQuery(id+"F0.wireOp",EDGE,"E14"),sQuery(id+"F0.wireOp",EDGE,"E15"),sQuery(id+"F0.wireOp",EDGE,"E16"),sQuery(id+"F0.wireOp",EDGE,"E19.trimOffspring"),sQuery(id+"F0.wireOp",EDGE,"E20.trimOffspring"),sQuery(id+"F0.wireOp",EDGE,"E23.trimOffspring"),subQ0,sQuery(id+"F0.wireOp",EDGE,"E27.trimOffspring"),sQuery(id+"F0.wireOp",EDGE,"E31.trimOffspring"),sQuery(id+"F0.wireOp",EDGE,"E34.trimOffspring")])],"isStart":false})]});}
            var Q214;
            {var subQ0=sQuery(id+"F0.wireOp",EDGE,"E16");Q214=makeQuery(id+"F2.opFillet","BLEND_EDGE",EDGE,{"blendedFrom":[makeQuery(id+"F1.opExtrude","CAP_EDGE",EDGE,{"disambiguationData":[OSD([subQ0])],"isStart":false}),makeQuery(id+"F1.opExtrude","SWEPT_FACE",FACE,{"disambiguationData":[OSD([subQ0])]})],"blendedInto":[makeQuery(id+"F1.opExtrude","SWEPT_FACE",FACE,{"disambiguationData":[OSD([subQ0])]})]});}
            var Q215;
            {var subQ0=sQuery(id+"F0.wireOp",EDGE,"E26.trimOffspring");Q215=makeQuery(id+"F2.opFillet","BLEND_EDGE",EDGE,{"blendedFrom":[makeQuery(id+"F1.opExtrude","CAP_EDGE",EDGE,{"disambiguationData":[OSD([subQ0])],"isStart":false}),makeQuery(id+"F1.opExtrude","SWEPT_FACE",FACE,{"disambiguationData":[OSD([subQ0])]})],"blendedInto":[makeQuery(id+"F1.opExtrude","SWEPT_FACE",FACE,{"disambiguationData":[OSD([subQ0])]})]});}
            var Q216;
            {var subQ0=sQuery(id+"F0.wireOp",EDGE,"E20.trimOffspring");var subQ1=sQuery(id+"F0.wireOp",EDGE,"E15");Q216=makeQuery(id+"F2.opFillet","BLEND_EDGE",EDGE,{"blendedFrom":[makeQuery(id+"F1.opExtrude","CAP_VERTEX",VERTEX,{"disambiguationData":[OSD([subQ1,subQ0])],"isStart":false}),makeQuery(id+"F1.opExtrude","SWEPT_EDGE",EDGE,{"disambiguationData":[OSD([subQ1,subQ0])]})],"blendedInto":[]});}
            var Q217;
            {var subQ0=sQuery(id+"F0.wireOp",EDGE,"E31.trimOffspring");var subQ1=sQuery(id+"F0.wireOp",EDGE,"E27.trimOffspring");Q217=makeQuery(id+"F2.opFillet","BLEND_EDGE",EDGE,{"blendedFrom":[makeQuery(id+"F1.opExtrude","CAP_VERTEX",VERTEX,{"disambiguationData":[OSD([subQ1,subQ0])],"isStart":false}),makeQuery(id+"F1.opExtrude","SWEPT_EDGE",EDGE,{"disambiguationData":[OSD([subQ1,subQ0])]})],"blendedInto":[]});}
            var Q218;
            {var subQ0=sQuery(id+"F0.wireOp",EDGE,"E13");Q218=makeQuery(id+"F2.opFillet","BLEND_EDGE",EDGE,{"blendedFrom":[makeQuery(id+"F1.opExtrude","CAP_EDGE",EDGE,{"disambiguationData":[OSD([subQ0])],"isStart":false}),makeQuery(id+"F1.opExtrude","SWEPT_FACE",FACE,{"disambiguationData":[OSD([subQ0])]})],"blendedInto":[makeQuery(id+"F1.opExtrude","SWEPT_FACE",FACE,{"disambiguationData":[OSD([subQ0])]})]});}
            var Q219;
            {var subQ0=sQuery(id+"F0.wireOp",EDGE,"E15");Q219=makeQuery(id+"F2.opFillet","BLEND_EDGE",EDGE,{"blendedFrom":[makeQuery(id+"F1.opExtrude","SWEPT_EDGE",EDGE,{"disambiguationData":[OSD([subQ0,sQuery(id+"F0.wireOp",EDGE,"E20.trimOffspring")])]}),makeQuery(id+"F1.opExtrude","SWEPT_FACE",FACE,{"disambiguationData":[OSD([subQ0])]})],"blendedInto":[makeQuery(id+"F1.opExtrude","SWEPT_FACE",FACE,{"disambiguationData":[OSD([subQ0])]})]});}
            var Q220;
            {var subQ0=sQuery(id+"F0.wireOp",EDGE,"E20.trimOffspring");Q220=makeQuery(id+"F2.opFillet","BLEND_EDGE",EDGE,{"blendedFrom":[makeQuery(id+"F1.opExtrude","SWEPT_EDGE",EDGE,{"disambiguationData":[OSD([sQuery(id+"F0.wireOp",EDGE,"E15"),subQ0])]}),makeQuery(id+"F1.opExtrude","SWEPT_FACE",FACE,{"disambiguationData":[OSD([subQ0])]})],"blendedInto":[makeQuery(id+"F1.opExtrude","SWEPT_FACE",FACE,{"disambiguationData":[OSD([subQ0])]})]});}
            var Q221;
            {var subQ0=sQuery(id+"F0.wireOp",EDGE,"E2");Q221=makeQuery(id+"F2.opFillet","BLEND_EDGE",EDGE,{"blendedFrom":[makeQuery(id+"F1.opExtrude","SWEPT_EDGE",EDGE,{"disambiguationData":[OSD([subQ0,sQuery(id+"F0.wireOp",EDGE,"E19.trimOffspring")])]}),makeQuery(id+"F1.opExtrude","SWEPT_FACE",FACE,{"disambiguationData":[OSD([subQ0])]})],"blendedInto":[makeQuery(id+"F1.opExtrude","SWEPT_FACE",FACE,{"disambiguationData":[OSD([subQ0])]})]});}
            var Q222;
            {var subQ0=sQuery(id+"F0.wireOp",EDGE,"E16");Q222=makeQuery(id+"F2.opFillet","BLEND_EDGE",EDGE,{"blendedFrom":[makeQuery(id+"F1.opExtrude","SWEPT_EDGE",EDGE,{"disambiguationData":[OSD([subQ0,sQuery(id+"F0.wireOp",EDGE,"E26.trimOffspring")])]}),makeQuery(id+"F1.opExtrude","SWEPT_FACE",FACE,{"disambiguationData":[OSD([subQ0])]})],"blendedInto":[makeQuery(id+"F1.opExtrude","SWEPT_FACE",FACE,{"disambiguationData":[OSD([subQ0])]})]});}
            var Q223;
            {var subQ0=sQuery(id+"F0.wireOp",EDGE,"E19.trimOffspring");Q223=makeQuery(id+"F2.opFillet","BLEND_EDGE",EDGE,{"blendedFrom":[makeQuery(id+"F1.opExtrude","SWEPT_EDGE",EDGE,{"disambiguationData":[OSD([sQuery(id+"F0.wireOp",EDGE,"E2"),subQ0])]}),makeQuery(id+"F1.opExtrude","SWEPT_FACE",FACE,{"disambiguationData":[OSD([subQ0])]})],"blendedInto":[makeQuery(id+"F1.opExtrude","SWEPT_FACE",FACE,{"disambiguationData":[OSD([subQ0])]})]});}
            var Q224;
            {var subQ0=sQuery(id+"F0.wireOp",EDGE,"E26.trimOffspring");Q224=makeQuery(id+"F2.opFillet","BLEND_EDGE",EDGE,{"blendedFrom":[makeQuery(id+"F1.opExtrude","SWEPT_EDGE",EDGE,{"disambiguationData":[OSD([sQuery(id+"F0.wireOp",EDGE,"E16"),subQ0])]}),makeQuery(id+"F1.opExtrude","SWEPT_FACE",FACE,{"disambiguationData":[OSD([subQ0])]})],"blendedInto":[makeQuery(id+"F1.opExtrude","SWEPT_FACE",FACE,{"disambiguationData":[OSD([subQ0])]})]});}
            var Q225;
            {var subQ0=sQuery(id+"F0.wireOp",EDGE,"E14");Q225=makeQuery(id+"F2.opFillet","BLEND_EDGE",EDGE,{"blendedFrom":[makeQuery(id+"F1.opExtrude","SWEPT_EDGE",EDGE,{"disambiguationData":[OSD([sQuery(id+"F0.wireOp",EDGE,"E2"),subQ0])]}),makeQuery(id+"F1.opExtrude","SWEPT_FACE",FACE,{"disambiguationData":[OSD([subQ0])]})],"blendedInto":[makeQuery(id+"F1.opExtrude","SWEPT_FACE",FACE,{"disambiguationData":[OSD([subQ0])]})]});}
            var Q226;
            {var subQ0=sQuery(id+"F0.wireOp",EDGE,"E26.trimOffspring");Q226=makeQuery(id+"F2.opFillet","BLEND_EDGE",EDGE,{"blendedFrom":[makeQuery(id+"F1.opExtrude","SWEPT_EDGE",EDGE,{"disambiguationData":[OSD([subQ0,sQuery(id+"F0.wireOp",EDGE,"E34.trimOffspring")])]}),makeQuery(id+"F1.opExtrude","SWEPT_FACE",FACE,{"disambiguationData":[OSD([subQ0])]})],"blendedInto":[makeQuery(id+"F1.opExtrude","SWEPT_FACE",FACE,{"disambiguationData":[OSD([subQ0])]})]});}
            var Q227;
            Q227=makeQuery(id+"F1.opExtrude","SWEPT_EDGE",EDGE,{"disambiguationData":[OSD([sQuery(id+"F0.wireOp",EDGE,"E9"),sQuery(id+"F0.wireOp",EDGE,"E13")])]});
            var Q228;
            {var subQ0=sQuery(id+"F0.wireOp",EDGE,"E34.trimOffspring");Q228=makeQuery(id+"F2.opFillet","BLEND_EDGE",EDGE,{"blendedFrom":[makeQuery(id+"F1.opExtrude","SWEPT_EDGE",EDGE,{"disambiguationData":[OSD([sQuery(id+"F0.wireOp",EDGE,"E26.trimOffspring"),subQ0])]}),makeQuery(id+"F1.opExtrude","SWEPT_FACE",FACE,{"disambiguationData":[OSD([subQ0])]})],"blendedInto":[makeQuery(id+"F1.opExtrude","SWEPT_FACE",FACE,{"disambiguationData":[OSD([subQ0])]})]});}
            var Q229;
            Q229=makeQuery(id+"F1.opExtrude","SWEPT_EDGE",EDGE,{"disambiguationData":[OSD([sQuery(id+"F0.wireOp",EDGE,"E10"),sQuery(id+"F0.wireOp",EDGE,"E23.trimOffspring")])]});
            var Q230;
            {var subQ0=sQuery(id+"F0.wireOp",EDGE,"E27.trimOffspring");Q230=makeQuery(id+"F2.opFillet","BLEND_EDGE",EDGE,{"blendedFrom":[makeQuery(id+"F1.opExtrude","SWEPT_EDGE",EDGE,{"disambiguationData":[OSD([subQ0,sQuery(id+"F0.wireOp",EDGE,"E31.trimOffspring")])]}),makeQuery(id+"F1.opExtrude","SWEPT_FACE",FACE,{"disambiguationData":[OSD([subQ0])]})],"blendedInto":[makeQuery(id+"F1.opExtrude","SWEPT_FACE",FACE,{"disambiguationData":[OSD([subQ0])]})]});}
            var Q231;
            {var subQ0=sQuery(id+"F0.wireOp",EDGE,"E15");Q231=makeQuery(id+"F2.opFillet","BLEND_EDGE",EDGE,{"blendedFrom":[makeQuery(id+"F1.opExtrude","CAP_EDGE",EDGE,{"disambiguationData":[OSD([subQ0])],"isStart":false}),makeQuery(id+"F1.opExtrude","SWEPT_FACE",FACE,{"disambiguationData":[OSD([subQ0])]})],"blendedInto":[makeQuery(id+"F1.opExtrude","SWEPT_FACE",FACE,{"disambiguationData":[OSD([subQ0])]})]});}
            var Q232;
            {var subQ0=sQuery(id+"F0.wireOp",EDGE,"E23.trimOffspring");Q232=makeQuery(id+"F2.opFillet","BLEND_EDGE",EDGE,{"blendedFrom":[makeQuery(id+"F1.opExtrude","CAP_EDGE",EDGE,{"disambiguationData":[OSD([subQ0])],"isStart":false}),makeQuery(id+"F1.opExtrude","SWEPT_FACE",FACE,{"disambiguationData":[OSD([subQ0])]})],"blendedInto":[makeQuery(id+"F1.opExtrude","SWEPT_FACE",FACE,{"disambiguationData":[OSD([subQ0])]})]});}
            var Q233;
            Q233=makeQuery(id+"F1.opExtrude","SWEPT_EDGE",EDGE,{"disambiguationData":[OSD([sQuery(id+"F0.wireOp",EDGE,"E11"),sQuery(id+"F0.wireOp",EDGE,"E14")])]});
            var Q234;
            Q234=makeQuery(id+"F1.opExtrude","SWEPT_EDGE",EDGE,{"disambiguationData":[OSD([sQuery(id+"F0.wireOp",EDGE,"E11"),sQuery(id+"F0.wireOp",EDGE,"E15")])]});
            var Q235;
            Q235=makeQuery(id+"F1.opExtrude","SWEPT_EDGE",EDGE,{"disambiguationData":[OSD([sQuery(id+"F0.wireOp",EDGE,"E12"),sQuery(id+"F0.wireOp",EDGE,"E27.trimOffspring")])]});
            var Q236;
            Q236=makeQuery(id+"F1.opExtrude","SWEPT_EDGE",EDGE,{"disambiguationData":[OSD([sQuery(id+"F0.wireOp",EDGE,"E12"),sQuery(id+"F0.wireOp",EDGE,"E19.trimOffspring")])]});
            var Q237;
            {var subQ0=sQuery(id+"F0.wireOp",EDGE,"E13");Q237=makeQuery(id+"F2.opFillet","BLEND_EDGE",EDGE,{"blendedFrom":[makeQuery(id+"F1.opExtrude","SWEPT_EDGE",EDGE,{"disambiguationData":[OSD([subQ0,sQuery(id+"F0.wireOp",EDGE,"E31.trimOffspring")])]}),makeQuery(id+"F1.opExtrude","SWEPT_FACE",FACE,{"disambiguationData":[OSD([subQ0])]})],"blendedInto":[makeQuery(id+"F1.opExtrude","SWEPT_FACE",FACE,{"disambiguationData":[OSD([subQ0])]})]});}
            var Q238;
            {var subQ0=sQuery(id+"F0.wireOp",EDGE,"E12");Q238=makeQuery(id+"F2.opFillet","BLEND_EDGE",EDGE,{"blendedFrom":[makeQuery(id+"F1.opExtrude","CAP_EDGE",EDGE,{"disambiguationData":[OSD([subQ0])],"isStart":true}),makeQuery(id+"F1.opExtrude","CAP_FACE",FACE,{"disambiguationData":[OSD([sQuery(id+"F0.wireOp",EDGE,"E0"),sQuery(id+"F0.wireOp",EDGE,"E2"),sQuery(id+"F0.wireOp",EDGE,"E5.0"),sQuery(id+"F0.wireOp",EDGE,"E5.1"),sQuery(id+"F0.wireOp",EDGE,"E5.2"),sQuery(id+"F0.wireOp",EDGE,"E5.3"),sQuery(id+"F0.wireOp",EDGE,"E5.4"),sQuery(id+"F0.wireOp",EDGE,"E5.5"),sQuery(id+"F0.wireOp",EDGE,"E6.0"),sQuery(id+"F0.wireOp",EDGE,"E6.1"),sQuery(id+"F0.wireOp",EDGE,"E6.2"),sQuery(id+"F0.wireOp",EDGE,"E6.3"),sQuery(id+"F0.wireOp",EDGE,"E6.4"),sQuery(id+"F0.wireOp",EDGE,"E6.5"),sQuery(id+"F0.wireOp",EDGE,"E7.0"),sQuery(id+"F0.wireOp",EDGE,"E7.1"),sQuery(id+"F0.wireOp",EDGE,"E7.2"),sQuery(id+"F0.wireOp",EDGE,"E7.3"),sQuery(id+"F0.wireOp",EDGE,"E7.4"),sQuery(id+"F0.wireOp",EDGE,"E7.5"),sQuery(id+"F0.wireOp",EDGE,"E8.0"),sQuery(id+"F0.wireOp",EDGE,"E8.1"),sQuery(id+"F0.wireOp",EDGE,"E8.2"),sQuery(id+"F0.wireOp",EDGE,"E8.3"),sQuery(id+"F0.wireOp",EDGE,"E8.4"),sQuery(id+"F0.wireOp",EDGE,"E8.5"),sQuery(id+"F0.wireOp",EDGE,"E9"),sQuery(id+"F0.wireOp",EDGE,"E10"),sQuery(id+"F0.wireOp",EDGE,"E11"),subQ0,sQuery(id+"F0.wireOp",EDGE,"E13"),sQuery(id+"F0.wireOp",EDGE,"E14"),sQuery(id+"F0.wireOp",EDGE,"E15"),sQuery(id+"F0.wireOp",EDGE,"E16"),sQuery(id+"F0.wireOp",EDGE,"E19.trimOffspring"),sQuery(id+"F0.wireOp",EDGE,"E20.trimOffspring"),sQuery(id+"F0.wireOp",EDGE,"E23.trimOffspring"),sQuery(id+"F0.wireOp",EDGE,"E26.trimOffspring"),sQuery(id+"F0.wireOp",EDGE,"E27.trimOffspring"),sQuery(id+"F0.wireOp",EDGE,"E31.trimOffspring"),sQuery(id+"F0.wireOp",EDGE,"E34.trimOffspring")])],"isStart":true})],"blendedInto":[makeQuery(id+"F1.opExtrude","CAP_FACE",FACE,{"disambiguationData":[OSD([sQuery(id+"F0.wireOp",EDGE,"E0"),sQuery(id+"F0.wireOp",EDGE,"E2"),sQuery(id+"F0.wireOp",EDGE,"E5.0"),sQuery(id+"F0.wireOp",EDGE,"E5.1"),sQuery(id+"F0.wireOp",EDGE,"E5.2"),sQuery(id+"F0.wireOp",EDGE,"E5.3"),sQuery(id+"F0.wireOp",EDGE,"E5.4"),sQuery(id+"F0.wireOp",EDGE,"E5.5"),sQuery(id+"F0.wireOp",EDGE,"E6.0"),sQuery(id+"F0.wireOp",EDGE,"E6.1"),sQuery(id+"F0.wireOp",EDGE,"E6.2"),sQuery(id+"F0.wireOp",EDGE,"E6.3"),sQuery(id+"F0.wireOp",EDGE,"E6.4"),sQuery(id+"F0.wireOp",EDGE,"E6.5"),sQuery(id+"F0.wireOp",EDGE,"E7.0"),sQuery(id+"F0.wireOp",EDGE,"E7.1"),sQuery(id+"F0.wireOp",EDGE,"E7.2"),sQuery(id+"F0.wireOp",EDGE,"E7.3"),sQuery(id+"F0.wireOp",EDGE,"E7.4"),sQuery(id+"F0.wireOp",EDGE,"E7.5"),sQuery(id+"F0.wireOp",EDGE,"E8.0"),sQuery(id+"F0.wireOp",EDGE,"E8.1"),sQuery(id+"F0.wireOp",EDGE,"E8.2"),sQuery(id+"F0.wireOp",EDGE,"E8.3"),sQuery(id+"F0.wireOp",EDGE,"E8.4"),sQuery(id+"F0.wireOp",EDGE,"E8.5"),sQuery(id+"F0.wireOp",EDGE,"E9"),sQuery(id+"F0.wireOp",EDGE,"E10"),sQuery(id+"F0.wireOp",EDGE,"E11"),subQ0,sQuery(id+"F0.wireOp",EDGE,"E13"),sQuery(id+"F0.wireOp",EDGE,"E14"),sQuery(id+"F0.wireOp",EDGE,"E15"),sQuery(id+"F0.wireOp",EDGE,"E16"),sQuery(id+"F0.wireOp",EDGE,"E19.trimOffspring"),sQuery(id+"F0.wireOp",EDGE,"E20.trimOffspring"),sQuery(id+"F0.wireOp",EDGE,"E23.trimOffspring"),sQuery(id+"F0.wireOp",EDGE,"E26.trimOffspring"),sQuery(id+"F0.wireOp",EDGE,"E27.trimOffspring"),sQuery(id+"F0.wireOp",EDGE,"E31.trimOffspring"),sQuery(id+"F0.wireOp",EDGE,"E34.trimOffspring")])],"isStart":true})]});}
            var Q239;
            {var subQ0=sQuery(id+"F0.wireOp",EDGE,"E12");Q239=makeQuery(id+"F2.opFillet","BLEND_EDGE",EDGE,{"blendedFrom":[makeQuery(id+"F1.opExtrude","CAP_EDGE",EDGE,{"disambiguationData":[OSD([subQ0])],"isStart":true}),makeQuery(id+"F1.opExtrude","SWEPT_FACE",FACE,{"disambiguationData":[OSD([subQ0])]})],"blendedInto":[makeQuery(id+"F1.opExtrude","SWEPT_FACE",FACE,{"disambiguationData":[OSD([subQ0])]})]});}
            var Q240;
            {var subQ0=sQuery(id+"F0.wireOp",EDGE,"E12");Q240=makeQuery(id+"F2.opFillet","BLEND_EDGE",EDGE,{"blendedFrom":[makeQuery(id+"F1.opExtrude","CAP_EDGE",EDGE,{"disambiguationData":[OSD([subQ0])],"isStart":false}),makeQuery(id+"F1.opExtrude","SWEPT_FACE",FACE,{"disambiguationData":[OSD([subQ0])]})],"blendedInto":[makeQuery(id+"F1.opExtrude","SWEPT_FACE",FACE,{"disambiguationData":[OSD([subQ0])]})]});}
            var Q241;
            {var subQ0=sQuery(id+"F0.wireOp",EDGE,"E12");Q241=makeQuery(id+"F2.opFillet","BLEND_EDGE",EDGE,{"blendedFrom":[makeQuery(id+"F1.opExtrude","CAP_EDGE",EDGE,{"disambiguationData":[OSD([subQ0])],"isStart":false}),makeQuery(id+"F1.opExtrude","CAP_FACE",FACE,{"disambiguationData":[OSD([sQuery(id+"F0.wireOp",EDGE,"E0"),sQuery(id+"F0.wireOp",EDGE,"E2"),sQuery(id+"F0.wireOp",EDGE,"E5.0"),sQuery(id+"F0.wireOp",EDGE,"E5.1"),sQuery(id+"F0.wireOp",EDGE,"E5.2"),sQuery(id+"F0.wireOp",EDGE,"E5.3"),sQuery(id+"F0.wireOp",EDGE,"E5.4"),sQuery(id+"F0.wireOp",EDGE,"E5.5"),sQuery(id+"F0.wireOp",EDGE,"E6.0"),sQuery(id+"F0.wireOp",EDGE,"E6.1"),sQuery(id+"F0.wireOp",EDGE,"E6.2"),sQuery(id+"F0.wireOp",EDGE,"E6.3"),sQuery(id+"F0.wireOp",EDGE,"E6.4"),sQuery(id+"F0.wireOp",EDGE,"E6.5"),sQuery(id+"F0.wireOp",EDGE,"E7.0"),sQuery(id+"F0.wireOp",EDGE,"E7.1"),sQuery(id+"F0.wireOp",EDGE,"E7.2"),sQuery(id+"F0.wireOp",EDGE,"E7.3"),sQuery(id+"F0.wireOp",EDGE,"E7.4"),sQuery(id+"F0.wireOp",EDGE,"E7.5"),sQuery(id+"F0.wireOp",EDGE,"E8.0"),sQuery(id+"F0.wireOp",EDGE,"E8.1"),sQuery(id+"F0.wireOp",EDGE,"E8.2"),sQuery(id+"F0.wireOp",EDGE,"E8.3"),sQuery(id+"F0.wireOp",EDGE,"E8.4"),sQuery(id+"F0.wireOp",EDGE,"E8.5"),sQuery(id+"F0.wireOp",EDGE,"E9"),sQuery(id+"F0.wireOp",EDGE,"E10"),sQuery(id+"F0.wireOp",EDGE,"E11"),subQ0,sQuery(id+"F0.wireOp",EDGE,"E13"),sQuery(id+"F0.wireOp",EDGE,"E14"),sQuery(id+"F0.wireOp",EDGE,"E15"),sQuery(id+"F0.wireOp",EDGE,"E16"),sQuery(id+"F0.wireOp",EDGE,"E19.trimOffspring"),sQuery(id+"F0.wireOp",EDGE,"E20.trimOffspring"),sQuery(id+"F0.wireOp",EDGE,"E23.trimOffspring"),sQuery(id+"F0.wireOp",EDGE,"E26.trimOffspring"),sQuery(id+"F0.wireOp",EDGE,"E27.trimOffspring"),sQuery(id+"F0.wireOp",EDGE,"E31.trimOffspring"),sQuery(id+"F0.wireOp",EDGE,"E34.trimOffspring")])],"isStart":false})],"blendedInto":[makeQuery(id+"F1.opExtrude","CAP_FACE",FACE,{"disambiguationData":[OSD([sQuery(id+"F0.wireOp",EDGE,"E0"),sQuery(id+"F0.wireOp",EDGE,"E2"),sQuery(id+"F0.wireOp",EDGE,"E5.0"),sQuery(id+"F0.wireOp",EDGE,"E5.1"),sQuery(id+"F0.wireOp",EDGE,"E5.2"),sQuery(id+"F0.wireOp",EDGE,"E5.3"),sQuery(id+"F0.wireOp",EDGE,"E5.4"),sQuery(id+"F0.wireOp",EDGE,"E5.5"),sQuery(id+"F0.wireOp",EDGE,"E6.0"),sQuery(id+"F0.wireOp",EDGE,"E6.1"),sQuery(id+"F0.wireOp",EDGE,"E6.2"),sQuery(id+"F0.wireOp",EDGE,"E6.3"),sQuery(id+"F0.wireOp",EDGE,"E6.4"),sQuery(id+"F0.wireOp",EDGE,"E6.5"),sQuery(id+"F0.wireOp",EDGE,"E7.0"),sQuery(id+"F0.wireOp",EDGE,"E7.1"),sQuery(id+"F0.wireOp",EDGE,"E7.2"),sQuery(id+"F0.wireOp",EDGE,"E7.3"),sQuery(id+"F0.wireOp",EDGE,"E7.4"),sQuery(id+"F0.wireOp",EDGE,"E7.5"),sQuery(id+"F0.wireOp",EDGE,"E8.0"),sQuery(id+"F0.wireOp",EDGE,"E8.1"),sQuery(id+"F0.wireOp",EDGE,"E8.2"),sQuery(id+"F0.wireOp",EDGE,"E8.3"),sQuery(id+"F0.wireOp",EDGE,"E8.4"),sQuery(id+"F0.wireOp",EDGE,"E8.5"),sQuery(id+"F0.wireOp",EDGE,"E9"),sQuery(id+"F0.wireOp",EDGE,"E10"),sQuery(id+"F0.wireOp",EDGE,"E11"),subQ0,sQuery(id+"F0.wireOp",EDGE,"E13"),sQuery(id+"F0.wireOp",EDGE,"E14"),sQuery(id+"F0.wireOp",EDGE,"E15"),sQuery(id+"F0.wireOp",EDGE,"E16"),sQuery(id+"F0.wireOp",EDGE,"E19.trimOffspring"),sQuery(id+"F0.wireOp",EDGE,"E20.trimOffspring"),sQuery(id+"F0.wireOp",EDGE,"E23.trimOffspring"),sQuery(id+"F0.wireOp",EDGE,"E26.trimOffspring"),sQuery(id+"F0.wireOp",EDGE,"E27.trimOffspring"),sQuery(id+"F0.wireOp",EDGE,"E31.trimOffspring"),sQuery(id+"F0.wireOp",EDGE,"E34.trimOffspring")])],"isStart":false})]});}
            chamfer(context, id + "F3", {"entities" : qUnion([Q0, Q1, Q2, Q3, Q4, Q5, Q6, Q7, Q8, Q9, Q10, Q11, Q12, Q13, Q14, Q15, Q16, Q17, Q18, Q19, Q20, Q21, Q22, Q23, Q24, Q25, Q26, Q27, Q28, Q29, Q30, Q31, Q32, Q33, Q34, Q35, Q36, Q37, Q38, Q39, Q40, Q41, Q42, Q43, Q44, Q45, Q46, Q47, Q48, Q49, Q50, Q51, Q52, Q53, Q54, Q55, Q56, Q57, Q58, Q59, Q60, Q61, Q62, Q63, Q64, Q65, Q66, Q67, Q68, Q69, Q70, Q71, Q72, Q73, Q74, Q75, Q76, Q77, Q78, Q79, Q80, Q81, Q82, Q83, Q84, Q85, Q86, Q87, Q88, Q89, Q90, Q91, Q92, Q93, Q94, Q95, Q96, Q97, Q98, Q99, Q100, Q101, Q102, Q103, Q104, Q105, Q106, Q107, Q108, Q109, Q110, Q111, Q112, Q113, Q114, Q115, Q116, Q117, Q118, Q119, Q120, Q121, Q122, Q123, Q124, Q125, Q126, Q127, Q128, Q129, Q130, Q131, Q132, Q133, Q134, Q135, Q136, Q137, Q138, Q139, Q140, Q141, Q142, Q143, Q144, Q145, Q146, Q147, Q148, Q149, Q150, Q151, Q152, Q153, Q154, Q155, Q156, Q157, Q158, Q159, Q160, Q161, Q162, Q163, Q164, Q165, Q166, Q167, Q168, Q169, Q170, Q171, Q172, Q173, Q174, Q175, Q176, Q177, Q178, Q179, Q180, Q181, Q182, Q183, Q184, Q185, Q186, Q187, Q188, Q189, Q190, Q191, Q192, Q193, Q194, Q195, Q196, Q197, Q198, Q199, Q200, Q201, Q202, Q203, Q204, Q205, Q206, Q207, Q208, Q209, Q210, Q211, Q212, Q213, Q214, Q215, Q216, Q217, Q218, Q219, Q220, Q221, Q222, Q223, Q224, Q225, Q226, Q227, Q228, Q229, Q230, Q231, Q232, Q233, Q234, Q235, Q236, Q237, Q238, Q239, Q240, Q241]), "width" : 1 * mm, "tangentPropagation" : true});
        }
    });
